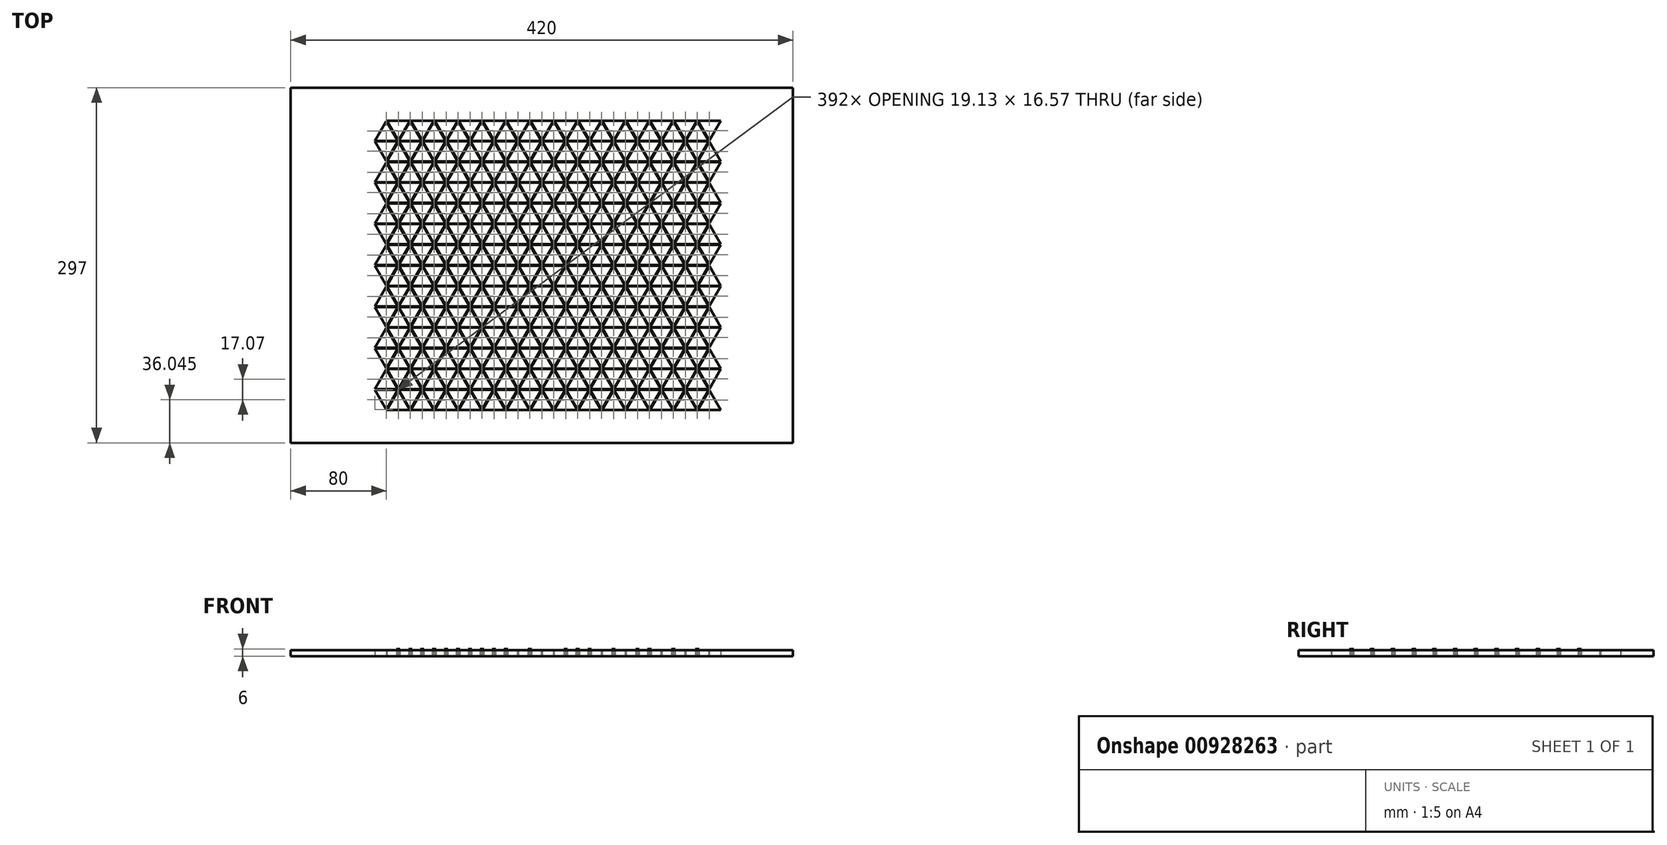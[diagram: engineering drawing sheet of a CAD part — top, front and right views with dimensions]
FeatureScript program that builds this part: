
annotation { "Feature Type Name" : "Feature", "Feature Type Description" : "" }
export const myFeature = defineFeature(function(context is Context, id is Id, definition is map)
    precondition{}
    {
        {
            var Q0;
            Q0=qCreatedBy(makeId("Top.planeOp"),FACE);
            var sketch = newSketch(context, id + "F0", { "sketchPlane" : qUnion([Q0])});
            skLineSegment(sketch, "E0", {"start": v(0, 0) * mm, "end": v(20, 0) * mm, "construction": true});
            skLineSegment(sketch, "E1", {"start": v(20, 0) * mm, "end": v(10, 17.32) * mm, "construction": true});
            skLineSegment(sketch, "E2", {"start": v(10, 17.32) * mm, "end": v(0, 0) * mm, "construction": true});
            skLineSegment(sketch, "E3.MirrorCS", {"start": v(10, -17.32) * mm, "end": v(0, 0) * mm, "construction": true});
            skLineSegment(sketch, "E4.MirrorCS", {"start": v(20, 0) * mm, "end": v(10, -17.32) * mm, "construction": true});
            skLineSegment(sketch, "E5.MirrorCS", {"start": v(30, -17.32) * mm, "end": v(20, 0) * mm, "construction": true});
            skLineSegment(sketch, "E6.MirrorCS", {"start": v(10, -17.32) * mm, "end": v(30, -17.32) * mm, "construction": true});
            skLineSegment(sketch, "E7.MirrorCS", {"start": v(30, 17.32) * mm, "end": v(20, 0) * mm, "construction": true});
            skLineSegment(sketch, "E8.MirrorCS", {"start": v(10, 17.32) * mm, "end": v(30, 17.32) * mm, "construction": true});
            skLineSegment(sketch, "E9.0.1.1", {"start": v(20, 34.64) * mm, "end": v(10, 17.32) * mm, "construction": true});
            skLineSegment(sketch, "E9.0.1.2", {"start": v(30, 17.32) * mm, "end": v(20, 34.64) * mm, "construction": true});
            skLineSegment(sketch, "E9.0.1.3", {"start": v(0, 34.64) * mm, "end": v(20, 34.64) * mm, "construction": true});
            skLineSegment(sketch, "E9.0.1.4", {"start": v(10, 17.32) * mm, "end": v(0, 34.64) * mm, "construction": true});
            skLineSegment(sketch, "E9.0.1.5", {"start": v(10, 51.96) * mm, "end": v(0, 34.64) * mm, "construction": true});
            skLineSegment(sketch, "E9.0.1.6", {"start": v(20, 34.64) * mm, "end": v(10, 51.96) * mm, "construction": true});
            skLineSegment(sketch, "E9.0.1.7", {"start": v(10, 51.96) * mm, "end": v(30, 51.96) * mm, "construction": true});
            skLineSegment(sketch, "E9.0.1.8", {"start": v(30, 51.96) * mm, "end": v(20, 34.64) * mm, "construction": true});
            skLineSegment(sketch, "E9.0.2.0", {"start": v(10, 51.96) * mm, "end": v(30, 51.96) * mm, "construction": true});
            skLineSegment(sketch, "E9.0.2.1", {"start": v(20, 69.28) * mm, "end": v(10, 51.96) * mm, "construction": true});
            skLineSegment(sketch, "E9.0.2.2", {"start": v(30, 51.96) * mm, "end": v(20, 69.28) * mm, "construction": true});
            skLineSegment(sketch, "E9.0.2.3", {"start": v(0, 69.28) * mm, "end": v(20, 69.28) * mm, "construction": true});
            skLineSegment(sketch, "E9.0.2.4", {"start": v(10, 51.96) * mm, "end": v(0, 69.28) * mm, "construction": true});
            skLineSegment(sketch, "E9.0.2.5", {"start": v(10, 86.6) * mm, "end": v(0, 69.28) * mm, "construction": true});
            skLineSegment(sketch, "E9.0.2.6", {"start": v(20, 69.28) * mm, "end": v(10, 86.6) * mm, "construction": true});
            skLineSegment(sketch, "E9.0.2.7", {"start": v(10, 86.6) * mm, "end": v(30, 86.6) * mm, "construction": true});
            skLineSegment(sketch, "E9.0.2.8", {"start": v(30, 86.6) * mm, "end": v(20, 69.28) * mm, "construction": true});
            skLineSegment(sketch, "E9.0.3.0", {"start": v(10, 86.6) * mm, "end": v(30, 86.6) * mm, "construction": true});
            skLineSegment(sketch, "E9.0.3.1", {"start": v(20, 103.92) * mm, "end": v(10, 86.6) * mm, "construction": true});
            skLineSegment(sketch, "E9.0.3.2", {"start": v(30, 86.6) * mm, "end": v(20, 103.92) * mm, "construction": true});
            skLineSegment(sketch, "E9.0.3.3", {"start": v(0, 103.92) * mm, "end": v(20, 103.92) * mm, "construction": true});
            skLineSegment(sketch, "E9.0.3.4", {"start": v(10, 86.6) * mm, "end": v(0, 103.92) * mm, "construction": true});
            skLineSegment(sketch, "E9.0.3.5", {"start": v(10, 121.24) * mm, "end": v(0, 103.92) * mm, "construction": true});
            skLineSegment(sketch, "E9.0.3.6", {"start": v(20, 103.92) * mm, "end": v(10, 121.24) * mm, "construction": true});
            skLineSegment(sketch, "E9.0.3.7", {"start": v(10, 121.24) * mm, "end": v(30, 121.24) * mm, "construction": true});
            skLineSegment(sketch, "E9.0.3.8", {"start": v(30, 121.24) * mm, "end": v(20, 103.92) * mm, "construction": true});
            skLineSegment(sketch, "E9.0.4.0", {"start": v(10, 121.24) * mm, "end": v(30, 121.24) * mm, "construction": true});
            skLineSegment(sketch, "E9.0.4.1", {"start": v(20, 138.56) * mm, "end": v(10, 121.24) * mm, "construction": true});
            skLineSegment(sketch, "E9.0.4.2", {"start": v(30, 121.24) * mm, "end": v(20, 138.56) * mm, "construction": true});
            skLineSegment(sketch, "E9.0.4.3", {"start": v(0, 138.56) * mm, "end": v(20, 138.56) * mm, "construction": true});
            skLineSegment(sketch, "E9.0.4.4", {"start": v(10, 121.24) * mm, "end": v(0, 138.56) * mm, "construction": true});
            skLineSegment(sketch, "E9.0.4.5", {"start": v(10, 155.88) * mm, "end": v(0, 138.56) * mm, "construction": true});
            skLineSegment(sketch, "E9.0.4.6", {"start": v(20, 138.56) * mm, "end": v(10, 155.88) * mm, "construction": true});
            skLineSegment(sketch, "E9.0.4.7", {"start": v(10, 155.88) * mm, "end": v(30, 155.88) * mm, "construction": true});
            skLineSegment(sketch, "E9.0.4.8", {"start": v(30, 155.88) * mm, "end": v(20, 138.56) * mm, "construction": true});
            skLineSegment(sketch, "E9.0.5.0", {"start": v(10, 155.88) * mm, "end": v(30, 155.88) * mm, "construction": true});
            skLineSegment(sketch, "E9.0.5.1", {"start": v(20, 173.2) * mm, "end": v(10, 155.88) * mm, "construction": true});
            skLineSegment(sketch, "E9.0.5.2", {"start": v(30, 155.88) * mm, "end": v(20, 173.2) * mm, "construction": true});
            skLineSegment(sketch, "E9.0.5.3", {"start": v(0, 173.2) * mm, "end": v(20, 173.2) * mm, "construction": true});
            skLineSegment(sketch, "E9.0.5.4", {"start": v(10, 155.88) * mm, "end": v(0, 173.2) * mm, "construction": true});
            skLineSegment(sketch, "E9.0.5.5", {"start": v(10, 190.53) * mm, "end": v(0, 173.2) * mm, "construction": true});
            skLineSegment(sketch, "E9.0.5.6", {"start": v(20, 173.2) * mm, "end": v(10, 190.53) * mm, "construction": true});
            skLineSegment(sketch, "E9.0.5.7", {"start": v(10, 190.53) * mm, "end": v(30, 190.53) * mm, "construction": true});
            skLineSegment(sketch, "E9.0.5.8", {"start": v(30, 190.53) * mm, "end": v(20, 173.2) * mm, "construction": true});
            skLineSegment(sketch, "E9.0.6.0", {"start": v(10, 190.53) * mm, "end": v(30, 190.53) * mm, "construction": true});
            skLineSegment(sketch, "E9.0.6.1", {"start": v(20, 207.85) * mm, "end": v(10, 190.53) * mm, "construction": true});
            skLineSegment(sketch, "E9.0.6.2", {"start": v(30, 190.53) * mm, "end": v(20, 207.85) * mm, "construction": true});
            skLineSegment(sketch, "E9.0.6.3", {"start": v(0, 207.85) * mm, "end": v(20, 207.85) * mm, "construction": true});
            skLineSegment(sketch, "E9.0.6.4", {"start": v(10, 190.53) * mm, "end": v(0, 207.85) * mm, "construction": true});
            skLineSegment(sketch, "E9.0.6.5", {"start": v(10, 225.17) * mm, "end": v(0, 207.85) * mm, "construction": true});
            skLineSegment(sketch, "E9.0.6.6", {"start": v(20, 207.85) * mm, "end": v(10, 225.17) * mm, "construction": true});
            skLineSegment(sketch, "E9.0.6.7", {"start": v(10, 225.17) * mm, "end": v(30, 225.17) * mm, "construction": true});
            skLineSegment(sketch, "E9.0.6.8", {"start": v(30, 225.17) * mm, "end": v(20, 207.85) * mm, "construction": true});
            skLineSegment(sketch, "E9.1.0.0", {"start": v(30, -17.32) * mm, "end": v(50, -17.32) * mm, "construction": true});
            skLineSegment(sketch, "E9.1.0.1", {"start": v(40, 0) * mm, "end": v(30, -17.32) * mm, "construction": true});
            skLineSegment(sketch, "E9.1.0.2", {"start": v(50, -17.32) * mm, "end": v(40, 0) * mm, "construction": true});
            skLineSegment(sketch, "E9.1.0.3", {"start": v(20, 0) * mm, "end": v(40, 0) * mm, "construction": true});
            skLineSegment(sketch, "E9.1.0.6", {"start": v(40, 0) * mm, "end": v(30, 17.32) * mm, "construction": true});
            skLineSegment(sketch, "E9.1.0.7", {"start": v(30, 17.32) * mm, "end": v(50, 17.32) * mm, "construction": true});
            skLineSegment(sketch, "E9.1.0.8", {"start": v(50, 17.32) * mm, "end": v(40, 0) * mm, "construction": true});
            skLineSegment(sketch, "E9.1.1.0", {"start": v(30, 17.32) * mm, "end": v(50, 17.32) * mm, "construction": true});
            skLineSegment(sketch, "E9.1.1.1", {"start": v(40, 34.64) * mm, "end": v(30, 17.32) * mm, "construction": true});
            skLineSegment(sketch, "E9.1.1.2", {"start": v(50, 17.32) * mm, "end": v(40, 34.64) * mm, "construction": true});
            skLineSegment(sketch, "E9.1.1.3", {"start": v(20, 34.64) * mm, "end": v(40, 34.64) * mm, "construction": true});
            skLineSegment(sketch, "E9.1.1.4", {"start": v(30, 17.32) * mm, "end": v(20, 34.64) * mm, "construction": true});
            skLineSegment(sketch, "E9.1.1.5", {"start": v(30, 51.96) * mm, "end": v(20, 34.64) * mm, "construction": true});
            skLineSegment(sketch, "E9.1.1.6", {"start": v(40, 34.64) * mm, "end": v(30, 51.96) * mm, "construction": true});
            skLineSegment(sketch, "E9.1.1.7", {"start": v(30, 51.96) * mm, "end": v(50, 51.96) * mm, "construction": true});
            skLineSegment(sketch, "E9.1.1.8", {"start": v(50, 51.96) * mm, "end": v(40, 34.64) * mm, "construction": true});
            skLineSegment(sketch, "E9.1.2.0", {"start": v(30, 51.96) * mm, "end": v(50, 51.96) * mm, "construction": true});
            skLineSegment(sketch, "E9.1.2.1", {"start": v(40, 69.28) * mm, "end": v(30, 51.96) * mm, "construction": true});
            skLineSegment(sketch, "E9.1.2.2", {"start": v(50, 51.96) * mm, "end": v(40, 69.28) * mm, "construction": true});
            skLineSegment(sketch, "E9.1.2.3", {"start": v(20, 69.28) * mm, "end": v(40, 69.28) * mm, "construction": true});
            skLineSegment(sketch, "E9.1.2.4", {"start": v(30, 51.96) * mm, "end": v(20, 69.28) * mm, "construction": true});
            skLineSegment(sketch, "E9.1.2.5", {"start": v(30, 86.6) * mm, "end": v(20, 69.28) * mm, "construction": true});
            skLineSegment(sketch, "E9.1.2.6", {"start": v(40, 69.28) * mm, "end": v(30, 86.6) * mm, "construction": true});
            skLineSegment(sketch, "E9.1.2.7", {"start": v(30, 86.6) * mm, "end": v(50, 86.6) * mm, "construction": true});
            skLineSegment(sketch, "E9.1.2.8", {"start": v(50, 86.6) * mm, "end": v(40, 69.28) * mm, "construction": true});
            skLineSegment(sketch, "E9.1.3.0", {"start": v(30, 86.6) * mm, "end": v(50, 86.6) * mm, "construction": true});
            skLineSegment(sketch, "E9.1.3.1", {"start": v(40, 103.92) * mm, "end": v(30, 86.6) * mm, "construction": true});
            skLineSegment(sketch, "E9.1.3.2", {"start": v(50, 86.6) * mm, "end": v(40, 103.92) * mm, "construction": true});
            skLineSegment(sketch, "E9.1.3.3", {"start": v(20, 103.92) * mm, "end": v(40, 103.92) * mm, "construction": true});
            skLineSegment(sketch, "E9.1.3.4", {"start": v(30, 86.6) * mm, "end": v(20, 103.92) * mm, "construction": true});
            skLineSegment(sketch, "E9.1.3.5", {"start": v(30, 121.24) * mm, "end": v(20, 103.92) * mm, "construction": true});
            skLineSegment(sketch, "E9.1.3.6", {"start": v(40, 103.92) * mm, "end": v(30, 121.24) * mm, "construction": true});
            skLineSegment(sketch, "E9.1.3.7", {"start": v(30, 121.24) * mm, "end": v(50, 121.24) * mm, "construction": true});
            skLineSegment(sketch, "E9.1.3.8", {"start": v(50, 121.24) * mm, "end": v(40, 103.92) * mm, "construction": true});
            skLineSegment(sketch, "E9.1.4.0", {"start": v(30, 121.24) * mm, "end": v(50, 121.24) * mm, "construction": true});
            skLineSegment(sketch, "E9.1.4.1", {"start": v(40, 138.56) * mm, "end": v(30, 121.24) * mm, "construction": true});
            skLineSegment(sketch, "E9.1.4.2", {"start": v(50, 121.24) * mm, "end": v(40, 138.56) * mm, "construction": true});
            skLineSegment(sketch, "E9.1.4.3", {"start": v(20, 138.56) * mm, "end": v(40, 138.56) * mm, "construction": true});
            skLineSegment(sketch, "E9.1.4.4", {"start": v(30, 121.24) * mm, "end": v(20, 138.56) * mm, "construction": true});
            skLineSegment(sketch, "E9.1.4.5", {"start": v(30, 155.88) * mm, "end": v(20, 138.56) * mm, "construction": true});
            skLineSegment(sketch, "E9.1.4.6", {"start": v(40, 138.56) * mm, "end": v(30, 155.88) * mm, "construction": true});
            skLineSegment(sketch, "E9.1.4.7", {"start": v(30, 155.88) * mm, "end": v(50, 155.88) * mm, "construction": true});
            skLineSegment(sketch, "E9.1.4.8", {"start": v(50, 155.88) * mm, "end": v(40, 138.56) * mm, "construction": true});
            skLineSegment(sketch, "E9.1.5.0", {"start": v(30, 155.88) * mm, "end": v(50, 155.88) * mm, "construction": true});
            skLineSegment(sketch, "E9.1.5.1", {"start": v(40, 173.2) * mm, "end": v(30, 155.88) * mm, "construction": true});
            skLineSegment(sketch, "E9.1.5.2", {"start": v(50, 155.88) * mm, "end": v(40, 173.2) * mm, "construction": true});
            skLineSegment(sketch, "E9.1.5.3", {"start": v(20, 173.2) * mm, "end": v(40, 173.2) * mm, "construction": true});
            skLineSegment(sketch, "E9.1.5.4", {"start": v(30, 155.88) * mm, "end": v(20, 173.2) * mm, "construction": true});
            skLineSegment(sketch, "E9.1.5.5", {"start": v(30, 190.53) * mm, "end": v(20, 173.2) * mm, "construction": true});
            skLineSegment(sketch, "E9.1.5.6", {"start": v(40, 173.2) * mm, "end": v(30, 190.53) * mm, "construction": true});
            skLineSegment(sketch, "E9.1.5.7", {"start": v(30, 190.53) * mm, "end": v(50, 190.53) * mm, "construction": true});
            skLineSegment(sketch, "E9.1.5.8", {"start": v(50, 190.53) * mm, "end": v(40, 173.2) * mm, "construction": true});
            skLineSegment(sketch, "E9.1.6.0", {"start": v(30, 190.53) * mm, "end": v(50, 190.53) * mm, "construction": true});
            skLineSegment(sketch, "E9.1.6.1", {"start": v(40, 207.85) * mm, "end": v(30, 190.53) * mm, "construction": true});
            skLineSegment(sketch, "E9.1.6.2", {"start": v(50, 190.53) * mm, "end": v(40, 207.85) * mm, "construction": true});
            skLineSegment(sketch, "E9.1.6.3", {"start": v(20, 207.85) * mm, "end": v(40, 207.85) * mm, "construction": true});
            skLineSegment(sketch, "E9.1.6.4", {"start": v(30, 190.53) * mm, "end": v(20, 207.85) * mm, "construction": true});
            skLineSegment(sketch, "E9.1.6.5", {"start": v(30, 225.17) * mm, "end": v(20, 207.85) * mm, "construction": true});
            skLineSegment(sketch, "E9.1.6.6", {"start": v(40, 207.85) * mm, "end": v(30, 225.17) * mm, "construction": true});
            skLineSegment(sketch, "E9.1.6.7", {"start": v(30, 225.17) * mm, "end": v(50, 225.17) * mm, "construction": true});
            skLineSegment(sketch, "E9.1.6.8", {"start": v(50, 225.17) * mm, "end": v(40, 207.85) * mm, "construction": true});
            skLineSegment(sketch, "E9.2.0.0", {"start": v(50, -17.32) * mm, "end": v(70, -17.32) * mm, "construction": true});
            skLineSegment(sketch, "E9.2.0.1", {"start": v(60, 0) * mm, "end": v(50, -17.32) * mm, "construction": true});
            skLineSegment(sketch, "E9.2.0.2", {"start": v(70, -17.32) * mm, "end": v(60, 0) * mm, "construction": true});
            skLineSegment(sketch, "E9.2.0.3", {"start": v(40, 0) * mm, "end": v(60, 0) * mm, "construction": true});
            skLineSegment(sketch, "E9.2.0.4", {"start": v(50, -17.32) * mm, "end": v(40, 0) * mm, "construction": true});
            skLineSegment(sketch, "E9.2.0.5", {"start": v(50, 17.32) * mm, "end": v(40, 0) * mm, "construction": true});
            skLineSegment(sketch, "E9.2.0.6", {"start": v(60, 0) * mm, "end": v(50, 17.32) * mm, "construction": true});
            skLineSegment(sketch, "E9.2.0.7", {"start": v(50, 17.32) * mm, "end": v(70, 17.32) * mm, "construction": true});
            skLineSegment(sketch, "E9.2.0.8", {"start": v(70, 17.32) * mm, "end": v(60, 0) * mm, "construction": true});
            skLineSegment(sketch, "E9.2.1.0", {"start": v(50, 17.32) * mm, "end": v(70, 17.32) * mm, "construction": true});
            skLineSegment(sketch, "E9.2.1.1", {"start": v(60, 34.64) * mm, "end": v(50, 17.32) * mm, "construction": true});
            skLineSegment(sketch, "E9.2.1.2", {"start": v(70, 17.32) * mm, "end": v(60, 34.64) * mm, "construction": true});
            skLineSegment(sketch, "E9.2.1.3", {"start": v(40, 34.64) * mm, "end": v(60, 34.64) * mm, "construction": true});
            skLineSegment(sketch, "E9.2.1.4", {"start": v(50, 17.32) * mm, "end": v(40, 34.64) * mm, "construction": true});
            skLineSegment(sketch, "E9.2.1.5", {"start": v(50, 51.96) * mm, "end": v(40, 34.64) * mm, "construction": true});
            skLineSegment(sketch, "E9.2.1.6", {"start": v(60, 34.64) * mm, "end": v(50, 51.96) * mm, "construction": true});
            skLineSegment(sketch, "E9.2.1.7", {"start": v(50, 51.96) * mm, "end": v(70, 51.96) * mm, "construction": true});
            skLineSegment(sketch, "E9.2.1.8", {"start": v(70, 51.96) * mm, "end": v(60, 34.64) * mm, "construction": true});
            skLineSegment(sketch, "E9.2.2.0", {"start": v(50, 51.96) * mm, "end": v(70, 51.96) * mm, "construction": true});
            skLineSegment(sketch, "E9.2.2.1", {"start": v(60, 69.28) * mm, "end": v(50, 51.96) * mm, "construction": true});
            skLineSegment(sketch, "E9.2.2.2", {"start": v(70, 51.96) * mm, "end": v(60, 69.28) * mm, "construction": true});
            skLineSegment(sketch, "E9.2.2.3", {"start": v(40, 69.28) * mm, "end": v(60, 69.28) * mm, "construction": true});
            skLineSegment(sketch, "E9.2.2.4", {"start": v(50, 51.96) * mm, "end": v(40, 69.28) * mm, "construction": true});
            skLineSegment(sketch, "E9.2.2.5", {"start": v(50, 86.6) * mm, "end": v(40, 69.28) * mm, "construction": true});
            skLineSegment(sketch, "E9.2.2.6", {"start": v(60, 69.28) * mm, "end": v(50, 86.6) * mm, "construction": true});
            skLineSegment(sketch, "E9.2.2.7", {"start": v(50, 86.6) * mm, "end": v(70, 86.6) * mm, "construction": true});
            skLineSegment(sketch, "E9.2.2.8", {"start": v(70, 86.6) * mm, "end": v(60, 69.28) * mm, "construction": true});
            skLineSegment(sketch, "E9.2.3.0", {"start": v(50, 86.6) * mm, "end": v(70, 86.6) * mm, "construction": true});
            skLineSegment(sketch, "E9.2.3.1", {"start": v(60, 103.92) * mm, "end": v(50, 86.6) * mm, "construction": true});
            skLineSegment(sketch, "E9.2.3.2", {"start": v(70, 86.6) * mm, "end": v(60, 103.92) * mm, "construction": true});
            skLineSegment(sketch, "E9.2.3.3", {"start": v(40, 103.92) * mm, "end": v(60, 103.92) * mm, "construction": true});
            skLineSegment(sketch, "E9.2.3.4", {"start": v(50, 86.6) * mm, "end": v(40, 103.92) * mm, "construction": true});
            skLineSegment(sketch, "E9.2.3.5", {"start": v(50, 121.24) * mm, "end": v(40, 103.92) * mm, "construction": true});
            skLineSegment(sketch, "E9.2.3.6", {"start": v(60, 103.92) * mm, "end": v(50, 121.24) * mm, "construction": true});
            skLineSegment(sketch, "E9.2.3.7", {"start": v(50, 121.24) * mm, "end": v(70, 121.24) * mm, "construction": true});
            skLineSegment(sketch, "E9.2.3.8", {"start": v(70, 121.24) * mm, "end": v(60, 103.92) * mm, "construction": true});
            skLineSegment(sketch, "E9.2.4.0", {"start": v(50, 121.24) * mm, "end": v(70, 121.24) * mm, "construction": true});
            skLineSegment(sketch, "E9.2.4.1", {"start": v(60, 138.56) * mm, "end": v(50, 121.24) * mm, "construction": true});
            skLineSegment(sketch, "E9.2.4.2", {"start": v(70, 121.24) * mm, "end": v(60, 138.56) * mm, "construction": true});
            skLineSegment(sketch, "E9.2.4.3", {"start": v(40, 138.56) * mm, "end": v(60, 138.56) * mm, "construction": true});
            skLineSegment(sketch, "E9.2.4.4", {"start": v(50, 121.24) * mm, "end": v(40, 138.56) * mm, "construction": true});
            skLineSegment(sketch, "E9.2.4.5", {"start": v(50, 155.88) * mm, "end": v(40, 138.56) * mm, "construction": true});
            skLineSegment(sketch, "E9.2.4.6", {"start": v(60, 138.56) * mm, "end": v(50, 155.88) * mm, "construction": true});
            skLineSegment(sketch, "E9.2.4.7", {"start": v(50, 155.88) * mm, "end": v(70, 155.88) * mm, "construction": true});
            skLineSegment(sketch, "E9.2.4.8", {"start": v(70, 155.88) * mm, "end": v(60, 138.56) * mm, "construction": true});
            skLineSegment(sketch, "E9.2.5.0", {"start": v(50, 155.88) * mm, "end": v(70, 155.88) * mm, "construction": true});
            skLineSegment(sketch, "E9.2.5.1", {"start": v(60, 173.2) * mm, "end": v(50, 155.88) * mm, "construction": true});
            skLineSegment(sketch, "E9.2.5.2", {"start": v(70, 155.88) * mm, "end": v(60, 173.2) * mm, "construction": true});
            skLineSegment(sketch, "E9.2.5.3", {"start": v(40, 173.2) * mm, "end": v(60, 173.2) * mm, "construction": true});
            skLineSegment(sketch, "E9.2.5.4", {"start": v(50, 155.88) * mm, "end": v(40, 173.2) * mm, "construction": true});
            skLineSegment(sketch, "E9.2.5.5", {"start": v(50, 190.53) * mm, "end": v(40, 173.2) * mm, "construction": true});
            skLineSegment(sketch, "E9.2.5.6", {"start": v(60, 173.2) * mm, "end": v(50, 190.53) * mm, "construction": true});
            skLineSegment(sketch, "E9.2.5.7", {"start": v(50, 190.53) * mm, "end": v(70, 190.53) * mm, "construction": true});
            skLineSegment(sketch, "E9.2.5.8", {"start": v(70, 190.53) * mm, "end": v(60, 173.2) * mm, "construction": true});
            skLineSegment(sketch, "E9.2.6.0", {"start": v(50, 190.53) * mm, "end": v(70, 190.53) * mm, "construction": true});
            skLineSegment(sketch, "E9.2.6.1", {"start": v(60, 207.85) * mm, "end": v(50, 190.53) * mm, "construction": true});
            skLineSegment(sketch, "E9.2.6.2", {"start": v(70, 190.53) * mm, "end": v(60, 207.85) * mm, "construction": true});
            skLineSegment(sketch, "E9.2.6.3", {"start": v(40, 207.85) * mm, "end": v(60, 207.85) * mm, "construction": true});
            skLineSegment(sketch, "E9.2.6.4", {"start": v(50, 190.53) * mm, "end": v(40, 207.85) * mm, "construction": true});
            skLineSegment(sketch, "E9.2.6.5", {"start": v(50, 225.17) * mm, "end": v(40, 207.85) * mm, "construction": true});
            skLineSegment(sketch, "E9.2.6.6", {"start": v(60, 207.85) * mm, "end": v(50, 225.17) * mm, "construction": true});
            skLineSegment(sketch, "E9.2.6.7", {"start": v(50, 225.17) * mm, "end": v(70, 225.17) * mm, "construction": true});
            skLineSegment(sketch, "E9.2.6.8", {"start": v(70, 225.17) * mm, "end": v(60, 207.85) * mm, "construction": true});
            skLineSegment(sketch, "E9.3.0.0", {"start": v(70, -17.32) * mm, "end": v(90, -17.32) * mm, "construction": true});
            skLineSegment(sketch, "E9.3.0.1", {"start": v(80, 0) * mm, "end": v(70, -17.32) * mm, "construction": true});
            skLineSegment(sketch, "E9.3.0.2", {"start": v(90, -17.32) * mm, "end": v(80, 0) * mm, "construction": true});
            skLineSegment(sketch, "E9.3.0.3", {"start": v(60, 0) * mm, "end": v(80, 0) * mm, "construction": true});
            skLineSegment(sketch, "E9.3.0.4", {"start": v(70, -17.32) * mm, "end": v(60, 0) * mm, "construction": true});
            skLineSegment(sketch, "E9.3.0.5", {"start": v(70, 17.32) * mm, "end": v(60, 0) * mm, "construction": true});
            skLineSegment(sketch, "E9.3.0.6", {"start": v(80, 0) * mm, "end": v(70, 17.32) * mm, "construction": true});
            skLineSegment(sketch, "E9.3.0.7", {"start": v(70, 17.32) * mm, "end": v(90, 17.32) * mm, "construction": true});
            skLineSegment(sketch, "E9.3.0.8", {"start": v(90, 17.32) * mm, "end": v(80, 0) * mm, "construction": true});
            skLineSegment(sketch, "E9.3.1.0", {"start": v(70, 17.32) * mm, "end": v(90, 17.32) * mm, "construction": true});
            skLineSegment(sketch, "E9.3.1.1", {"start": v(80, 34.64) * mm, "end": v(70, 17.32) * mm, "construction": true});
            skLineSegment(sketch, "E9.3.1.2", {"start": v(90, 17.32) * mm, "end": v(80, 34.64) * mm, "construction": true});
            skLineSegment(sketch, "E9.3.1.3", {"start": v(60, 34.64) * mm, "end": v(80, 34.64) * mm, "construction": true});
            skLineSegment(sketch, "E9.3.1.4", {"start": v(70, 17.32) * mm, "end": v(60, 34.64) * mm, "construction": true});
            skLineSegment(sketch, "E9.3.1.5", {"start": v(70, 51.96) * mm, "end": v(60, 34.64) * mm, "construction": true});
            skLineSegment(sketch, "E9.3.1.6", {"start": v(80, 34.64) * mm, "end": v(70, 51.96) * mm, "construction": true});
            skLineSegment(sketch, "E9.3.1.7", {"start": v(70, 51.96) * mm, "end": v(90, 51.96) * mm, "construction": true});
            skLineSegment(sketch, "E9.3.1.8", {"start": v(90, 51.96) * mm, "end": v(80, 34.64) * mm, "construction": true});
            skLineSegment(sketch, "E9.3.2.0", {"start": v(70, 51.96) * mm, "end": v(90, 51.96) * mm, "construction": true});
            skLineSegment(sketch, "E9.3.2.1", {"start": v(80, 69.28) * mm, "end": v(70, 51.96) * mm, "construction": true});
            skLineSegment(sketch, "E9.3.2.2", {"start": v(90, 51.96) * mm, "end": v(80, 69.28) * mm, "construction": true});
            skLineSegment(sketch, "E9.3.2.3", {"start": v(60, 69.28) * mm, "end": v(80, 69.28) * mm, "construction": true});
            skLineSegment(sketch, "E9.3.2.4", {"start": v(70, 51.96) * mm, "end": v(60, 69.28) * mm, "construction": true});
            skLineSegment(sketch, "E9.3.2.5", {"start": v(70, 86.6) * mm, "end": v(60, 69.28) * mm, "construction": true});
            skLineSegment(sketch, "E9.3.2.6", {"start": v(80, 69.28) * mm, "end": v(70, 86.6) * mm, "construction": true});
            skLineSegment(sketch, "E9.3.2.7", {"start": v(70, 86.6) * mm, "end": v(90, 86.6) * mm, "construction": true});
            skLineSegment(sketch, "E9.3.2.8", {"start": v(90, 86.6) * mm, "end": v(80, 69.28) * mm, "construction": true});
            skLineSegment(sketch, "E9.3.3.0", {"start": v(70, 86.6) * mm, "end": v(90, 86.6) * mm, "construction": true});
            skLineSegment(sketch, "E9.3.3.1", {"start": v(80, 103.92) * mm, "end": v(70, 86.6) * mm, "construction": true});
            skLineSegment(sketch, "E9.3.3.2", {"start": v(90, 86.6) * mm, "end": v(80, 103.92) * mm, "construction": true});
            skLineSegment(sketch, "E9.3.3.3", {"start": v(60, 103.92) * mm, "end": v(80, 103.92) * mm, "construction": true});
            skLineSegment(sketch, "E9.3.3.4", {"start": v(70, 86.6) * mm, "end": v(60, 103.92) * mm, "construction": true});
            skLineSegment(sketch, "E9.3.3.5", {"start": v(70, 121.24) * mm, "end": v(60, 103.92) * mm, "construction": true});
            skLineSegment(sketch, "E9.3.3.6", {"start": v(80, 103.92) * mm, "end": v(70, 121.24) * mm, "construction": true});
            skLineSegment(sketch, "E9.3.3.7", {"start": v(70, 121.24) * mm, "end": v(90, 121.24) * mm, "construction": true});
            skLineSegment(sketch, "E9.3.3.8", {"start": v(90, 121.24) * mm, "end": v(80, 103.92) * mm, "construction": true});
            skLineSegment(sketch, "E9.3.4.0", {"start": v(70, 121.24) * mm, "end": v(90, 121.24) * mm, "construction": true});
            skLineSegment(sketch, "E9.3.4.1", {"start": v(80, 138.56) * mm, "end": v(70, 121.24) * mm, "construction": true});
            skLineSegment(sketch, "E9.3.4.2", {"start": v(90, 121.24) * mm, "end": v(80, 138.56) * mm, "construction": true});
            skLineSegment(sketch, "E9.3.4.3", {"start": v(60, 138.56) * mm, "end": v(80, 138.56) * mm, "construction": true});
            skLineSegment(sketch, "E9.3.4.4", {"start": v(70, 121.24) * mm, "end": v(60, 138.56) * mm, "construction": true});
            skLineSegment(sketch, "E9.3.4.5", {"start": v(70, 155.88) * mm, "end": v(60, 138.56) * mm, "construction": true});
            skLineSegment(sketch, "E9.3.4.6", {"start": v(80, 138.56) * mm, "end": v(70, 155.88) * mm, "construction": true});
            skLineSegment(sketch, "E9.3.4.7", {"start": v(70, 155.88) * mm, "end": v(90, 155.88) * mm, "construction": true});
            skLineSegment(sketch, "E9.3.4.8", {"start": v(90, 155.88) * mm, "end": v(80, 138.56) * mm, "construction": true});
            skLineSegment(sketch, "E9.3.5.0", {"start": v(70, 155.88) * mm, "end": v(90, 155.88) * mm, "construction": true});
            skLineSegment(sketch, "E9.3.5.1", {"start": v(80, 173.2) * mm, "end": v(70, 155.88) * mm, "construction": true});
            skLineSegment(sketch, "E9.3.5.2", {"start": v(90, 155.88) * mm, "end": v(80, 173.2) * mm, "construction": true});
            skLineSegment(sketch, "E9.3.5.3", {"start": v(60, 173.2) * mm, "end": v(80, 173.2) * mm, "construction": true});
            skLineSegment(sketch, "E9.3.5.4", {"start": v(70, 155.88) * mm, "end": v(60, 173.2) * mm, "construction": true});
            skLineSegment(sketch, "E9.3.5.5", {"start": v(70, 190.53) * mm, "end": v(60, 173.2) * mm, "construction": true});
            skLineSegment(sketch, "E9.3.5.6", {"start": v(80, 173.2) * mm, "end": v(70, 190.53) * mm, "construction": true});
            skLineSegment(sketch, "E9.3.5.7", {"start": v(70, 190.53) * mm, "end": v(90, 190.53) * mm, "construction": true});
            skLineSegment(sketch, "E9.3.5.8", {"start": v(90, 190.53) * mm, "end": v(80, 173.2) * mm, "construction": true});
            skLineSegment(sketch, "E9.3.6.0", {"start": v(70, 190.53) * mm, "end": v(90, 190.53) * mm, "construction": true});
            skLineSegment(sketch, "E9.3.6.1", {"start": v(80, 207.85) * mm, "end": v(70, 190.53) * mm, "construction": true});
            skLineSegment(sketch, "E9.3.6.2", {"start": v(90, 190.53) * mm, "end": v(80, 207.85) * mm, "construction": true});
            skLineSegment(sketch, "E9.3.6.3", {"start": v(60, 207.85) * mm, "end": v(80, 207.85) * mm, "construction": true});
            skLineSegment(sketch, "E9.3.6.4", {"start": v(70, 190.53) * mm, "end": v(60, 207.85) * mm, "construction": true});
            skLineSegment(sketch, "E9.3.6.5", {"start": v(70, 225.17) * mm, "end": v(60, 207.85) * mm, "construction": true});
            skLineSegment(sketch, "E9.3.6.6", {"start": v(80, 207.85) * mm, "end": v(70, 225.17) * mm, "construction": true});
            skLineSegment(sketch, "E9.3.6.7", {"start": v(70, 225.17) * mm, "end": v(90, 225.17) * mm, "construction": true});
            skLineSegment(sketch, "E9.3.6.8", {"start": v(90, 225.17) * mm, "end": v(80, 207.85) * mm, "construction": true});
            skLineSegment(sketch, "E9.4.0.0", {"start": v(90, -17.32) * mm, "end": v(110, -17.32) * mm, "construction": true});
            skLineSegment(sketch, "E9.4.0.1", {"start": v(100, 0) * mm, "end": v(90, -17.32) * mm, "construction": true});
            skLineSegment(sketch, "E9.4.0.2", {"start": v(110, -17.32) * mm, "end": v(100, 0) * mm, "construction": true});
            skLineSegment(sketch, "E9.4.0.3", {"start": v(80, 0) * mm, "end": v(100, 0) * mm, "construction": true});
            skLineSegment(sketch, "E9.4.0.4", {"start": v(90, -17.32) * mm, "end": v(80, 0) * mm, "construction": true});
            skLineSegment(sketch, "E9.4.0.5", {"start": v(90, 17.32) * mm, "end": v(80, 0) * mm, "construction": true});
            skLineSegment(sketch, "E9.4.0.6", {"start": v(100, 0) * mm, "end": v(90, 17.32) * mm, "construction": true});
            skLineSegment(sketch, "E9.4.0.7", {"start": v(90, 17.32) * mm, "end": v(110, 17.32) * mm, "construction": true});
            skLineSegment(sketch, "E9.4.0.8", {"start": v(110, 17.32) * mm, "end": v(100, 0) * mm, "construction": true});
            skLineSegment(sketch, "E9.4.1.0", {"start": v(90, 17.32) * mm, "end": v(110, 17.32) * mm, "construction": true});
            skLineSegment(sketch, "E9.4.1.1", {"start": v(100, 34.64) * mm, "end": v(90, 17.32) * mm, "construction": true});
            skLineSegment(sketch, "E9.4.1.2", {"start": v(110, 17.32) * mm, "end": v(100, 34.64) * mm, "construction": true});
            skLineSegment(sketch, "E9.4.1.3", {"start": v(80, 34.64) * mm, "end": v(100, 34.64) * mm, "construction": true});
            skLineSegment(sketch, "E9.4.1.4", {"start": v(90, 17.32) * mm, "end": v(80, 34.64) * mm, "construction": true});
            skLineSegment(sketch, "E9.4.1.5", {"start": v(90, 51.96) * mm, "end": v(80, 34.64) * mm, "construction": true});
            skLineSegment(sketch, "E9.4.1.6", {"start": v(100, 34.64) * mm, "end": v(90, 51.96) * mm, "construction": true});
            skLineSegment(sketch, "E9.4.1.7", {"start": v(90, 51.96) * mm, "end": v(110, 51.96) * mm, "construction": true});
            skLineSegment(sketch, "E9.4.1.8", {"start": v(110, 51.96) * mm, "end": v(100, 34.64) * mm, "construction": true});
            skLineSegment(sketch, "E9.4.2.0", {"start": v(90, 51.96) * mm, "end": v(110, 51.96) * mm, "construction": true});
            skLineSegment(sketch, "E9.4.2.1", {"start": v(100, 69.28) * mm, "end": v(90, 51.96) * mm, "construction": true});
            skLineSegment(sketch, "E9.4.2.2", {"start": v(110, 51.96) * mm, "end": v(100, 69.28) * mm, "construction": true});
            skLineSegment(sketch, "E9.4.2.3", {"start": v(80, 69.28) * mm, "end": v(100, 69.28) * mm, "construction": true});
            skLineSegment(sketch, "E9.4.2.4", {"start": v(90, 51.96) * mm, "end": v(80, 69.28) * mm, "construction": true});
            skLineSegment(sketch, "E9.4.2.5", {"start": v(90, 86.6) * mm, "end": v(80, 69.28) * mm, "construction": true});
            skLineSegment(sketch, "E9.4.2.6", {"start": v(100, 69.28) * mm, "end": v(90, 86.6) * mm, "construction": true});
            skLineSegment(sketch, "E9.4.2.7", {"start": v(90, 86.6) * mm, "end": v(110, 86.6) * mm, "construction": true});
            skLineSegment(sketch, "E9.4.2.8", {"start": v(110, 86.6) * mm, "end": v(100, 69.28) * mm, "construction": true});
            skLineSegment(sketch, "E9.4.3.0", {"start": v(90, 86.6) * mm, "end": v(110, 86.6) * mm, "construction": true});
            skLineSegment(sketch, "E9.4.3.1", {"start": v(100, 103.92) * mm, "end": v(90, 86.6) * mm, "construction": true});
            skLineSegment(sketch, "E9.4.3.2", {"start": v(110, 86.6) * mm, "end": v(100, 103.92) * mm, "construction": true});
            skLineSegment(sketch, "E9.4.3.3", {"start": v(80, 103.92) * mm, "end": v(100, 103.92) * mm, "construction": true});
            skLineSegment(sketch, "E9.4.3.4", {"start": v(90, 86.6) * mm, "end": v(80, 103.92) * mm, "construction": true});
            skLineSegment(sketch, "E9.4.3.5", {"start": v(90, 121.24) * mm, "end": v(80, 103.92) * mm, "construction": true});
            skLineSegment(sketch, "E9.4.3.6", {"start": v(100, 103.92) * mm, "end": v(90, 121.24) * mm, "construction": true});
            skLineSegment(sketch, "E9.4.3.7", {"start": v(90, 121.24) * mm, "end": v(110, 121.24) * mm, "construction": true});
            skLineSegment(sketch, "E9.4.3.8", {"start": v(110, 121.24) * mm, "end": v(100, 103.92) * mm, "construction": true});
            skLineSegment(sketch, "E9.4.4.0", {"start": v(90, 121.24) * mm, "end": v(110, 121.24) * mm, "construction": true});
            skLineSegment(sketch, "E9.4.4.1", {"start": v(100, 138.56) * mm, "end": v(90, 121.24) * mm, "construction": true});
            skLineSegment(sketch, "E9.4.4.2", {"start": v(110, 121.24) * mm, "end": v(100, 138.56) * mm, "construction": true});
            skLineSegment(sketch, "E9.4.4.3", {"start": v(80, 138.56) * mm, "end": v(100, 138.56) * mm, "construction": true});
            skLineSegment(sketch, "E9.4.4.4", {"start": v(90, 121.24) * mm, "end": v(80, 138.56) * mm, "construction": true});
            skLineSegment(sketch, "E9.4.4.5", {"start": v(90, 155.88) * mm, "end": v(80, 138.56) * mm, "construction": true});
            skLineSegment(sketch, "E9.4.4.6", {"start": v(100, 138.56) * mm, "end": v(90, 155.88) * mm, "construction": true});
            skLineSegment(sketch, "E9.4.4.7", {"start": v(90, 155.88) * mm, "end": v(110, 155.88) * mm, "construction": true});
            skLineSegment(sketch, "E9.4.4.8", {"start": v(110, 155.88) * mm, "end": v(100, 138.56) * mm, "construction": true});
            skLineSegment(sketch, "E9.4.5.0", {"start": v(90, 155.88) * mm, "end": v(110, 155.88) * mm, "construction": true});
            skLineSegment(sketch, "E9.4.5.1", {"start": v(100, 173.2) * mm, "end": v(90, 155.88) * mm, "construction": true});
            skLineSegment(sketch, "E9.4.5.2", {"start": v(110, 155.88) * mm, "end": v(100, 173.2) * mm, "construction": true});
            skLineSegment(sketch, "E9.4.5.3", {"start": v(80, 173.2) * mm, "end": v(100, 173.2) * mm, "construction": true});
            skLineSegment(sketch, "E9.4.5.4", {"start": v(90, 155.88) * mm, "end": v(80, 173.2) * mm, "construction": true});
            skLineSegment(sketch, "E9.4.5.5", {"start": v(90, 190.53) * mm, "end": v(80, 173.2) * mm, "construction": true});
            skLineSegment(sketch, "E9.4.5.6", {"start": v(100, 173.2) * mm, "end": v(90, 190.53) * mm, "construction": true});
            skLineSegment(sketch, "E9.4.5.7", {"start": v(90, 190.53) * mm, "end": v(110, 190.53) * mm, "construction": true});
            skLineSegment(sketch, "E9.4.5.8", {"start": v(110, 190.53) * mm, "end": v(100, 173.2) * mm, "construction": true});
            skLineSegment(sketch, "E9.4.6.0", {"start": v(90, 190.53) * mm, "end": v(110, 190.53) * mm, "construction": true});
            skLineSegment(sketch, "E9.4.6.1", {"start": v(100, 207.85) * mm, "end": v(90, 190.53) * mm, "construction": true});
            skLineSegment(sketch, "E9.4.6.2", {"start": v(110, 190.53) * mm, "end": v(100, 207.85) * mm, "construction": true});
            skLineSegment(sketch, "E9.4.6.3", {"start": v(80, 207.85) * mm, "end": v(100, 207.85) * mm, "construction": true});
            skLineSegment(sketch, "E9.4.6.4", {"start": v(90, 190.53) * mm, "end": v(80, 207.85) * mm, "construction": true});
            skLineSegment(sketch, "E9.4.6.5", {"start": v(90, 225.17) * mm, "end": v(80, 207.85) * mm, "construction": true});
            skLineSegment(sketch, "E9.4.6.6", {"start": v(100, 207.85) * mm, "end": v(90, 225.17) * mm, "construction": true});
            skLineSegment(sketch, "E9.4.6.7", {"start": v(90, 225.17) * mm, "end": v(110, 225.17) * mm, "construction": true});
            skLineSegment(sketch, "E9.4.6.8", {"start": v(110, 225.17) * mm, "end": v(100, 207.85) * mm, "construction": true});
            skLineSegment(sketch, "E9.5.0.0", {"start": v(110, -17.32) * mm, "end": v(130, -17.32) * mm, "construction": true});
            skLineSegment(sketch, "E9.5.0.1", {"start": v(120, 0) * mm, "end": v(110, -17.32) * mm, "construction": true});
            skLineSegment(sketch, "E9.5.0.2", {"start": v(130, -17.32) * mm, "end": v(120, 0) * mm, "construction": true});
            skLineSegment(sketch, "E9.5.0.3", {"start": v(100, 0) * mm, "end": v(120, 0) * mm, "construction": true});
            skLineSegment(sketch, "E9.5.0.4", {"start": v(110, -17.32) * mm, "end": v(100, 0) * mm, "construction": true});
            skLineSegment(sketch, "E9.5.0.5", {"start": v(110, 17.32) * mm, "end": v(100, 0) * mm, "construction": true});
            skLineSegment(sketch, "E9.5.0.6", {"start": v(120, 0) * mm, "end": v(110, 17.32) * mm, "construction": true});
            skLineSegment(sketch, "E9.5.0.7", {"start": v(110, 17.32) * mm, "end": v(130, 17.32) * mm, "construction": true});
            skLineSegment(sketch, "E9.5.0.8", {"start": v(130, 17.32) * mm, "end": v(120, 0) * mm, "construction": true});
            skLineSegment(sketch, "E9.5.1.0", {"start": v(110, 17.32) * mm, "end": v(130, 17.32) * mm, "construction": true});
            skLineSegment(sketch, "E9.5.1.1", {"start": v(120, 34.64) * mm, "end": v(110, 17.32) * mm, "construction": true});
            skLineSegment(sketch, "E9.5.1.2", {"start": v(130, 17.32) * mm, "end": v(120, 34.64) * mm, "construction": true});
            skLineSegment(sketch, "E9.5.1.3", {"start": v(100, 34.64) * mm, "end": v(120, 34.64) * mm, "construction": true});
            skLineSegment(sketch, "E9.5.1.4", {"start": v(110, 17.32) * mm, "end": v(100, 34.64) * mm, "construction": true});
            skLineSegment(sketch, "E9.5.1.5", {"start": v(110, 51.96) * mm, "end": v(100, 34.64) * mm, "construction": true});
            skLineSegment(sketch, "E9.5.1.6", {"start": v(120, 34.64) * mm, "end": v(110, 51.96) * mm, "construction": true});
            skLineSegment(sketch, "E9.5.1.7", {"start": v(110, 51.96) * mm, "end": v(130, 51.96) * mm, "construction": true});
            skLineSegment(sketch, "E9.5.1.8", {"start": v(130, 51.96) * mm, "end": v(120, 34.64) * mm, "construction": true});
            skLineSegment(sketch, "E9.5.2.0", {"start": v(110, 51.96) * mm, "end": v(130, 51.96) * mm, "construction": true});
            skLineSegment(sketch, "E9.5.2.1", {"start": v(120, 69.28) * mm, "end": v(110, 51.96) * mm, "construction": true});
            skLineSegment(sketch, "E9.5.2.2", {"start": v(130, 51.96) * mm, "end": v(120, 69.28) * mm, "construction": true});
            skLineSegment(sketch, "E9.5.2.3", {"start": v(100, 69.28) * mm, "end": v(120, 69.28) * mm, "construction": true});
            skLineSegment(sketch, "E9.5.2.4", {"start": v(110, 51.96) * mm, "end": v(100, 69.28) * mm, "construction": true});
            skLineSegment(sketch, "E9.5.2.5", {"start": v(110, 86.6) * mm, "end": v(100, 69.28) * mm, "construction": true});
            skLineSegment(sketch, "E9.5.2.6", {"start": v(120, 69.28) * mm, "end": v(110, 86.6) * mm, "construction": true});
            skLineSegment(sketch, "E9.5.2.7", {"start": v(110, 86.6) * mm, "end": v(130, 86.6) * mm, "construction": true});
            skLineSegment(sketch, "E9.5.2.8", {"start": v(130, 86.6) * mm, "end": v(120, 69.28) * mm, "construction": true});
            skLineSegment(sketch, "E9.5.3.0", {"start": v(110, 86.6) * mm, "end": v(130, 86.6) * mm, "construction": true});
            skLineSegment(sketch, "E9.5.3.1", {"start": v(120, 103.92) * mm, "end": v(110, 86.6) * mm, "construction": true});
            skLineSegment(sketch, "E9.5.3.2", {"start": v(130, 86.6) * mm, "end": v(120, 103.92) * mm, "construction": true});
            skLineSegment(sketch, "E9.5.3.3", {"start": v(100, 103.92) * mm, "end": v(120, 103.92) * mm, "construction": true});
            skLineSegment(sketch, "E9.5.3.4", {"start": v(110, 86.6) * mm, "end": v(100, 103.92) * mm, "construction": true});
            skLineSegment(sketch, "E9.5.3.5", {"start": v(110, 121.24) * mm, "end": v(100, 103.92) * mm, "construction": true});
            skLineSegment(sketch, "E9.5.3.6", {"start": v(120, 103.92) * mm, "end": v(110, 121.24) * mm, "construction": true});
            skLineSegment(sketch, "E9.5.3.7", {"start": v(110, 121.24) * mm, "end": v(130, 121.24) * mm, "construction": true});
            skLineSegment(sketch, "E9.5.3.8", {"start": v(130, 121.24) * mm, "end": v(120, 103.92) * mm, "construction": true});
            skLineSegment(sketch, "E9.5.4.0", {"start": v(110, 121.24) * mm, "end": v(130, 121.24) * mm, "construction": true});
            skLineSegment(sketch, "E9.5.4.1", {"start": v(120, 138.56) * mm, "end": v(110, 121.24) * mm, "construction": true});
            skLineSegment(sketch, "E9.5.4.2", {"start": v(130, 121.24) * mm, "end": v(120, 138.56) * mm, "construction": true});
            skLineSegment(sketch, "E9.5.4.3", {"start": v(100, 138.56) * mm, "end": v(120, 138.56) * mm, "construction": true});
            skLineSegment(sketch, "E9.5.4.4", {"start": v(110, 121.24) * mm, "end": v(100, 138.56) * mm, "construction": true});
            skLineSegment(sketch, "E9.5.4.5", {"start": v(110, 155.88) * mm, "end": v(100, 138.56) * mm, "construction": true});
            skLineSegment(sketch, "E9.5.4.6", {"start": v(120, 138.56) * mm, "end": v(110, 155.88) * mm, "construction": true});
            skLineSegment(sketch, "E9.5.4.7", {"start": v(110, 155.88) * mm, "end": v(130, 155.88) * mm, "construction": true});
            skLineSegment(sketch, "E9.5.4.8", {"start": v(130, 155.88) * mm, "end": v(120, 138.56) * mm, "construction": true});
            skLineSegment(sketch, "E9.5.5.0", {"start": v(110, 155.88) * mm, "end": v(130, 155.88) * mm, "construction": true});
            skLineSegment(sketch, "E9.5.5.1", {"start": v(120, 173.2) * mm, "end": v(110, 155.88) * mm, "construction": true});
            skLineSegment(sketch, "E9.5.5.2", {"start": v(130, 155.88) * mm, "end": v(120, 173.2) * mm, "construction": true});
            skLineSegment(sketch, "E9.5.5.3", {"start": v(100, 173.2) * mm, "end": v(120, 173.2) * mm, "construction": true});
            skLineSegment(sketch, "E9.5.5.4", {"start": v(110, 155.88) * mm, "end": v(100, 173.2) * mm, "construction": true});
            skLineSegment(sketch, "E9.5.5.5", {"start": v(110, 190.53) * mm, "end": v(100, 173.2) * mm, "construction": true});
            skLineSegment(sketch, "E9.5.5.6", {"start": v(120, 173.2) * mm, "end": v(110, 190.53) * mm, "construction": true});
            skLineSegment(sketch, "E9.5.5.7", {"start": v(110, 190.53) * mm, "end": v(130, 190.53) * mm, "construction": true});
            skLineSegment(sketch, "E9.5.5.8", {"start": v(130, 190.53) * mm, "end": v(120, 173.2) * mm, "construction": true});
            skLineSegment(sketch, "E9.5.6.0", {"start": v(110, 190.53) * mm, "end": v(130, 190.53) * mm, "construction": true});
            skLineSegment(sketch, "E9.5.6.1", {"start": v(120, 207.85) * mm, "end": v(110, 190.53) * mm, "construction": true});
            skLineSegment(sketch, "E9.5.6.2", {"start": v(130, 190.53) * mm, "end": v(120, 207.85) * mm, "construction": true});
            skLineSegment(sketch, "E9.5.6.3", {"start": v(100, 207.85) * mm, "end": v(120, 207.85) * mm, "construction": true});
            skLineSegment(sketch, "E9.5.6.4", {"start": v(110, 190.53) * mm, "end": v(100, 207.85) * mm, "construction": true});
            skLineSegment(sketch, "E9.5.6.5", {"start": v(110, 225.17) * mm, "end": v(100, 207.85) * mm, "construction": true});
            skLineSegment(sketch, "E9.5.6.6", {"start": v(120, 207.85) * mm, "end": v(110, 225.17) * mm, "construction": true});
            skLineSegment(sketch, "E9.5.6.7", {"start": v(110, 225.17) * mm, "end": v(130, 225.17) * mm, "construction": true});
            skLineSegment(sketch, "E9.5.6.8", {"start": v(130, 225.17) * mm, "end": v(120, 207.85) * mm, "construction": true});
            skLineSegment(sketch, "E9.6.0.0", {"start": v(130, -17.32) * mm, "end": v(150, -17.32) * mm, "construction": true});
            skLineSegment(sketch, "E9.6.0.1", {"start": v(140, 0) * mm, "end": v(130, -17.32) * mm, "construction": true});
            skLineSegment(sketch, "E9.6.0.2", {"start": v(150, -17.32) * mm, "end": v(140, 0) * mm, "construction": true});
            skLineSegment(sketch, "E9.6.0.3", {"start": v(120, 0) * mm, "end": v(140, 0) * mm, "construction": true});
            skLineSegment(sketch, "E9.6.0.4", {"start": v(130, -17.32) * mm, "end": v(120, 0) * mm, "construction": true});
            skLineSegment(sketch, "E9.6.0.5", {"start": v(130, 17.32) * mm, "end": v(120, 0) * mm, "construction": true});
            skLineSegment(sketch, "E9.6.0.6", {"start": v(140, 0) * mm, "end": v(130, 17.32) * mm, "construction": true});
            skLineSegment(sketch, "E9.6.0.7", {"start": v(130, 17.32) * mm, "end": v(150, 17.32) * mm, "construction": true});
            skLineSegment(sketch, "E9.6.0.8", {"start": v(150, 17.32) * mm, "end": v(140, 0) * mm, "construction": true});
            skLineSegment(sketch, "E9.6.1.0", {"start": v(130, 17.32) * mm, "end": v(150, 17.32) * mm, "construction": true});
            skLineSegment(sketch, "E9.6.1.1", {"start": v(140, 34.64) * mm, "end": v(130, 17.32) * mm, "construction": true});
            skLineSegment(sketch, "E9.6.1.2", {"start": v(150, 17.32) * mm, "end": v(140, 34.64) * mm, "construction": true});
            skLineSegment(sketch, "E9.6.1.3", {"start": v(120, 34.64) * mm, "end": v(140, 34.64) * mm, "construction": true});
            skLineSegment(sketch, "E9.6.1.4", {"start": v(130, 17.32) * mm, "end": v(120, 34.64) * mm, "construction": true});
            skLineSegment(sketch, "E9.6.1.5", {"start": v(130, 51.96) * mm, "end": v(120, 34.64) * mm, "construction": true});
            skLineSegment(sketch, "E9.6.1.6", {"start": v(140, 34.64) * mm, "end": v(130, 51.96) * mm, "construction": true});
            skLineSegment(sketch, "E9.6.1.7", {"start": v(130, 51.96) * mm, "end": v(150, 51.96) * mm, "construction": true});
            skLineSegment(sketch, "E9.6.1.8", {"start": v(150, 51.96) * mm, "end": v(140, 34.64) * mm, "construction": true});
            skLineSegment(sketch, "E9.6.2.0", {"start": v(130, 51.96) * mm, "end": v(150, 51.96) * mm, "construction": true});
            skLineSegment(sketch, "E9.6.2.1", {"start": v(140, 69.28) * mm, "end": v(130, 51.96) * mm, "construction": true});
            skLineSegment(sketch, "E9.6.2.2", {"start": v(150, 51.96) * mm, "end": v(140, 69.28) * mm, "construction": true});
            skLineSegment(sketch, "E9.6.2.3", {"start": v(120, 69.28) * mm, "end": v(140, 69.28) * mm, "construction": true});
            skLineSegment(sketch, "E9.6.2.4", {"start": v(130, 51.96) * mm, "end": v(120, 69.28) * mm, "construction": true});
            skLineSegment(sketch, "E9.6.2.5", {"start": v(130, 86.6) * mm, "end": v(120, 69.28) * mm, "construction": true});
            skLineSegment(sketch, "E9.6.2.6", {"start": v(140, 69.28) * mm, "end": v(130, 86.6) * mm, "construction": true});
            skLineSegment(sketch, "E9.6.2.7", {"start": v(130, 86.6) * mm, "end": v(150, 86.6) * mm, "construction": true});
            skLineSegment(sketch, "E9.6.2.8", {"start": v(150, 86.6) * mm, "end": v(140, 69.28) * mm, "construction": true});
            skLineSegment(sketch, "E9.6.3.0", {"start": v(130, 86.6) * mm, "end": v(150, 86.6) * mm, "construction": true});
            skLineSegment(sketch, "E9.6.3.1", {"start": v(140, 103.92) * mm, "end": v(130, 86.6) * mm, "construction": true});
            skLineSegment(sketch, "E9.6.3.2", {"start": v(150, 86.6) * mm, "end": v(140, 103.92) * mm, "construction": true});
            skLineSegment(sketch, "E9.6.3.3", {"start": v(120, 103.92) * mm, "end": v(140, 103.92) * mm, "construction": true});
            skLineSegment(sketch, "E9.6.3.4", {"start": v(130, 86.6) * mm, "end": v(120, 103.92) * mm, "construction": true});
            skLineSegment(sketch, "E9.6.3.5", {"start": v(130, 121.24) * mm, "end": v(120, 103.92) * mm, "construction": true});
            skLineSegment(sketch, "E9.6.3.6", {"start": v(140, 103.92) * mm, "end": v(130, 121.24) * mm, "construction": true});
            skLineSegment(sketch, "E9.6.3.7", {"start": v(130, 121.24) * mm, "end": v(150, 121.24) * mm, "construction": true});
            skLineSegment(sketch, "E9.6.3.8", {"start": v(150, 121.24) * mm, "end": v(140, 103.92) * mm, "construction": true});
            skLineSegment(sketch, "E9.6.4.0", {"start": v(130, 121.24) * mm, "end": v(150, 121.24) * mm, "construction": true});
            skLineSegment(sketch, "E9.6.4.1", {"start": v(140, 138.56) * mm, "end": v(130, 121.24) * mm, "construction": true});
            skLineSegment(sketch, "E9.6.4.2", {"start": v(150, 121.24) * mm, "end": v(140, 138.56) * mm, "construction": true});
            skLineSegment(sketch, "E9.6.4.3", {"start": v(120, 138.56) * mm, "end": v(140, 138.56) * mm, "construction": true});
            skLineSegment(sketch, "E9.6.4.4", {"start": v(130, 121.24) * mm, "end": v(120, 138.56) * mm, "construction": true});
            skLineSegment(sketch, "E9.6.4.5", {"start": v(130, 155.88) * mm, "end": v(120, 138.56) * mm, "construction": true});
            skLineSegment(sketch, "E9.6.4.6", {"start": v(140, 138.56) * mm, "end": v(130, 155.88) * mm, "construction": true});
            skLineSegment(sketch, "E9.6.4.7", {"start": v(130, 155.88) * mm, "end": v(150, 155.88) * mm, "construction": true});
            skLineSegment(sketch, "E9.6.4.8", {"start": v(150, 155.88) * mm, "end": v(140, 138.56) * mm, "construction": true});
            skLineSegment(sketch, "E9.6.5.0", {"start": v(130, 155.88) * mm, "end": v(150, 155.88) * mm, "construction": true});
            skLineSegment(sketch, "E9.6.5.1", {"start": v(140, 173.2) * mm, "end": v(130, 155.88) * mm, "construction": true});
            skLineSegment(sketch, "E9.6.5.2", {"start": v(150, 155.88) * mm, "end": v(140, 173.2) * mm, "construction": true});
            skLineSegment(sketch, "E9.6.5.3", {"start": v(120, 173.2) * mm, "end": v(140, 173.2) * mm, "construction": true});
            skLineSegment(sketch, "E9.6.5.4", {"start": v(130, 155.88) * mm, "end": v(120, 173.2) * mm, "construction": true});
            skLineSegment(sketch, "E9.6.5.5", {"start": v(130, 190.53) * mm, "end": v(120, 173.2) * mm, "construction": true});
            skLineSegment(sketch, "E9.6.5.6", {"start": v(140, 173.2) * mm, "end": v(130, 190.53) * mm, "construction": true});
            skLineSegment(sketch, "E9.6.5.7", {"start": v(130, 190.53) * mm, "end": v(150, 190.53) * mm, "construction": true});
            skLineSegment(sketch, "E9.6.5.8", {"start": v(150, 190.53) * mm, "end": v(140, 173.2) * mm, "construction": true});
            skLineSegment(sketch, "E9.6.6.0", {"start": v(130, 190.53) * mm, "end": v(150, 190.53) * mm, "construction": true});
            skLineSegment(sketch, "E9.6.6.1", {"start": v(140, 207.85) * mm, "end": v(130, 190.53) * mm, "construction": true});
            skLineSegment(sketch, "E9.6.6.2", {"start": v(150, 190.53) * mm, "end": v(140, 207.85) * mm, "construction": true});
            skLineSegment(sketch, "E9.6.6.3", {"start": v(120, 207.85) * mm, "end": v(140, 207.85) * mm, "construction": true});
            skLineSegment(sketch, "E9.6.6.4", {"start": v(130, 190.53) * mm, "end": v(120, 207.85) * mm, "construction": true});
            skLineSegment(sketch, "E9.6.6.5", {"start": v(130, 225.17) * mm, "end": v(120, 207.85) * mm, "construction": true});
            skLineSegment(sketch, "E9.6.6.6", {"start": v(140, 207.85) * mm, "end": v(130, 225.17) * mm, "construction": true});
            skLineSegment(sketch, "E9.6.6.7", {"start": v(130, 225.17) * mm, "end": v(150, 225.17) * mm, "construction": true});
            skLineSegment(sketch, "E9.6.6.8", {"start": v(150, 225.17) * mm, "end": v(140, 207.85) * mm, "construction": true});
            skLineSegment(sketch, "E9.7.0.0", {"start": v(150, -17.32) * mm, "end": v(170, -17.32) * mm, "construction": true});
            skLineSegment(sketch, "E9.7.0.1", {"start": v(160, 0) * mm, "end": v(150, -17.32) * mm, "construction": true});
            skLineSegment(sketch, "E9.7.0.2", {"start": v(170, -17.32) * mm, "end": v(160, 0) * mm, "construction": true});
            skLineSegment(sketch, "E9.7.0.3", {"start": v(140, 0) * mm, "end": v(160, 0) * mm, "construction": true});
            skLineSegment(sketch, "E9.7.0.4", {"start": v(150, -17.32) * mm, "end": v(140, 0) * mm, "construction": true});
            skLineSegment(sketch, "E9.7.0.5", {"start": v(150, 17.32) * mm, "end": v(140, 0) * mm, "construction": true});
            skLineSegment(sketch, "E9.7.0.6", {"start": v(160, 0) * mm, "end": v(150, 17.32) * mm, "construction": true});
            skLineSegment(sketch, "E9.7.0.7", {"start": v(150, 17.32) * mm, "end": v(170, 17.32) * mm, "construction": true});
            skLineSegment(sketch, "E9.7.0.8", {"start": v(170, 17.32) * mm, "end": v(160, 0) * mm, "construction": true});
            skLineSegment(sketch, "E9.7.1.0", {"start": v(150, 17.32) * mm, "end": v(170, 17.32) * mm, "construction": true});
            skLineSegment(sketch, "E9.7.1.1", {"start": v(160, 34.64) * mm, "end": v(150, 17.32) * mm, "construction": true});
            skLineSegment(sketch, "E9.7.1.2", {"start": v(170, 17.32) * mm, "end": v(160, 34.64) * mm, "construction": true});
            skLineSegment(sketch, "E9.7.1.3", {"start": v(140, 34.64) * mm, "end": v(160, 34.64) * mm, "construction": true});
            skLineSegment(sketch, "E9.7.1.4", {"start": v(150, 17.32) * mm, "end": v(140, 34.64) * mm, "construction": true});
            skLineSegment(sketch, "E9.7.1.5", {"start": v(150, 51.96) * mm, "end": v(140, 34.64) * mm, "construction": true});
            skLineSegment(sketch, "E9.7.1.6", {"start": v(160, 34.64) * mm, "end": v(150, 51.96) * mm, "construction": true});
            skLineSegment(sketch, "E9.7.1.7", {"start": v(150, 51.96) * mm, "end": v(170, 51.96) * mm, "construction": true});
            skLineSegment(sketch, "E9.7.1.8", {"start": v(170, 51.96) * mm, "end": v(160, 34.64) * mm, "construction": true});
            skLineSegment(sketch, "E9.7.2.0", {"start": v(150, 51.96) * mm, "end": v(170, 51.96) * mm, "construction": true});
            skLineSegment(sketch, "E9.7.2.1", {"start": v(160, 69.28) * mm, "end": v(150, 51.96) * mm, "construction": true});
            skLineSegment(sketch, "E9.7.2.2", {"start": v(170, 51.96) * mm, "end": v(160, 69.28) * mm, "construction": true});
            skLineSegment(sketch, "E9.7.2.3", {"start": v(140, 69.28) * mm, "end": v(160, 69.28) * mm, "construction": true});
            skLineSegment(sketch, "E9.7.2.4", {"start": v(150, 51.96) * mm, "end": v(140, 69.28) * mm, "construction": true});
            skLineSegment(sketch, "E9.7.2.5", {"start": v(150, 86.6) * mm, "end": v(140, 69.28) * mm, "construction": true});
            skLineSegment(sketch, "E9.7.2.6", {"start": v(160, 69.28) * mm, "end": v(150, 86.6) * mm, "construction": true});
            skLineSegment(sketch, "E9.7.2.7", {"start": v(150, 86.6) * mm, "end": v(170, 86.6) * mm, "construction": true});
            skLineSegment(sketch, "E9.7.2.8", {"start": v(170, 86.6) * mm, "end": v(160, 69.28) * mm, "construction": true});
            skLineSegment(sketch, "E9.7.3.0", {"start": v(150, 86.6) * mm, "end": v(170, 86.6) * mm, "construction": true});
            skLineSegment(sketch, "E9.7.3.1", {"start": v(160, 103.92) * mm, "end": v(150, 86.6) * mm, "construction": true});
            skLineSegment(sketch, "E9.7.3.2", {"start": v(170, 86.6) * mm, "end": v(160, 103.92) * mm, "construction": true});
            skLineSegment(sketch, "E9.7.3.3", {"start": v(140, 103.92) * mm, "end": v(160, 103.92) * mm, "construction": true});
            skLineSegment(sketch, "E9.7.3.4", {"start": v(150, 86.6) * mm, "end": v(140, 103.92) * mm, "construction": true});
            skLineSegment(sketch, "E9.7.3.5", {"start": v(150, 121.24) * mm, "end": v(140, 103.92) * mm, "construction": true});
            skLineSegment(sketch, "E9.7.3.6", {"start": v(160, 103.92) * mm, "end": v(150, 121.24) * mm, "construction": true});
            skLineSegment(sketch, "E9.7.3.7", {"start": v(150, 121.24) * mm, "end": v(170, 121.24) * mm, "construction": true});
            skLineSegment(sketch, "E9.7.3.8", {"start": v(170, 121.24) * mm, "end": v(160, 103.92) * mm, "construction": true});
            skLineSegment(sketch, "E9.7.4.0", {"start": v(150, 121.24) * mm, "end": v(170, 121.24) * mm, "construction": true});
            skLineSegment(sketch, "E9.7.4.1", {"start": v(160, 138.56) * mm, "end": v(150, 121.24) * mm, "construction": true});
            skLineSegment(sketch, "E9.7.4.2", {"start": v(170, 121.24) * mm, "end": v(160, 138.56) * mm, "construction": true});
            skLineSegment(sketch, "E9.7.4.3", {"start": v(140, 138.56) * mm, "end": v(160, 138.56) * mm, "construction": true});
            skLineSegment(sketch, "E9.7.4.4", {"start": v(150, 121.24) * mm, "end": v(140, 138.56) * mm, "construction": true});
            skLineSegment(sketch, "E9.7.4.5", {"start": v(150, 155.88) * mm, "end": v(140, 138.56) * mm, "construction": true});
            skLineSegment(sketch, "E9.7.4.6", {"start": v(160, 138.56) * mm, "end": v(150, 155.88) * mm, "construction": true});
            skLineSegment(sketch, "E9.7.4.7", {"start": v(150, 155.88) * mm, "end": v(170, 155.88) * mm, "construction": true});
            skLineSegment(sketch, "E9.7.4.8", {"start": v(170, 155.88) * mm, "end": v(160, 138.56) * mm, "construction": true});
            skLineSegment(sketch, "E9.7.5.0", {"start": v(150, 155.88) * mm, "end": v(170, 155.88) * mm, "construction": true});
            skLineSegment(sketch, "E9.7.5.1", {"start": v(160, 173.2) * mm, "end": v(150, 155.88) * mm, "construction": true});
            skLineSegment(sketch, "E9.7.5.2", {"start": v(170, 155.88) * mm, "end": v(160, 173.2) * mm, "construction": true});
            skLineSegment(sketch, "E9.7.5.3", {"start": v(140, 173.2) * mm, "end": v(160, 173.2) * mm, "construction": true});
            skLineSegment(sketch, "E9.7.5.4", {"start": v(150, 155.88) * mm, "end": v(140, 173.2) * mm, "construction": true});
            skLineSegment(sketch, "E9.7.5.5", {"start": v(150, 190.53) * mm, "end": v(140, 173.2) * mm, "construction": true});
            skLineSegment(sketch, "E9.7.5.6", {"start": v(160, 173.2) * mm, "end": v(150, 190.53) * mm, "construction": true});
            skLineSegment(sketch, "E9.7.5.7", {"start": v(150, 190.53) * mm, "end": v(170, 190.53) * mm, "construction": true});
            skLineSegment(sketch, "E9.7.5.8", {"start": v(170, 190.53) * mm, "end": v(160, 173.2) * mm, "construction": true});
            skLineSegment(sketch, "E9.7.6.0", {"start": v(150, 190.53) * mm, "end": v(170, 190.53) * mm, "construction": true});
            skLineSegment(sketch, "E9.7.6.1", {"start": v(160, 207.85) * mm, "end": v(150, 190.53) * mm, "construction": true});
            skLineSegment(sketch, "E9.7.6.2", {"start": v(170, 190.53) * mm, "end": v(160, 207.85) * mm, "construction": true});
            skLineSegment(sketch, "E9.7.6.3", {"start": v(140, 207.85) * mm, "end": v(160, 207.85) * mm, "construction": true});
            skLineSegment(sketch, "E9.7.6.4", {"start": v(150, 190.53) * mm, "end": v(140, 207.85) * mm, "construction": true});
            skLineSegment(sketch, "E9.7.6.5", {"start": v(150, 225.17) * mm, "end": v(140, 207.85) * mm, "construction": true});
            skLineSegment(sketch, "E9.7.6.6", {"start": v(160, 207.85) * mm, "end": v(150, 225.17) * mm, "construction": true});
            skLineSegment(sketch, "E9.7.6.7", {"start": v(150, 225.17) * mm, "end": v(170, 225.17) * mm, "construction": true});
            skLineSegment(sketch, "E9.7.6.8", {"start": v(170, 225.17) * mm, "end": v(160, 207.85) * mm, "construction": true});
            skLineSegment(sketch, "E9.8.0.0", {"start": v(170, -17.32) * mm, "end": v(190, -17.32) * mm, "construction": true});
            skLineSegment(sketch, "E9.8.0.1", {"start": v(180, 0) * mm, "end": v(170, -17.32) * mm, "construction": true});
            skLineSegment(sketch, "E9.8.0.2", {"start": v(190, -17.32) * mm, "end": v(180, 0) * mm, "construction": true});
            skLineSegment(sketch, "E9.8.0.3", {"start": v(160, 0) * mm, "end": v(180, 0) * mm, "construction": true});
            skLineSegment(sketch, "E9.8.0.4", {"start": v(170, -17.32) * mm, "end": v(160, 0) * mm, "construction": true});
            skLineSegment(sketch, "E9.8.0.5", {"start": v(170, 17.32) * mm, "end": v(160, 0) * mm, "construction": true});
            skLineSegment(sketch, "E9.8.0.6", {"start": v(180, 0) * mm, "end": v(170, 17.32) * mm, "construction": true});
            skLineSegment(sketch, "E9.8.0.7", {"start": v(170, 17.32) * mm, "end": v(190, 17.32) * mm, "construction": true});
            skLineSegment(sketch, "E9.8.0.8", {"start": v(190, 17.32) * mm, "end": v(180, 0) * mm, "construction": true});
            skLineSegment(sketch, "E9.8.1.0", {"start": v(170, 17.32) * mm, "end": v(190, 17.32) * mm, "construction": true});
            skLineSegment(sketch, "E9.8.1.1", {"start": v(180, 34.64) * mm, "end": v(170, 17.32) * mm, "construction": true});
            skLineSegment(sketch, "E9.8.1.2", {"start": v(190, 17.32) * mm, "end": v(180, 34.64) * mm, "construction": true});
            skLineSegment(sketch, "E9.8.1.3", {"start": v(160, 34.64) * mm, "end": v(180, 34.64) * mm, "construction": true});
            skLineSegment(sketch, "E9.8.1.4", {"start": v(170, 17.32) * mm, "end": v(160, 34.64) * mm, "construction": true});
            skLineSegment(sketch, "E9.8.1.5", {"start": v(170, 51.96) * mm, "end": v(160, 34.64) * mm, "construction": true});
            skLineSegment(sketch, "E9.8.1.6", {"start": v(180, 34.64) * mm, "end": v(170, 51.96) * mm, "construction": true});
            skLineSegment(sketch, "E9.8.1.7", {"start": v(170, 51.96) * mm, "end": v(190, 51.96) * mm, "construction": true});
            skLineSegment(sketch, "E9.8.1.8", {"start": v(190, 51.96) * mm, "end": v(180, 34.64) * mm, "construction": true});
            skLineSegment(sketch, "E9.8.2.0", {"start": v(170, 51.96) * mm, "end": v(190, 51.96) * mm, "construction": true});
            skLineSegment(sketch, "E9.8.2.1", {"start": v(180, 69.28) * mm, "end": v(170, 51.96) * mm, "construction": true});
            skLineSegment(sketch, "E9.8.2.2", {"start": v(190, 51.96) * mm, "end": v(180, 69.28) * mm, "construction": true});
            skLineSegment(sketch, "E9.8.2.3", {"start": v(160, 69.28) * mm, "end": v(180, 69.28) * mm, "construction": true});
            skLineSegment(sketch, "E9.8.2.4", {"start": v(170, 51.96) * mm, "end": v(160, 69.28) * mm, "construction": true});
            skLineSegment(sketch, "E9.8.2.5", {"start": v(170, 86.6) * mm, "end": v(160, 69.28) * mm, "construction": true});
            skLineSegment(sketch, "E9.8.2.6", {"start": v(180, 69.28) * mm, "end": v(170, 86.6) * mm, "construction": true});
            skLineSegment(sketch, "E9.8.2.7", {"start": v(170, 86.6) * mm, "end": v(190, 86.6) * mm, "construction": true});
            skLineSegment(sketch, "E9.8.2.8", {"start": v(190, 86.6) * mm, "end": v(180, 69.28) * mm, "construction": true});
            skLineSegment(sketch, "E9.8.3.0", {"start": v(170, 86.6) * mm, "end": v(190, 86.6) * mm, "construction": true});
            skLineSegment(sketch, "E9.8.3.1", {"start": v(180, 103.92) * mm, "end": v(170, 86.6) * mm, "construction": true});
            skLineSegment(sketch, "E9.8.3.2", {"start": v(190, 86.6) * mm, "end": v(180, 103.92) * mm, "construction": true});
            skLineSegment(sketch, "E9.8.3.3", {"start": v(160, 103.92) * mm, "end": v(180, 103.92) * mm, "construction": true});
            skLineSegment(sketch, "E9.8.3.4", {"start": v(170, 86.6) * mm, "end": v(160, 103.92) * mm, "construction": true});
            skLineSegment(sketch, "E9.8.3.5", {"start": v(170, 121.24) * mm, "end": v(160, 103.92) * mm, "construction": true});
            skLineSegment(sketch, "E9.8.3.6", {"start": v(180, 103.92) * mm, "end": v(170, 121.24) * mm, "construction": true});
            skLineSegment(sketch, "E9.8.3.7", {"start": v(170, 121.24) * mm, "end": v(190, 121.24) * mm, "construction": true});
            skLineSegment(sketch, "E9.8.3.8", {"start": v(190, 121.24) * mm, "end": v(180, 103.92) * mm, "construction": true});
            skLineSegment(sketch, "E9.8.4.0", {"start": v(170, 121.24) * mm, "end": v(190, 121.24) * mm, "construction": true});
            skLineSegment(sketch, "E9.8.4.1", {"start": v(180, 138.56) * mm, "end": v(170, 121.24) * mm, "construction": true});
            skLineSegment(sketch, "E9.8.4.2", {"start": v(190, 121.24) * mm, "end": v(180, 138.56) * mm, "construction": true});
            skLineSegment(sketch, "E9.8.4.3", {"start": v(160, 138.56) * mm, "end": v(180, 138.56) * mm, "construction": true});
            skLineSegment(sketch, "E9.8.4.4", {"start": v(170, 121.24) * mm, "end": v(160, 138.56) * mm, "construction": true});
            skLineSegment(sketch, "E9.8.4.5", {"start": v(170, 155.88) * mm, "end": v(160, 138.56) * mm, "construction": true});
            skLineSegment(sketch, "E9.8.4.6", {"start": v(180, 138.56) * mm, "end": v(170, 155.88) * mm, "construction": true});
            skLineSegment(sketch, "E9.8.4.7", {"start": v(170, 155.88) * mm, "end": v(190, 155.88) * mm, "construction": true});
            skLineSegment(sketch, "E9.8.4.8", {"start": v(190, 155.88) * mm, "end": v(180, 138.56) * mm, "construction": true});
            skLineSegment(sketch, "E9.8.5.0", {"start": v(170, 155.88) * mm, "end": v(190, 155.88) * mm, "construction": true});
            skLineSegment(sketch, "E9.8.5.1", {"start": v(180, 173.2) * mm, "end": v(170, 155.88) * mm, "construction": true});
            skLineSegment(sketch, "E9.8.5.2", {"start": v(190, 155.88) * mm, "end": v(180, 173.2) * mm, "construction": true});
            skLineSegment(sketch, "E9.8.5.3", {"start": v(160, 173.2) * mm, "end": v(180, 173.2) * mm, "construction": true});
            skLineSegment(sketch, "E9.8.5.4", {"start": v(170, 155.88) * mm, "end": v(160, 173.2) * mm, "construction": true});
            skLineSegment(sketch, "E9.8.5.5", {"start": v(170, 190.53) * mm, "end": v(160, 173.2) * mm, "construction": true});
            skLineSegment(sketch, "E9.8.5.6", {"start": v(180, 173.2) * mm, "end": v(170, 190.53) * mm, "construction": true});
            skLineSegment(sketch, "E9.8.5.7", {"start": v(170, 190.53) * mm, "end": v(190, 190.53) * mm, "construction": true});
            skLineSegment(sketch, "E9.8.5.8", {"start": v(190, 190.53) * mm, "end": v(180, 173.2) * mm, "construction": true});
            skLineSegment(sketch, "E9.8.6.0", {"start": v(170, 190.53) * mm, "end": v(190, 190.53) * mm, "construction": true});
            skLineSegment(sketch, "E9.8.6.1", {"start": v(180, 207.85) * mm, "end": v(170, 190.53) * mm, "construction": true});
            skLineSegment(sketch, "E9.8.6.2", {"start": v(190, 190.53) * mm, "end": v(180, 207.85) * mm, "construction": true});
            skLineSegment(sketch, "E9.8.6.3", {"start": v(160, 207.85) * mm, "end": v(180, 207.85) * mm, "construction": true});
            skLineSegment(sketch, "E9.8.6.4", {"start": v(170, 190.53) * mm, "end": v(160, 207.85) * mm, "construction": true});
            skLineSegment(sketch, "E9.8.6.5", {"start": v(170, 225.17) * mm, "end": v(160, 207.85) * mm, "construction": true});
            skLineSegment(sketch, "E9.8.6.6", {"start": v(180, 207.85) * mm, "end": v(170, 225.17) * mm, "construction": true});
            skLineSegment(sketch, "E9.8.6.7", {"start": v(170, 225.17) * mm, "end": v(190, 225.17) * mm, "construction": true});
            skLineSegment(sketch, "E9.8.6.8", {"start": v(190, 225.17) * mm, "end": v(180, 207.85) * mm, "construction": true});
            skLineSegment(sketch, "E9.9.0.0", {"start": v(190, -17.32) * mm, "end": v(210, -17.32) * mm, "construction": true});
            skLineSegment(sketch, "E9.9.0.1", {"start": v(200, 0) * mm, "end": v(190, -17.32) * mm, "construction": true});
            skLineSegment(sketch, "E9.9.0.2", {"start": v(210, -17.32) * mm, "end": v(200, 0) * mm, "construction": true});
            skLineSegment(sketch, "E9.9.0.3", {"start": v(180, 0) * mm, "end": v(200, 0) * mm, "construction": true});
            skLineSegment(sketch, "E9.9.0.4", {"start": v(190, -17.32) * mm, "end": v(180, 0) * mm, "construction": true});
            skLineSegment(sketch, "E9.9.0.5", {"start": v(190, 17.32) * mm, "end": v(180, 0) * mm, "construction": true});
            skLineSegment(sketch, "E9.9.0.6", {"start": v(200, 0) * mm, "end": v(190, 17.32) * mm, "construction": true});
            skLineSegment(sketch, "E9.9.0.7", {"start": v(190, 17.32) * mm, "end": v(210, 17.32) * mm, "construction": true});
            skLineSegment(sketch, "E9.9.0.8", {"start": v(210, 17.32) * mm, "end": v(200, 0) * mm, "construction": true});
            skLineSegment(sketch, "E9.9.1.0", {"start": v(190, 17.32) * mm, "end": v(210, 17.32) * mm, "construction": true});
            skLineSegment(sketch, "E9.9.1.1", {"start": v(200, 34.64) * mm, "end": v(190, 17.32) * mm, "construction": true});
            skLineSegment(sketch, "E9.9.1.2", {"start": v(210, 17.32) * mm, "end": v(200, 34.64) * mm, "construction": true});
            skLineSegment(sketch, "E9.9.1.3", {"start": v(180, 34.64) * mm, "end": v(200, 34.64) * mm, "construction": true});
            skLineSegment(sketch, "E9.9.1.4", {"start": v(190, 17.32) * mm, "end": v(180, 34.64) * mm, "construction": true});
            skLineSegment(sketch, "E9.9.1.5", {"start": v(190, 51.96) * mm, "end": v(180, 34.64) * mm, "construction": true});
            skLineSegment(sketch, "E9.9.1.6", {"start": v(200, 34.64) * mm, "end": v(190, 51.96) * mm, "construction": true});
            skLineSegment(sketch, "E9.9.1.7", {"start": v(190, 51.96) * mm, "end": v(210, 51.96) * mm, "construction": true});
            skLineSegment(sketch, "E9.9.1.8", {"start": v(210, 51.96) * mm, "end": v(200, 34.64) * mm, "construction": true});
            skLineSegment(sketch, "E9.9.2.0", {"start": v(190, 51.96) * mm, "end": v(210, 51.96) * mm, "construction": true});
            skLineSegment(sketch, "E9.9.2.1", {"start": v(200, 69.28) * mm, "end": v(190, 51.96) * mm, "construction": true});
            skLineSegment(sketch, "E9.9.2.2", {"start": v(210, 51.96) * mm, "end": v(200, 69.28) * mm, "construction": true});
            skLineSegment(sketch, "E9.9.2.3", {"start": v(180, 69.28) * mm, "end": v(200, 69.28) * mm, "construction": true});
            skLineSegment(sketch, "E9.9.2.4", {"start": v(190, 51.96) * mm, "end": v(180, 69.28) * mm, "construction": true});
            skLineSegment(sketch, "E9.9.2.5", {"start": v(190, 86.6) * mm, "end": v(180, 69.28) * mm, "construction": true});
            skLineSegment(sketch, "E9.9.2.6", {"start": v(200, 69.28) * mm, "end": v(190, 86.6) * mm, "construction": true});
            skLineSegment(sketch, "E9.9.2.7", {"start": v(190, 86.6) * mm, "end": v(210, 86.6) * mm, "construction": true});
            skLineSegment(sketch, "E9.9.2.8", {"start": v(210, 86.6) * mm, "end": v(200, 69.28) * mm, "construction": true});
            skLineSegment(sketch, "E9.9.3.0", {"start": v(190, 86.6) * mm, "end": v(210, 86.6) * mm, "construction": true});
            skLineSegment(sketch, "E9.9.3.1", {"start": v(200, 103.92) * mm, "end": v(190, 86.6) * mm, "construction": true});
            skLineSegment(sketch, "E9.9.3.2", {"start": v(210, 86.6) * mm, "end": v(200, 103.92) * mm, "construction": true});
            skLineSegment(sketch, "E9.9.3.3", {"start": v(180, 103.92) * mm, "end": v(200, 103.92) * mm, "construction": true});
            skLineSegment(sketch, "E9.9.3.4", {"start": v(190, 86.6) * mm, "end": v(180, 103.92) * mm, "construction": true});
            skLineSegment(sketch, "E9.9.3.5", {"start": v(190, 121.24) * mm, "end": v(180, 103.92) * mm, "construction": true});
            skLineSegment(sketch, "E9.9.3.6", {"start": v(200, 103.92) * mm, "end": v(190, 121.24) * mm, "construction": true});
            skLineSegment(sketch, "E9.9.3.7", {"start": v(190, 121.24) * mm, "end": v(210, 121.24) * mm, "construction": true});
            skLineSegment(sketch, "E9.9.3.8", {"start": v(210, 121.24) * mm, "end": v(200, 103.92) * mm, "construction": true});
            skLineSegment(sketch, "E9.9.4.0", {"start": v(190, 121.24) * mm, "end": v(210, 121.24) * mm, "construction": true});
            skLineSegment(sketch, "E9.9.4.1", {"start": v(200, 138.56) * mm, "end": v(190, 121.24) * mm, "construction": true});
            skLineSegment(sketch, "E9.9.4.2", {"start": v(210, 121.24) * mm, "end": v(200, 138.56) * mm, "construction": true});
            skLineSegment(sketch, "E9.9.4.3", {"start": v(180, 138.56) * mm, "end": v(200, 138.56) * mm, "construction": true});
            skLineSegment(sketch, "E9.9.4.4", {"start": v(190, 121.24) * mm, "end": v(180, 138.56) * mm, "construction": true});
            skLineSegment(sketch, "E9.9.4.5", {"start": v(190, 155.88) * mm, "end": v(180, 138.56) * mm, "construction": true});
            skLineSegment(sketch, "E9.9.4.6", {"start": v(200, 138.56) * mm, "end": v(190, 155.88) * mm, "construction": true});
            skLineSegment(sketch, "E9.9.4.7", {"start": v(190, 155.88) * mm, "end": v(210, 155.88) * mm, "construction": true});
            skLineSegment(sketch, "E9.9.4.8", {"start": v(210, 155.88) * mm, "end": v(200, 138.56) * mm, "construction": true});
            skLineSegment(sketch, "E9.9.5.0", {"start": v(190, 155.88) * mm, "end": v(210, 155.88) * mm, "construction": true});
            skLineSegment(sketch, "E9.9.5.1", {"start": v(200, 173.2) * mm, "end": v(190, 155.88) * mm, "construction": true});
            skLineSegment(sketch, "E9.9.5.2", {"start": v(210, 155.88) * mm, "end": v(200, 173.2) * mm, "construction": true});
            skLineSegment(sketch, "E9.9.5.3", {"start": v(180, 173.2) * mm, "end": v(200, 173.2) * mm, "construction": true});
            skLineSegment(sketch, "E9.9.5.4", {"start": v(190, 155.88) * mm, "end": v(180, 173.2) * mm, "construction": true});
            skLineSegment(sketch, "E9.9.5.5", {"start": v(190, 190.53) * mm, "end": v(180, 173.2) * mm, "construction": true});
            skLineSegment(sketch, "E9.9.5.6", {"start": v(200, 173.2) * mm, "end": v(190, 190.53) * mm, "construction": true});
            skLineSegment(sketch, "E9.9.5.7", {"start": v(190, 190.53) * mm, "end": v(210, 190.53) * mm, "construction": true});
            skLineSegment(sketch, "E9.9.5.8", {"start": v(210, 190.53) * mm, "end": v(200, 173.2) * mm, "construction": true});
            skLineSegment(sketch, "E9.9.6.0", {"start": v(190, 190.53) * mm, "end": v(210, 190.53) * mm, "construction": true});
            skLineSegment(sketch, "E9.9.6.1", {"start": v(200, 207.85) * mm, "end": v(190, 190.53) * mm, "construction": true});
            skLineSegment(sketch, "E9.9.6.2", {"start": v(210, 190.53) * mm, "end": v(200, 207.85) * mm, "construction": true});
            skLineSegment(sketch, "E9.9.6.3", {"start": v(180, 207.85) * mm, "end": v(200, 207.85) * mm, "construction": true});
            skLineSegment(sketch, "E9.9.6.4", {"start": v(190, 190.53) * mm, "end": v(180, 207.85) * mm, "construction": true});
            skLineSegment(sketch, "E9.9.6.5", {"start": v(190, 225.17) * mm, "end": v(180, 207.85) * mm, "construction": true});
            skLineSegment(sketch, "E9.9.6.6", {"start": v(200, 207.85) * mm, "end": v(190, 225.17) * mm, "construction": true});
            skLineSegment(sketch, "E9.9.6.7", {"start": v(190, 225.17) * mm, "end": v(210, 225.17) * mm, "construction": true});
            skLineSegment(sketch, "E9.9.6.8", {"start": v(210, 225.17) * mm, "end": v(200, 207.85) * mm, "construction": true});
            skLineSegment(sketch, "E9.10.0.0", {"start": v(210, -17.32) * mm, "end": v(230, -17.32) * mm, "construction": true});
            skLineSegment(sketch, "E9.10.0.1", {"start": v(220, 0) * mm, "end": v(210, -17.32) * mm, "construction": true});
            skLineSegment(sketch, "E9.10.0.2", {"start": v(230, -17.32) * mm, "end": v(220, 0) * mm, "construction": true});
            skLineSegment(sketch, "E9.10.0.3", {"start": v(200, 0) * mm, "end": v(220, 0) * mm, "construction": true});
            skLineSegment(sketch, "E9.10.0.4", {"start": v(210, -17.32) * mm, "end": v(200, 0) * mm, "construction": true});
            skLineSegment(sketch, "E9.10.0.5", {"start": v(210, 17.32) * mm, "end": v(200, 0) * mm, "construction": true});
            skLineSegment(sketch, "E9.10.0.6", {"start": v(220, 0) * mm, "end": v(210, 17.32) * mm, "construction": true});
            skLineSegment(sketch, "E9.10.0.7", {"start": v(210, 17.32) * mm, "end": v(230, 17.32) * mm, "construction": true});
            skLineSegment(sketch, "E9.10.0.8", {"start": v(230, 17.32) * mm, "end": v(220, 0) * mm, "construction": true});
            skLineSegment(sketch, "E9.10.1.0", {"start": v(210, 17.32) * mm, "end": v(230, 17.32) * mm, "construction": true});
            skLineSegment(sketch, "E9.10.1.1", {"start": v(220, 34.64) * mm, "end": v(210, 17.32) * mm, "construction": true});
            skLineSegment(sketch, "E9.10.1.2", {"start": v(230, 17.32) * mm, "end": v(220, 34.64) * mm, "construction": true});
            skLineSegment(sketch, "E9.10.1.3", {"start": v(200, 34.64) * mm, "end": v(220, 34.64) * mm, "construction": true});
            skLineSegment(sketch, "E9.10.1.4", {"start": v(210, 17.32) * mm, "end": v(200, 34.64) * mm, "construction": true});
            skLineSegment(sketch, "E9.10.1.5", {"start": v(210, 51.96) * mm, "end": v(200, 34.64) * mm, "construction": true});
            skLineSegment(sketch, "E9.10.1.6", {"start": v(220, 34.64) * mm, "end": v(210, 51.96) * mm, "construction": true});
            skLineSegment(sketch, "E9.10.1.7", {"start": v(210, 51.96) * mm, "end": v(230, 51.96) * mm, "construction": true});
            skLineSegment(sketch, "E9.10.1.8", {"start": v(230, 51.96) * mm, "end": v(220, 34.64) * mm, "construction": true});
            skLineSegment(sketch, "E9.10.2.0", {"start": v(210, 51.96) * mm, "end": v(230, 51.96) * mm, "construction": true});
            skLineSegment(sketch, "E9.10.2.1", {"start": v(220, 69.28) * mm, "end": v(210, 51.96) * mm, "construction": true});
            skLineSegment(sketch, "E9.10.2.2", {"start": v(230, 51.96) * mm, "end": v(220, 69.28) * mm, "construction": true});
            skLineSegment(sketch, "E9.10.2.3", {"start": v(200, 69.28) * mm, "end": v(220, 69.28) * mm, "construction": true});
            skLineSegment(sketch, "E9.10.2.4", {"start": v(210, 51.96) * mm, "end": v(200, 69.28) * mm, "construction": true});
            skLineSegment(sketch, "E9.10.2.5", {"start": v(210, 86.6) * mm, "end": v(200, 69.28) * mm, "construction": true});
            skLineSegment(sketch, "E9.10.2.6", {"start": v(220, 69.28) * mm, "end": v(210, 86.6) * mm, "construction": true});
            skLineSegment(sketch, "E9.10.2.7", {"start": v(210, 86.6) * mm, "end": v(230, 86.6) * mm, "construction": true});
            skLineSegment(sketch, "E9.10.2.8", {"start": v(230, 86.6) * mm, "end": v(220, 69.28) * mm, "construction": true});
            skLineSegment(sketch, "E9.10.3.0", {"start": v(210, 86.6) * mm, "end": v(230, 86.6) * mm, "construction": true});
            skLineSegment(sketch, "E9.10.3.1", {"start": v(220, 103.92) * mm, "end": v(210, 86.6) * mm, "construction": true});
            skLineSegment(sketch, "E9.10.3.2", {"start": v(230, 86.6) * mm, "end": v(220, 103.92) * mm, "construction": true});
            skLineSegment(sketch, "E9.10.3.3", {"start": v(200, 103.92) * mm, "end": v(220, 103.92) * mm, "construction": true});
            skLineSegment(sketch, "E9.10.3.4", {"start": v(210, 86.6) * mm, "end": v(200, 103.92) * mm, "construction": true});
            skLineSegment(sketch, "E9.10.3.5", {"start": v(210, 121.24) * mm, "end": v(200, 103.92) * mm, "construction": true});
            skLineSegment(sketch, "E9.10.3.6", {"start": v(220, 103.92) * mm, "end": v(210, 121.24) * mm, "construction": true});
            skLineSegment(sketch, "E9.10.3.7", {"start": v(210, 121.24) * mm, "end": v(230, 121.24) * mm, "construction": true});
            skLineSegment(sketch, "E9.10.3.8", {"start": v(230, 121.24) * mm, "end": v(220, 103.92) * mm, "construction": true});
            skLineSegment(sketch, "E9.10.4.0", {"start": v(210, 121.24) * mm, "end": v(230, 121.24) * mm, "construction": true});
            skLineSegment(sketch, "E9.10.4.1", {"start": v(220, 138.56) * mm, "end": v(210, 121.24) * mm, "construction": true});
            skLineSegment(sketch, "E9.10.4.2", {"start": v(230, 121.24) * mm, "end": v(220, 138.56) * mm, "construction": true});
            skLineSegment(sketch, "E9.10.4.3", {"start": v(200, 138.56) * mm, "end": v(220, 138.56) * mm, "construction": true});
            skLineSegment(sketch, "E9.10.4.4", {"start": v(210, 121.24) * mm, "end": v(200, 138.56) * mm, "construction": true});
            skLineSegment(sketch, "E9.10.4.5", {"start": v(210, 155.88) * mm, "end": v(200, 138.56) * mm, "construction": true});
            skLineSegment(sketch, "E9.10.4.6", {"start": v(220, 138.56) * mm, "end": v(210, 155.88) * mm, "construction": true});
            skLineSegment(sketch, "E9.10.4.7", {"start": v(210, 155.88) * mm, "end": v(230, 155.88) * mm, "construction": true});
            skLineSegment(sketch, "E9.10.4.8", {"start": v(230, 155.88) * mm, "end": v(220, 138.56) * mm, "construction": true});
            skLineSegment(sketch, "E9.10.5.0", {"start": v(210, 155.88) * mm, "end": v(230, 155.88) * mm, "construction": true});
            skLineSegment(sketch, "E9.10.5.1", {"start": v(220, 173.2) * mm, "end": v(210, 155.88) * mm, "construction": true});
            skLineSegment(sketch, "E9.10.5.2", {"start": v(230, 155.88) * mm, "end": v(220, 173.2) * mm, "construction": true});
            skLineSegment(sketch, "E9.10.5.3", {"start": v(200, 173.2) * mm, "end": v(220, 173.2) * mm, "construction": true});
            skLineSegment(sketch, "E9.10.5.4", {"start": v(210, 155.88) * mm, "end": v(200, 173.2) * mm, "construction": true});
            skLineSegment(sketch, "E9.10.5.5", {"start": v(210, 190.53) * mm, "end": v(200, 173.2) * mm, "construction": true});
            skLineSegment(sketch, "E9.10.5.6", {"start": v(220, 173.2) * mm, "end": v(210, 190.53) * mm, "construction": true});
            skLineSegment(sketch, "E9.10.5.7", {"start": v(210, 190.53) * mm, "end": v(230, 190.53) * mm, "construction": true});
            skLineSegment(sketch, "E9.10.5.8", {"start": v(230, 190.53) * mm, "end": v(220, 173.2) * mm, "construction": true});
            skLineSegment(sketch, "E9.10.6.0", {"start": v(210, 190.53) * mm, "end": v(230, 190.53) * mm, "construction": true});
            skLineSegment(sketch, "E9.10.6.1", {"start": v(220, 207.85) * mm, "end": v(210, 190.53) * mm, "construction": true});
            skLineSegment(sketch, "E9.10.6.2", {"start": v(230, 190.53) * mm, "end": v(220, 207.85) * mm, "construction": true});
            skLineSegment(sketch, "E9.10.6.3", {"start": v(200, 207.85) * mm, "end": v(220, 207.85) * mm, "construction": true});
            skLineSegment(sketch, "E9.10.6.4", {"start": v(210, 190.53) * mm, "end": v(200, 207.85) * mm, "construction": true});
            skLineSegment(sketch, "E9.10.6.5", {"start": v(210, 225.17) * mm, "end": v(200, 207.85) * mm, "construction": true});
            skLineSegment(sketch, "E9.10.6.6", {"start": v(220, 207.85) * mm, "end": v(210, 225.17) * mm, "construction": true});
            skLineSegment(sketch, "E9.10.6.7", {"start": v(210, 225.17) * mm, "end": v(230, 225.17) * mm, "construction": true});
            skLineSegment(sketch, "E9.10.6.8", {"start": v(230, 225.17) * mm, "end": v(220, 207.85) * mm, "construction": true});
            skLineSegment(sketch, "E9.11.0.0", {"start": v(230, -17.32) * mm, "end": v(250, -17.32) * mm, "construction": true});
            skLineSegment(sketch, "E9.11.0.1", {"start": v(240, 0) * mm, "end": v(230, -17.32) * mm, "construction": true});
            skLineSegment(sketch, "E9.11.0.2", {"start": v(250, -17.32) * mm, "end": v(240, 0) * mm, "construction": true});
            skLineSegment(sketch, "E9.11.0.3", {"start": v(220, 0) * mm, "end": v(240, 0) * mm, "construction": true});
            skLineSegment(sketch, "E9.11.0.4", {"start": v(230, -17.32) * mm, "end": v(220, 0) * mm, "construction": true});
            skLineSegment(sketch, "E9.11.0.5", {"start": v(230, 17.32) * mm, "end": v(220, 0) * mm, "construction": true});
            skLineSegment(sketch, "E9.11.0.6", {"start": v(240, 0) * mm, "end": v(230, 17.32) * mm, "construction": true});
            skLineSegment(sketch, "E9.11.0.7", {"start": v(230, 17.32) * mm, "end": v(250, 17.32) * mm, "construction": true});
            skLineSegment(sketch, "E9.11.0.8", {"start": v(250, 17.32) * mm, "end": v(240, 0) * mm, "construction": true});
            skLineSegment(sketch, "E9.11.1.0", {"start": v(230, 17.32) * mm, "end": v(250, 17.32) * mm, "construction": true});
            skLineSegment(sketch, "E9.11.1.1", {"start": v(240, 34.64) * mm, "end": v(230, 17.32) * mm, "construction": true});
            skLineSegment(sketch, "E9.11.1.2", {"start": v(250, 17.32) * mm, "end": v(240, 34.64) * mm, "construction": true});
            skLineSegment(sketch, "E9.11.1.3", {"start": v(220, 34.64) * mm, "end": v(240, 34.64) * mm, "construction": true});
            skLineSegment(sketch, "E9.11.1.4", {"start": v(230, 17.32) * mm, "end": v(220, 34.64) * mm, "construction": true});
            skLineSegment(sketch, "E9.11.1.5", {"start": v(230, 51.96) * mm, "end": v(220, 34.64) * mm, "construction": true});
            skLineSegment(sketch, "E9.11.1.6", {"start": v(240, 34.64) * mm, "end": v(230, 51.96) * mm, "construction": true});
            skLineSegment(sketch, "E9.11.1.7", {"start": v(230, 51.96) * mm, "end": v(250, 51.96) * mm, "construction": true});
            skLineSegment(sketch, "E9.11.1.8", {"start": v(250, 51.96) * mm, "end": v(240, 34.64) * mm, "construction": true});
            skLineSegment(sketch, "E9.11.2.0", {"start": v(230, 51.96) * mm, "end": v(250, 51.96) * mm, "construction": true});
            skLineSegment(sketch, "E9.11.2.1", {"start": v(240, 69.28) * mm, "end": v(230, 51.96) * mm, "construction": true});
            skLineSegment(sketch, "E9.11.2.2", {"start": v(250, 51.96) * mm, "end": v(240, 69.28) * mm, "construction": true});
            skLineSegment(sketch, "E9.11.2.3", {"start": v(220, 69.28) * mm, "end": v(240, 69.28) * mm, "construction": true});
            skLineSegment(sketch, "E9.11.2.4", {"start": v(230, 51.96) * mm, "end": v(220, 69.28) * mm, "construction": true});
            skLineSegment(sketch, "E9.11.2.5", {"start": v(230, 86.6) * mm, "end": v(220, 69.28) * mm, "construction": true});
            skLineSegment(sketch, "E9.11.2.6", {"start": v(240, 69.28) * mm, "end": v(230, 86.6) * mm, "construction": true});
            skLineSegment(sketch, "E9.11.2.7", {"start": v(230, 86.6) * mm, "end": v(250, 86.6) * mm, "construction": true});
            skLineSegment(sketch, "E9.11.2.8", {"start": v(250, 86.6) * mm, "end": v(240, 69.28) * mm, "construction": true});
            skLineSegment(sketch, "E9.11.3.0", {"start": v(230, 86.6) * mm, "end": v(250, 86.6) * mm, "construction": true});
            skLineSegment(sketch, "E9.11.3.1", {"start": v(240, 103.92) * mm, "end": v(230, 86.6) * mm, "construction": true});
            skLineSegment(sketch, "E9.11.3.2", {"start": v(250, 86.6) * mm, "end": v(240, 103.92) * mm, "construction": true});
            skLineSegment(sketch, "E9.11.3.3", {"start": v(220, 103.92) * mm, "end": v(240, 103.92) * mm, "construction": true});
            skLineSegment(sketch, "E9.11.3.4", {"start": v(230, 86.6) * mm, "end": v(220, 103.92) * mm, "construction": true});
            skLineSegment(sketch, "E9.11.3.5", {"start": v(230, 121.24) * mm, "end": v(220, 103.92) * mm, "construction": true});
            skLineSegment(sketch, "E9.11.3.6", {"start": v(240, 103.92) * mm, "end": v(230, 121.24) * mm, "construction": true});
            skLineSegment(sketch, "E9.11.3.7", {"start": v(230, 121.24) * mm, "end": v(250, 121.24) * mm, "construction": true});
            skLineSegment(sketch, "E9.11.3.8", {"start": v(250, 121.24) * mm, "end": v(240, 103.92) * mm, "construction": true});
            skLineSegment(sketch, "E9.11.4.0", {"start": v(230, 121.24) * mm, "end": v(250, 121.24) * mm, "construction": true});
            skLineSegment(sketch, "E9.11.4.1", {"start": v(240, 138.56) * mm, "end": v(230, 121.24) * mm, "construction": true});
            skLineSegment(sketch, "E9.11.4.2", {"start": v(250, 121.24) * mm, "end": v(240, 138.56) * mm, "construction": true});
            skLineSegment(sketch, "E9.11.4.3", {"start": v(220, 138.56) * mm, "end": v(240, 138.56) * mm, "construction": true});
            skLineSegment(sketch, "E9.11.4.4", {"start": v(230, 121.24) * mm, "end": v(220, 138.56) * mm, "construction": true});
            skLineSegment(sketch, "E9.11.4.5", {"start": v(230, 155.88) * mm, "end": v(220, 138.56) * mm, "construction": true});
            skLineSegment(sketch, "E9.11.4.6", {"start": v(240, 138.56) * mm, "end": v(230, 155.88) * mm, "construction": true});
            skLineSegment(sketch, "E9.11.4.7", {"start": v(230, 155.88) * mm, "end": v(250, 155.88) * mm, "construction": true});
            skLineSegment(sketch, "E9.11.4.8", {"start": v(250, 155.88) * mm, "end": v(240, 138.56) * mm, "construction": true});
            skLineSegment(sketch, "E9.11.5.0", {"start": v(230, 155.88) * mm, "end": v(250, 155.88) * mm, "construction": true});
            skLineSegment(sketch, "E9.11.5.1", {"start": v(240, 173.2) * mm, "end": v(230, 155.88) * mm, "construction": true});
            skLineSegment(sketch, "E9.11.5.2", {"start": v(250, 155.88) * mm, "end": v(240, 173.2) * mm, "construction": true});
            skLineSegment(sketch, "E9.11.5.3", {"start": v(220, 173.2) * mm, "end": v(240, 173.2) * mm, "construction": true});
            skLineSegment(sketch, "E9.11.5.4", {"start": v(230, 155.88) * mm, "end": v(220, 173.2) * mm, "construction": true});
            skLineSegment(sketch, "E9.11.5.5", {"start": v(230, 190.53) * mm, "end": v(220, 173.2) * mm, "construction": true});
            skLineSegment(sketch, "E9.11.5.6", {"start": v(240, 173.2) * mm, "end": v(230, 190.53) * mm, "construction": true});
            skLineSegment(sketch, "E9.11.5.7", {"start": v(230, 190.53) * mm, "end": v(250, 190.53) * mm, "construction": true});
            skLineSegment(sketch, "E9.11.5.8", {"start": v(250, 190.53) * mm, "end": v(240, 173.2) * mm, "construction": true});
            skLineSegment(sketch, "E9.11.6.0", {"start": v(230, 190.53) * mm, "end": v(250, 190.53) * mm, "construction": true});
            skLineSegment(sketch, "E9.11.6.1", {"start": v(240, 207.85) * mm, "end": v(230, 190.53) * mm, "construction": true});
            skLineSegment(sketch, "E9.11.6.2", {"start": v(250, 190.53) * mm, "end": v(240, 207.85) * mm, "construction": true});
            skLineSegment(sketch, "E9.11.6.3", {"start": v(220, 207.85) * mm, "end": v(240, 207.85) * mm, "construction": true});
            skLineSegment(sketch, "E9.11.6.4", {"start": v(230, 190.53) * mm, "end": v(220, 207.85) * mm, "construction": true});
            skLineSegment(sketch, "E9.11.6.5", {"start": v(230, 225.17) * mm, "end": v(220, 207.85) * mm, "construction": true});
            skLineSegment(sketch, "E9.11.6.6", {"start": v(240, 207.85) * mm, "end": v(230, 225.17) * mm, "construction": true});
            skLineSegment(sketch, "E9.11.6.7", {"start": v(230, 225.17) * mm, "end": v(250, 225.17) * mm, "construction": true});
            skLineSegment(sketch, "E9.11.6.8", {"start": v(250, 225.17) * mm, "end": v(240, 207.85) * mm, "construction": true});
            skLineSegment(sketch, "E9.12.0.0", {"start": v(250, -17.32) * mm, "end": v(270, -17.32) * mm, "construction": true});
            skLineSegment(sketch, "E9.12.0.1", {"start": v(260, 0) * mm, "end": v(250, -17.32) * mm, "construction": true});
            skLineSegment(sketch, "E9.12.0.2", {"start": v(270, -17.32) * mm, "end": v(260, 0) * mm, "construction": true});
            skLineSegment(sketch, "E9.12.0.3", {"start": v(240, 0) * mm, "end": v(260, 0) * mm, "construction": true});
            skLineSegment(sketch, "E9.12.0.4", {"start": v(250, -17.32) * mm, "end": v(240, 0) * mm, "construction": true});
            skLineSegment(sketch, "E9.12.0.5", {"start": v(250, 17.32) * mm, "end": v(240, 0) * mm, "construction": true});
            skLineSegment(sketch, "E9.12.0.6", {"start": v(260, 0) * mm, "end": v(250, 17.32) * mm, "construction": true});
            skLineSegment(sketch, "E9.12.0.7", {"start": v(250, 17.32) * mm, "end": v(270, 17.32) * mm, "construction": true});
            skLineSegment(sketch, "E9.12.0.8", {"start": v(270, 17.32) * mm, "end": v(260, 0) * mm, "construction": true});
            skLineSegment(sketch, "E9.12.1.0", {"start": v(250, 17.32) * mm, "end": v(270, 17.32) * mm, "construction": true});
            skLineSegment(sketch, "E9.12.1.1", {"start": v(260, 34.64) * mm, "end": v(250, 17.32) * mm, "construction": true});
            skLineSegment(sketch, "E9.12.1.2", {"start": v(270, 17.32) * mm, "end": v(260, 34.64) * mm, "construction": true});
            skLineSegment(sketch, "E9.12.1.3", {"start": v(240, 34.64) * mm, "end": v(260, 34.64) * mm, "construction": true});
            skLineSegment(sketch, "E9.12.1.4", {"start": v(250, 17.32) * mm, "end": v(240, 34.64) * mm, "construction": true});
            skLineSegment(sketch, "E9.12.1.5", {"start": v(250, 51.96) * mm, "end": v(240, 34.64) * mm, "construction": true});
            skLineSegment(sketch, "E9.12.1.6", {"start": v(260, 34.64) * mm, "end": v(250, 51.96) * mm, "construction": true});
            skLineSegment(sketch, "E9.12.1.7", {"start": v(250, 51.96) * mm, "end": v(270, 51.96) * mm, "construction": true});
            skLineSegment(sketch, "E9.12.1.8", {"start": v(270, 51.96) * mm, "end": v(260, 34.64) * mm, "construction": true});
            skLineSegment(sketch, "E9.12.2.0", {"start": v(250, 51.96) * mm, "end": v(270, 51.96) * mm, "construction": true});
            skLineSegment(sketch, "E9.12.2.1", {"start": v(260, 69.28) * mm, "end": v(250, 51.96) * mm, "construction": true});
            skLineSegment(sketch, "E9.12.2.2", {"start": v(270, 51.96) * mm, "end": v(260, 69.28) * mm, "construction": true});
            skLineSegment(sketch, "E9.12.2.3", {"start": v(240, 69.28) * mm, "end": v(260, 69.28) * mm, "construction": true});
            skLineSegment(sketch, "E9.12.2.4", {"start": v(250, 51.96) * mm, "end": v(240, 69.28) * mm, "construction": true});
            skLineSegment(sketch, "E9.12.2.5", {"start": v(250, 86.6) * mm, "end": v(240, 69.28) * mm, "construction": true});
            skLineSegment(sketch, "E9.12.2.6", {"start": v(260, 69.28) * mm, "end": v(250, 86.6) * mm, "construction": true});
            skLineSegment(sketch, "E9.12.2.7", {"start": v(250, 86.6) * mm, "end": v(270, 86.6) * mm, "construction": true});
            skLineSegment(sketch, "E9.12.2.8", {"start": v(270, 86.6) * mm, "end": v(260, 69.28) * mm, "construction": true});
            skLineSegment(sketch, "E9.12.3.0", {"start": v(250, 86.6) * mm, "end": v(270, 86.6) * mm, "construction": true});
            skLineSegment(sketch, "E9.12.3.1", {"start": v(260, 103.92) * mm, "end": v(250, 86.6) * mm, "construction": true});
            skLineSegment(sketch, "E9.12.3.2", {"start": v(270, 86.6) * mm, "end": v(260, 103.92) * mm, "construction": true});
            skLineSegment(sketch, "E9.12.3.3", {"start": v(240, 103.92) * mm, "end": v(260, 103.92) * mm, "construction": true});
            skLineSegment(sketch, "E9.12.3.4", {"start": v(250, 86.6) * mm, "end": v(240, 103.92) * mm, "construction": true});
            skLineSegment(sketch, "E9.12.3.5", {"start": v(250, 121.24) * mm, "end": v(240, 103.92) * mm, "construction": true});
            skLineSegment(sketch, "E9.12.3.6", {"start": v(260, 103.92) * mm, "end": v(250, 121.24) * mm, "construction": true});
            skLineSegment(sketch, "E9.12.3.7", {"start": v(250, 121.24) * mm, "end": v(270, 121.24) * mm, "construction": true});
            skLineSegment(sketch, "E9.12.3.8", {"start": v(270, 121.24) * mm, "end": v(260, 103.92) * mm, "construction": true});
            skLineSegment(sketch, "E9.12.4.0", {"start": v(250, 121.24) * mm, "end": v(270, 121.24) * mm, "construction": true});
            skLineSegment(sketch, "E9.12.4.1", {"start": v(260, 138.56) * mm, "end": v(250, 121.24) * mm, "construction": true});
            skLineSegment(sketch, "E9.12.4.2", {"start": v(270, 121.24) * mm, "end": v(260, 138.56) * mm, "construction": true});
            skLineSegment(sketch, "E9.12.4.3", {"start": v(240, 138.56) * mm, "end": v(260, 138.56) * mm, "construction": true});
            skLineSegment(sketch, "E9.12.4.4", {"start": v(250, 121.24) * mm, "end": v(240, 138.56) * mm, "construction": true});
            skLineSegment(sketch, "E9.12.4.5", {"start": v(250, 155.88) * mm, "end": v(240, 138.56) * mm, "construction": true});
            skLineSegment(sketch, "E9.12.4.6", {"start": v(260, 138.56) * mm, "end": v(250, 155.88) * mm, "construction": true});
            skLineSegment(sketch, "E9.12.4.7", {"start": v(250, 155.88) * mm, "end": v(270, 155.88) * mm, "construction": true});
            skLineSegment(sketch, "E9.12.4.8", {"start": v(270, 155.88) * mm, "end": v(260, 138.56) * mm, "construction": true});
            skLineSegment(sketch, "E9.12.5.0", {"start": v(250, 155.88) * mm, "end": v(270, 155.88) * mm, "construction": true});
            skLineSegment(sketch, "E9.12.5.1", {"start": v(260, 173.2) * mm, "end": v(250, 155.88) * mm, "construction": true});
            skLineSegment(sketch, "E9.12.5.2", {"start": v(270, 155.88) * mm, "end": v(260, 173.2) * mm, "construction": true});
            skLineSegment(sketch, "E9.12.5.3", {"start": v(240, 173.2) * mm, "end": v(260, 173.2) * mm, "construction": true});
            skLineSegment(sketch, "E9.12.5.4", {"start": v(250, 155.88) * mm, "end": v(240, 173.2) * mm, "construction": true});
            skLineSegment(sketch, "E9.12.5.5", {"start": v(250, 190.53) * mm, "end": v(240, 173.2) * mm, "construction": true});
            skLineSegment(sketch, "E9.12.5.6", {"start": v(260, 173.2) * mm, "end": v(250, 190.53) * mm, "construction": true});
            skLineSegment(sketch, "E9.12.5.7", {"start": v(250, 190.53) * mm, "end": v(270, 190.53) * mm, "construction": true});
            skLineSegment(sketch, "E9.12.5.8", {"start": v(270, 190.53) * mm, "end": v(260, 173.2) * mm, "construction": true});
            skLineSegment(sketch, "E9.12.6.0", {"start": v(250, 190.53) * mm, "end": v(270, 190.53) * mm, "construction": true});
            skLineSegment(sketch, "E9.12.6.1", {"start": v(260, 207.85) * mm, "end": v(250, 190.53) * mm, "construction": true});
            skLineSegment(sketch, "E9.12.6.2", {"start": v(270, 190.53) * mm, "end": v(260, 207.85) * mm, "construction": true});
            skLineSegment(sketch, "E9.12.6.3", {"start": v(240, 207.85) * mm, "end": v(260, 207.85) * mm, "construction": true});
            skLineSegment(sketch, "E9.12.6.4", {"start": v(250, 190.53) * mm, "end": v(240, 207.85) * mm, "construction": true});
            skLineSegment(sketch, "E9.12.6.5", {"start": v(250, 225.17) * mm, "end": v(240, 207.85) * mm, "construction": true});
            skLineSegment(sketch, "E9.12.6.6", {"start": v(260, 207.85) * mm, "end": v(250, 225.17) * mm, "construction": true});
            skLineSegment(sketch, "E9.12.6.7", {"start": v(250, 225.17) * mm, "end": v(270, 225.17) * mm, "construction": true});
            skLineSegment(sketch, "E9.12.6.8", {"start": v(270, 225.17) * mm, "end": v(260, 207.85) * mm, "construction": true});
            skLineSegment(sketch, "E9.13.0.0", {"start": v(270, -17.32) * mm, "end": v(290, -17.32) * mm, "construction": true});
            skLineSegment(sketch, "E9.13.0.1", {"start": v(280, 0) * mm, "end": v(270, -17.32) * mm, "construction": true});
            skLineSegment(sketch, "E9.13.0.2", {"start": v(290, -17.32) * mm, "end": v(280, 0) * mm, "construction": true});
            skLineSegment(sketch, "E9.13.0.3", {"start": v(260, 0) * mm, "end": v(280, 0) * mm, "construction": true});
            skLineSegment(sketch, "E9.13.0.4", {"start": v(270, -17.32) * mm, "end": v(260, 0) * mm, "construction": true});
            skLineSegment(sketch, "E9.13.0.5", {"start": v(270, 17.32) * mm, "end": v(260, 0) * mm, "construction": true});
            skLineSegment(sketch, "E9.13.0.6", {"start": v(280, 0) * mm, "end": v(270, 17.32) * mm, "construction": true});
            skLineSegment(sketch, "E9.13.0.7", {"start": v(270, 17.32) * mm, "end": v(290, 17.32) * mm, "construction": true});
            skLineSegment(sketch, "E9.13.0.8", {"start": v(290, 17.32) * mm, "end": v(280, 0) * mm, "construction": true});
            skLineSegment(sketch, "E9.13.1.0", {"start": v(270, 17.32) * mm, "end": v(290, 17.32) * mm, "construction": true});
            skLineSegment(sketch, "E9.13.1.1", {"start": v(280, 34.64) * mm, "end": v(270, 17.32) * mm, "construction": true});
            skLineSegment(sketch, "E9.13.1.2", {"start": v(290, 17.32) * mm, "end": v(280, 34.64) * mm, "construction": true});
            skLineSegment(sketch, "E9.13.1.3", {"start": v(260, 34.64) * mm, "end": v(280, 34.64) * mm, "construction": true});
            skLineSegment(sketch, "E9.13.1.4", {"start": v(270, 17.32) * mm, "end": v(260, 34.64) * mm, "construction": true});
            skLineSegment(sketch, "E9.13.1.5", {"start": v(270, 51.96) * mm, "end": v(260, 34.64) * mm, "construction": true});
            skLineSegment(sketch, "E9.13.1.6", {"start": v(280, 34.64) * mm, "end": v(270, 51.96) * mm, "construction": true});
            skLineSegment(sketch, "E9.13.1.7", {"start": v(270, 51.96) * mm, "end": v(290, 51.96) * mm, "construction": true});
            skLineSegment(sketch, "E9.13.1.8", {"start": v(290, 51.96) * mm, "end": v(280, 34.64) * mm, "construction": true});
            skLineSegment(sketch, "E9.13.2.0", {"start": v(270, 51.96) * mm, "end": v(290, 51.96) * mm, "construction": true});
            skLineSegment(sketch, "E9.13.2.1", {"start": v(280, 69.28) * mm, "end": v(270, 51.96) * mm, "construction": true});
            skLineSegment(sketch, "E9.13.2.2", {"start": v(290, 51.96) * mm, "end": v(280, 69.28) * mm, "construction": true});
            skLineSegment(sketch, "E9.13.2.3", {"start": v(260, 69.28) * mm, "end": v(280, 69.28) * mm, "construction": true});
            skLineSegment(sketch, "E9.13.2.4", {"start": v(270, 51.96) * mm, "end": v(260, 69.28) * mm, "construction": true});
            skLineSegment(sketch, "E9.13.2.5", {"start": v(270, 86.6) * mm, "end": v(260, 69.28) * mm, "construction": true});
            skLineSegment(sketch, "E9.13.2.6", {"start": v(280, 69.28) * mm, "end": v(270, 86.6) * mm, "construction": true});
            skLineSegment(sketch, "E9.13.2.7", {"start": v(270, 86.6) * mm, "end": v(290, 86.6) * mm, "construction": true});
            skLineSegment(sketch, "E9.13.2.8", {"start": v(290, 86.6) * mm, "end": v(280, 69.28) * mm, "construction": true});
            skLineSegment(sketch, "E9.13.3.0", {"start": v(270, 86.6) * mm, "end": v(290, 86.6) * mm, "construction": true});
            skLineSegment(sketch, "E9.13.3.1", {"start": v(280, 103.92) * mm, "end": v(270, 86.6) * mm, "construction": true});
            skLineSegment(sketch, "E9.13.3.2", {"start": v(290, 86.6) * mm, "end": v(280, 103.92) * mm, "construction": true});
            skLineSegment(sketch, "E9.13.3.3", {"start": v(260, 103.92) * mm, "end": v(280, 103.92) * mm, "construction": true});
            skLineSegment(sketch, "E9.13.3.4", {"start": v(270, 86.6) * mm, "end": v(260, 103.92) * mm, "construction": true});
            skLineSegment(sketch, "E9.13.3.5", {"start": v(270, 121.24) * mm, "end": v(260, 103.92) * mm, "construction": true});
            skLineSegment(sketch, "E9.13.3.6", {"start": v(280, 103.92) * mm, "end": v(270, 121.24) * mm, "construction": true});
            skLineSegment(sketch, "E9.13.3.7", {"start": v(270, 121.24) * mm, "end": v(290, 121.24) * mm, "construction": true});
            skLineSegment(sketch, "E9.13.3.8", {"start": v(290, 121.24) * mm, "end": v(280, 103.92) * mm, "construction": true});
            skLineSegment(sketch, "E9.13.4.0", {"start": v(270, 121.24) * mm, "end": v(290, 121.24) * mm, "construction": true});
            skLineSegment(sketch, "E9.13.4.1", {"start": v(280, 138.56) * mm, "end": v(270, 121.24) * mm, "construction": true});
            skLineSegment(sketch, "E9.13.4.2", {"start": v(290, 121.24) * mm, "end": v(280, 138.56) * mm, "construction": true});
            skLineSegment(sketch, "E9.13.4.3", {"start": v(260, 138.56) * mm, "end": v(280, 138.56) * mm, "construction": true});
            skLineSegment(sketch, "E9.13.4.4", {"start": v(270, 121.24) * mm, "end": v(260, 138.56) * mm, "construction": true});
            skLineSegment(sketch, "E9.13.4.5", {"start": v(270, 155.88) * mm, "end": v(260, 138.56) * mm, "construction": true});
            skLineSegment(sketch, "E9.13.4.6", {"start": v(280, 138.56) * mm, "end": v(270, 155.88) * mm, "construction": true});
            skLineSegment(sketch, "E9.13.4.7", {"start": v(270, 155.88) * mm, "end": v(290, 155.88) * mm, "construction": true});
            skLineSegment(sketch, "E9.13.4.8", {"start": v(290, 155.88) * mm, "end": v(280, 138.56) * mm, "construction": true});
            skLineSegment(sketch, "E9.13.5.0", {"start": v(270, 155.88) * mm, "end": v(290, 155.88) * mm, "construction": true});
            skLineSegment(sketch, "E9.13.5.1", {"start": v(280, 173.2) * mm, "end": v(270, 155.88) * mm, "construction": true});
            skLineSegment(sketch, "E9.13.5.2", {"start": v(290, 155.88) * mm, "end": v(280, 173.2) * mm, "construction": true});
            skLineSegment(sketch, "E9.13.5.3", {"start": v(260, 173.2) * mm, "end": v(280, 173.2) * mm, "construction": true});
            skLineSegment(sketch, "E9.13.5.4", {"start": v(270, 155.88) * mm, "end": v(260, 173.2) * mm, "construction": true});
            skLineSegment(sketch, "E9.13.5.5", {"start": v(270, 190.53) * mm, "end": v(260, 173.2) * mm, "construction": true});
            skLineSegment(sketch, "E9.13.5.6", {"start": v(280, 173.2) * mm, "end": v(270, 190.53) * mm, "construction": true});
            skLineSegment(sketch, "E9.13.5.7", {"start": v(270, 190.53) * mm, "end": v(290, 190.53) * mm, "construction": true});
            skLineSegment(sketch, "E9.13.5.8", {"start": v(290, 190.53) * mm, "end": v(280, 173.2) * mm, "construction": true});
            skLineSegment(sketch, "E9.13.6.0", {"start": v(270, 190.53) * mm, "end": v(290, 190.53) * mm, "construction": true});
            skLineSegment(sketch, "E9.13.6.1", {"start": v(280, 207.85) * mm, "end": v(270, 190.53) * mm, "construction": true});
            skLineSegment(sketch, "E9.13.6.2", {"start": v(290, 190.53) * mm, "end": v(280, 207.85) * mm, "construction": true});
            skLineSegment(sketch, "E9.13.6.3", {"start": v(260, 207.85) * mm, "end": v(280, 207.85) * mm, "construction": true});
            skLineSegment(sketch, "E9.13.6.4", {"start": v(270, 190.53) * mm, "end": v(260, 207.85) * mm, "construction": true});
            skLineSegment(sketch, "E9.13.6.5", {"start": v(270, 225.17) * mm, "end": v(260, 207.85) * mm, "construction": true});
            skLineSegment(sketch, "E9.13.6.6", {"start": v(280, 207.85) * mm, "end": v(270, 225.17) * mm, "construction": true});
            skLineSegment(sketch, "E9.13.6.7", {"start": v(270, 225.17) * mm, "end": v(290, 225.17) * mm, "construction": true});
            skLineSegment(sketch, "E9.13.6.8", {"start": v(290, 225.17) * mm, "end": v(280, 207.85) * mm, "construction": true});
            skLineSegment(sketch, "E9.direction2", {"start": v(10, -17.32) * mm, "end": v(10, 17.32) * mm, "construction": true});
            skLineSegment(sketch, "E10.bottom", {"start": v(-70, -44.58) * mm, "end": v(350, -44.58) * mm});
            skLineSegment(sketch, "E10.top", {"start": v(-70, 252.42) * mm, "end": v(350, 252.42) * mm});
            skLineSegment(sketch, "E10.left", {"start": v(-70, -44.58) * mm, "end": v(-70, 252.42) * mm});
            skLineSegment(sketch, "E10.right", {"start": v(350, -44.58) * mm, "end": v(350, 252.42) * mm});
            skPoint(sketch, "E10.middle", {"position": v(140, 103.92) * mm});
            skLineSegment(sketch, "E11", {"start": v(0.43, -0.25) * mm, "end": v(19.57, -0.25) * mm});
            skLineSegment(sketch, "E12", {"start": v(19.57, -0.25) * mm, "end": v(10, -16.82) * mm});
            skLineSegment(sketch, "E13", {"start": v(10, -16.82) * mm, "end": v(0.43, -0.25) * mm});
            skLineSegment(sketch, "E14.MirrorCS", {"start": v(0.43, 0.25) * mm, "end": v(19.57, 0.25) * mm});
            skLineSegment(sketch, "E15.MirrorCS", {"start": v(10, 16.82) * mm, "end": v(0.43, 0.25) * mm});
            skLineSegment(sketch, "E16.MirrorCS", {"start": v(19.57, 0.25) * mm, "end": v(10, 16.82) * mm});
            skLineSegment(sketch, "E17.MirrorCS", {"start": v(20, -0.5) * mm, "end": v(10.43, -17.07) * mm});
            skLineSegment(sketch, "E18.MirrorCS", {"start": v(29.57, -17.07) * mm, "end": v(20, -0.5) * mm});
            skLineSegment(sketch, "E19.MirrorCS", {"start": v(10.43, -17.07) * mm, "end": v(29.57, -17.07) * mm});
            skLineSegment(sketch, "E20.MirrorCS", {"start": v(20, 0.5) * mm, "end": v(10.43, 17.07) * mm});
            skLineSegment(sketch, "E21.MirrorCS", {"start": v(10.43, 17.07) * mm, "end": v(29.57, 17.07) * mm});
            skLineSegment(sketch, "E22.MirrorCS", {"start": v(29.57, 17.07) * mm, "end": v(20, 0.5) * mm});
            skLineSegment(sketch, "E23.0.1.0", {"start": v(10.43, 17.57) * mm, "end": v(29.57, 17.57) * mm});
            skLineSegment(sketch, "E23.0.1.1", {"start": v(20, 34.14) * mm, "end": v(10.43, 17.57) * mm});
            skLineSegment(sketch, "E23.0.1.2", {"start": v(29.57, 17.57) * mm, "end": v(20, 34.14) * mm});
            skLineSegment(sketch, "E23.0.1.3", {"start": v(0.43, 34.4) * mm, "end": v(19.57, 34.4) * mm});
            skLineSegment(sketch, "E23.0.1.4", {"start": v(19.57, 34.4) * mm, "end": v(10, 17.82) * mm});
            skLineSegment(sketch, "E23.0.1.5", {"start": v(10, 17.82) * mm, "end": v(0.43, 34.4) * mm});
            skLineSegment(sketch, "E23.0.1.6", {"start": v(10, 51.46) * mm, "end": v(0.43, 34.9) * mm});
            skLineSegment(sketch, "E23.0.1.7", {"start": v(0.43, 34.9) * mm, "end": v(19.57, 34.9) * mm});
            skLineSegment(sketch, "E23.0.1.8", {"start": v(19.57, 34.9) * mm, "end": v(10, 51.46) * mm});
            skLineSegment(sketch, "E23.0.1.9", {"start": v(20, 35.14) * mm, "end": v(10.43, 51.71) * mm});
            skLineSegment(sketch, "E23.0.1.10", {"start": v(29.57, 51.71) * mm, "end": v(20, 35.14) * mm});
            skLineSegment(sketch, "E23.0.1.11", {"start": v(10.43, 51.71) * mm, "end": v(29.57, 51.71) * mm});
            skLineSegment(sketch, "E23.0.2.0", {"start": v(10.43, 52.21) * mm, "end": v(29.57, 52.21) * mm});
            skLineSegment(sketch, "E23.0.2.1", {"start": v(20, 68.78) * mm, "end": v(10.43, 52.21) * mm});
            skLineSegment(sketch, "E23.0.2.2", {"start": v(29.57, 52.21) * mm, "end": v(20, 68.78) * mm});
            skLineSegment(sketch, "E23.0.2.3", {"start": v(0.43, 69.03) * mm, "end": v(19.57, 69.03) * mm});
            skLineSegment(sketch, "E23.0.2.4", {"start": v(19.57, 69.03) * mm, "end": v(10, 52.46) * mm});
            skLineSegment(sketch, "E23.0.2.5", {"start": v(10, 52.46) * mm, "end": v(0.43, 69.03) * mm});
            skLineSegment(sketch, "E23.0.2.6", {"start": v(10, 86.1) * mm, "end": v(0.43, 69.53) * mm});
            skLineSegment(sketch, "E23.0.2.7", {"start": v(0.43, 69.53) * mm, "end": v(19.57, 69.53) * mm});
            skLineSegment(sketch, "E23.0.2.8", {"start": v(19.57, 69.53) * mm, "end": v(10, 86.1) * mm});
            skLineSegment(sketch, "E23.0.2.9", {"start": v(20, 69.78) * mm, "end": v(10.43, 86.35) * mm});
            skLineSegment(sketch, "E23.0.2.10", {"start": v(29.57, 86.35) * mm, "end": v(20, 69.78) * mm});
            skLineSegment(sketch, "E23.0.2.11", {"start": v(10.43, 86.35) * mm, "end": v(29.57, 86.35) * mm});
            skLineSegment(sketch, "E23.0.3.0", {"start": v(10.43, 86.85) * mm, "end": v(29.57, 86.85) * mm});
            skLineSegment(sketch, "E23.0.3.1", {"start": v(20, 103.42) * mm, "end": v(10.43, 86.85) * mm});
            skLineSegment(sketch, "E23.0.3.2", {"start": v(29.57, 86.85) * mm, "end": v(20, 103.42) * mm});
            skLineSegment(sketch, "E23.0.3.3", {"start": v(0.43, 103.67) * mm, "end": v(19.57, 103.67) * mm});
            skLineSegment(sketch, "E23.0.3.4", {"start": v(19.57, 103.67) * mm, "end": v(10, 87.1) * mm});
            skLineSegment(sketch, "E23.0.3.5", {"start": v(10, 87.1) * mm, "end": v(0.43, 103.67) * mm});
            skLineSegment(sketch, "E23.0.3.6", {"start": v(10, 120.74) * mm, "end": v(0.43, 104.17) * mm});
            skLineSegment(sketch, "E23.0.3.7", {"start": v(0.43, 104.17) * mm, "end": v(19.57, 104.17) * mm});
            skLineSegment(sketch, "E23.0.3.8", {"start": v(19.57, 104.17) * mm, "end": v(10, 120.74) * mm});
            skLineSegment(sketch, "E23.0.3.9", {"start": v(20, 104.42) * mm, "end": v(10.43, 121) * mm});
            skLineSegment(sketch, "E23.0.3.10", {"start": v(29.57, 121) * mm, "end": v(20, 104.42) * mm});
            skLineSegment(sketch, "E23.0.3.11", {"start": v(10.43, 121) * mm, "end": v(29.57, 121) * mm});
            skLineSegment(sketch, "E23.0.4.0", {"start": v(10.43, 121.5) * mm, "end": v(29.57, 121.5) * mm});
            skLineSegment(sketch, "E23.0.4.1", {"start": v(20, 138.06) * mm, "end": v(10.43, 121.5) * mm});
            skLineSegment(sketch, "E23.0.4.2", {"start": v(29.57, 121.5) * mm, "end": v(20, 138.06) * mm});
            skLineSegment(sketch, "E23.0.4.3", {"start": v(0.43, 138.31) * mm, "end": v(19.57, 138.31) * mm});
            skLineSegment(sketch, "E23.0.4.4", {"start": v(19.57, 138.31) * mm, "end": v(10, 121.74) * mm});
            skLineSegment(sketch, "E23.0.4.5", {"start": v(10, 121.74) * mm, "end": v(0.43, 138.31) * mm});
            skLineSegment(sketch, "E23.0.4.6", {"start": v(10, 155.38) * mm, "end": v(0.43, 138.81) * mm});
            skLineSegment(sketch, "E23.0.4.7", {"start": v(0.43, 138.81) * mm, "end": v(19.57, 138.81) * mm});
            skLineSegment(sketch, "E23.0.4.8", {"start": v(19.57, 138.81) * mm, "end": v(10, 155.38) * mm});
            skLineSegment(sketch, "E23.0.4.9", {"start": v(20, 139.06) * mm, "end": v(10.43, 155.63) * mm});
            skLineSegment(sketch, "E23.0.4.10", {"start": v(29.57, 155.63) * mm, "end": v(20, 139.06) * mm});
            skLineSegment(sketch, "E23.0.4.11", {"start": v(10.43, 155.63) * mm, "end": v(29.57, 155.63) * mm});
            skLineSegment(sketch, "E23.0.5.0", {"start": v(10.43, 156.13) * mm, "end": v(29.57, 156.13) * mm});
            skLineSegment(sketch, "E23.0.5.1", {"start": v(20, 172.7) * mm, "end": v(10.43, 156.13) * mm});
            skLineSegment(sketch, "E23.0.5.2", {"start": v(29.57, 156.13) * mm, "end": v(20, 172.7) * mm});
            skLineSegment(sketch, "E23.0.5.3", {"start": v(0.43, 172.96) * mm, "end": v(19.57, 172.96) * mm});
            skLineSegment(sketch, "E23.0.5.4", {"start": v(19.57, 172.96) * mm, "end": v(10, 156.38) * mm});
            skLineSegment(sketch, "E23.0.5.5", {"start": v(10, 156.38) * mm, "end": v(0.43, 172.96) * mm});
            skLineSegment(sketch, "E23.0.5.6", {"start": v(10, 190.03) * mm, "end": v(0.43, 173.46) * mm});
            skLineSegment(sketch, "E23.0.5.7", {"start": v(0.43, 173.46) * mm, "end": v(19.57, 173.46) * mm});
            skLineSegment(sketch, "E23.0.5.8", {"start": v(19.57, 173.46) * mm, "end": v(10, 190.03) * mm});
            skLineSegment(sketch, "E23.0.5.9", {"start": v(20, 173.7) * mm, "end": v(10.43, 190.28) * mm});
            skLineSegment(sketch, "E23.0.5.10", {"start": v(29.57, 190.28) * mm, "end": v(20, 173.7) * mm});
            skLineSegment(sketch, "E23.0.5.11", {"start": v(10.43, 190.28) * mm, "end": v(29.57, 190.28) * mm});
            skLineSegment(sketch, "E23.0.6.0", {"start": v(10.43, 190.78) * mm, "end": v(29.57, 190.78) * mm});
            skLineSegment(sketch, "E23.0.6.1", {"start": v(20, 207.35) * mm, "end": v(10.43, 190.78) * mm});
            skLineSegment(sketch, "E23.0.6.2", {"start": v(29.57, 190.78) * mm, "end": v(20, 207.35) * mm});
            skLineSegment(sketch, "E23.0.6.3", {"start": v(0.43, 207.6) * mm, "end": v(19.57, 207.6) * mm});
            skLineSegment(sketch, "E23.0.6.4", {"start": v(19.57, 207.6) * mm, "end": v(10, 191.03) * mm});
            skLineSegment(sketch, "E23.0.6.5", {"start": v(10, 191.03) * mm, "end": v(0.43, 207.6) * mm});
            skLineSegment(sketch, "E23.0.6.6", {"start": v(10, 224.67) * mm, "end": v(0.43, 208.1) * mm});
            skLineSegment(sketch, "E23.0.6.7", {"start": v(0.43, 208.1) * mm, "end": v(19.57, 208.1) * mm});
            skLineSegment(sketch, "E23.0.6.8", {"start": v(19.57, 208.1) * mm, "end": v(10, 224.67) * mm});
            skLineSegment(sketch, "E23.0.6.9", {"start": v(20, 208.35) * mm, "end": v(10.43, 224.92) * mm});
            skLineSegment(sketch, "E23.0.6.10", {"start": v(29.57, 224.92) * mm, "end": v(20, 208.35) * mm});
            skLineSegment(sketch, "E23.0.6.11", {"start": v(10.43, 224.92) * mm, "end": v(29.57, 224.92) * mm});
            skLineSegment(sketch, "E23.1.0.0", {"start": v(30.43, -17.07) * mm, "end": v(49.57, -17.07) * mm});
            skLineSegment(sketch, "E23.1.0.1", {"start": v(40, -0.5) * mm, "end": v(30.43, -17.07) * mm});
            skLineSegment(sketch, "E23.1.0.2", {"start": v(49.57, -17.07) * mm, "end": v(40, -0.5) * mm});
            skLineSegment(sketch, "E23.1.0.3", {"start": v(20.43, -0.25) * mm, "end": v(39.57, -0.25) * mm});
            skLineSegment(sketch, "E23.1.0.4", {"start": v(39.57, -0.25) * mm, "end": v(30, -16.82) * mm});
            skLineSegment(sketch, "E23.1.0.5", {"start": v(30, -16.82) * mm, "end": v(20.43, -0.25) * mm});
            skLineSegment(sketch, "E23.1.0.6", {"start": v(30, 16.82) * mm, "end": v(20.43, 0.25) * mm});
            skLineSegment(sketch, "E23.1.0.7", {"start": v(20.43, 0.25) * mm, "end": v(39.57, 0.25) * mm});
            skLineSegment(sketch, "E23.1.0.8", {"start": v(39.57, 0.25) * mm, "end": v(30, 16.82) * mm});
            skLineSegment(sketch, "E23.1.0.9", {"start": v(40, 0.5) * mm, "end": v(30.43, 17.07) * mm});
            skLineSegment(sketch, "E23.1.0.10", {"start": v(49.57, 17.07) * mm, "end": v(40, 0.5) * mm});
            skLineSegment(sketch, "E23.1.0.11", {"start": v(30.43, 17.07) * mm, "end": v(49.57, 17.07) * mm});
            skLineSegment(sketch, "E23.1.1.0", {"start": v(30.43, 17.57) * mm, "end": v(49.57, 17.57) * mm});
            skLineSegment(sketch, "E23.1.1.1", {"start": v(40, 34.14) * mm, "end": v(30.43, 17.57) * mm});
            skLineSegment(sketch, "E23.1.1.2", {"start": v(49.57, 17.57) * mm, "end": v(40, 34.14) * mm});
            skLineSegment(sketch, "E23.1.1.3", {"start": v(20.43, 34.4) * mm, "end": v(39.57, 34.4) * mm});
            skLineSegment(sketch, "E23.1.1.4", {"start": v(39.57, 34.4) * mm, "end": v(30, 17.82) * mm});
            skLineSegment(sketch, "E23.1.1.5", {"start": v(30, 17.82) * mm, "end": v(20.43, 34.4) * mm});
            skLineSegment(sketch, "E23.1.1.6", {"start": v(30, 51.46) * mm, "end": v(20.43, 34.9) * mm});
            skLineSegment(sketch, "E23.1.1.7", {"start": v(20.43, 34.9) * mm, "end": v(39.57, 34.9) * mm});
            skLineSegment(sketch, "E23.1.1.8", {"start": v(39.57, 34.9) * mm, "end": v(30, 51.46) * mm});
            skLineSegment(sketch, "E23.1.1.9", {"start": v(40, 35.14) * mm, "end": v(30.43, 51.71) * mm});
            skLineSegment(sketch, "E23.1.1.10", {"start": v(49.57, 51.71) * mm, "end": v(40, 35.14) * mm});
            skLineSegment(sketch, "E23.1.1.11", {"start": v(30.43, 51.71) * mm, "end": v(49.57, 51.71) * mm});
            skLineSegment(sketch, "E23.1.2.0", {"start": v(30.43, 52.21) * mm, "end": v(49.57, 52.21) * mm});
            skLineSegment(sketch, "E23.1.2.1", {"start": v(40, 68.78) * mm, "end": v(30.43, 52.21) * mm});
            skLineSegment(sketch, "E23.1.2.2", {"start": v(49.57, 52.21) * mm, "end": v(40, 68.78) * mm});
            skLineSegment(sketch, "E23.1.2.3", {"start": v(20.43, 69.03) * mm, "end": v(39.57, 69.03) * mm});
            skLineSegment(sketch, "E23.1.2.4", {"start": v(39.57, 69.03) * mm, "end": v(30, 52.46) * mm});
            skLineSegment(sketch, "E23.1.2.5", {"start": v(30, 52.46) * mm, "end": v(20.43, 69.03) * mm});
            skLineSegment(sketch, "E23.1.2.6", {"start": v(30, 86.1) * mm, "end": v(20.43, 69.53) * mm});
            skLineSegment(sketch, "E23.1.2.7", {"start": v(20.43, 69.53) * mm, "end": v(39.57, 69.53) * mm});
            skLineSegment(sketch, "E23.1.2.8", {"start": v(39.57, 69.53) * mm, "end": v(30, 86.1) * mm});
            skLineSegment(sketch, "E23.1.2.9", {"start": v(40, 69.78) * mm, "end": v(30.43, 86.35) * mm});
            skLineSegment(sketch, "E23.1.2.10", {"start": v(49.57, 86.35) * mm, "end": v(40, 69.78) * mm});
            skLineSegment(sketch, "E23.1.2.11", {"start": v(30.43, 86.35) * mm, "end": v(49.57, 86.35) * mm});
            skLineSegment(sketch, "E23.1.3.0", {"start": v(30.43, 86.85) * mm, "end": v(49.57, 86.85) * mm});
            skLineSegment(sketch, "E23.1.3.1", {"start": v(40, 103.42) * mm, "end": v(30.43, 86.85) * mm});
            skLineSegment(sketch, "E23.1.3.2", {"start": v(49.57, 86.85) * mm, "end": v(40, 103.42) * mm});
            skLineSegment(sketch, "E23.1.3.3", {"start": v(20.43, 103.67) * mm, "end": v(39.57, 103.67) * mm});
            skLineSegment(sketch, "E23.1.3.4", {"start": v(39.57, 103.67) * mm, "end": v(30, 87.1) * mm});
            skLineSegment(sketch, "E23.1.3.5", {"start": v(30, 87.1) * mm, "end": v(20.43, 103.67) * mm});
            skLineSegment(sketch, "E23.1.3.6", {"start": v(30, 120.74) * mm, "end": v(20.43, 104.17) * mm});
            skLineSegment(sketch, "E23.1.3.7", {"start": v(20.43, 104.17) * mm, "end": v(39.57, 104.17) * mm});
            skLineSegment(sketch, "E23.1.3.8", {"start": v(39.57, 104.17) * mm, "end": v(30, 120.74) * mm});
            skLineSegment(sketch, "E23.1.3.9", {"start": v(40, 104.42) * mm, "end": v(30.43, 121) * mm});
            skLineSegment(sketch, "E23.1.3.10", {"start": v(49.57, 121) * mm, "end": v(40, 104.42) * mm});
            skLineSegment(sketch, "E23.1.3.11", {"start": v(30.43, 121) * mm, "end": v(49.57, 121) * mm});
            skLineSegment(sketch, "E23.1.4.0", {"start": v(30.43, 121.5) * mm, "end": v(49.57, 121.5) * mm});
            skLineSegment(sketch, "E23.1.4.1", {"start": v(40, 138.06) * mm, "end": v(30.43, 121.5) * mm});
            skLineSegment(sketch, "E23.1.4.2", {"start": v(49.57, 121.5) * mm, "end": v(40, 138.06) * mm});
            skLineSegment(sketch, "E23.1.4.3", {"start": v(20.43, 138.31) * mm, "end": v(39.57, 138.31) * mm});
            skLineSegment(sketch, "E23.1.4.4", {"start": v(39.57, 138.31) * mm, "end": v(30, 121.74) * mm});
            skLineSegment(sketch, "E23.1.4.5", {"start": v(30, 121.74) * mm, "end": v(20.43, 138.31) * mm});
            skLineSegment(sketch, "E23.1.4.6", {"start": v(30, 155.38) * mm, "end": v(20.43, 138.81) * mm});
            skLineSegment(sketch, "E23.1.4.7", {"start": v(20.43, 138.81) * mm, "end": v(39.57, 138.81) * mm});
            skLineSegment(sketch, "E23.1.4.8", {"start": v(39.57, 138.81) * mm, "end": v(30, 155.38) * mm});
            skLineSegment(sketch, "E23.1.4.9", {"start": v(40, 139.06) * mm, "end": v(30.43, 155.63) * mm});
            skLineSegment(sketch, "E23.1.4.10", {"start": v(49.57, 155.63) * mm, "end": v(40, 139.06) * mm});
            skLineSegment(sketch, "E23.1.4.11", {"start": v(30.43, 155.63) * mm, "end": v(49.57, 155.63) * mm});
            skLineSegment(sketch, "E23.1.5.0", {"start": v(30.43, 156.13) * mm, "end": v(49.57, 156.13) * mm});
            skLineSegment(sketch, "E23.1.5.1", {"start": v(40, 172.7) * mm, "end": v(30.43, 156.13) * mm});
            skLineSegment(sketch, "E23.1.5.2", {"start": v(49.57, 156.13) * mm, "end": v(40, 172.7) * mm});
            skLineSegment(sketch, "E23.1.5.3", {"start": v(20.43, 172.96) * mm, "end": v(39.57, 172.96) * mm});
            skLineSegment(sketch, "E23.1.5.4", {"start": v(39.57, 172.96) * mm, "end": v(30, 156.38) * mm});
            skLineSegment(sketch, "E23.1.5.5", {"start": v(30, 156.38) * mm, "end": v(20.43, 172.96) * mm});
            skLineSegment(sketch, "E23.1.5.6", {"start": v(30, 190.03) * mm, "end": v(20.43, 173.46) * mm});
            skLineSegment(sketch, "E23.1.5.7", {"start": v(20.43, 173.46) * mm, "end": v(39.57, 173.46) * mm});
            skLineSegment(sketch, "E23.1.5.8", {"start": v(39.57, 173.46) * mm, "end": v(30, 190.03) * mm});
            skLineSegment(sketch, "E23.1.5.9", {"start": v(40, 173.7) * mm, "end": v(30.43, 190.28) * mm});
            skLineSegment(sketch, "E23.1.5.10", {"start": v(49.57, 190.28) * mm, "end": v(40, 173.7) * mm});
            skLineSegment(sketch, "E23.1.5.11", {"start": v(30.43, 190.28) * mm, "end": v(49.57, 190.28) * mm});
            skLineSegment(sketch, "E23.1.6.0", {"start": v(30.43, 190.78) * mm, "end": v(49.57, 190.78) * mm});
            skLineSegment(sketch, "E23.1.6.1", {"start": v(40, 207.35) * mm, "end": v(30.43, 190.78) * mm});
            skLineSegment(sketch, "E23.1.6.2", {"start": v(49.57, 190.78) * mm, "end": v(40, 207.35) * mm});
            skLineSegment(sketch, "E23.1.6.3", {"start": v(20.43, 207.6) * mm, "end": v(39.57, 207.6) * mm});
            skLineSegment(sketch, "E23.1.6.4", {"start": v(39.57, 207.6) * mm, "end": v(30, 191.03) * mm});
            skLineSegment(sketch, "E23.1.6.5", {"start": v(30, 191.03) * mm, "end": v(20.43, 207.6) * mm});
            skLineSegment(sketch, "E23.1.6.6", {"start": v(30, 224.67) * mm, "end": v(20.43, 208.1) * mm});
            skLineSegment(sketch, "E23.1.6.7", {"start": v(20.43, 208.1) * mm, "end": v(39.57, 208.1) * mm});
            skLineSegment(sketch, "E23.1.6.8", {"start": v(39.57, 208.1) * mm, "end": v(30, 224.67) * mm});
            skLineSegment(sketch, "E23.1.6.9", {"start": v(40, 208.35) * mm, "end": v(30.43, 224.92) * mm});
            skLineSegment(sketch, "E23.1.6.10", {"start": v(49.57, 224.92) * mm, "end": v(40, 208.35) * mm});
            skLineSegment(sketch, "E23.1.6.11", {"start": v(30.43, 224.92) * mm, "end": v(49.57, 224.92) * mm});
            skLineSegment(sketch, "E23.2.0.0", {"start": v(50.43, -17.07) * mm, "end": v(69.57, -17.07) * mm});
            skLineSegment(sketch, "E23.2.0.1", {"start": v(60, -0.5) * mm, "end": v(50.43, -17.07) * mm});
            skLineSegment(sketch, "E23.2.0.2", {"start": v(69.57, -17.07) * mm, "end": v(60, -0.5) * mm});
            skLineSegment(sketch, "E23.2.0.3", {"start": v(40.43, -0.25) * mm, "end": v(59.57, -0.25) * mm});
            skLineSegment(sketch, "E23.2.0.4", {"start": v(59.57, -0.25) * mm, "end": v(50, -16.82) * mm});
            skLineSegment(sketch, "E23.2.0.5", {"start": v(50, -16.82) * mm, "end": v(40.43, -0.25) * mm});
            skLineSegment(sketch, "E23.2.0.6", {"start": v(50, 16.82) * mm, "end": v(40.43, 0.25) * mm});
            skLineSegment(sketch, "E23.2.0.7", {"start": v(40.43, 0.25) * mm, "end": v(59.57, 0.25) * mm});
            skLineSegment(sketch, "E23.2.0.8", {"start": v(59.57, 0.25) * mm, "end": v(50, 16.82) * mm});
            skLineSegment(sketch, "E23.2.0.9", {"start": v(60, 0.5) * mm, "end": v(50.43, 17.07) * mm});
            skLineSegment(sketch, "E23.2.0.10", {"start": v(69.57, 17.07) * mm, "end": v(60, 0.5) * mm});
            skLineSegment(sketch, "E23.2.0.11", {"start": v(50.43, 17.07) * mm, "end": v(69.57, 17.07) * mm});
            skLineSegment(sketch, "E23.2.1.0", {"start": v(50.43, 17.57) * mm, "end": v(69.57, 17.57) * mm});
            skLineSegment(sketch, "E23.2.1.1", {"start": v(60, 34.14) * mm, "end": v(50.43, 17.57) * mm});
            skLineSegment(sketch, "E23.2.1.2", {"start": v(69.57, 17.57) * mm, "end": v(60, 34.14) * mm});
            skLineSegment(sketch, "E23.2.1.3", {"start": v(40.43, 34.4) * mm, "end": v(59.57, 34.4) * mm});
            skLineSegment(sketch, "E23.2.1.4", {"start": v(59.57, 34.4) * mm, "end": v(50, 17.82) * mm});
            skLineSegment(sketch, "E23.2.1.5", {"start": v(50, 17.82) * mm, "end": v(40.43, 34.4) * mm});
            skLineSegment(sketch, "E23.2.1.6", {"start": v(50, 51.46) * mm, "end": v(40.43, 34.9) * mm});
            skLineSegment(sketch, "E23.2.1.7", {"start": v(40.43, 34.9) * mm, "end": v(59.57, 34.9) * mm});
            skLineSegment(sketch, "E23.2.1.8", {"start": v(59.57, 34.9) * mm, "end": v(50, 51.46) * mm});
            skLineSegment(sketch, "E23.2.1.9", {"start": v(60, 35.14) * mm, "end": v(50.43, 51.71) * mm});
            skLineSegment(sketch, "E23.2.1.10", {"start": v(69.57, 51.71) * mm, "end": v(60, 35.14) * mm});
            skLineSegment(sketch, "E23.2.1.11", {"start": v(50.43, 51.71) * mm, "end": v(69.57, 51.71) * mm});
            skLineSegment(sketch, "E23.2.2.0", {"start": v(50.43, 52.21) * mm, "end": v(69.57, 52.21) * mm});
            skLineSegment(sketch, "E23.2.2.1", {"start": v(60, 68.78) * mm, "end": v(50.43, 52.21) * mm});
            skLineSegment(sketch, "E23.2.2.2", {"start": v(69.57, 52.21) * mm, "end": v(60, 68.78) * mm});
            skLineSegment(sketch, "E23.2.2.3", {"start": v(40.43, 69.03) * mm, "end": v(59.57, 69.03) * mm});
            skLineSegment(sketch, "E23.2.2.4", {"start": v(59.57, 69.03) * mm, "end": v(50, 52.46) * mm});
            skLineSegment(sketch, "E23.2.2.5", {"start": v(50, 52.46) * mm, "end": v(40.43, 69.03) * mm});
            skLineSegment(sketch, "E23.2.2.6", {"start": v(50, 86.1) * mm, "end": v(40.43, 69.53) * mm});
            skLineSegment(sketch, "E23.2.2.7", {"start": v(40.43, 69.53) * mm, "end": v(59.57, 69.53) * mm});
            skLineSegment(sketch, "E23.2.2.8", {"start": v(59.57, 69.53) * mm, "end": v(50, 86.1) * mm});
            skLineSegment(sketch, "E23.2.2.9", {"start": v(60, 69.78) * mm, "end": v(50.43, 86.35) * mm});
            skLineSegment(sketch, "E23.2.2.10", {"start": v(69.57, 86.35) * mm, "end": v(60, 69.78) * mm});
            skLineSegment(sketch, "E23.2.2.11", {"start": v(50.43, 86.35) * mm, "end": v(69.57, 86.35) * mm});
            skLineSegment(sketch, "E23.2.3.0", {"start": v(50.43, 86.85) * mm, "end": v(69.57, 86.85) * mm});
            skLineSegment(sketch, "E23.2.3.1", {"start": v(60, 103.42) * mm, "end": v(50.43, 86.85) * mm});
            skLineSegment(sketch, "E23.2.3.2", {"start": v(69.57, 86.85) * mm, "end": v(60, 103.42) * mm});
            skLineSegment(sketch, "E23.2.3.3", {"start": v(40.43, 103.67) * mm, "end": v(59.57, 103.67) * mm});
            skLineSegment(sketch, "E23.2.3.4", {"start": v(59.57, 103.67) * mm, "end": v(50, 87.1) * mm});
            skLineSegment(sketch, "E23.2.3.5", {"start": v(50, 87.1) * mm, "end": v(40.43, 103.67) * mm});
            skLineSegment(sketch, "E23.2.3.6", {"start": v(50, 120.74) * mm, "end": v(40.43, 104.17) * mm});
            skLineSegment(sketch, "E23.2.3.7", {"start": v(40.43, 104.17) * mm, "end": v(59.57, 104.17) * mm});
            skLineSegment(sketch, "E23.2.3.8", {"start": v(59.57, 104.17) * mm, "end": v(50, 120.74) * mm});
            skLineSegment(sketch, "E23.2.3.9", {"start": v(60, 104.42) * mm, "end": v(50.43, 121) * mm});
            skLineSegment(sketch, "E23.2.3.10", {"start": v(69.57, 121) * mm, "end": v(60, 104.42) * mm});
            skLineSegment(sketch, "E23.2.3.11", {"start": v(50.43, 121) * mm, "end": v(69.57, 121) * mm});
            skLineSegment(sketch, "E23.2.4.0", {"start": v(50.43, 121.5) * mm, "end": v(69.57, 121.5) * mm});
            skLineSegment(sketch, "E23.2.4.1", {"start": v(60, 138.06) * mm, "end": v(50.43, 121.5) * mm});
            skLineSegment(sketch, "E23.2.4.2", {"start": v(69.57, 121.5) * mm, "end": v(60, 138.06) * mm});
            skLineSegment(sketch, "E23.2.4.3", {"start": v(40.43, 138.31) * mm, "end": v(59.57, 138.31) * mm});
            skLineSegment(sketch, "E23.2.4.4", {"start": v(59.57, 138.31) * mm, "end": v(50, 121.74) * mm});
            skLineSegment(sketch, "E23.2.4.5", {"start": v(50, 121.74) * mm, "end": v(40.43, 138.31) * mm});
            skLineSegment(sketch, "E23.2.4.6", {"start": v(50, 155.38) * mm, "end": v(40.43, 138.81) * mm});
            skLineSegment(sketch, "E23.2.4.7", {"start": v(40.43, 138.81) * mm, "end": v(59.57, 138.81) * mm});
            skLineSegment(sketch, "E23.2.4.8", {"start": v(59.57, 138.81) * mm, "end": v(50, 155.38) * mm});
            skLineSegment(sketch, "E23.2.4.9", {"start": v(60, 139.06) * mm, "end": v(50.43, 155.63) * mm});
            skLineSegment(sketch, "E23.2.4.10", {"start": v(69.57, 155.63) * mm, "end": v(60, 139.06) * mm});
            skLineSegment(sketch, "E23.2.4.11", {"start": v(50.43, 155.63) * mm, "end": v(69.57, 155.63) * mm});
            skLineSegment(sketch, "E23.2.5.0", {"start": v(50.43, 156.13) * mm, "end": v(69.57, 156.13) * mm});
            skLineSegment(sketch, "E23.2.5.1", {"start": v(60, 172.7) * mm, "end": v(50.43, 156.13) * mm});
            skLineSegment(sketch, "E23.2.5.2", {"start": v(69.57, 156.13) * mm, "end": v(60, 172.7) * mm});
            skLineSegment(sketch, "E23.2.5.3", {"start": v(40.43, 172.96) * mm, "end": v(59.57, 172.96) * mm});
            skLineSegment(sketch, "E23.2.5.4", {"start": v(59.57, 172.96) * mm, "end": v(50, 156.38) * mm});
            skLineSegment(sketch, "E23.2.5.5", {"start": v(50, 156.38) * mm, "end": v(40.43, 172.96) * mm});
            skLineSegment(sketch, "E23.2.5.6", {"start": v(50, 190.03) * mm, "end": v(40.43, 173.46) * mm});
            skLineSegment(sketch, "E23.2.5.7", {"start": v(40.43, 173.46) * mm, "end": v(59.57, 173.46) * mm});
            skLineSegment(sketch, "E23.2.5.8", {"start": v(59.57, 173.46) * mm, "end": v(50, 190.03) * mm});
            skLineSegment(sketch, "E23.2.5.9", {"start": v(60, 173.7) * mm, "end": v(50.43, 190.28) * mm});
            skLineSegment(sketch, "E23.2.5.10", {"start": v(69.57, 190.28) * mm, "end": v(60, 173.7) * mm});
            skLineSegment(sketch, "E23.2.5.11", {"start": v(50.43, 190.28) * mm, "end": v(69.57, 190.28) * mm});
            skLineSegment(sketch, "E23.2.6.0", {"start": v(50.43, 190.78) * mm, "end": v(69.57, 190.78) * mm});
            skLineSegment(sketch, "E23.2.6.1", {"start": v(60, 207.35) * mm, "end": v(50.43, 190.78) * mm});
            skLineSegment(sketch, "E23.2.6.2", {"start": v(69.57, 190.78) * mm, "end": v(60, 207.35) * mm});
            skLineSegment(sketch, "E23.2.6.3", {"start": v(40.43, 207.6) * mm, "end": v(59.57, 207.6) * mm});
            skLineSegment(sketch, "E23.2.6.4", {"start": v(59.57, 207.6) * mm, "end": v(50, 191.03) * mm});
            skLineSegment(sketch, "E23.2.6.5", {"start": v(50, 191.03) * mm, "end": v(40.43, 207.6) * mm});
            skLineSegment(sketch, "E23.2.6.6", {"start": v(50, 224.67) * mm, "end": v(40.43, 208.1) * mm});
            skLineSegment(sketch, "E23.2.6.7", {"start": v(40.43, 208.1) * mm, "end": v(59.57, 208.1) * mm});
            skLineSegment(sketch, "E23.2.6.8", {"start": v(59.57, 208.1) * mm, "end": v(50, 224.67) * mm});
            skLineSegment(sketch, "E23.2.6.9", {"start": v(60, 208.35) * mm, "end": v(50.43, 224.92) * mm});
            skLineSegment(sketch, "E23.2.6.10", {"start": v(69.57, 224.92) * mm, "end": v(60, 208.35) * mm});
            skLineSegment(sketch, "E23.2.6.11", {"start": v(50.43, 224.92) * mm, "end": v(69.57, 224.92) * mm});
            skLineSegment(sketch, "E23.3.0.0", {"start": v(70.43, -17.07) * mm, "end": v(89.57, -17.07) * mm});
            skLineSegment(sketch, "E23.3.0.1", {"start": v(80, -0.5) * mm, "end": v(70.43, -17.07) * mm});
            skLineSegment(sketch, "E23.3.0.2", {"start": v(89.57, -17.07) * mm, "end": v(80, -0.5) * mm});
            skLineSegment(sketch, "E23.3.0.3", {"start": v(60.43, -0.25) * mm, "end": v(79.57, -0.25) * mm});
            skLineSegment(sketch, "E23.3.0.4", {"start": v(79.57, -0.25) * mm, "end": v(70, -16.82) * mm});
            skLineSegment(sketch, "E23.3.0.5", {"start": v(70, -16.82) * mm, "end": v(60.43, -0.25) * mm});
            skLineSegment(sketch, "E23.3.0.6", {"start": v(70, 16.82) * mm, "end": v(60.43, 0.25) * mm});
            skLineSegment(sketch, "E23.3.0.7", {"start": v(60.43, 0.25) * mm, "end": v(79.57, 0.25) * mm});
            skLineSegment(sketch, "E23.3.0.8", {"start": v(79.57, 0.25) * mm, "end": v(70, 16.82) * mm});
            skLineSegment(sketch, "E23.3.0.9", {"start": v(80, 0.5) * mm, "end": v(70.43, 17.07) * mm});
            skLineSegment(sketch, "E23.3.0.10", {"start": v(89.57, 17.07) * mm, "end": v(80, 0.5) * mm});
            skLineSegment(sketch, "E23.3.0.11", {"start": v(70.43, 17.07) * mm, "end": v(89.57, 17.07) * mm});
            skLineSegment(sketch, "E23.3.1.0", {"start": v(70.43, 17.57) * mm, "end": v(89.57, 17.57) * mm});
            skLineSegment(sketch, "E23.3.1.1", {"start": v(80, 34.14) * mm, "end": v(70.43, 17.57) * mm});
            skLineSegment(sketch, "E23.3.1.2", {"start": v(89.57, 17.57) * mm, "end": v(80, 34.14) * mm});
            skLineSegment(sketch, "E23.3.1.3", {"start": v(60.43, 34.4) * mm, "end": v(79.57, 34.4) * mm});
            skLineSegment(sketch, "E23.3.1.4", {"start": v(79.57, 34.4) * mm, "end": v(70, 17.82) * mm});
            skLineSegment(sketch, "E23.3.1.5", {"start": v(70, 17.82) * mm, "end": v(60.43, 34.4) * mm});
            skLineSegment(sketch, "E23.3.1.6", {"start": v(70, 51.46) * mm, "end": v(60.43, 34.9) * mm});
            skLineSegment(sketch, "E23.3.1.7", {"start": v(60.43, 34.9) * mm, "end": v(79.57, 34.9) * mm});
            skLineSegment(sketch, "E23.3.1.8", {"start": v(79.57, 34.9) * mm, "end": v(70, 51.46) * mm});
            skLineSegment(sketch, "E23.3.1.9", {"start": v(80, 35.14) * mm, "end": v(70.43, 51.71) * mm});
            skLineSegment(sketch, "E23.3.1.10", {"start": v(89.57, 51.71) * mm, "end": v(80, 35.14) * mm});
            skLineSegment(sketch, "E23.3.1.11", {"start": v(70.43, 51.71) * mm, "end": v(89.57, 51.71) * mm});
            skLineSegment(sketch, "E23.3.2.0", {"start": v(70.43, 52.21) * mm, "end": v(89.57, 52.21) * mm});
            skLineSegment(sketch, "E23.3.2.1", {"start": v(80, 68.78) * mm, "end": v(70.43, 52.21) * mm});
            skLineSegment(sketch, "E23.3.2.2", {"start": v(89.57, 52.21) * mm, "end": v(80, 68.78) * mm});
            skLineSegment(sketch, "E23.3.2.3", {"start": v(60.43, 69.03) * mm, "end": v(79.57, 69.03) * mm});
            skLineSegment(sketch, "E23.3.2.4", {"start": v(79.57, 69.03) * mm, "end": v(70, 52.46) * mm});
            skLineSegment(sketch, "E23.3.2.5", {"start": v(70, 52.46) * mm, "end": v(60.43, 69.03) * mm});
            skLineSegment(sketch, "E23.3.2.6", {"start": v(70, 86.1) * mm, "end": v(60.43, 69.53) * mm});
            skLineSegment(sketch, "E23.3.2.7", {"start": v(60.43, 69.53) * mm, "end": v(79.57, 69.53) * mm});
            skLineSegment(sketch, "E23.3.2.8", {"start": v(79.57, 69.53) * mm, "end": v(70, 86.1) * mm});
            skLineSegment(sketch, "E23.3.2.9", {"start": v(80, 69.78) * mm, "end": v(70.43, 86.35) * mm});
            skLineSegment(sketch, "E23.3.2.10", {"start": v(89.57, 86.35) * mm, "end": v(80, 69.78) * mm});
            skLineSegment(sketch, "E23.3.2.11", {"start": v(70.43, 86.35) * mm, "end": v(89.57, 86.35) * mm});
            skLineSegment(sketch, "E23.3.3.0", {"start": v(70.43, 86.85) * mm, "end": v(89.57, 86.85) * mm});
            skLineSegment(sketch, "E23.3.3.1", {"start": v(80, 103.42) * mm, "end": v(70.43, 86.85) * mm});
            skLineSegment(sketch, "E23.3.3.2", {"start": v(89.57, 86.85) * mm, "end": v(80, 103.42) * mm});
            skLineSegment(sketch, "E23.3.3.3", {"start": v(60.43, 103.67) * mm, "end": v(79.57, 103.67) * mm});
            skLineSegment(sketch, "E23.3.3.4", {"start": v(79.57, 103.67) * mm, "end": v(70, 87.1) * mm});
            skLineSegment(sketch, "E23.3.3.5", {"start": v(70, 87.1) * mm, "end": v(60.43, 103.67) * mm});
            skLineSegment(sketch, "E23.3.3.6", {"start": v(70, 120.74) * mm, "end": v(60.43, 104.17) * mm});
            skLineSegment(sketch, "E23.3.3.7", {"start": v(60.43, 104.17) * mm, "end": v(79.57, 104.17) * mm});
            skLineSegment(sketch, "E23.3.3.8", {"start": v(79.57, 104.17) * mm, "end": v(70, 120.74) * mm});
            skLineSegment(sketch, "E23.3.3.9", {"start": v(80, 104.42) * mm, "end": v(70.43, 121) * mm});
            skLineSegment(sketch, "E23.3.3.10", {"start": v(89.57, 121) * mm, "end": v(80, 104.42) * mm});
            skLineSegment(sketch, "E23.3.3.11", {"start": v(70.43, 121) * mm, "end": v(89.57, 121) * mm});
            skLineSegment(sketch, "E23.3.4.0", {"start": v(70.43, 121.5) * mm, "end": v(89.57, 121.5) * mm});
            skLineSegment(sketch, "E23.3.4.1", {"start": v(80, 138.06) * mm, "end": v(70.43, 121.5) * mm});
            skLineSegment(sketch, "E23.3.4.2", {"start": v(89.57, 121.5) * mm, "end": v(80, 138.06) * mm});
            skLineSegment(sketch, "E23.3.4.3", {"start": v(60.43, 138.31) * mm, "end": v(79.57, 138.31) * mm});
            skLineSegment(sketch, "E23.3.4.4", {"start": v(79.57, 138.31) * mm, "end": v(70, 121.74) * mm});
            skLineSegment(sketch, "E23.3.4.5", {"start": v(70, 121.74) * mm, "end": v(60.43, 138.31) * mm});
            skLineSegment(sketch, "E23.3.4.6", {"start": v(70, 155.38) * mm, "end": v(60.43, 138.81) * mm});
            skLineSegment(sketch, "E23.3.4.7", {"start": v(60.43, 138.81) * mm, "end": v(79.57, 138.81) * mm});
            skLineSegment(sketch, "E23.3.4.8", {"start": v(79.57, 138.81) * mm, "end": v(70, 155.38) * mm});
            skLineSegment(sketch, "E23.3.4.9", {"start": v(80, 139.06) * mm, "end": v(70.43, 155.63) * mm});
            skLineSegment(sketch, "E23.3.4.10", {"start": v(89.57, 155.63) * mm, "end": v(80, 139.06) * mm});
            skLineSegment(sketch, "E23.3.4.11", {"start": v(70.43, 155.63) * mm, "end": v(89.57, 155.63) * mm});
            skLineSegment(sketch, "E23.3.5.0", {"start": v(70.43, 156.13) * mm, "end": v(89.57, 156.13) * mm});
            skLineSegment(sketch, "E23.3.5.1", {"start": v(80, 172.7) * mm, "end": v(70.43, 156.13) * mm});
            skLineSegment(sketch, "E23.3.5.2", {"start": v(89.57, 156.13) * mm, "end": v(80, 172.7) * mm});
            skLineSegment(sketch, "E23.3.5.3", {"start": v(60.43, 172.96) * mm, "end": v(79.57, 172.96) * mm});
            skLineSegment(sketch, "E23.3.5.4", {"start": v(79.57, 172.96) * mm, "end": v(70, 156.38) * mm});
            skLineSegment(sketch, "E23.3.5.5", {"start": v(70, 156.38) * mm, "end": v(60.43, 172.96) * mm});
            skLineSegment(sketch, "E23.3.5.6", {"start": v(70, 190.03) * mm, "end": v(60.43, 173.46) * mm});
            skLineSegment(sketch, "E23.3.5.7", {"start": v(60.43, 173.46) * mm, "end": v(79.57, 173.46) * mm});
            skLineSegment(sketch, "E23.3.5.8", {"start": v(79.57, 173.46) * mm, "end": v(70, 190.03) * mm});
            skLineSegment(sketch, "E23.3.5.9", {"start": v(80, 173.7) * mm, "end": v(70.43, 190.28) * mm});
            skLineSegment(sketch, "E23.3.5.10", {"start": v(89.57, 190.28) * mm, "end": v(80, 173.7) * mm});
            skLineSegment(sketch, "E23.3.5.11", {"start": v(70.43, 190.28) * mm, "end": v(89.57, 190.28) * mm});
            skLineSegment(sketch, "E23.3.6.0", {"start": v(70.43, 190.78) * mm, "end": v(89.57, 190.78) * mm});
            skLineSegment(sketch, "E23.3.6.1", {"start": v(80, 207.35) * mm, "end": v(70.43, 190.78) * mm});
            skLineSegment(sketch, "E23.3.6.2", {"start": v(89.57, 190.78) * mm, "end": v(80, 207.35) * mm});
            skLineSegment(sketch, "E23.3.6.3", {"start": v(60.43, 207.6) * mm, "end": v(79.57, 207.6) * mm});
            skLineSegment(sketch, "E23.3.6.4", {"start": v(79.57, 207.6) * mm, "end": v(70, 191.03) * mm});
            skLineSegment(sketch, "E23.3.6.5", {"start": v(70, 191.03) * mm, "end": v(60.43, 207.6) * mm});
            skLineSegment(sketch, "E23.3.6.6", {"start": v(70, 224.67) * mm, "end": v(60.43, 208.1) * mm});
            skLineSegment(sketch, "E23.3.6.7", {"start": v(60.43, 208.1) * mm, "end": v(79.57, 208.1) * mm});
            skLineSegment(sketch, "E23.3.6.8", {"start": v(79.57, 208.1) * mm, "end": v(70, 224.67) * mm});
            skLineSegment(sketch, "E23.3.6.9", {"start": v(80, 208.35) * mm, "end": v(70.43, 224.92) * mm});
            skLineSegment(sketch, "E23.3.6.10", {"start": v(89.57, 224.92) * mm, "end": v(80, 208.35) * mm});
            skLineSegment(sketch, "E23.3.6.11", {"start": v(70.43, 224.92) * mm, "end": v(89.57, 224.92) * mm});
            skLineSegment(sketch, "E23.4.0.0", {"start": v(90.43, -17.07) * mm, "end": v(109.57, -17.07) * mm});
            skLineSegment(sketch, "E23.4.0.1", {"start": v(100, -0.5) * mm, "end": v(90.43, -17.07) * mm});
            skLineSegment(sketch, "E23.4.0.2", {"start": v(109.57, -17.07) * mm, "end": v(100, -0.5) * mm});
            skLineSegment(sketch, "E23.4.0.3", {"start": v(80.43, -0.25) * mm, "end": v(99.57, -0.25) * mm});
            skLineSegment(sketch, "E23.4.0.4", {"start": v(99.57, -0.25) * mm, "end": v(90, -16.82) * mm});
            skLineSegment(sketch, "E23.4.0.5", {"start": v(90, -16.82) * mm, "end": v(80.43, -0.25) * mm});
            skLineSegment(sketch, "E23.4.0.6", {"start": v(90, 16.82) * mm, "end": v(80.43, 0.25) * mm});
            skLineSegment(sketch, "E23.4.0.7", {"start": v(80.43, 0.25) * mm, "end": v(99.57, 0.25) * mm});
            skLineSegment(sketch, "E23.4.0.8", {"start": v(99.57, 0.25) * mm, "end": v(90, 16.82) * mm});
            skLineSegment(sketch, "E23.4.0.9", {"start": v(100, 0.5) * mm, "end": v(90.43, 17.07) * mm});
            skLineSegment(sketch, "E23.4.0.10", {"start": v(109.57, 17.07) * mm, "end": v(100, 0.5) * mm});
            skLineSegment(sketch, "E23.4.0.11", {"start": v(90.43, 17.07) * mm, "end": v(109.57, 17.07) * mm});
            skLineSegment(sketch, "E23.4.1.0", {"start": v(90.43, 17.57) * mm, "end": v(109.57, 17.57) * mm});
            skLineSegment(sketch, "E23.4.1.1", {"start": v(100, 34.14) * mm, "end": v(90.43, 17.57) * mm});
            skLineSegment(sketch, "E23.4.1.2", {"start": v(109.57, 17.57) * mm, "end": v(100, 34.14) * mm});
            skLineSegment(sketch, "E23.4.1.3", {"start": v(80.43, 34.4) * mm, "end": v(99.57, 34.4) * mm});
            skLineSegment(sketch, "E23.4.1.4", {"start": v(99.57, 34.4) * mm, "end": v(90, 17.82) * mm});
            skLineSegment(sketch, "E23.4.1.5", {"start": v(90, 17.82) * mm, "end": v(80.43, 34.4) * mm});
            skLineSegment(sketch, "E23.4.1.6", {"start": v(90, 51.46) * mm, "end": v(80.43, 34.9) * mm});
            skLineSegment(sketch, "E23.4.1.7", {"start": v(80.43, 34.9) * mm, "end": v(99.57, 34.9) * mm});
            skLineSegment(sketch, "E23.4.1.8", {"start": v(99.57, 34.9) * mm, "end": v(90, 51.46) * mm});
            skLineSegment(sketch, "E23.4.1.9", {"start": v(100, 35.14) * mm, "end": v(90.43, 51.71) * mm});
            skLineSegment(sketch, "E23.4.1.10", {"start": v(109.57, 51.71) * mm, "end": v(100, 35.14) * mm});
            skLineSegment(sketch, "E23.4.1.11", {"start": v(90.43, 51.71) * mm, "end": v(109.57, 51.71) * mm});
            skLineSegment(sketch, "E23.4.2.0", {"start": v(90.43, 52.21) * mm, "end": v(109.57, 52.21) * mm});
            skLineSegment(sketch, "E23.4.2.1", {"start": v(100, 68.78) * mm, "end": v(90.43, 52.21) * mm});
            skLineSegment(sketch, "E23.4.2.2", {"start": v(109.57, 52.21) * mm, "end": v(100, 68.78) * mm});
            skLineSegment(sketch, "E23.4.2.3", {"start": v(80.43, 69.03) * mm, "end": v(99.57, 69.03) * mm});
            skLineSegment(sketch, "E23.4.2.4", {"start": v(99.57, 69.03) * mm, "end": v(90, 52.46) * mm});
            skLineSegment(sketch, "E23.4.2.5", {"start": v(90, 52.46) * mm, "end": v(80.43, 69.03) * mm});
            skLineSegment(sketch, "E23.4.2.6", {"start": v(90, 86.1) * mm, "end": v(80.43, 69.53) * mm});
            skLineSegment(sketch, "E23.4.2.7", {"start": v(80.43, 69.53) * mm, "end": v(99.57, 69.53) * mm});
            skLineSegment(sketch, "E23.4.2.8", {"start": v(99.57, 69.53) * mm, "end": v(90, 86.1) * mm});
            skLineSegment(sketch, "E23.4.2.9", {"start": v(100, 69.78) * mm, "end": v(90.43, 86.35) * mm});
            skLineSegment(sketch, "E23.4.2.10", {"start": v(109.57, 86.35) * mm, "end": v(100, 69.78) * mm});
            skLineSegment(sketch, "E23.4.2.11", {"start": v(90.43, 86.35) * mm, "end": v(109.57, 86.35) * mm});
            skLineSegment(sketch, "E23.4.3.0", {"start": v(90.43, 86.85) * mm, "end": v(109.57, 86.85) * mm});
            skLineSegment(sketch, "E23.4.3.1", {"start": v(100, 103.42) * mm, "end": v(90.43, 86.85) * mm});
            skLineSegment(sketch, "E23.4.3.2", {"start": v(109.57, 86.85) * mm, "end": v(100, 103.42) * mm});
            skLineSegment(sketch, "E23.4.3.3", {"start": v(80.43, 103.67) * mm, "end": v(99.57, 103.67) * mm});
            skLineSegment(sketch, "E23.4.3.4", {"start": v(99.57, 103.67) * mm, "end": v(90, 87.1) * mm});
            skLineSegment(sketch, "E23.4.3.5", {"start": v(90, 87.1) * mm, "end": v(80.43, 103.67) * mm});
            skLineSegment(sketch, "E23.4.3.6", {"start": v(90, 120.74) * mm, "end": v(80.43, 104.17) * mm});
            skLineSegment(sketch, "E23.4.3.7", {"start": v(80.43, 104.17) * mm, "end": v(99.57, 104.17) * mm});
            skLineSegment(sketch, "E23.4.3.8", {"start": v(99.57, 104.17) * mm, "end": v(90, 120.74) * mm});
            skLineSegment(sketch, "E23.4.3.9", {"start": v(100, 104.42) * mm, "end": v(90.43, 121) * mm});
            skLineSegment(sketch, "E23.4.3.10", {"start": v(109.57, 121) * mm, "end": v(100, 104.42) * mm});
            skLineSegment(sketch, "E23.4.3.11", {"start": v(90.43, 121) * mm, "end": v(109.57, 121) * mm});
            skLineSegment(sketch, "E23.4.4.0", {"start": v(90.43, 121.5) * mm, "end": v(109.57, 121.5) * mm});
            skLineSegment(sketch, "E23.4.4.1", {"start": v(100, 138.06) * mm, "end": v(90.43, 121.5) * mm});
            skLineSegment(sketch, "E23.4.4.2", {"start": v(109.57, 121.5) * mm, "end": v(100, 138.06) * mm});
            skLineSegment(sketch, "E23.4.4.3", {"start": v(80.43, 138.31) * mm, "end": v(99.57, 138.31) * mm});
            skLineSegment(sketch, "E23.4.4.4", {"start": v(99.57, 138.31) * mm, "end": v(90, 121.74) * mm});
            skLineSegment(sketch, "E23.4.4.5", {"start": v(90, 121.74) * mm, "end": v(80.43, 138.31) * mm});
            skLineSegment(sketch, "E23.4.4.6", {"start": v(90, 155.38) * mm, "end": v(80.43, 138.81) * mm});
            skLineSegment(sketch, "E23.4.4.7", {"start": v(80.43, 138.81) * mm, "end": v(99.57, 138.81) * mm});
            skLineSegment(sketch, "E23.4.4.8", {"start": v(99.57, 138.81) * mm, "end": v(90, 155.38) * mm});
            skLineSegment(sketch, "E23.4.4.9", {"start": v(100, 139.06) * mm, "end": v(90.43, 155.63) * mm});
            skLineSegment(sketch, "E23.4.4.10", {"start": v(109.57, 155.63) * mm, "end": v(100, 139.06) * mm});
            skLineSegment(sketch, "E23.4.4.11", {"start": v(90.43, 155.63) * mm, "end": v(109.57, 155.63) * mm});
            skLineSegment(sketch, "E23.4.5.0", {"start": v(90.43, 156.13) * mm, "end": v(109.57, 156.13) * mm});
            skLineSegment(sketch, "E23.4.5.1", {"start": v(100, 172.7) * mm, "end": v(90.43, 156.13) * mm});
            skLineSegment(sketch, "E23.4.5.2", {"start": v(109.57, 156.13) * mm, "end": v(100, 172.7) * mm});
            skLineSegment(sketch, "E23.4.5.3", {"start": v(80.43, 172.96) * mm, "end": v(99.57, 172.96) * mm});
            skLineSegment(sketch, "E23.4.5.4", {"start": v(99.57, 172.96) * mm, "end": v(90, 156.38) * mm});
            skLineSegment(sketch, "E23.4.5.5", {"start": v(90, 156.38) * mm, "end": v(80.43, 172.96) * mm});
            skLineSegment(sketch, "E23.4.5.6", {"start": v(90, 190.03) * mm, "end": v(80.43, 173.46) * mm});
            skLineSegment(sketch, "E23.4.5.7", {"start": v(80.43, 173.46) * mm, "end": v(99.57, 173.46) * mm});
            skLineSegment(sketch, "E23.4.5.8", {"start": v(99.57, 173.46) * mm, "end": v(90, 190.03) * mm});
            skLineSegment(sketch, "E23.4.5.9", {"start": v(100, 173.7) * mm, "end": v(90.43, 190.28) * mm});
            skLineSegment(sketch, "E23.4.5.10", {"start": v(109.57, 190.28) * mm, "end": v(100, 173.7) * mm});
            skLineSegment(sketch, "E23.4.5.11", {"start": v(90.43, 190.28) * mm, "end": v(109.57, 190.28) * mm});
            skLineSegment(sketch, "E23.4.6.0", {"start": v(90.43, 190.78) * mm, "end": v(109.57, 190.78) * mm});
            skLineSegment(sketch, "E23.4.6.1", {"start": v(100, 207.35) * mm, "end": v(90.43, 190.78) * mm});
            skLineSegment(sketch, "E23.4.6.2", {"start": v(109.57, 190.78) * mm, "end": v(100, 207.35) * mm});
            skLineSegment(sketch, "E23.4.6.3", {"start": v(80.43, 207.6) * mm, "end": v(99.57, 207.6) * mm});
            skLineSegment(sketch, "E23.4.6.4", {"start": v(99.57, 207.6) * mm, "end": v(90, 191.03) * mm});
            skLineSegment(sketch, "E23.4.6.5", {"start": v(90, 191.03) * mm, "end": v(80.43, 207.6) * mm});
            skLineSegment(sketch, "E23.4.6.6", {"start": v(90, 224.67) * mm, "end": v(80.43, 208.1) * mm});
            skLineSegment(sketch, "E23.4.6.7", {"start": v(80.43, 208.1) * mm, "end": v(99.57, 208.1) * mm});
            skLineSegment(sketch, "E23.4.6.8", {"start": v(99.57, 208.1) * mm, "end": v(90, 224.67) * mm});
            skLineSegment(sketch, "E23.4.6.9", {"start": v(100, 208.35) * mm, "end": v(90.43, 224.92) * mm});
            skLineSegment(sketch, "E23.4.6.10", {"start": v(109.57, 224.92) * mm, "end": v(100, 208.35) * mm});
            skLineSegment(sketch, "E23.4.6.11", {"start": v(90.43, 224.92) * mm, "end": v(109.57, 224.92) * mm});
            skLineSegment(sketch, "E23.5.0.0", {"start": v(110.43, -17.07) * mm, "end": v(129.57, -17.07) * mm});
            skLineSegment(sketch, "E23.5.0.1", {"start": v(120, -0.5) * mm, "end": v(110.43, -17.07) * mm});
            skLineSegment(sketch, "E23.5.0.2", {"start": v(129.57, -17.07) * mm, "end": v(120, -0.5) * mm});
            skLineSegment(sketch, "E23.5.0.3", {"start": v(100.43, -0.25) * mm, "end": v(119.57, -0.25) * mm});
            skLineSegment(sketch, "E23.5.0.4", {"start": v(119.57, -0.25) * mm, "end": v(110, -16.82) * mm});
            skLineSegment(sketch, "E23.5.0.5", {"start": v(110, -16.82) * mm, "end": v(100.43, -0.25) * mm});
            skLineSegment(sketch, "E23.5.0.6", {"start": v(110, 16.82) * mm, "end": v(100.43, 0.25) * mm});
            skLineSegment(sketch, "E23.5.0.7", {"start": v(100.43, 0.25) * mm, "end": v(119.57, 0.25) * mm});
            skLineSegment(sketch, "E23.5.0.8", {"start": v(119.57, 0.25) * mm, "end": v(110, 16.82) * mm});
            skLineSegment(sketch, "E23.5.0.9", {"start": v(120, 0.5) * mm, "end": v(110.43, 17.07) * mm});
            skLineSegment(sketch, "E23.5.0.10", {"start": v(129.57, 17.07) * mm, "end": v(120, 0.5) * mm});
            skLineSegment(sketch, "E23.5.0.11", {"start": v(110.43, 17.07) * mm, "end": v(129.57, 17.07) * mm});
            skLineSegment(sketch, "E23.5.1.0", {"start": v(110.43, 17.57) * mm, "end": v(129.57, 17.57) * mm});
            skLineSegment(sketch, "E23.5.1.1", {"start": v(120, 34.14) * mm, "end": v(110.43, 17.57) * mm});
            skLineSegment(sketch, "E23.5.1.2", {"start": v(129.57, 17.57) * mm, "end": v(120, 34.14) * mm});
            skLineSegment(sketch, "E23.5.1.3", {"start": v(100.43, 34.4) * mm, "end": v(119.57, 34.4) * mm});
            skLineSegment(sketch, "E23.5.1.4", {"start": v(119.57, 34.4) * mm, "end": v(110, 17.82) * mm});
            skLineSegment(sketch, "E23.5.1.5", {"start": v(110, 17.82) * mm, "end": v(100.43, 34.4) * mm});
            skLineSegment(sketch, "E23.5.1.6", {"start": v(110, 51.46) * mm, "end": v(100.43, 34.9) * mm});
            skLineSegment(sketch, "E23.5.1.7", {"start": v(100.43, 34.9) * mm, "end": v(119.57, 34.9) * mm});
            skLineSegment(sketch, "E23.5.1.8", {"start": v(119.57, 34.9) * mm, "end": v(110, 51.46) * mm});
            skLineSegment(sketch, "E23.5.1.9", {"start": v(120, 35.14) * mm, "end": v(110.43, 51.71) * mm});
            skLineSegment(sketch, "E23.5.1.10", {"start": v(129.57, 51.71) * mm, "end": v(120, 35.14) * mm});
            skLineSegment(sketch, "E23.5.1.11", {"start": v(110.43, 51.71) * mm, "end": v(129.57, 51.71) * mm});
            skLineSegment(sketch, "E23.5.2.0", {"start": v(110.43, 52.21) * mm, "end": v(129.57, 52.21) * mm});
            skLineSegment(sketch, "E23.5.2.1", {"start": v(120, 68.78) * mm, "end": v(110.43, 52.21) * mm});
            skLineSegment(sketch, "E23.5.2.2", {"start": v(129.57, 52.21) * mm, "end": v(120, 68.78) * mm});
            skLineSegment(sketch, "E23.5.2.3", {"start": v(100.43, 69.03) * mm, "end": v(119.57, 69.03) * mm});
            skLineSegment(sketch, "E23.5.2.4", {"start": v(119.57, 69.03) * mm, "end": v(110, 52.46) * mm});
            skLineSegment(sketch, "E23.5.2.5", {"start": v(110, 52.46) * mm, "end": v(100.43, 69.03) * mm});
            skLineSegment(sketch, "E23.5.2.6", {"start": v(110, 86.1) * mm, "end": v(100.43, 69.53) * mm});
            skLineSegment(sketch, "E23.5.2.7", {"start": v(100.43, 69.53) * mm, "end": v(119.57, 69.53) * mm});
            skLineSegment(sketch, "E23.5.2.8", {"start": v(119.57, 69.53) * mm, "end": v(110, 86.1) * mm});
            skLineSegment(sketch, "E23.5.2.9", {"start": v(120, 69.78) * mm, "end": v(110.43, 86.35) * mm});
            skLineSegment(sketch, "E23.5.2.10", {"start": v(129.57, 86.35) * mm, "end": v(120, 69.78) * mm});
            skLineSegment(sketch, "E23.5.2.11", {"start": v(110.43, 86.35) * mm, "end": v(129.57, 86.35) * mm});
            skLineSegment(sketch, "E23.5.3.0", {"start": v(110.43, 86.85) * mm, "end": v(129.57, 86.85) * mm});
            skLineSegment(sketch, "E23.5.3.1", {"start": v(120, 103.42) * mm, "end": v(110.43, 86.85) * mm});
            skLineSegment(sketch, "E23.5.3.2", {"start": v(129.57, 86.85) * mm, "end": v(120, 103.42) * mm});
            skLineSegment(sketch, "E23.5.3.3", {"start": v(100.43, 103.67) * mm, "end": v(119.57, 103.67) * mm});
            skLineSegment(sketch, "E23.5.3.4", {"start": v(119.57, 103.67) * mm, "end": v(110, 87.1) * mm});
            skLineSegment(sketch, "E23.5.3.5", {"start": v(110, 87.1) * mm, "end": v(100.43, 103.67) * mm});
            skLineSegment(sketch, "E23.5.3.6", {"start": v(110, 120.74) * mm, "end": v(100.43, 104.17) * mm});
            skLineSegment(sketch, "E23.5.3.7", {"start": v(100.43, 104.17) * mm, "end": v(119.57, 104.17) * mm});
            skLineSegment(sketch, "E23.5.3.8", {"start": v(119.57, 104.17) * mm, "end": v(110, 120.74) * mm});
            skLineSegment(sketch, "E23.5.3.9", {"start": v(120, 104.42) * mm, "end": v(110.43, 121) * mm});
            skLineSegment(sketch, "E23.5.3.10", {"start": v(129.57, 121) * mm, "end": v(120, 104.42) * mm});
            skLineSegment(sketch, "E23.5.3.11", {"start": v(110.43, 121) * mm, "end": v(129.57, 121) * mm});
            skLineSegment(sketch, "E23.5.4.0", {"start": v(110.43, 121.5) * mm, "end": v(129.57, 121.5) * mm});
            skLineSegment(sketch, "E23.5.4.1", {"start": v(120, 138.06) * mm, "end": v(110.43, 121.5) * mm});
            skLineSegment(sketch, "E23.5.4.2", {"start": v(129.57, 121.5) * mm, "end": v(120, 138.06) * mm});
            skLineSegment(sketch, "E23.5.4.3", {"start": v(100.43, 138.31) * mm, "end": v(119.57, 138.31) * mm});
            skLineSegment(sketch, "E23.5.4.4", {"start": v(119.57, 138.31) * mm, "end": v(110, 121.74) * mm});
            skLineSegment(sketch, "E23.5.4.5", {"start": v(110, 121.74) * mm, "end": v(100.43, 138.31) * mm});
            skLineSegment(sketch, "E23.5.4.6", {"start": v(110, 155.38) * mm, "end": v(100.43, 138.81) * mm});
            skLineSegment(sketch, "E23.5.4.7", {"start": v(100.43, 138.81) * mm, "end": v(119.57, 138.81) * mm});
            skLineSegment(sketch, "E23.5.4.8", {"start": v(119.57, 138.81) * mm, "end": v(110, 155.38) * mm});
            skLineSegment(sketch, "E23.5.4.9", {"start": v(120, 139.06) * mm, "end": v(110.43, 155.63) * mm});
            skLineSegment(sketch, "E23.5.4.10", {"start": v(129.57, 155.63) * mm, "end": v(120, 139.06) * mm});
            skLineSegment(sketch, "E23.5.4.11", {"start": v(110.43, 155.63) * mm, "end": v(129.57, 155.63) * mm});
            skLineSegment(sketch, "E23.5.5.0", {"start": v(110.43, 156.13) * mm, "end": v(129.57, 156.13) * mm});
            skLineSegment(sketch, "E23.5.5.1", {"start": v(120, 172.7) * mm, "end": v(110.43, 156.13) * mm});
            skLineSegment(sketch, "E23.5.5.2", {"start": v(129.57, 156.13) * mm, "end": v(120, 172.7) * mm});
            skLineSegment(sketch, "E23.5.5.3", {"start": v(100.43, 172.96) * mm, "end": v(119.57, 172.96) * mm});
            skLineSegment(sketch, "E23.5.5.4", {"start": v(119.57, 172.96) * mm, "end": v(110, 156.38) * mm});
            skLineSegment(sketch, "E23.5.5.5", {"start": v(110, 156.38) * mm, "end": v(100.43, 172.96) * mm});
            skLineSegment(sketch, "E23.5.5.6", {"start": v(110, 190.03) * mm, "end": v(100.43, 173.46) * mm});
            skLineSegment(sketch, "E23.5.5.7", {"start": v(100.43, 173.46) * mm, "end": v(119.57, 173.46) * mm});
            skLineSegment(sketch, "E23.5.5.8", {"start": v(119.57, 173.46) * mm, "end": v(110, 190.03) * mm});
            skLineSegment(sketch, "E23.5.5.9", {"start": v(120, 173.7) * mm, "end": v(110.43, 190.28) * mm});
            skLineSegment(sketch, "E23.5.5.10", {"start": v(129.57, 190.28) * mm, "end": v(120, 173.7) * mm});
            skLineSegment(sketch, "E23.5.5.11", {"start": v(110.43, 190.28) * mm, "end": v(129.57, 190.28) * mm});
            skLineSegment(sketch, "E23.5.6.0", {"start": v(110.43, 190.78) * mm, "end": v(129.57, 190.78) * mm});
            skLineSegment(sketch, "E23.5.6.1", {"start": v(120, 207.35) * mm, "end": v(110.43, 190.78) * mm});
            skLineSegment(sketch, "E23.5.6.2", {"start": v(129.57, 190.78) * mm, "end": v(120, 207.35) * mm});
            skLineSegment(sketch, "E23.5.6.3", {"start": v(100.43, 207.6) * mm, "end": v(119.57, 207.6) * mm});
            skLineSegment(sketch, "E23.5.6.4", {"start": v(119.57, 207.6) * mm, "end": v(110, 191.03) * mm});
            skLineSegment(sketch, "E23.5.6.5", {"start": v(110, 191.03) * mm, "end": v(100.43, 207.6) * mm});
            skLineSegment(sketch, "E23.5.6.6", {"start": v(110, 224.67) * mm, "end": v(100.43, 208.1) * mm});
            skLineSegment(sketch, "E23.5.6.7", {"start": v(100.43, 208.1) * mm, "end": v(119.57, 208.1) * mm});
            skLineSegment(sketch, "E23.5.6.8", {"start": v(119.57, 208.1) * mm, "end": v(110, 224.67) * mm});
            skLineSegment(sketch, "E23.5.6.9", {"start": v(120, 208.35) * mm, "end": v(110.43, 224.92) * mm});
            skLineSegment(sketch, "E23.5.6.10", {"start": v(129.57, 224.92) * mm, "end": v(120, 208.35) * mm});
            skLineSegment(sketch, "E23.5.6.11", {"start": v(110.43, 224.92) * mm, "end": v(129.57, 224.92) * mm});
            skLineSegment(sketch, "E23.6.0.0", {"start": v(130.43, -17.07) * mm, "end": v(149.57, -17.07) * mm});
            skLineSegment(sketch, "E23.6.0.1", {"start": v(140, -0.5) * mm, "end": v(130.43, -17.07) * mm});
            skLineSegment(sketch, "E23.6.0.2", {"start": v(149.57, -17.07) * mm, "end": v(140, -0.5) * mm});
            skLineSegment(sketch, "E23.6.0.3", {"start": v(120.43, -0.25) * mm, "end": v(139.57, -0.25) * mm});
            skLineSegment(sketch, "E23.6.0.4", {"start": v(139.57, -0.25) * mm, "end": v(130, -16.82) * mm});
            skLineSegment(sketch, "E23.6.0.5", {"start": v(130, -16.82) * mm, "end": v(120.43, -0.25) * mm});
            skLineSegment(sketch, "E23.6.0.6", {"start": v(130, 16.82) * mm, "end": v(120.43, 0.25) * mm});
            skLineSegment(sketch, "E23.6.0.7", {"start": v(120.43, 0.25) * mm, "end": v(139.57, 0.25) * mm});
            skLineSegment(sketch, "E23.6.0.8", {"start": v(139.57, 0.25) * mm, "end": v(130, 16.82) * mm});
            skLineSegment(sketch, "E23.6.0.9", {"start": v(140, 0.5) * mm, "end": v(130.43, 17.07) * mm});
            skLineSegment(sketch, "E23.6.0.10", {"start": v(149.57, 17.07) * mm, "end": v(140, 0.5) * mm});
            skLineSegment(sketch, "E23.6.0.11", {"start": v(130.43, 17.07) * mm, "end": v(149.57, 17.07) * mm});
            skLineSegment(sketch, "E23.6.1.0", {"start": v(130.43, 17.57) * mm, "end": v(149.57, 17.57) * mm});
            skLineSegment(sketch, "E23.6.1.1", {"start": v(140, 34.14) * mm, "end": v(130.43, 17.57) * mm});
            skLineSegment(sketch, "E23.6.1.2", {"start": v(149.57, 17.57) * mm, "end": v(140, 34.14) * mm});
            skLineSegment(sketch, "E23.6.1.3", {"start": v(120.43, 34.4) * mm, "end": v(139.57, 34.4) * mm});
            skLineSegment(sketch, "E23.6.1.4", {"start": v(139.57, 34.4) * mm, "end": v(130, 17.82) * mm});
            skLineSegment(sketch, "E23.6.1.5", {"start": v(130, 17.82) * mm, "end": v(120.43, 34.4) * mm});
            skLineSegment(sketch, "E23.6.1.6", {"start": v(130, 51.46) * mm, "end": v(120.43, 34.9) * mm});
            skLineSegment(sketch, "E23.6.1.7", {"start": v(120.43, 34.9) * mm, "end": v(139.57, 34.9) * mm});
            skLineSegment(sketch, "E23.6.1.8", {"start": v(139.57, 34.9) * mm, "end": v(130, 51.46) * mm});
            skLineSegment(sketch, "E23.6.1.9", {"start": v(140, 35.14) * mm, "end": v(130.43, 51.71) * mm});
            skLineSegment(sketch, "E23.6.1.10", {"start": v(149.57, 51.71) * mm, "end": v(140, 35.14) * mm});
            skLineSegment(sketch, "E23.6.1.11", {"start": v(130.43, 51.71) * mm, "end": v(149.57, 51.71) * mm});
            skLineSegment(sketch, "E23.6.2.0", {"start": v(130.43, 52.21) * mm, "end": v(149.57, 52.21) * mm});
            skLineSegment(sketch, "E23.6.2.1", {"start": v(140, 68.78) * mm, "end": v(130.43, 52.21) * mm});
            skLineSegment(sketch, "E23.6.2.2", {"start": v(149.57, 52.21) * mm, "end": v(140, 68.78) * mm});
            skLineSegment(sketch, "E23.6.2.3", {"start": v(120.43, 69.03) * mm, "end": v(139.57, 69.03) * mm});
            skLineSegment(sketch, "E23.6.2.4", {"start": v(139.57, 69.03) * mm, "end": v(130, 52.46) * mm});
            skLineSegment(sketch, "E23.6.2.5", {"start": v(130, 52.46) * mm, "end": v(120.43, 69.03) * mm});
            skLineSegment(sketch, "E23.6.2.6", {"start": v(130, 86.1) * mm, "end": v(120.43, 69.53) * mm});
            skLineSegment(sketch, "E23.6.2.7", {"start": v(120.43, 69.53) * mm, "end": v(139.57, 69.53) * mm});
            skLineSegment(sketch, "E23.6.2.8", {"start": v(139.57, 69.53) * mm, "end": v(130, 86.1) * mm});
            skLineSegment(sketch, "E23.6.2.9", {"start": v(140, 69.78) * mm, "end": v(130.43, 86.35) * mm});
            skLineSegment(sketch, "E23.6.2.10", {"start": v(149.57, 86.35) * mm, "end": v(140, 69.78) * mm});
            skLineSegment(sketch, "E23.6.2.11", {"start": v(130.43, 86.35) * mm, "end": v(149.57, 86.35) * mm});
            skLineSegment(sketch, "E23.6.3.0", {"start": v(130.43, 86.85) * mm, "end": v(149.57, 86.85) * mm});
            skLineSegment(sketch, "E23.6.3.1", {"start": v(140, 103.42) * mm, "end": v(130.43, 86.85) * mm});
            skLineSegment(sketch, "E23.6.3.2", {"start": v(149.57, 86.85) * mm, "end": v(140, 103.42) * mm});
            skLineSegment(sketch, "E23.6.3.3", {"start": v(120.43, 103.67) * mm, "end": v(139.57, 103.67) * mm});
            skLineSegment(sketch, "E23.6.3.4", {"start": v(139.57, 103.67) * mm, "end": v(130, 87.1) * mm});
            skLineSegment(sketch, "E23.6.3.5", {"start": v(130, 87.1) * mm, "end": v(120.43, 103.67) * mm});
            skLineSegment(sketch, "E23.6.3.6", {"start": v(130, 120.74) * mm, "end": v(120.43, 104.17) * mm});
            skLineSegment(sketch, "E23.6.3.7", {"start": v(120.43, 104.17) * mm, "end": v(139.57, 104.17) * mm});
            skLineSegment(sketch, "E23.6.3.8", {"start": v(139.57, 104.17) * mm, "end": v(130, 120.74) * mm});
            skLineSegment(sketch, "E23.6.3.9", {"start": v(140, 104.42) * mm, "end": v(130.43, 121) * mm});
            skLineSegment(sketch, "E23.6.3.10", {"start": v(149.57, 121) * mm, "end": v(140, 104.42) * mm});
            skLineSegment(sketch, "E23.6.3.11", {"start": v(130.43, 121) * mm, "end": v(149.57, 121) * mm});
            skLineSegment(sketch, "E23.6.4.0", {"start": v(130.43, 121.5) * mm, "end": v(149.57, 121.5) * mm});
            skLineSegment(sketch, "E23.6.4.1", {"start": v(140, 138.06) * mm, "end": v(130.43, 121.5) * mm});
            skLineSegment(sketch, "E23.6.4.2", {"start": v(149.57, 121.5) * mm, "end": v(140, 138.06) * mm});
            skLineSegment(sketch, "E23.6.4.3", {"start": v(120.43, 138.31) * mm, "end": v(139.57, 138.31) * mm});
            skLineSegment(sketch, "E23.6.4.4", {"start": v(139.57, 138.31) * mm, "end": v(130, 121.74) * mm});
            skLineSegment(sketch, "E23.6.4.5", {"start": v(130, 121.74) * mm, "end": v(120.43, 138.31) * mm});
            skLineSegment(sketch, "E23.6.4.6", {"start": v(130, 155.38) * mm, "end": v(120.43, 138.81) * mm});
            skLineSegment(sketch, "E23.6.4.7", {"start": v(120.43, 138.81) * mm, "end": v(139.57, 138.81) * mm});
            skLineSegment(sketch, "E23.6.4.8", {"start": v(139.57, 138.81) * mm, "end": v(130, 155.38) * mm});
            skLineSegment(sketch, "E23.6.4.9", {"start": v(140, 139.06) * mm, "end": v(130.43, 155.63) * mm});
            skLineSegment(sketch, "E23.6.4.10", {"start": v(149.57, 155.63) * mm, "end": v(140, 139.06) * mm});
            skLineSegment(sketch, "E23.6.4.11", {"start": v(130.43, 155.63) * mm, "end": v(149.57, 155.63) * mm});
            skLineSegment(sketch, "E23.6.5.0", {"start": v(130.43, 156.13) * mm, "end": v(149.57, 156.13) * mm});
            skLineSegment(sketch, "E23.6.5.1", {"start": v(140, 172.7) * mm, "end": v(130.43, 156.13) * mm});
            skLineSegment(sketch, "E23.6.5.2", {"start": v(149.57, 156.13) * mm, "end": v(140, 172.7) * mm});
            skLineSegment(sketch, "E23.6.5.3", {"start": v(120.43, 172.96) * mm, "end": v(139.57, 172.96) * mm});
            skLineSegment(sketch, "E23.6.5.4", {"start": v(139.57, 172.96) * mm, "end": v(130, 156.38) * mm});
            skLineSegment(sketch, "E23.6.5.5", {"start": v(130, 156.38) * mm, "end": v(120.43, 172.96) * mm});
            skLineSegment(sketch, "E23.6.5.6", {"start": v(130, 190.03) * mm, "end": v(120.43, 173.46) * mm});
            skLineSegment(sketch, "E23.6.5.7", {"start": v(120.43, 173.46) * mm, "end": v(139.57, 173.46) * mm});
            skLineSegment(sketch, "E23.6.5.8", {"start": v(139.57, 173.46) * mm, "end": v(130, 190.03) * mm});
            skLineSegment(sketch, "E23.6.5.9", {"start": v(140, 173.7) * mm, "end": v(130.43, 190.28) * mm});
            skLineSegment(sketch, "E23.6.5.10", {"start": v(149.57, 190.28) * mm, "end": v(140, 173.7) * mm});
            skLineSegment(sketch, "E23.6.5.11", {"start": v(130.43, 190.28) * mm, "end": v(149.57, 190.28) * mm});
            skLineSegment(sketch, "E23.6.6.0", {"start": v(130.43, 190.78) * mm, "end": v(149.57, 190.78) * mm});
            skLineSegment(sketch, "E23.6.6.1", {"start": v(140, 207.35) * mm, "end": v(130.43, 190.78) * mm});
            skLineSegment(sketch, "E23.6.6.2", {"start": v(149.57, 190.78) * mm, "end": v(140, 207.35) * mm});
            skLineSegment(sketch, "E23.6.6.3", {"start": v(120.43, 207.6) * mm, "end": v(139.57, 207.6) * mm});
            skLineSegment(sketch, "E23.6.6.4", {"start": v(139.57, 207.6) * mm, "end": v(130, 191.03) * mm});
            skLineSegment(sketch, "E23.6.6.5", {"start": v(130, 191.03) * mm, "end": v(120.43, 207.6) * mm});
            skLineSegment(sketch, "E23.6.6.6", {"start": v(130, 224.67) * mm, "end": v(120.43, 208.1) * mm});
            skLineSegment(sketch, "E23.6.6.7", {"start": v(120.43, 208.1) * mm, "end": v(139.57, 208.1) * mm});
            skLineSegment(sketch, "E23.6.6.8", {"start": v(139.57, 208.1) * mm, "end": v(130, 224.67) * mm});
            skLineSegment(sketch, "E23.6.6.9", {"start": v(140, 208.35) * mm, "end": v(130.43, 224.92) * mm});
            skLineSegment(sketch, "E23.6.6.10", {"start": v(149.57, 224.92) * mm, "end": v(140, 208.35) * mm});
            skLineSegment(sketch, "E23.6.6.11", {"start": v(130.43, 224.92) * mm, "end": v(149.57, 224.92) * mm});
            skLineSegment(sketch, "E23.7.0.0", {"start": v(150.43, -17.07) * mm, "end": v(169.57, -17.07) * mm});
            skLineSegment(sketch, "E23.7.0.1", {"start": v(160, -0.5) * mm, "end": v(150.43, -17.07) * mm});
            skLineSegment(sketch, "E23.7.0.2", {"start": v(169.57, -17.07) * mm, "end": v(160, -0.5) * mm});
            skLineSegment(sketch, "E23.7.0.3", {"start": v(140.43, -0.25) * mm, "end": v(159.57, -0.25) * mm});
            skLineSegment(sketch, "E23.7.0.4", {"start": v(159.57, -0.25) * mm, "end": v(150, -16.82) * mm});
            skLineSegment(sketch, "E23.7.0.5", {"start": v(150, -16.82) * mm, "end": v(140.43, -0.25) * mm});
            skLineSegment(sketch, "E23.7.0.6", {"start": v(150, 16.82) * mm, "end": v(140.43, 0.25) * mm});
            skLineSegment(sketch, "E23.7.0.7", {"start": v(140.43, 0.25) * mm, "end": v(159.57, 0.25) * mm});
            skLineSegment(sketch, "E23.7.0.8", {"start": v(159.57, 0.25) * mm, "end": v(150, 16.82) * mm});
            skLineSegment(sketch, "E23.7.0.9", {"start": v(160, 0.5) * mm, "end": v(150.43, 17.07) * mm});
            skLineSegment(sketch, "E23.7.0.10", {"start": v(169.57, 17.07) * mm, "end": v(160, 0.5) * mm});
            skLineSegment(sketch, "E23.7.0.11", {"start": v(150.43, 17.07) * mm, "end": v(169.57, 17.07) * mm});
            skLineSegment(sketch, "E23.7.1.0", {"start": v(150.43, 17.57) * mm, "end": v(169.57, 17.57) * mm});
            skLineSegment(sketch, "E23.7.1.1", {"start": v(160, 34.14) * mm, "end": v(150.43, 17.57) * mm});
            skLineSegment(sketch, "E23.7.1.2", {"start": v(169.57, 17.57) * mm, "end": v(160, 34.14) * mm});
            skLineSegment(sketch, "E23.7.1.3", {"start": v(140.43, 34.4) * mm, "end": v(159.57, 34.4) * mm});
            skLineSegment(sketch, "E23.7.1.4", {"start": v(159.57, 34.4) * mm, "end": v(150, 17.82) * mm});
            skLineSegment(sketch, "E23.7.1.5", {"start": v(150, 17.82) * mm, "end": v(140.43, 34.4) * mm});
            skLineSegment(sketch, "E23.7.1.6", {"start": v(150, 51.46) * mm, "end": v(140.43, 34.9) * mm});
            skLineSegment(sketch, "E23.7.1.7", {"start": v(140.43, 34.9) * mm, "end": v(159.57, 34.9) * mm});
            skLineSegment(sketch, "E23.7.1.8", {"start": v(159.57, 34.9) * mm, "end": v(150, 51.46) * mm});
            skLineSegment(sketch, "E23.7.1.9", {"start": v(160, 35.14) * mm, "end": v(150.43, 51.71) * mm});
            skLineSegment(sketch, "E23.7.1.10", {"start": v(169.57, 51.71) * mm, "end": v(160, 35.14) * mm});
            skLineSegment(sketch, "E23.7.1.11", {"start": v(150.43, 51.71) * mm, "end": v(169.57, 51.71) * mm});
            skLineSegment(sketch, "E23.7.2.0", {"start": v(150.43, 52.21) * mm, "end": v(169.57, 52.21) * mm});
            skLineSegment(sketch, "E23.7.2.1", {"start": v(160, 68.78) * mm, "end": v(150.43, 52.21) * mm});
            skLineSegment(sketch, "E23.7.2.2", {"start": v(169.57, 52.21) * mm, "end": v(160, 68.78) * mm});
            skLineSegment(sketch, "E23.7.2.3", {"start": v(140.43, 69.03) * mm, "end": v(159.57, 69.03) * mm});
            skLineSegment(sketch, "E23.7.2.4", {"start": v(159.57, 69.03) * mm, "end": v(150, 52.46) * mm});
            skLineSegment(sketch, "E23.7.2.5", {"start": v(150, 52.46) * mm, "end": v(140.43, 69.03) * mm});
            skLineSegment(sketch, "E23.7.2.6", {"start": v(150, 86.1) * mm, "end": v(140.43, 69.53) * mm});
            skLineSegment(sketch, "E23.7.2.7", {"start": v(140.43, 69.53) * mm, "end": v(159.57, 69.53) * mm});
            skLineSegment(sketch, "E23.7.2.8", {"start": v(159.57, 69.53) * mm, "end": v(150, 86.1) * mm});
            skLineSegment(sketch, "E23.7.2.9", {"start": v(160, 69.78) * mm, "end": v(150.43, 86.35) * mm});
            skLineSegment(sketch, "E23.7.2.10", {"start": v(169.57, 86.35) * mm, "end": v(160, 69.78) * mm});
            skLineSegment(sketch, "E23.7.2.11", {"start": v(150.43, 86.35) * mm, "end": v(169.57, 86.35) * mm});
            skLineSegment(sketch, "E23.7.3.0", {"start": v(150.43, 86.85) * mm, "end": v(169.57, 86.85) * mm});
            skLineSegment(sketch, "E23.7.3.1", {"start": v(160, 103.42) * mm, "end": v(150.43, 86.85) * mm});
            skLineSegment(sketch, "E23.7.3.2", {"start": v(169.57, 86.85) * mm, "end": v(160, 103.42) * mm});
            skLineSegment(sketch, "E23.7.3.3", {"start": v(140.43, 103.67) * mm, "end": v(159.57, 103.67) * mm});
            skLineSegment(sketch, "E23.7.3.4", {"start": v(159.57, 103.67) * mm, "end": v(150, 87.1) * mm});
            skLineSegment(sketch, "E23.7.3.5", {"start": v(150, 87.1) * mm, "end": v(140.43, 103.67) * mm});
            skLineSegment(sketch, "E23.7.3.6", {"start": v(150, 120.74) * mm, "end": v(140.43, 104.17) * mm});
            skLineSegment(sketch, "E23.7.3.7", {"start": v(140.43, 104.17) * mm, "end": v(159.57, 104.17) * mm});
            skLineSegment(sketch, "E23.7.3.8", {"start": v(159.57, 104.17) * mm, "end": v(150, 120.74) * mm});
            skLineSegment(sketch, "E23.7.3.9", {"start": v(160, 104.42) * mm, "end": v(150.43, 121) * mm});
            skLineSegment(sketch, "E23.7.3.10", {"start": v(169.57, 121) * mm, "end": v(160, 104.42) * mm});
            skLineSegment(sketch, "E23.7.3.11", {"start": v(150.43, 121) * mm, "end": v(169.57, 121) * mm});
            skLineSegment(sketch, "E23.7.4.0", {"start": v(150.43, 121.5) * mm, "end": v(169.57, 121.5) * mm});
            skLineSegment(sketch, "E23.7.4.1", {"start": v(160, 138.06) * mm, "end": v(150.43, 121.5) * mm});
            skLineSegment(sketch, "E23.7.4.2", {"start": v(169.57, 121.5) * mm, "end": v(160, 138.06) * mm});
            skLineSegment(sketch, "E23.7.4.3", {"start": v(140.43, 138.31) * mm, "end": v(159.57, 138.31) * mm});
            skLineSegment(sketch, "E23.7.4.4", {"start": v(159.57, 138.31) * mm, "end": v(150, 121.74) * mm});
            skLineSegment(sketch, "E23.7.4.5", {"start": v(150, 121.74) * mm, "end": v(140.43, 138.31) * mm});
            skLineSegment(sketch, "E23.7.4.6", {"start": v(150, 155.38) * mm, "end": v(140.43, 138.81) * mm});
            skLineSegment(sketch, "E23.7.4.7", {"start": v(140.43, 138.81) * mm, "end": v(159.57, 138.81) * mm});
            skLineSegment(sketch, "E23.7.4.8", {"start": v(159.57, 138.81) * mm, "end": v(150, 155.38) * mm});
            skLineSegment(sketch, "E23.7.4.9", {"start": v(160, 139.06) * mm, "end": v(150.43, 155.63) * mm});
            skLineSegment(sketch, "E23.7.4.10", {"start": v(169.57, 155.63) * mm, "end": v(160, 139.06) * mm});
            skLineSegment(sketch, "E23.7.4.11", {"start": v(150.43, 155.63) * mm, "end": v(169.57, 155.63) * mm});
            skLineSegment(sketch, "E23.7.5.0", {"start": v(150.43, 156.13) * mm, "end": v(169.57, 156.13) * mm});
            skLineSegment(sketch, "E23.7.5.1", {"start": v(160, 172.7) * mm, "end": v(150.43, 156.13) * mm});
            skLineSegment(sketch, "E23.7.5.2", {"start": v(169.57, 156.13) * mm, "end": v(160, 172.7) * mm});
            skLineSegment(sketch, "E23.7.5.3", {"start": v(140.43, 172.96) * mm, "end": v(159.57, 172.96) * mm});
            skLineSegment(sketch, "E23.7.5.4", {"start": v(159.57, 172.96) * mm, "end": v(150, 156.38) * mm});
            skLineSegment(sketch, "E23.7.5.5", {"start": v(150, 156.38) * mm, "end": v(140.43, 172.96) * mm});
            skLineSegment(sketch, "E23.7.5.6", {"start": v(150, 190.03) * mm, "end": v(140.43, 173.46) * mm});
            skLineSegment(sketch, "E23.7.5.7", {"start": v(140.43, 173.46) * mm, "end": v(159.57, 173.46) * mm});
            skLineSegment(sketch, "E23.7.5.8", {"start": v(159.57, 173.46) * mm, "end": v(150, 190.03) * mm});
            skLineSegment(sketch, "E23.7.5.9", {"start": v(160, 173.7) * mm, "end": v(150.43, 190.28) * mm});
            skLineSegment(sketch, "E23.7.5.10", {"start": v(169.57, 190.28) * mm, "end": v(160, 173.7) * mm});
            skLineSegment(sketch, "E23.7.5.11", {"start": v(150.43, 190.28) * mm, "end": v(169.57, 190.28) * mm});
            skLineSegment(sketch, "E23.7.6.0", {"start": v(150.43, 190.78) * mm, "end": v(169.57, 190.78) * mm});
            skLineSegment(sketch, "E23.7.6.1", {"start": v(160, 207.35) * mm, "end": v(150.43, 190.78) * mm});
            skLineSegment(sketch, "E23.7.6.2", {"start": v(169.57, 190.78) * mm, "end": v(160, 207.35) * mm});
            skLineSegment(sketch, "E23.7.6.3", {"start": v(140.43, 207.6) * mm, "end": v(159.57, 207.6) * mm});
            skLineSegment(sketch, "E23.7.6.4", {"start": v(159.57, 207.6) * mm, "end": v(150, 191.03) * mm});
            skLineSegment(sketch, "E23.7.6.5", {"start": v(150, 191.03) * mm, "end": v(140.43, 207.6) * mm});
            skLineSegment(sketch, "E23.7.6.6", {"start": v(150, 224.67) * mm, "end": v(140.43, 208.1) * mm});
            skLineSegment(sketch, "E23.7.6.7", {"start": v(140.43, 208.1) * mm, "end": v(159.57, 208.1) * mm});
            skLineSegment(sketch, "E23.7.6.8", {"start": v(159.57, 208.1) * mm, "end": v(150, 224.67) * mm});
            skLineSegment(sketch, "E23.7.6.9", {"start": v(160, 208.35) * mm, "end": v(150.43, 224.92) * mm});
            skLineSegment(sketch, "E23.7.6.10", {"start": v(169.57, 224.92) * mm, "end": v(160, 208.35) * mm});
            skLineSegment(sketch, "E23.7.6.11", {"start": v(150.43, 224.92) * mm, "end": v(169.57, 224.92) * mm});
            skLineSegment(sketch, "E23.8.0.0", {"start": v(170.43, -17.07) * mm, "end": v(189.57, -17.07) * mm});
            skLineSegment(sketch, "E23.8.0.1", {"start": v(180, -0.5) * mm, "end": v(170.43, -17.07) * mm});
            skLineSegment(sketch, "E23.8.0.2", {"start": v(189.57, -17.07) * mm, "end": v(180, -0.5) * mm});
            skLineSegment(sketch, "E23.8.0.3", {"start": v(160.43, -0.25) * mm, "end": v(179.57, -0.25) * mm});
            skLineSegment(sketch, "E23.8.0.4", {"start": v(179.57, -0.25) * mm, "end": v(170, -16.82) * mm});
            skLineSegment(sketch, "E23.8.0.5", {"start": v(170, -16.82) * mm, "end": v(160.43, -0.25) * mm});
            skLineSegment(sketch, "E23.8.0.6", {"start": v(170, 16.82) * mm, "end": v(160.43, 0.25) * mm});
            skLineSegment(sketch, "E23.8.0.7", {"start": v(160.43, 0.25) * mm, "end": v(179.57, 0.25) * mm});
            skLineSegment(sketch, "E23.8.0.8", {"start": v(179.57, 0.25) * mm, "end": v(170, 16.82) * mm});
            skLineSegment(sketch, "E23.8.0.9", {"start": v(180, 0.5) * mm, "end": v(170.43, 17.07) * mm});
            skLineSegment(sketch, "E23.8.0.10", {"start": v(189.57, 17.07) * mm, "end": v(180, 0.5) * mm});
            skLineSegment(sketch, "E23.8.0.11", {"start": v(170.43, 17.07) * mm, "end": v(189.57, 17.07) * mm});
            skLineSegment(sketch, "E23.8.1.0", {"start": v(170.43, 17.57) * mm, "end": v(189.57, 17.57) * mm});
            skLineSegment(sketch, "E23.8.1.1", {"start": v(180, 34.14) * mm, "end": v(170.43, 17.57) * mm});
            skLineSegment(sketch, "E23.8.1.2", {"start": v(189.57, 17.57) * mm, "end": v(180, 34.14) * mm});
            skLineSegment(sketch, "E23.8.1.3", {"start": v(160.43, 34.4) * mm, "end": v(179.57, 34.4) * mm});
            skLineSegment(sketch, "E23.8.1.4", {"start": v(179.57, 34.4) * mm, "end": v(170, 17.82) * mm});
            skLineSegment(sketch, "E23.8.1.5", {"start": v(170, 17.82) * mm, "end": v(160.43, 34.4) * mm});
            skLineSegment(sketch, "E23.8.1.6", {"start": v(170, 51.46) * mm, "end": v(160.43, 34.9) * mm});
            skLineSegment(sketch, "E23.8.1.7", {"start": v(160.43, 34.9) * mm, "end": v(179.57, 34.9) * mm});
            skLineSegment(sketch, "E23.8.1.8", {"start": v(179.57, 34.9) * mm, "end": v(170, 51.46) * mm});
            skLineSegment(sketch, "E23.8.1.9", {"start": v(180, 35.14) * mm, "end": v(170.43, 51.71) * mm});
            skLineSegment(sketch, "E23.8.1.10", {"start": v(189.57, 51.71) * mm, "end": v(180, 35.14) * mm});
            skLineSegment(sketch, "E23.8.1.11", {"start": v(170.43, 51.71) * mm, "end": v(189.57, 51.71) * mm});
            skLineSegment(sketch, "E23.8.2.0", {"start": v(170.43, 52.21) * mm, "end": v(189.57, 52.21) * mm});
            skLineSegment(sketch, "E23.8.2.1", {"start": v(180, 68.78) * mm, "end": v(170.43, 52.21) * mm});
            skLineSegment(sketch, "E23.8.2.2", {"start": v(189.57, 52.21) * mm, "end": v(180, 68.78) * mm});
            skLineSegment(sketch, "E23.8.2.3", {"start": v(160.43, 69.03) * mm, "end": v(179.57, 69.03) * mm});
            skLineSegment(sketch, "E23.8.2.4", {"start": v(179.57, 69.03) * mm, "end": v(170, 52.46) * mm});
            skLineSegment(sketch, "E23.8.2.5", {"start": v(170, 52.46) * mm, "end": v(160.43, 69.03) * mm});
            skLineSegment(sketch, "E23.8.2.6", {"start": v(170, 86.1) * mm, "end": v(160.43, 69.53) * mm});
            skLineSegment(sketch, "E23.8.2.7", {"start": v(160.43, 69.53) * mm, "end": v(179.57, 69.53) * mm});
            skLineSegment(sketch, "E23.8.2.8", {"start": v(179.57, 69.53) * mm, "end": v(170, 86.1) * mm});
            skLineSegment(sketch, "E23.8.2.9", {"start": v(180, 69.78) * mm, "end": v(170.43, 86.35) * mm});
            skLineSegment(sketch, "E23.8.2.10", {"start": v(189.57, 86.35) * mm, "end": v(180, 69.78) * mm});
            skLineSegment(sketch, "E23.8.2.11", {"start": v(170.43, 86.35) * mm, "end": v(189.57, 86.35) * mm});
            skLineSegment(sketch, "E23.8.3.0", {"start": v(170.43, 86.85) * mm, "end": v(189.57, 86.85) * mm});
            skLineSegment(sketch, "E23.8.3.1", {"start": v(180, 103.42) * mm, "end": v(170.43, 86.85) * mm});
            skLineSegment(sketch, "E23.8.3.2", {"start": v(189.57, 86.85) * mm, "end": v(180, 103.42) * mm});
            skLineSegment(sketch, "E23.8.3.3", {"start": v(160.43, 103.67) * mm, "end": v(179.57, 103.67) * mm});
            skLineSegment(sketch, "E23.8.3.4", {"start": v(179.57, 103.67) * mm, "end": v(170, 87.1) * mm});
            skLineSegment(sketch, "E23.8.3.5", {"start": v(170, 87.1) * mm, "end": v(160.43, 103.67) * mm});
            skLineSegment(sketch, "E23.8.3.6", {"start": v(170, 120.74) * mm, "end": v(160.43, 104.17) * mm});
            skLineSegment(sketch, "E23.8.3.7", {"start": v(160.43, 104.17) * mm, "end": v(179.57, 104.17) * mm});
            skLineSegment(sketch, "E23.8.3.8", {"start": v(179.57, 104.17) * mm, "end": v(170, 120.74) * mm});
            skLineSegment(sketch, "E23.8.3.9", {"start": v(180, 104.42) * mm, "end": v(170.43, 121) * mm});
            skLineSegment(sketch, "E23.8.3.10", {"start": v(189.57, 121) * mm, "end": v(180, 104.42) * mm});
            skLineSegment(sketch, "E23.8.3.11", {"start": v(170.43, 121) * mm, "end": v(189.57, 121) * mm});
            skLineSegment(sketch, "E23.8.4.0", {"start": v(170.43, 121.5) * mm, "end": v(189.57, 121.5) * mm});
            skLineSegment(sketch, "E23.8.4.1", {"start": v(180, 138.06) * mm, "end": v(170.43, 121.5) * mm});
            skLineSegment(sketch, "E23.8.4.2", {"start": v(189.57, 121.5) * mm, "end": v(180, 138.06) * mm});
            skLineSegment(sketch, "E23.8.4.3", {"start": v(160.43, 138.31) * mm, "end": v(179.57, 138.31) * mm});
            skLineSegment(sketch, "E23.8.4.4", {"start": v(179.57, 138.31) * mm, "end": v(170, 121.74) * mm});
            skLineSegment(sketch, "E23.8.4.5", {"start": v(170, 121.74) * mm, "end": v(160.43, 138.31) * mm});
            skLineSegment(sketch, "E23.8.4.6", {"start": v(170, 155.38) * mm, "end": v(160.43, 138.81) * mm});
            skLineSegment(sketch, "E23.8.4.7", {"start": v(160.43, 138.81) * mm, "end": v(179.57, 138.81) * mm});
            skLineSegment(sketch, "E23.8.4.8", {"start": v(179.57, 138.81) * mm, "end": v(170, 155.38) * mm});
            skLineSegment(sketch, "E23.8.4.9", {"start": v(180, 139.06) * mm, "end": v(170.43, 155.63) * mm});
            skLineSegment(sketch, "E23.8.4.10", {"start": v(189.57, 155.63) * mm, "end": v(180, 139.06) * mm});
            skLineSegment(sketch, "E23.8.4.11", {"start": v(170.43, 155.63) * mm, "end": v(189.57, 155.63) * mm});
            skLineSegment(sketch, "E23.8.5.0", {"start": v(170.43, 156.13) * mm, "end": v(189.57, 156.13) * mm});
            skLineSegment(sketch, "E23.8.5.1", {"start": v(180, 172.7) * mm, "end": v(170.43, 156.13) * mm});
            skLineSegment(sketch, "E23.8.5.2", {"start": v(189.57, 156.13) * mm, "end": v(180, 172.7) * mm});
            skLineSegment(sketch, "E23.8.5.3", {"start": v(160.43, 172.96) * mm, "end": v(179.57, 172.96) * mm});
            skLineSegment(sketch, "E23.8.5.4", {"start": v(179.57, 172.96) * mm, "end": v(170, 156.38) * mm});
            skLineSegment(sketch, "E23.8.5.5", {"start": v(170, 156.38) * mm, "end": v(160.43, 172.96) * mm});
            skLineSegment(sketch, "E23.8.5.6", {"start": v(170, 190.03) * mm, "end": v(160.43, 173.46) * mm});
            skLineSegment(sketch, "E23.8.5.7", {"start": v(160.43, 173.46) * mm, "end": v(179.57, 173.46) * mm});
            skLineSegment(sketch, "E23.8.5.8", {"start": v(179.57, 173.46) * mm, "end": v(170, 190.03) * mm});
            skLineSegment(sketch, "E23.8.5.9", {"start": v(180, 173.7) * mm, "end": v(170.43, 190.28) * mm});
            skLineSegment(sketch, "E23.8.5.10", {"start": v(189.57, 190.28) * mm, "end": v(180, 173.7) * mm});
            skLineSegment(sketch, "E23.8.5.11", {"start": v(170.43, 190.28) * mm, "end": v(189.57, 190.28) * mm});
            skLineSegment(sketch, "E23.8.6.0", {"start": v(170.43, 190.78) * mm, "end": v(189.57, 190.78) * mm});
            skLineSegment(sketch, "E23.8.6.1", {"start": v(180, 207.35) * mm, "end": v(170.43, 190.78) * mm});
            skLineSegment(sketch, "E23.8.6.2", {"start": v(189.57, 190.78) * mm, "end": v(180, 207.35) * mm});
            skLineSegment(sketch, "E23.8.6.3", {"start": v(160.43, 207.6) * mm, "end": v(179.57, 207.6) * mm});
            skLineSegment(sketch, "E23.8.6.4", {"start": v(179.57, 207.6) * mm, "end": v(170, 191.03) * mm});
            skLineSegment(sketch, "E23.8.6.5", {"start": v(170, 191.03) * mm, "end": v(160.43, 207.6) * mm});
            skLineSegment(sketch, "E23.8.6.6", {"start": v(170, 224.67) * mm, "end": v(160.43, 208.1) * mm});
            skLineSegment(sketch, "E23.8.6.7", {"start": v(160.43, 208.1) * mm, "end": v(179.57, 208.1) * mm});
            skLineSegment(sketch, "E23.8.6.8", {"start": v(179.57, 208.1) * mm, "end": v(170, 224.67) * mm});
            skLineSegment(sketch, "E23.8.6.9", {"start": v(180, 208.35) * mm, "end": v(170.43, 224.92) * mm});
            skLineSegment(sketch, "E23.8.6.10", {"start": v(189.57, 224.92) * mm, "end": v(180, 208.35) * mm});
            skLineSegment(sketch, "E23.8.6.11", {"start": v(170.43, 224.92) * mm, "end": v(189.57, 224.92) * mm});
            skLineSegment(sketch, "E23.9.0.0", {"start": v(190.43, -17.07) * mm, "end": v(209.57, -17.07) * mm});
            skLineSegment(sketch, "E23.9.0.1", {"start": v(200, -0.5) * mm, "end": v(190.43, -17.07) * mm});
            skLineSegment(sketch, "E23.9.0.2", {"start": v(209.57, -17.07) * mm, "end": v(200, -0.5) * mm});
            skLineSegment(sketch, "E23.9.0.3", {"start": v(180.43, -0.25) * mm, "end": v(199.57, -0.25) * mm});
            skLineSegment(sketch, "E23.9.0.4", {"start": v(199.57, -0.25) * mm, "end": v(190, -16.82) * mm});
            skLineSegment(sketch, "E23.9.0.5", {"start": v(190, -16.82) * mm, "end": v(180.43, -0.25) * mm});
            skLineSegment(sketch, "E23.9.0.6", {"start": v(190, 16.82) * mm, "end": v(180.43, 0.25) * mm});
            skLineSegment(sketch, "E23.9.0.7", {"start": v(180.43, 0.25) * mm, "end": v(199.57, 0.25) * mm});
            skLineSegment(sketch, "E23.9.0.8", {"start": v(199.57, 0.25) * mm, "end": v(190, 16.82) * mm});
            skLineSegment(sketch, "E23.9.0.9", {"start": v(200, 0.5) * mm, "end": v(190.43, 17.07) * mm});
            skLineSegment(sketch, "E23.9.0.10", {"start": v(209.57, 17.07) * mm, "end": v(200, 0.5) * mm});
            skLineSegment(sketch, "E23.9.0.11", {"start": v(190.43, 17.07) * mm, "end": v(209.57, 17.07) * mm});
            skLineSegment(sketch, "E23.9.1.0", {"start": v(190.43, 17.57) * mm, "end": v(209.57, 17.57) * mm});
            skLineSegment(sketch, "E23.9.1.1", {"start": v(200, 34.14) * mm, "end": v(190.43, 17.57) * mm});
            skLineSegment(sketch, "E23.9.1.2", {"start": v(209.57, 17.57) * mm, "end": v(200, 34.14) * mm});
            skLineSegment(sketch, "E23.9.1.3", {"start": v(180.43, 34.4) * mm, "end": v(199.57, 34.4) * mm});
            skLineSegment(sketch, "E23.9.1.4", {"start": v(199.57, 34.4) * mm, "end": v(190, 17.82) * mm});
            skLineSegment(sketch, "E23.9.1.5", {"start": v(190, 17.82) * mm, "end": v(180.43, 34.4) * mm});
            skLineSegment(sketch, "E23.9.1.6", {"start": v(190, 51.46) * mm, "end": v(180.43, 34.9) * mm});
            skLineSegment(sketch, "E23.9.1.7", {"start": v(180.43, 34.9) * mm, "end": v(199.57, 34.9) * mm});
            skLineSegment(sketch, "E23.9.1.8", {"start": v(199.57, 34.9) * mm, "end": v(190, 51.46) * mm});
            skLineSegment(sketch, "E23.9.1.9", {"start": v(200, 35.14) * mm, "end": v(190.43, 51.71) * mm});
            skLineSegment(sketch, "E23.9.1.10", {"start": v(209.57, 51.71) * mm, "end": v(200, 35.14) * mm});
            skLineSegment(sketch, "E23.9.1.11", {"start": v(190.43, 51.71) * mm, "end": v(209.57, 51.71) * mm});
            skLineSegment(sketch, "E23.9.2.0", {"start": v(190.43, 52.21) * mm, "end": v(209.57, 52.21) * mm});
            skLineSegment(sketch, "E23.9.2.1", {"start": v(200, 68.78) * mm, "end": v(190.43, 52.21) * mm});
            skLineSegment(sketch, "E23.9.2.2", {"start": v(209.57, 52.21) * mm, "end": v(200, 68.78) * mm});
            skLineSegment(sketch, "E23.9.2.3", {"start": v(180.43, 69.03) * mm, "end": v(199.57, 69.03) * mm});
            skLineSegment(sketch, "E23.9.2.4", {"start": v(199.57, 69.03) * mm, "end": v(190, 52.46) * mm});
            skLineSegment(sketch, "E23.9.2.5", {"start": v(190, 52.46) * mm, "end": v(180.43, 69.03) * mm});
            skLineSegment(sketch, "E23.9.2.6", {"start": v(190, 86.1) * mm, "end": v(180.43, 69.53) * mm});
            skLineSegment(sketch, "E23.9.2.7", {"start": v(180.43, 69.53) * mm, "end": v(199.57, 69.53) * mm});
            skLineSegment(sketch, "E23.9.2.8", {"start": v(199.57, 69.53) * mm, "end": v(190, 86.1) * mm});
            skLineSegment(sketch, "E23.9.2.9", {"start": v(200, 69.78) * mm, "end": v(190.43, 86.35) * mm});
            skLineSegment(sketch, "E23.9.2.10", {"start": v(209.57, 86.35) * mm, "end": v(200, 69.78) * mm});
            skLineSegment(sketch, "E23.9.2.11", {"start": v(190.43, 86.35) * mm, "end": v(209.57, 86.35) * mm});
            skLineSegment(sketch, "E23.9.3.0", {"start": v(190.43, 86.85) * mm, "end": v(209.57, 86.85) * mm});
            skLineSegment(sketch, "E23.9.3.1", {"start": v(200, 103.42) * mm, "end": v(190.43, 86.85) * mm});
            skLineSegment(sketch, "E23.9.3.2", {"start": v(209.57, 86.85) * mm, "end": v(200, 103.42) * mm});
            skLineSegment(sketch, "E23.9.3.3", {"start": v(180.43, 103.67) * mm, "end": v(199.57, 103.67) * mm});
            skLineSegment(sketch, "E23.9.3.4", {"start": v(199.57, 103.67) * mm, "end": v(190, 87.1) * mm});
            skLineSegment(sketch, "E23.9.3.5", {"start": v(190, 87.1) * mm, "end": v(180.43, 103.67) * mm});
            skLineSegment(sketch, "E23.9.3.6", {"start": v(190, 120.74) * mm, "end": v(180.43, 104.17) * mm});
            skLineSegment(sketch, "E23.9.3.7", {"start": v(180.43, 104.17) * mm, "end": v(199.57, 104.17) * mm});
            skLineSegment(sketch, "E23.9.3.8", {"start": v(199.57, 104.17) * mm, "end": v(190, 120.74) * mm});
            skLineSegment(sketch, "E23.9.3.9", {"start": v(200, 104.42) * mm, "end": v(190.43, 121) * mm});
            skLineSegment(sketch, "E23.9.3.10", {"start": v(209.57, 121) * mm, "end": v(200, 104.42) * mm});
            skLineSegment(sketch, "E23.9.3.11", {"start": v(190.43, 121) * mm, "end": v(209.57, 121) * mm});
            skLineSegment(sketch, "E23.9.4.0", {"start": v(190.43, 121.5) * mm, "end": v(209.57, 121.5) * mm});
            skLineSegment(sketch, "E23.9.4.1", {"start": v(200, 138.06) * mm, "end": v(190.43, 121.5) * mm});
            skLineSegment(sketch, "E23.9.4.2", {"start": v(209.57, 121.5) * mm, "end": v(200, 138.06) * mm});
            skLineSegment(sketch, "E23.9.4.3", {"start": v(180.43, 138.31) * mm, "end": v(199.57, 138.31) * mm});
            skLineSegment(sketch, "E23.9.4.4", {"start": v(199.57, 138.31) * mm, "end": v(190, 121.74) * mm});
            skLineSegment(sketch, "E23.9.4.5", {"start": v(190, 121.74) * mm, "end": v(180.43, 138.31) * mm});
            skLineSegment(sketch, "E23.9.4.6", {"start": v(190, 155.38) * mm, "end": v(180.43, 138.81) * mm});
            skLineSegment(sketch, "E23.9.4.7", {"start": v(180.43, 138.81) * mm, "end": v(199.57, 138.81) * mm});
            skLineSegment(sketch, "E23.9.4.8", {"start": v(199.57, 138.81) * mm, "end": v(190, 155.38) * mm});
            skLineSegment(sketch, "E23.9.4.9", {"start": v(200, 139.06) * mm, "end": v(190.43, 155.63) * mm});
            skLineSegment(sketch, "E23.9.4.10", {"start": v(209.57, 155.63) * mm, "end": v(200, 139.06) * mm});
            skLineSegment(sketch, "E23.9.4.11", {"start": v(190.43, 155.63) * mm, "end": v(209.57, 155.63) * mm});
            skLineSegment(sketch, "E23.9.5.0", {"start": v(190.43, 156.13) * mm, "end": v(209.57, 156.13) * mm});
            skLineSegment(sketch, "E23.9.5.1", {"start": v(200, 172.7) * mm, "end": v(190.43, 156.13) * mm});
            skLineSegment(sketch, "E23.9.5.2", {"start": v(209.57, 156.13) * mm, "end": v(200, 172.7) * mm});
            skLineSegment(sketch, "E23.9.5.3", {"start": v(180.43, 172.96) * mm, "end": v(199.57, 172.96) * mm});
            skLineSegment(sketch, "E23.9.5.4", {"start": v(199.57, 172.96) * mm, "end": v(190, 156.38) * mm});
            skLineSegment(sketch, "E23.9.5.5", {"start": v(190, 156.38) * mm, "end": v(180.43, 172.96) * mm});
            skLineSegment(sketch, "E23.9.5.6", {"start": v(190, 190.03) * mm, "end": v(180.43, 173.46) * mm});
            skLineSegment(sketch, "E23.9.5.7", {"start": v(180.43, 173.46) * mm, "end": v(199.57, 173.46) * mm});
            skLineSegment(sketch, "E23.9.5.8", {"start": v(199.57, 173.46) * mm, "end": v(190, 190.03) * mm});
            skLineSegment(sketch, "E23.9.5.9", {"start": v(200, 173.7) * mm, "end": v(190.43, 190.28) * mm});
            skLineSegment(sketch, "E23.9.5.10", {"start": v(209.57, 190.28) * mm, "end": v(200, 173.7) * mm});
            skLineSegment(sketch, "E23.9.5.11", {"start": v(190.43, 190.28) * mm, "end": v(209.57, 190.28) * mm});
            skLineSegment(sketch, "E23.9.6.0", {"start": v(190.43, 190.78) * mm, "end": v(209.57, 190.78) * mm});
            skLineSegment(sketch, "E23.9.6.1", {"start": v(200, 207.35) * mm, "end": v(190.43, 190.78) * mm});
            skLineSegment(sketch, "E23.9.6.2", {"start": v(209.57, 190.78) * mm, "end": v(200, 207.35) * mm});
            skLineSegment(sketch, "E23.9.6.3", {"start": v(180.43, 207.6) * mm, "end": v(199.57, 207.6) * mm});
            skLineSegment(sketch, "E23.9.6.4", {"start": v(199.57, 207.6) * mm, "end": v(190, 191.03) * mm});
            skLineSegment(sketch, "E23.9.6.5", {"start": v(190, 191.03) * mm, "end": v(180.43, 207.6) * mm});
            skLineSegment(sketch, "E23.9.6.6", {"start": v(190, 224.67) * mm, "end": v(180.43, 208.1) * mm});
            skLineSegment(sketch, "E23.9.6.7", {"start": v(180.43, 208.1) * mm, "end": v(199.57, 208.1) * mm});
            skLineSegment(sketch, "E23.9.6.8", {"start": v(199.57, 208.1) * mm, "end": v(190, 224.67) * mm});
            skLineSegment(sketch, "E23.9.6.9", {"start": v(200, 208.35) * mm, "end": v(190.43, 224.92) * mm});
            skLineSegment(sketch, "E23.9.6.10", {"start": v(209.57, 224.92) * mm, "end": v(200, 208.35) * mm});
            skLineSegment(sketch, "E23.9.6.11", {"start": v(190.43, 224.92) * mm, "end": v(209.57, 224.92) * mm});
            skLineSegment(sketch, "E23.10.0.0", {"start": v(210.43, -17.07) * mm, "end": v(229.57, -17.07) * mm});
            skLineSegment(sketch, "E23.10.0.1", {"start": v(220, -0.5) * mm, "end": v(210.43, -17.07) * mm});
            skLineSegment(sketch, "E23.10.0.2", {"start": v(229.57, -17.07) * mm, "end": v(220, -0.5) * mm});
            skLineSegment(sketch, "E23.10.0.3", {"start": v(200.43, -0.25) * mm, "end": v(219.57, -0.25) * mm});
            skLineSegment(sketch, "E23.10.0.4", {"start": v(219.57, -0.25) * mm, "end": v(210, -16.82) * mm});
            skLineSegment(sketch, "E23.10.0.5", {"start": v(210, -16.82) * mm, "end": v(200.43, -0.25) * mm});
            skLineSegment(sketch, "E23.10.0.6", {"start": v(210, 16.82) * mm, "end": v(200.43, 0.25) * mm});
            skLineSegment(sketch, "E23.10.0.7", {"start": v(200.43, 0.25) * mm, "end": v(219.57, 0.25) * mm});
            skLineSegment(sketch, "E23.10.0.8", {"start": v(219.57, 0.25) * mm, "end": v(210, 16.82) * mm});
            skLineSegment(sketch, "E23.10.0.9", {"start": v(220, 0.5) * mm, "end": v(210.43, 17.07) * mm});
            skLineSegment(sketch, "E23.10.0.10", {"start": v(229.57, 17.07) * mm, "end": v(220, 0.5) * mm});
            skLineSegment(sketch, "E23.10.0.11", {"start": v(210.43, 17.07) * mm, "end": v(229.57, 17.07) * mm});
            skLineSegment(sketch, "E23.10.1.0", {"start": v(210.43, 17.57) * mm, "end": v(229.57, 17.57) * mm});
            skLineSegment(sketch, "E23.10.1.1", {"start": v(220, 34.14) * mm, "end": v(210.43, 17.57) * mm});
            skLineSegment(sketch, "E23.10.1.2", {"start": v(229.57, 17.57) * mm, "end": v(220, 34.14) * mm});
            skLineSegment(sketch, "E23.10.1.3", {"start": v(200.43, 34.4) * mm, "end": v(219.57, 34.4) * mm});
            skLineSegment(sketch, "E23.10.1.4", {"start": v(219.57, 34.4) * mm, "end": v(210, 17.82) * mm});
            skLineSegment(sketch, "E23.10.1.5", {"start": v(210, 17.82) * mm, "end": v(200.43, 34.4) * mm});
            skLineSegment(sketch, "E23.10.1.6", {"start": v(210, 51.46) * mm, "end": v(200.43, 34.9) * mm});
            skLineSegment(sketch, "E23.10.1.7", {"start": v(200.43, 34.9) * mm, "end": v(219.57, 34.9) * mm});
            skLineSegment(sketch, "E23.10.1.8", {"start": v(219.57, 34.9) * mm, "end": v(210, 51.46) * mm});
            skLineSegment(sketch, "E23.10.1.9", {"start": v(220, 35.14) * mm, "end": v(210.43, 51.71) * mm});
            skLineSegment(sketch, "E23.10.1.10", {"start": v(229.57, 51.71) * mm, "end": v(220, 35.14) * mm});
            skLineSegment(sketch, "E23.10.1.11", {"start": v(210.43, 51.71) * mm, "end": v(229.57, 51.71) * mm});
            skLineSegment(sketch, "E23.10.2.0", {"start": v(210.43, 52.21) * mm, "end": v(229.57, 52.21) * mm});
            skLineSegment(sketch, "E23.10.2.1", {"start": v(220, 68.78) * mm, "end": v(210.43, 52.21) * mm});
            skLineSegment(sketch, "E23.10.2.2", {"start": v(229.57, 52.21) * mm, "end": v(220, 68.78) * mm});
            skLineSegment(sketch, "E23.10.2.3", {"start": v(200.43, 69.03) * mm, "end": v(219.57, 69.03) * mm});
            skLineSegment(sketch, "E23.10.2.4", {"start": v(219.57, 69.03) * mm, "end": v(210, 52.46) * mm});
            skLineSegment(sketch, "E23.10.2.5", {"start": v(210, 52.46) * mm, "end": v(200.43, 69.03) * mm});
            skLineSegment(sketch, "E23.10.2.6", {"start": v(210, 86.1) * mm, "end": v(200.43, 69.53) * mm});
            skLineSegment(sketch, "E23.10.2.7", {"start": v(200.43, 69.53) * mm, "end": v(219.57, 69.53) * mm});
            skLineSegment(sketch, "E23.10.2.8", {"start": v(219.57, 69.53) * mm, "end": v(210, 86.1) * mm});
            skLineSegment(sketch, "E23.10.2.9", {"start": v(220, 69.78) * mm, "end": v(210.43, 86.35) * mm});
            skLineSegment(sketch, "E23.10.2.10", {"start": v(229.57, 86.35) * mm, "end": v(220, 69.78) * mm});
            skLineSegment(sketch, "E23.10.2.11", {"start": v(210.43, 86.35) * mm, "end": v(229.57, 86.35) * mm});
            skLineSegment(sketch, "E23.10.3.0", {"start": v(210.43, 86.85) * mm, "end": v(229.57, 86.85) * mm});
            skLineSegment(sketch, "E23.10.3.1", {"start": v(220, 103.42) * mm, "end": v(210.43, 86.85) * mm});
            skLineSegment(sketch, "E23.10.3.2", {"start": v(229.57, 86.85) * mm, "end": v(220, 103.42) * mm});
            skLineSegment(sketch, "E23.10.3.3", {"start": v(200.43, 103.67) * mm, "end": v(219.57, 103.67) * mm});
            skLineSegment(sketch, "E23.10.3.4", {"start": v(219.57, 103.67) * mm, "end": v(210, 87.1) * mm});
            skLineSegment(sketch, "E23.10.3.5", {"start": v(210, 87.1) * mm, "end": v(200.43, 103.67) * mm});
            skLineSegment(sketch, "E23.10.3.6", {"start": v(210, 120.74) * mm, "end": v(200.43, 104.17) * mm});
            skLineSegment(sketch, "E23.10.3.7", {"start": v(200.43, 104.17) * mm, "end": v(219.57, 104.17) * mm});
            skLineSegment(sketch, "E23.10.3.8", {"start": v(219.57, 104.17) * mm, "end": v(210, 120.74) * mm});
            skLineSegment(sketch, "E23.10.3.9", {"start": v(220, 104.42) * mm, "end": v(210.43, 121) * mm});
            skLineSegment(sketch, "E23.10.3.10", {"start": v(229.57, 121) * mm, "end": v(220, 104.42) * mm});
            skLineSegment(sketch, "E23.10.3.11", {"start": v(210.43, 121) * mm, "end": v(229.57, 121) * mm});
            skLineSegment(sketch, "E23.10.4.0", {"start": v(210.43, 121.5) * mm, "end": v(229.57, 121.5) * mm});
            skLineSegment(sketch, "E23.10.4.1", {"start": v(220, 138.06) * mm, "end": v(210.43, 121.5) * mm});
            skLineSegment(sketch, "E23.10.4.2", {"start": v(229.57, 121.5) * mm, "end": v(220, 138.06) * mm});
            skLineSegment(sketch, "E23.10.4.3", {"start": v(200.43, 138.31) * mm, "end": v(219.57, 138.31) * mm});
            skLineSegment(sketch, "E23.10.4.4", {"start": v(219.57, 138.31) * mm, "end": v(210, 121.74) * mm});
            skLineSegment(sketch, "E23.10.4.5", {"start": v(210, 121.74) * mm, "end": v(200.43, 138.31) * mm});
            skLineSegment(sketch, "E23.10.4.6", {"start": v(210, 155.38) * mm, "end": v(200.43, 138.81) * mm});
            skLineSegment(sketch, "E23.10.4.7", {"start": v(200.43, 138.81) * mm, "end": v(219.57, 138.81) * mm});
            skLineSegment(sketch, "E23.10.4.8", {"start": v(219.57, 138.81) * mm, "end": v(210, 155.38) * mm});
            skLineSegment(sketch, "E23.10.4.9", {"start": v(220, 139.06) * mm, "end": v(210.43, 155.63) * mm});
            skLineSegment(sketch, "E23.10.4.10", {"start": v(229.57, 155.63) * mm, "end": v(220, 139.06) * mm});
            skLineSegment(sketch, "E23.10.4.11", {"start": v(210.43, 155.63) * mm, "end": v(229.57, 155.63) * mm});
            skLineSegment(sketch, "E23.10.5.0", {"start": v(210.43, 156.13) * mm, "end": v(229.57, 156.13) * mm});
            skLineSegment(sketch, "E23.10.5.1", {"start": v(220, 172.7) * mm, "end": v(210.43, 156.13) * mm});
            skLineSegment(sketch, "E23.10.5.2", {"start": v(229.57, 156.13) * mm, "end": v(220, 172.7) * mm});
            skLineSegment(sketch, "E23.10.5.3", {"start": v(200.43, 172.96) * mm, "end": v(219.57, 172.96) * mm});
            skLineSegment(sketch, "E23.10.5.4", {"start": v(219.57, 172.96) * mm, "end": v(210, 156.38) * mm});
            skLineSegment(sketch, "E23.10.5.5", {"start": v(210, 156.38) * mm, "end": v(200.43, 172.96) * mm});
            skLineSegment(sketch, "E23.10.5.6", {"start": v(210, 190.03) * mm, "end": v(200.43, 173.46) * mm});
            skLineSegment(sketch, "E23.10.5.7", {"start": v(200.43, 173.46) * mm, "end": v(219.57, 173.46) * mm});
            skLineSegment(sketch, "E23.10.5.8", {"start": v(219.57, 173.46) * mm, "end": v(210, 190.03) * mm});
            skLineSegment(sketch, "E23.10.5.9", {"start": v(220, 173.7) * mm, "end": v(210.43, 190.28) * mm});
            skLineSegment(sketch, "E23.10.5.10", {"start": v(229.57, 190.28) * mm, "end": v(220, 173.7) * mm});
            skLineSegment(sketch, "E23.10.5.11", {"start": v(210.43, 190.28) * mm, "end": v(229.57, 190.28) * mm});
            skLineSegment(sketch, "E23.10.6.0", {"start": v(210.43, 190.78) * mm, "end": v(229.57, 190.78) * mm});
            skLineSegment(sketch, "E23.10.6.1", {"start": v(220, 207.35) * mm, "end": v(210.43, 190.78) * mm});
            skLineSegment(sketch, "E23.10.6.2", {"start": v(229.57, 190.78) * mm, "end": v(220, 207.35) * mm});
            skLineSegment(sketch, "E23.10.6.3", {"start": v(200.43, 207.6) * mm, "end": v(219.57, 207.6) * mm});
            skLineSegment(sketch, "E23.10.6.4", {"start": v(219.57, 207.6) * mm, "end": v(210, 191.03) * mm});
            skLineSegment(sketch, "E23.10.6.5", {"start": v(210, 191.03) * mm, "end": v(200.43, 207.6) * mm});
            skLineSegment(sketch, "E23.10.6.6", {"start": v(210, 224.67) * mm, "end": v(200.43, 208.1) * mm});
            skLineSegment(sketch, "E23.10.6.7", {"start": v(200.43, 208.1) * mm, "end": v(219.57, 208.1) * mm});
            skLineSegment(sketch, "E23.10.6.8", {"start": v(219.57, 208.1) * mm, "end": v(210, 224.67) * mm});
            skLineSegment(sketch, "E23.10.6.9", {"start": v(220, 208.35) * mm, "end": v(210.43, 224.92) * mm});
            skLineSegment(sketch, "E23.10.6.10", {"start": v(229.57, 224.92) * mm, "end": v(220, 208.35) * mm});
            skLineSegment(sketch, "E23.10.6.11", {"start": v(210.43, 224.92) * mm, "end": v(229.57, 224.92) * mm});
            skLineSegment(sketch, "E23.11.0.0", {"start": v(230.43, -17.07) * mm, "end": v(249.57, -17.07) * mm});
            skLineSegment(sketch, "E23.11.0.1", {"start": v(240, -0.5) * mm, "end": v(230.43, -17.07) * mm});
            skLineSegment(sketch, "E23.11.0.2", {"start": v(249.57, -17.07) * mm, "end": v(240, -0.5) * mm});
            skLineSegment(sketch, "E23.11.0.3", {"start": v(220.43, -0.25) * mm, "end": v(239.57, -0.25) * mm});
            skLineSegment(sketch, "E23.11.0.4", {"start": v(239.57, -0.25) * mm, "end": v(230, -16.82) * mm});
            skLineSegment(sketch, "E23.11.0.5", {"start": v(230, -16.82) * mm, "end": v(220.43, -0.25) * mm});
            skLineSegment(sketch, "E23.11.0.6", {"start": v(230, 16.82) * mm, "end": v(220.43, 0.25) * mm});
            skLineSegment(sketch, "E23.11.0.7", {"start": v(220.43, 0.25) * mm, "end": v(239.57, 0.25) * mm});
            skLineSegment(sketch, "E23.11.0.8", {"start": v(239.57, 0.25) * mm, "end": v(230, 16.82) * mm});
            skLineSegment(sketch, "E23.11.0.9", {"start": v(240, 0.5) * mm, "end": v(230.43, 17.07) * mm});
            skLineSegment(sketch, "E23.11.0.10", {"start": v(249.57, 17.07) * mm, "end": v(240, 0.5) * mm});
            skLineSegment(sketch, "E23.11.0.11", {"start": v(230.43, 17.07) * mm, "end": v(249.57, 17.07) * mm});
            skLineSegment(sketch, "E23.11.1.0", {"start": v(230.43, 17.57) * mm, "end": v(249.57, 17.57) * mm});
            skLineSegment(sketch, "E23.11.1.1", {"start": v(240, 34.14) * mm, "end": v(230.43, 17.57) * mm});
            skLineSegment(sketch, "E23.11.1.2", {"start": v(249.57, 17.57) * mm, "end": v(240, 34.14) * mm});
            skLineSegment(sketch, "E23.11.1.3", {"start": v(220.43, 34.4) * mm, "end": v(239.57, 34.4) * mm});
            skLineSegment(sketch, "E23.11.1.4", {"start": v(239.57, 34.4) * mm, "end": v(230, 17.82) * mm});
            skLineSegment(sketch, "E23.11.1.5", {"start": v(230, 17.82) * mm, "end": v(220.43, 34.4) * mm});
            skLineSegment(sketch, "E23.11.1.6", {"start": v(230, 51.46) * mm, "end": v(220.43, 34.9) * mm});
            skLineSegment(sketch, "E23.11.1.7", {"start": v(220.43, 34.9) * mm, "end": v(239.57, 34.9) * mm});
            skLineSegment(sketch, "E23.11.1.8", {"start": v(239.57, 34.9) * mm, "end": v(230, 51.46) * mm});
            skLineSegment(sketch, "E23.11.1.9", {"start": v(240, 35.14) * mm, "end": v(230.43, 51.71) * mm});
            skLineSegment(sketch, "E23.11.1.10", {"start": v(249.57, 51.71) * mm, "end": v(240, 35.14) * mm});
            skLineSegment(sketch, "E23.11.1.11", {"start": v(230.43, 51.71) * mm, "end": v(249.57, 51.71) * mm});
            skLineSegment(sketch, "E23.11.2.0", {"start": v(230.43, 52.21) * mm, "end": v(249.57, 52.21) * mm});
            skLineSegment(sketch, "E23.11.2.1", {"start": v(240, 68.78) * mm, "end": v(230.43, 52.21) * mm});
            skLineSegment(sketch, "E23.11.2.2", {"start": v(249.57, 52.21) * mm, "end": v(240, 68.78) * mm});
            skLineSegment(sketch, "E23.11.2.3", {"start": v(220.43, 69.03) * mm, "end": v(239.57, 69.03) * mm});
            skLineSegment(sketch, "E23.11.2.4", {"start": v(239.57, 69.03) * mm, "end": v(230, 52.46) * mm});
            skLineSegment(sketch, "E23.11.2.5", {"start": v(230, 52.46) * mm, "end": v(220.43, 69.03) * mm});
            skLineSegment(sketch, "E23.11.2.6", {"start": v(230, 86.1) * mm, "end": v(220.43, 69.53) * mm});
            skLineSegment(sketch, "E23.11.2.7", {"start": v(220.43, 69.53) * mm, "end": v(239.57, 69.53) * mm});
            skLineSegment(sketch, "E23.11.2.8", {"start": v(239.57, 69.53) * mm, "end": v(230, 86.1) * mm});
            skLineSegment(sketch, "E23.11.2.9", {"start": v(240, 69.78) * mm, "end": v(230.43, 86.35) * mm});
            skLineSegment(sketch, "E23.11.2.10", {"start": v(249.57, 86.35) * mm, "end": v(240, 69.78) * mm});
            skLineSegment(sketch, "E23.11.2.11", {"start": v(230.43, 86.35) * mm, "end": v(249.57, 86.35) * mm});
            skLineSegment(sketch, "E23.11.3.0", {"start": v(230.43, 86.85) * mm, "end": v(249.57, 86.85) * mm});
            skLineSegment(sketch, "E23.11.3.1", {"start": v(240, 103.42) * mm, "end": v(230.43, 86.85) * mm});
            skLineSegment(sketch, "E23.11.3.2", {"start": v(249.57, 86.85) * mm, "end": v(240, 103.42) * mm});
            skLineSegment(sketch, "E23.11.3.3", {"start": v(220.43, 103.67) * mm, "end": v(239.57, 103.67) * mm});
            skLineSegment(sketch, "E23.11.3.4", {"start": v(239.57, 103.67) * mm, "end": v(230, 87.1) * mm});
            skLineSegment(sketch, "E23.11.3.5", {"start": v(230, 87.1) * mm, "end": v(220.43, 103.67) * mm});
            skLineSegment(sketch, "E23.11.3.6", {"start": v(230, 120.74) * mm, "end": v(220.43, 104.17) * mm});
            skLineSegment(sketch, "E23.11.3.7", {"start": v(220.43, 104.17) * mm, "end": v(239.57, 104.17) * mm});
            skLineSegment(sketch, "E23.11.3.8", {"start": v(239.57, 104.17) * mm, "end": v(230, 120.74) * mm});
            skLineSegment(sketch, "E23.11.3.9", {"start": v(240, 104.42) * mm, "end": v(230.43, 121) * mm});
            skLineSegment(sketch, "E23.11.3.10", {"start": v(249.57, 121) * mm, "end": v(240, 104.42) * mm});
            skLineSegment(sketch, "E23.11.3.11", {"start": v(230.43, 121) * mm, "end": v(249.57, 121) * mm});
            skLineSegment(sketch, "E23.11.4.0", {"start": v(230.43, 121.5) * mm, "end": v(249.57, 121.5) * mm});
            skLineSegment(sketch, "E23.11.4.1", {"start": v(240, 138.06) * mm, "end": v(230.43, 121.5) * mm});
            skLineSegment(sketch, "E23.11.4.2", {"start": v(249.57, 121.5) * mm, "end": v(240, 138.06) * mm});
            skLineSegment(sketch, "E23.11.4.3", {"start": v(220.43, 138.31) * mm, "end": v(239.57, 138.31) * mm});
            skLineSegment(sketch, "E23.11.4.4", {"start": v(239.57, 138.31) * mm, "end": v(230, 121.74) * mm});
            skLineSegment(sketch, "E23.11.4.5", {"start": v(230, 121.74) * mm, "end": v(220.43, 138.31) * mm});
            skLineSegment(sketch, "E23.11.4.6", {"start": v(230, 155.38) * mm, "end": v(220.43, 138.81) * mm});
            skLineSegment(sketch, "E23.11.4.7", {"start": v(220.43, 138.81) * mm, "end": v(239.57, 138.81) * mm});
            skLineSegment(sketch, "E23.11.4.8", {"start": v(239.57, 138.81) * mm, "end": v(230, 155.38) * mm});
            skLineSegment(sketch, "E23.11.4.9", {"start": v(240, 139.06) * mm, "end": v(230.43, 155.63) * mm});
            skLineSegment(sketch, "E23.11.4.10", {"start": v(249.57, 155.63) * mm, "end": v(240, 139.06) * mm});
            skLineSegment(sketch, "E23.11.4.11", {"start": v(230.43, 155.63) * mm, "end": v(249.57, 155.63) * mm});
            skLineSegment(sketch, "E23.11.5.0", {"start": v(230.43, 156.13) * mm, "end": v(249.57, 156.13) * mm});
            skLineSegment(sketch, "E23.11.5.1", {"start": v(240, 172.7) * mm, "end": v(230.43, 156.13) * mm});
            skLineSegment(sketch, "E23.11.5.2", {"start": v(249.57, 156.13) * mm, "end": v(240, 172.7) * mm});
            skLineSegment(sketch, "E23.11.5.3", {"start": v(220.43, 172.96) * mm, "end": v(239.57, 172.96) * mm});
            skLineSegment(sketch, "E23.11.5.4", {"start": v(239.57, 172.96) * mm, "end": v(230, 156.38) * mm});
            skLineSegment(sketch, "E23.11.5.5", {"start": v(230, 156.38) * mm, "end": v(220.43, 172.96) * mm});
            skLineSegment(sketch, "E23.11.5.6", {"start": v(230, 190.03) * mm, "end": v(220.43, 173.46) * mm});
            skLineSegment(sketch, "E23.11.5.7", {"start": v(220.43, 173.46) * mm, "end": v(239.57, 173.46) * mm});
            skLineSegment(sketch, "E23.11.5.8", {"start": v(239.57, 173.46) * mm, "end": v(230, 190.03) * mm});
            skLineSegment(sketch, "E23.11.5.9", {"start": v(240, 173.7) * mm, "end": v(230.43, 190.28) * mm});
            skLineSegment(sketch, "E23.11.5.10", {"start": v(249.57, 190.28) * mm, "end": v(240, 173.7) * mm});
            skLineSegment(sketch, "E23.11.5.11", {"start": v(230.43, 190.28) * mm, "end": v(249.57, 190.28) * mm});
            skLineSegment(sketch, "E23.11.6.0", {"start": v(230.43, 190.78) * mm, "end": v(249.57, 190.78) * mm});
            skLineSegment(sketch, "E23.11.6.1", {"start": v(240, 207.35) * mm, "end": v(230.43, 190.78) * mm});
            skLineSegment(sketch, "E23.11.6.2", {"start": v(249.57, 190.78) * mm, "end": v(240, 207.35) * mm});
            skLineSegment(sketch, "E23.11.6.3", {"start": v(220.43, 207.6) * mm, "end": v(239.57, 207.6) * mm});
            skLineSegment(sketch, "E23.11.6.4", {"start": v(239.57, 207.6) * mm, "end": v(230, 191.03) * mm});
            skLineSegment(sketch, "E23.11.6.5", {"start": v(230, 191.03) * mm, "end": v(220.43, 207.6) * mm});
            skLineSegment(sketch, "E23.11.6.6", {"start": v(230, 224.67) * mm, "end": v(220.43, 208.1) * mm});
            skLineSegment(sketch, "E23.11.6.7", {"start": v(220.43, 208.1) * mm, "end": v(239.57, 208.1) * mm});
            skLineSegment(sketch, "E23.11.6.8", {"start": v(239.57, 208.1) * mm, "end": v(230, 224.67) * mm});
            skLineSegment(sketch, "E23.11.6.9", {"start": v(240, 208.35) * mm, "end": v(230.43, 224.92) * mm});
            skLineSegment(sketch, "E23.11.6.10", {"start": v(249.57, 224.92) * mm, "end": v(240, 208.35) * mm});
            skLineSegment(sketch, "E23.11.6.11", {"start": v(230.43, 224.92) * mm, "end": v(249.57, 224.92) * mm});
            skLineSegment(sketch, "E23.12.0.0", {"start": v(250.43, -17.07) * mm, "end": v(269.57, -17.07) * mm});
            skLineSegment(sketch, "E23.12.0.1", {"start": v(260, -0.5) * mm, "end": v(250.43, -17.07) * mm});
            skLineSegment(sketch, "E23.12.0.2", {"start": v(269.57, -17.07) * mm, "end": v(260, -0.5) * mm});
            skLineSegment(sketch, "E23.12.0.3", {"start": v(240.43, -0.25) * mm, "end": v(259.57, -0.25) * mm});
            skLineSegment(sketch, "E23.12.0.4", {"start": v(259.57, -0.25) * mm, "end": v(250, -16.82) * mm});
            skLineSegment(sketch, "E23.12.0.5", {"start": v(250, -16.82) * mm, "end": v(240.43, -0.25) * mm});
            skLineSegment(sketch, "E23.12.0.6", {"start": v(250, 16.82) * mm, "end": v(240.43, 0.25) * mm});
            skLineSegment(sketch, "E23.12.0.7", {"start": v(240.43, 0.25) * mm, "end": v(259.57, 0.25) * mm});
            skLineSegment(sketch, "E23.12.0.8", {"start": v(259.57, 0.25) * mm, "end": v(250, 16.82) * mm});
            skLineSegment(sketch, "E23.12.0.9", {"start": v(260, 0.5) * mm, "end": v(250.43, 17.07) * mm});
            skLineSegment(sketch, "E23.12.0.10", {"start": v(269.57, 17.07) * mm, "end": v(260, 0.5) * mm});
            skLineSegment(sketch, "E23.12.0.11", {"start": v(250.43, 17.07) * mm, "end": v(269.57, 17.07) * mm});
            skLineSegment(sketch, "E23.12.1.0", {"start": v(250.43, 17.57) * mm, "end": v(269.57, 17.57) * mm});
            skLineSegment(sketch, "E23.12.1.1", {"start": v(260, 34.14) * mm, "end": v(250.43, 17.57) * mm});
            skLineSegment(sketch, "E23.12.1.2", {"start": v(269.57, 17.57) * mm, "end": v(260, 34.14) * mm});
            skLineSegment(sketch, "E23.12.1.3", {"start": v(240.43, 34.4) * mm, "end": v(259.57, 34.4) * mm});
            skLineSegment(sketch, "E23.12.1.4", {"start": v(259.57, 34.4) * mm, "end": v(250, 17.82) * mm});
            skLineSegment(sketch, "E23.12.1.5", {"start": v(250, 17.82) * mm, "end": v(240.43, 34.4) * mm});
            skLineSegment(sketch, "E23.12.1.6", {"start": v(250, 51.46) * mm, "end": v(240.43, 34.9) * mm});
            skLineSegment(sketch, "E23.12.1.7", {"start": v(240.43, 34.9) * mm, "end": v(259.57, 34.9) * mm});
            skLineSegment(sketch, "E23.12.1.8", {"start": v(259.57, 34.9) * mm, "end": v(250, 51.46) * mm});
            skLineSegment(sketch, "E23.12.1.9", {"start": v(260, 35.14) * mm, "end": v(250.43, 51.71) * mm});
            skLineSegment(sketch, "E23.12.1.10", {"start": v(269.57, 51.71) * mm, "end": v(260, 35.14) * mm});
            skLineSegment(sketch, "E23.12.1.11", {"start": v(250.43, 51.71) * mm, "end": v(269.57, 51.71) * mm});
            skLineSegment(sketch, "E23.12.2.0", {"start": v(250.43, 52.21) * mm, "end": v(269.57, 52.21) * mm});
            skLineSegment(sketch, "E23.12.2.1", {"start": v(260, 68.78) * mm, "end": v(250.43, 52.21) * mm});
            skLineSegment(sketch, "E23.12.2.2", {"start": v(269.57, 52.21) * mm, "end": v(260, 68.78) * mm});
            skLineSegment(sketch, "E23.12.2.3", {"start": v(240.43, 69.03) * mm, "end": v(259.57, 69.03) * mm});
            skLineSegment(sketch, "E23.12.2.4", {"start": v(259.57, 69.03) * mm, "end": v(250, 52.46) * mm});
            skLineSegment(sketch, "E23.12.2.5", {"start": v(250, 52.46) * mm, "end": v(240.43, 69.03) * mm});
            skLineSegment(sketch, "E23.12.2.6", {"start": v(250, 86.1) * mm, "end": v(240.43, 69.53) * mm});
            skLineSegment(sketch, "E23.12.2.7", {"start": v(240.43, 69.53) * mm, "end": v(259.57, 69.53) * mm});
            skLineSegment(sketch, "E23.12.2.8", {"start": v(259.57, 69.53) * mm, "end": v(250, 86.1) * mm});
            skLineSegment(sketch, "E23.12.2.9", {"start": v(260, 69.78) * mm, "end": v(250.43, 86.35) * mm});
            skLineSegment(sketch, "E23.12.2.10", {"start": v(269.57, 86.35) * mm, "end": v(260, 69.78) * mm});
            skLineSegment(sketch, "E23.12.2.11", {"start": v(250.43, 86.35) * mm, "end": v(269.57, 86.35) * mm});
            skLineSegment(sketch, "E23.12.3.0", {"start": v(250.43, 86.85) * mm, "end": v(269.57, 86.85) * mm});
            skLineSegment(sketch, "E23.12.3.1", {"start": v(260, 103.42) * mm, "end": v(250.43, 86.85) * mm});
            skLineSegment(sketch, "E23.12.3.2", {"start": v(269.57, 86.85) * mm, "end": v(260, 103.42) * mm});
            skLineSegment(sketch, "E23.12.3.3", {"start": v(240.43, 103.67) * mm, "end": v(259.57, 103.67) * mm});
            skLineSegment(sketch, "E23.12.3.4", {"start": v(259.57, 103.67) * mm, "end": v(250, 87.1) * mm});
            skLineSegment(sketch, "E23.12.3.5", {"start": v(250, 87.1) * mm, "end": v(240.43, 103.67) * mm});
            skLineSegment(sketch, "E23.12.3.6", {"start": v(250, 120.74) * mm, "end": v(240.43, 104.17) * mm});
            skLineSegment(sketch, "E23.12.3.7", {"start": v(240.43, 104.17) * mm, "end": v(259.57, 104.17) * mm});
            skLineSegment(sketch, "E23.12.3.8", {"start": v(259.57, 104.17) * mm, "end": v(250, 120.74) * mm});
            skLineSegment(sketch, "E23.12.3.9", {"start": v(260, 104.42) * mm, "end": v(250.43, 121) * mm});
            skLineSegment(sketch, "E23.12.3.10", {"start": v(269.57, 121) * mm, "end": v(260, 104.42) * mm});
            skLineSegment(sketch, "E23.12.3.11", {"start": v(250.43, 121) * mm, "end": v(269.57, 121) * mm});
            skLineSegment(sketch, "E23.12.4.0", {"start": v(250.43, 121.5) * mm, "end": v(269.57, 121.5) * mm});
            skLineSegment(sketch, "E23.12.4.1", {"start": v(260, 138.06) * mm, "end": v(250.43, 121.5) * mm});
            skLineSegment(sketch, "E23.12.4.2", {"start": v(269.57, 121.5) * mm, "end": v(260, 138.06) * mm});
            skLineSegment(sketch, "E23.12.4.3", {"start": v(240.43, 138.31) * mm, "end": v(259.57, 138.31) * mm});
            skLineSegment(sketch, "E23.12.4.4", {"start": v(259.57, 138.31) * mm, "end": v(250, 121.74) * mm});
            skLineSegment(sketch, "E23.12.4.5", {"start": v(250, 121.74) * mm, "end": v(240.43, 138.31) * mm});
            skLineSegment(sketch, "E23.12.4.6", {"start": v(250, 155.38) * mm, "end": v(240.43, 138.81) * mm});
            skLineSegment(sketch, "E23.12.4.7", {"start": v(240.43, 138.81) * mm, "end": v(259.57, 138.81) * mm});
            skLineSegment(sketch, "E23.12.4.8", {"start": v(259.57, 138.81) * mm, "end": v(250, 155.38) * mm});
            skLineSegment(sketch, "E23.12.4.9", {"start": v(260, 139.06) * mm, "end": v(250.43, 155.63) * mm});
            skLineSegment(sketch, "E23.12.4.10", {"start": v(269.57, 155.63) * mm, "end": v(260, 139.06) * mm});
            skLineSegment(sketch, "E23.12.4.11", {"start": v(250.43, 155.63) * mm, "end": v(269.57, 155.63) * mm});
            skLineSegment(sketch, "E23.12.5.0", {"start": v(250.43, 156.13) * mm, "end": v(269.57, 156.13) * mm});
            skLineSegment(sketch, "E23.12.5.1", {"start": v(260, 172.7) * mm, "end": v(250.43, 156.13) * mm});
            skLineSegment(sketch, "E23.12.5.2", {"start": v(269.57, 156.13) * mm, "end": v(260, 172.7) * mm});
            skLineSegment(sketch, "E23.12.5.3", {"start": v(240.43, 172.96) * mm, "end": v(259.57, 172.96) * mm});
            skLineSegment(sketch, "E23.12.5.4", {"start": v(259.57, 172.96) * mm, "end": v(250, 156.38) * mm});
            skLineSegment(sketch, "E23.12.5.5", {"start": v(250, 156.38) * mm, "end": v(240.43, 172.96) * mm});
            skLineSegment(sketch, "E23.12.5.6", {"start": v(250, 190.03) * mm, "end": v(240.43, 173.46) * mm});
            skLineSegment(sketch, "E23.12.5.7", {"start": v(240.43, 173.46) * mm, "end": v(259.57, 173.46) * mm});
            skLineSegment(sketch, "E23.12.5.8", {"start": v(259.57, 173.46) * mm, "end": v(250, 190.03) * mm});
            skLineSegment(sketch, "E23.12.5.9", {"start": v(260, 173.7) * mm, "end": v(250.43, 190.28) * mm});
            skLineSegment(sketch, "E23.12.5.10", {"start": v(269.57, 190.28) * mm, "end": v(260, 173.7) * mm});
            skLineSegment(sketch, "E23.12.5.11", {"start": v(250.43, 190.28) * mm, "end": v(269.57, 190.28) * mm});
            skLineSegment(sketch, "E23.12.6.0", {"start": v(250.43, 190.78) * mm, "end": v(269.57, 190.78) * mm});
            skLineSegment(sketch, "E23.12.6.1", {"start": v(260, 207.35) * mm, "end": v(250.43, 190.78) * mm});
            skLineSegment(sketch, "E23.12.6.2", {"start": v(269.57, 190.78) * mm, "end": v(260, 207.35) * mm});
            skLineSegment(sketch, "E23.12.6.3", {"start": v(240.43, 207.6) * mm, "end": v(259.57, 207.6) * mm});
            skLineSegment(sketch, "E23.12.6.4", {"start": v(259.57, 207.6) * mm, "end": v(250, 191.03) * mm});
            skLineSegment(sketch, "E23.12.6.5", {"start": v(250, 191.03) * mm, "end": v(240.43, 207.6) * mm});
            skLineSegment(sketch, "E23.12.6.6", {"start": v(250, 224.67) * mm, "end": v(240.43, 208.1) * mm});
            skLineSegment(sketch, "E23.12.6.7", {"start": v(240.43, 208.1) * mm, "end": v(259.57, 208.1) * mm});
            skLineSegment(sketch, "E23.12.6.8", {"start": v(259.57, 208.1) * mm, "end": v(250, 224.67) * mm});
            skLineSegment(sketch, "E23.12.6.9", {"start": v(260, 208.35) * mm, "end": v(250.43, 224.92) * mm});
            skLineSegment(sketch, "E23.12.6.10", {"start": v(269.57, 224.92) * mm, "end": v(260, 208.35) * mm});
            skLineSegment(sketch, "E23.12.6.11", {"start": v(250.43, 224.92) * mm, "end": v(269.57, 224.92) * mm});
            skLineSegment(sketch, "E23.13.0.0", {"start": v(270.43, -17.07) * mm, "end": v(289.57, -17.07) * mm});
            skLineSegment(sketch, "E23.13.0.1", {"start": v(280, -0.5) * mm, "end": v(270.43, -17.07) * mm});
            skLineSegment(sketch, "E23.13.0.2", {"start": v(289.57, -17.07) * mm, "end": v(280, -0.5) * mm});
            skLineSegment(sketch, "E23.13.0.3", {"start": v(260.43, -0.25) * mm, "end": v(279.57, -0.25) * mm});
            skLineSegment(sketch, "E23.13.0.4", {"start": v(279.57, -0.25) * mm, "end": v(270, -16.82) * mm});
            skLineSegment(sketch, "E23.13.0.5", {"start": v(270, -16.82) * mm, "end": v(260.43, -0.25) * mm});
            skLineSegment(sketch, "E23.13.0.6", {"start": v(270, 16.82) * mm, "end": v(260.43, 0.25) * mm});
            skLineSegment(sketch, "E23.13.0.7", {"start": v(260.43, 0.25) * mm, "end": v(279.57, 0.25) * mm});
            skLineSegment(sketch, "E23.13.0.8", {"start": v(279.57, 0.25) * mm, "end": v(270, 16.82) * mm});
            skLineSegment(sketch, "E23.13.0.9", {"start": v(280, 0.5) * mm, "end": v(270.43, 17.07) * mm});
            skLineSegment(sketch, "E23.13.0.10", {"start": v(289.57, 17.07) * mm, "end": v(280, 0.5) * mm});
            skLineSegment(sketch, "E23.13.0.11", {"start": v(270.43, 17.07) * mm, "end": v(289.57, 17.07) * mm});
            skLineSegment(sketch, "E23.13.1.0", {"start": v(270.43, 17.57) * mm, "end": v(289.57, 17.57) * mm});
            skLineSegment(sketch, "E23.13.1.1", {"start": v(280, 34.14) * mm, "end": v(270.43, 17.57) * mm});
            skLineSegment(sketch, "E23.13.1.2", {"start": v(289.57, 17.57) * mm, "end": v(280, 34.14) * mm});
            skLineSegment(sketch, "E23.13.1.3", {"start": v(260.43, 34.4) * mm, "end": v(279.57, 34.4) * mm});
            skLineSegment(sketch, "E23.13.1.4", {"start": v(279.57, 34.4) * mm, "end": v(270, 17.82) * mm});
            skLineSegment(sketch, "E23.13.1.5", {"start": v(270, 17.82) * mm, "end": v(260.43, 34.4) * mm});
            skLineSegment(sketch, "E23.13.1.6", {"start": v(270, 51.46) * mm, "end": v(260.43, 34.9) * mm});
            skLineSegment(sketch, "E23.13.1.7", {"start": v(260.43, 34.9) * mm, "end": v(279.57, 34.9) * mm});
            skLineSegment(sketch, "E23.13.1.8", {"start": v(279.57, 34.9) * mm, "end": v(270, 51.46) * mm});
            skLineSegment(sketch, "E23.13.1.9", {"start": v(280, 35.14) * mm, "end": v(270.43, 51.71) * mm});
            skLineSegment(sketch, "E23.13.1.10", {"start": v(289.57, 51.71) * mm, "end": v(280, 35.14) * mm});
            skLineSegment(sketch, "E23.13.1.11", {"start": v(270.43, 51.71) * mm, "end": v(289.57, 51.71) * mm});
            skLineSegment(sketch, "E23.13.2.0", {"start": v(270.43, 52.21) * mm, "end": v(289.57, 52.21) * mm});
            skLineSegment(sketch, "E23.13.2.1", {"start": v(280, 68.78) * mm, "end": v(270.43, 52.21) * mm});
            skLineSegment(sketch, "E23.13.2.2", {"start": v(289.57, 52.21) * mm, "end": v(280, 68.78) * mm});
            skLineSegment(sketch, "E23.13.2.3", {"start": v(260.43, 69.03) * mm, "end": v(279.57, 69.03) * mm});
            skLineSegment(sketch, "E23.13.2.4", {"start": v(279.57, 69.03) * mm, "end": v(270, 52.46) * mm});
            skLineSegment(sketch, "E23.13.2.5", {"start": v(270, 52.46) * mm, "end": v(260.43, 69.03) * mm});
            skLineSegment(sketch, "E23.13.2.6", {"start": v(270, 86.1) * mm, "end": v(260.43, 69.53) * mm});
            skLineSegment(sketch, "E23.13.2.7", {"start": v(260.43, 69.53) * mm, "end": v(279.57, 69.53) * mm});
            skLineSegment(sketch, "E23.13.2.8", {"start": v(279.57, 69.53) * mm, "end": v(270, 86.1) * mm});
            skLineSegment(sketch, "E23.13.2.9", {"start": v(280, 69.78) * mm, "end": v(270.43, 86.35) * mm});
            skLineSegment(sketch, "E23.13.2.10", {"start": v(289.57, 86.35) * mm, "end": v(280, 69.78) * mm});
            skLineSegment(sketch, "E23.13.2.11", {"start": v(270.43, 86.35) * mm, "end": v(289.57, 86.35) * mm});
            skLineSegment(sketch, "E23.13.3.0", {"start": v(270.43, 86.85) * mm, "end": v(289.57, 86.85) * mm});
            skLineSegment(sketch, "E23.13.3.1", {"start": v(280, 103.42) * mm, "end": v(270.43, 86.85) * mm});
            skLineSegment(sketch, "E23.13.3.2", {"start": v(289.57, 86.85) * mm, "end": v(280, 103.42) * mm});
            skLineSegment(sketch, "E23.13.3.3", {"start": v(260.43, 103.67) * mm, "end": v(279.57, 103.67) * mm});
            skLineSegment(sketch, "E23.13.3.4", {"start": v(279.57, 103.67) * mm, "end": v(270, 87.1) * mm});
            skLineSegment(sketch, "E23.13.3.5", {"start": v(270, 87.1) * mm, "end": v(260.43, 103.67) * mm});
            skLineSegment(sketch, "E23.13.3.6", {"start": v(270, 120.74) * mm, "end": v(260.43, 104.17) * mm});
            skLineSegment(sketch, "E23.13.3.7", {"start": v(260.43, 104.17) * mm, "end": v(279.57, 104.17) * mm});
            skLineSegment(sketch, "E23.13.3.8", {"start": v(279.57, 104.17) * mm, "end": v(270, 120.74) * mm});
            skLineSegment(sketch, "E23.13.3.9", {"start": v(280, 104.42) * mm, "end": v(270.43, 121) * mm});
            skLineSegment(sketch, "E23.13.3.10", {"start": v(289.57, 121) * mm, "end": v(280, 104.42) * mm});
            skLineSegment(sketch, "E23.13.3.11", {"start": v(270.43, 121) * mm, "end": v(289.57, 121) * mm});
            skLineSegment(sketch, "E23.13.4.0", {"start": v(270.43, 121.5) * mm, "end": v(289.57, 121.5) * mm});
            skLineSegment(sketch, "E23.13.4.1", {"start": v(280, 138.06) * mm, "end": v(270.43, 121.5) * mm});
            skLineSegment(sketch, "E23.13.4.2", {"start": v(289.57, 121.5) * mm, "end": v(280, 138.06) * mm});
            skLineSegment(sketch, "E23.13.4.3", {"start": v(260.43, 138.31) * mm, "end": v(279.57, 138.31) * mm});
            skLineSegment(sketch, "E23.13.4.4", {"start": v(279.57, 138.31) * mm, "end": v(270, 121.74) * mm});
            skLineSegment(sketch, "E23.13.4.5", {"start": v(270, 121.74) * mm, "end": v(260.43, 138.31) * mm});
            skLineSegment(sketch, "E23.13.4.6", {"start": v(270, 155.38) * mm, "end": v(260.43, 138.81) * mm});
            skLineSegment(sketch, "E23.13.4.7", {"start": v(260.43, 138.81) * mm, "end": v(279.57, 138.81) * mm});
            skLineSegment(sketch, "E23.13.4.8", {"start": v(279.57, 138.81) * mm, "end": v(270, 155.38) * mm});
            skLineSegment(sketch, "E23.13.4.9", {"start": v(280, 139.06) * mm, "end": v(270.43, 155.63) * mm});
            skLineSegment(sketch, "E23.13.4.10", {"start": v(289.57, 155.63) * mm, "end": v(280, 139.06) * mm});
            skLineSegment(sketch, "E23.13.4.11", {"start": v(270.43, 155.63) * mm, "end": v(289.57, 155.63) * mm});
            skLineSegment(sketch, "E23.13.5.0", {"start": v(270.43, 156.13) * mm, "end": v(289.57, 156.13) * mm});
            skLineSegment(sketch, "E23.13.5.1", {"start": v(280, 172.7) * mm, "end": v(270.43, 156.13) * mm});
            skLineSegment(sketch, "E23.13.5.2", {"start": v(289.57, 156.13) * mm, "end": v(280, 172.7) * mm});
            skLineSegment(sketch, "E23.13.5.3", {"start": v(260.43, 172.96) * mm, "end": v(279.57, 172.96) * mm});
            skLineSegment(sketch, "E23.13.5.4", {"start": v(279.57, 172.96) * mm, "end": v(270, 156.38) * mm});
            skLineSegment(sketch, "E23.13.5.5", {"start": v(270, 156.38) * mm, "end": v(260.43, 172.96) * mm});
            skLineSegment(sketch, "E23.13.5.6", {"start": v(270, 190.03) * mm, "end": v(260.43, 173.46) * mm});
            skLineSegment(sketch, "E23.13.5.7", {"start": v(260.43, 173.46) * mm, "end": v(279.57, 173.46) * mm});
            skLineSegment(sketch, "E23.13.5.8", {"start": v(279.57, 173.46) * mm, "end": v(270, 190.03) * mm});
            skLineSegment(sketch, "E23.13.5.9", {"start": v(280, 173.7) * mm, "end": v(270.43, 190.28) * mm});
            skLineSegment(sketch, "E23.13.5.10", {"start": v(289.57, 190.28) * mm, "end": v(280, 173.7) * mm});
            skLineSegment(sketch, "E23.13.5.11", {"start": v(270.43, 190.28) * mm, "end": v(289.57, 190.28) * mm});
            skLineSegment(sketch, "E23.13.6.0", {"start": v(270.43, 190.78) * mm, "end": v(289.57, 190.78) * mm});
            skLineSegment(sketch, "E23.13.6.1", {"start": v(280, 207.35) * mm, "end": v(270.43, 190.78) * mm});
            skLineSegment(sketch, "E23.13.6.2", {"start": v(289.57, 190.78) * mm, "end": v(280, 207.35) * mm});
            skLineSegment(sketch, "E23.13.6.3", {"start": v(260.43, 207.6) * mm, "end": v(279.57, 207.6) * mm});
            skLineSegment(sketch, "E23.13.6.4", {"start": v(279.57, 207.6) * mm, "end": v(270, 191.03) * mm});
            skLineSegment(sketch, "E23.13.6.5", {"start": v(270, 191.03) * mm, "end": v(260.43, 207.6) * mm});
            skLineSegment(sketch, "E23.13.6.6", {"start": v(270, 224.67) * mm, "end": v(260.43, 208.1) * mm});
            skLineSegment(sketch, "E23.13.6.7", {"start": v(260.43, 208.1) * mm, "end": v(279.57, 208.1) * mm});
            skLineSegment(sketch, "E23.13.6.8", {"start": v(279.57, 208.1) * mm, "end": v(270, 224.67) * mm});
            skLineSegment(sketch, "E23.13.6.9", {"start": v(280, 208.35) * mm, "end": v(270.43, 224.92) * mm});
            skLineSegment(sketch, "E23.13.6.10", {"start": v(289.57, 224.92) * mm, "end": v(280, 208.35) * mm});
            skLineSegment(sketch, "E23.13.6.11", {"start": v(270.43, 224.92) * mm, "end": v(289.57, 224.92) * mm});
            skLineSegment(sketch, "E23.direction1", {"start": v(10.43, -17.07) * mm, "end": v(30.43, -17.07) * mm, "construction": true});
            skLineSegment(sketch, "E23.direction2", {"start": v(10.43, -17.07) * mm, "end": v(10.43, 17.57) * mm, "construction": true});
            skPoint(sketch, "E24.middle", {"position": v(-4.97, 0.22) * mm});
            skSolve(sketch);
        }
        {
            var Q0;
            Q0=makeQuery(id+"F0.imprint","IMPRINT",FACE,{"disambiguationData":[TD([[makeQuery(id+"F0.imprint","IMPRINT",EDGE,{"derivedFrom":sQuery(id+"F0.wireOp",EDGE,"E10.bottom")}),1.0]])]});
            extrude(context, id + "F1", {"entities" : qUnion([Q0]), "depth" : 5 * mm, "offsetDistance" : 25 * mm});
        }
        {
            var Q0;
            Q0=qCreatedBy(makeId("Top.planeOp"),FACE);
            var sketch = newSketch(context, id + "F2", { "sketchPlane" : qUnion([Q0])});
            skLineSegment(sketch, "E25", {"start": v(0, 0) * mm, "end": v(20, 0) * mm, "construction": true});
            skLineSegment(sketch, "E26", {"start": v(20, 0) * mm, "end": v(10, 17.32) * mm, "construction": true});
            skLineSegment(sketch, "E27", {"start": v(10, 17.32) * mm, "end": v(0, 0) * mm, "construction": true});
            skLineSegment(sketch, "E28.MirrorCS", {"start": v(10, -17.32) * mm, "end": v(0, 0) * mm, "construction": true});
            skLineSegment(sketch, "E29.MirrorCS", {"start": v(20, 0) * mm, "end": v(10, -17.32) * mm, "construction": true});
            skLineSegment(sketch, "E30.MirrorCS", {"start": v(30, -17.32) * mm, "end": v(20, 0) * mm, "construction": true});
            skLineSegment(sketch, "E31.MirrorCS", {"start": v(10, -17.32) * mm, "end": v(30, -17.32) * mm, "construction": true});
            skLineSegment(sketch, "E32.MirrorCS", {"start": v(30, 17.32) * mm, "end": v(20, 0) * mm, "construction": true});
            skLineSegment(sketch, "E33.MirrorCS", {"start": v(10, 17.32) * mm, "end": v(30, 17.32) * mm, "construction": true});
            skLineSegment(sketch, "E34.0.1.1", {"start": v(20, 34.64) * mm, "end": v(10, 17.32) * mm, "construction": true});
            skLineSegment(sketch, "E34.0.1.2", {"start": v(30, 17.32) * mm, "end": v(20, 34.64) * mm, "construction": true});
            skLineSegment(sketch, "E34.0.1.3", {"start": v(0, 34.64) * mm, "end": v(20, 34.64) * mm, "construction": true});
            skLineSegment(sketch, "E34.0.1.4", {"start": v(10, 17.32) * mm, "end": v(0, 34.64) * mm, "construction": true});
            skLineSegment(sketch, "E34.0.1.5", {"start": v(10, 51.96) * mm, "end": v(0, 34.64) * mm, "construction": true});
            skLineSegment(sketch, "E34.0.1.6", {"start": v(20, 34.64) * mm, "end": v(10, 51.96) * mm, "construction": true});
            skLineSegment(sketch, "E34.0.1.7", {"start": v(10, 51.96) * mm, "end": v(30, 51.96) * mm, "construction": true});
            skLineSegment(sketch, "E34.0.1.8", {"start": v(30, 51.96) * mm, "end": v(20, 34.64) * mm, "construction": true});
            skLineSegment(sketch, "E34.0.2.0", {"start": v(10, 51.96) * mm, "end": v(30, 51.96) * mm, "construction": true});
            skLineSegment(sketch, "E34.0.2.1", {"start": v(20, 69.28) * mm, "end": v(10, 51.96) * mm, "construction": true});
            skLineSegment(sketch, "E34.0.2.2", {"start": v(30, 51.96) * mm, "end": v(20, 69.28) * mm, "construction": true});
            skLineSegment(sketch, "E34.0.2.3", {"start": v(0, 69.28) * mm, "end": v(20, 69.28) * mm, "construction": true});
            skLineSegment(sketch, "E34.0.2.4", {"start": v(10, 51.96) * mm, "end": v(0, 69.28) * mm, "construction": true});
            skLineSegment(sketch, "E34.0.2.5", {"start": v(10, 86.6) * mm, "end": v(0, 69.28) * mm, "construction": true});
            skLineSegment(sketch, "E34.0.2.6", {"start": v(20, 69.28) * mm, "end": v(10, 86.6) * mm, "construction": true});
            skLineSegment(sketch, "E34.0.2.7", {"start": v(10, 86.6) * mm, "end": v(30, 86.6) * mm, "construction": true});
            skLineSegment(sketch, "E34.0.2.8", {"start": v(30, 86.6) * mm, "end": v(20, 69.28) * mm, "construction": true});
            skLineSegment(sketch, "E34.0.3.0", {"start": v(10, 86.6) * mm, "end": v(30, 86.6) * mm, "construction": true});
            skLineSegment(sketch, "E34.0.3.1", {"start": v(20, 103.92) * mm, "end": v(10, 86.6) * mm, "construction": true});
            skLineSegment(sketch, "E34.0.3.2", {"start": v(30, 86.6) * mm, "end": v(20, 103.92) * mm, "construction": true});
            skLineSegment(sketch, "E34.0.3.3", {"start": v(0, 103.92) * mm, "end": v(20, 103.92) * mm, "construction": true});
            skLineSegment(sketch, "E34.0.3.4", {"start": v(10, 86.6) * mm, "end": v(0, 103.92) * mm, "construction": true});
            skLineSegment(sketch, "E34.0.3.5", {"start": v(10, 121.24) * mm, "end": v(0, 103.92) * mm, "construction": true});
            skLineSegment(sketch, "E34.0.3.6", {"start": v(20, 103.92) * mm, "end": v(10, 121.24) * mm, "construction": true});
            skLineSegment(sketch, "E34.0.3.7", {"start": v(10, 121.24) * mm, "end": v(30, 121.24) * mm, "construction": true});
            skLineSegment(sketch, "E34.0.3.8", {"start": v(30, 121.24) * mm, "end": v(20, 103.92) * mm, "construction": true});
            skLineSegment(sketch, "E34.0.4.0", {"start": v(10, 121.24) * mm, "end": v(30, 121.24) * mm, "construction": true});
            skLineSegment(sketch, "E34.0.4.1", {"start": v(20, 138.56) * mm, "end": v(10, 121.24) * mm, "construction": true});
            skLineSegment(sketch, "E34.0.4.2", {"start": v(30, 121.24) * mm, "end": v(20, 138.56) * mm, "construction": true});
            skLineSegment(sketch, "E34.0.4.3", {"start": v(0, 138.56) * mm, "end": v(20, 138.56) * mm, "construction": true});
            skLineSegment(sketch, "E34.0.4.4", {"start": v(10, 121.24) * mm, "end": v(0, 138.56) * mm, "construction": true});
            skLineSegment(sketch, "E34.0.4.5", {"start": v(10, 155.88) * mm, "end": v(0, 138.56) * mm, "construction": true});
            skLineSegment(sketch, "E34.0.4.6", {"start": v(20, 138.56) * mm, "end": v(10, 155.88) * mm, "construction": true});
            skLineSegment(sketch, "E34.0.4.7", {"start": v(10, 155.88) * mm, "end": v(30, 155.88) * mm, "construction": true});
            skLineSegment(sketch, "E34.0.4.8", {"start": v(30, 155.88) * mm, "end": v(20, 138.56) * mm, "construction": true});
            skLineSegment(sketch, "E34.0.5.0", {"start": v(10, 155.88) * mm, "end": v(30, 155.88) * mm, "construction": true});
            skLineSegment(sketch, "E34.0.5.1", {"start": v(20, 173.2) * mm, "end": v(10, 155.88) * mm, "construction": true});
            skLineSegment(sketch, "E34.0.5.2", {"start": v(30, 155.88) * mm, "end": v(20, 173.2) * mm, "construction": true});
            skLineSegment(sketch, "E34.0.5.3", {"start": v(0, 173.2) * mm, "end": v(20, 173.2) * mm, "construction": true});
            skLineSegment(sketch, "E34.0.5.4", {"start": v(10, 155.88) * mm, "end": v(0, 173.2) * mm, "construction": true});
            skLineSegment(sketch, "E34.0.5.5", {"start": v(10, 190.53) * mm, "end": v(0, 173.2) * mm, "construction": true});
            skLineSegment(sketch, "E34.0.5.6", {"start": v(20, 173.2) * mm, "end": v(10, 190.53) * mm, "construction": true});
            skLineSegment(sketch, "E34.0.5.7", {"start": v(10, 190.53) * mm, "end": v(30, 190.53) * mm, "construction": true});
            skLineSegment(sketch, "E34.0.5.8", {"start": v(30, 190.53) * mm, "end": v(20, 173.2) * mm, "construction": true});
            skLineSegment(sketch, "E34.0.6.0", {"start": v(10, 190.53) * mm, "end": v(30, 190.53) * mm, "construction": true});
            skLineSegment(sketch, "E34.0.6.1", {"start": v(20, 207.85) * mm, "end": v(10, 190.53) * mm, "construction": true});
            skLineSegment(sketch, "E34.0.6.2", {"start": v(30, 190.53) * mm, "end": v(20, 207.85) * mm, "construction": true});
            skLineSegment(sketch, "E34.0.6.3", {"start": v(0, 207.85) * mm, "end": v(20, 207.85) * mm, "construction": true});
            skLineSegment(sketch, "E34.0.6.4", {"start": v(10, 190.53) * mm, "end": v(0, 207.85) * mm, "construction": true});
            skLineSegment(sketch, "E34.0.6.5", {"start": v(10, 225.17) * mm, "end": v(0, 207.85) * mm, "construction": true});
            skLineSegment(sketch, "E34.0.6.6", {"start": v(20, 207.85) * mm, "end": v(10, 225.17) * mm, "construction": true});
            skLineSegment(sketch, "E34.0.6.7", {"start": v(10, 225.17) * mm, "end": v(30, 225.17) * mm, "construction": true});
            skLineSegment(sketch, "E34.0.6.8", {"start": v(30, 225.17) * mm, "end": v(20, 207.85) * mm, "construction": true});
            skLineSegment(sketch, "E34.1.0.0", {"start": v(30, -17.32) * mm, "end": v(50, -17.32) * mm, "construction": true});
            skLineSegment(sketch, "E34.1.0.1", {"start": v(40, 0) * mm, "end": v(30, -17.32) * mm, "construction": true});
            skLineSegment(sketch, "E34.1.0.2", {"start": v(50, -17.32) * mm, "end": v(40, 0) * mm, "construction": true});
            skLineSegment(sketch, "E34.1.0.3", {"start": v(20, 0) * mm, "end": v(40, 0) * mm, "construction": true});
            skLineSegment(sketch, "E34.1.0.6", {"start": v(40, 0) * mm, "end": v(30, 17.32) * mm, "construction": true});
            skLineSegment(sketch, "E34.1.0.7", {"start": v(30, 17.32) * mm, "end": v(50, 17.32) * mm, "construction": true});
            skLineSegment(sketch, "E34.1.0.8", {"start": v(50, 17.32) * mm, "end": v(40, 0) * mm, "construction": true});
            skLineSegment(sketch, "E34.1.1.0", {"start": v(30, 17.32) * mm, "end": v(50, 17.32) * mm, "construction": true});
            skLineSegment(sketch, "E34.1.1.1", {"start": v(40, 34.64) * mm, "end": v(30, 17.32) * mm, "construction": true});
            skLineSegment(sketch, "E34.1.1.2", {"start": v(50, 17.32) * mm, "end": v(40, 34.64) * mm, "construction": true});
            skLineSegment(sketch, "E34.1.1.3", {"start": v(20, 34.64) * mm, "end": v(40, 34.64) * mm, "construction": true});
            skLineSegment(sketch, "E34.1.1.4", {"start": v(30, 17.32) * mm, "end": v(20, 34.64) * mm, "construction": true});
            skLineSegment(sketch, "E34.1.1.5", {"start": v(30, 51.96) * mm, "end": v(20, 34.64) * mm, "construction": true});
            skLineSegment(sketch, "E34.1.1.6", {"start": v(40, 34.64) * mm, "end": v(30, 51.96) * mm, "construction": true});
            skLineSegment(sketch, "E34.1.1.7", {"start": v(30, 51.96) * mm, "end": v(50, 51.96) * mm, "construction": true});
            skLineSegment(sketch, "E34.1.1.8", {"start": v(50, 51.96) * mm, "end": v(40, 34.64) * mm, "construction": true});
            skLineSegment(sketch, "E34.1.2.0", {"start": v(30, 51.96) * mm, "end": v(50, 51.96) * mm, "construction": true});
            skLineSegment(sketch, "E34.1.2.1", {"start": v(40, 69.28) * mm, "end": v(30, 51.96) * mm, "construction": true});
            skLineSegment(sketch, "E34.1.2.2", {"start": v(50, 51.96) * mm, "end": v(40, 69.28) * mm, "construction": true});
            skLineSegment(sketch, "E34.1.2.3", {"start": v(20, 69.28) * mm, "end": v(40, 69.28) * mm, "construction": true});
            skLineSegment(sketch, "E34.1.2.4", {"start": v(30, 51.96) * mm, "end": v(20, 69.28) * mm, "construction": true});
            skLineSegment(sketch, "E34.1.2.5", {"start": v(30, 86.6) * mm, "end": v(20, 69.28) * mm, "construction": true});
            skLineSegment(sketch, "E34.1.2.6", {"start": v(40, 69.28) * mm, "end": v(30, 86.6) * mm, "construction": true});
            skLineSegment(sketch, "E34.1.2.7", {"start": v(30, 86.6) * mm, "end": v(50, 86.6) * mm, "construction": true});
            skLineSegment(sketch, "E34.1.2.8", {"start": v(50, 86.6) * mm, "end": v(40, 69.28) * mm, "construction": true});
            skLineSegment(sketch, "E34.1.3.0", {"start": v(30, 86.6) * mm, "end": v(50, 86.6) * mm, "construction": true});
            skLineSegment(sketch, "E34.1.3.1", {"start": v(40, 103.92) * mm, "end": v(30, 86.6) * mm, "construction": true});
            skLineSegment(sketch, "E34.1.3.2", {"start": v(50, 86.6) * mm, "end": v(40, 103.92) * mm, "construction": true});
            skLineSegment(sketch, "E34.1.3.3", {"start": v(20, 103.92) * mm, "end": v(40, 103.92) * mm, "construction": true});
            skLineSegment(sketch, "E34.1.3.4", {"start": v(30, 86.6) * mm, "end": v(20, 103.92) * mm, "construction": true});
            skLineSegment(sketch, "E34.1.3.5", {"start": v(30, 121.24) * mm, "end": v(20, 103.92) * mm, "construction": true});
            skLineSegment(sketch, "E34.1.3.6", {"start": v(40, 103.92) * mm, "end": v(30, 121.24) * mm, "construction": true});
            skLineSegment(sketch, "E34.1.3.7", {"start": v(30, 121.24) * mm, "end": v(50, 121.24) * mm, "construction": true});
            skLineSegment(sketch, "E34.1.3.8", {"start": v(50, 121.24) * mm, "end": v(40, 103.92) * mm, "construction": true});
            skLineSegment(sketch, "E34.1.4.0", {"start": v(30, 121.24) * mm, "end": v(50, 121.24) * mm, "construction": true});
            skLineSegment(sketch, "E34.1.4.1", {"start": v(40, 138.56) * mm, "end": v(30, 121.24) * mm, "construction": true});
            skLineSegment(sketch, "E34.1.4.2", {"start": v(50, 121.24) * mm, "end": v(40, 138.56) * mm, "construction": true});
            skLineSegment(sketch, "E34.1.4.3", {"start": v(20, 138.56) * mm, "end": v(40, 138.56) * mm, "construction": true});
            skLineSegment(sketch, "E34.1.4.4", {"start": v(30, 121.24) * mm, "end": v(20, 138.56) * mm, "construction": true});
            skLineSegment(sketch, "E34.1.4.5", {"start": v(30, 155.88) * mm, "end": v(20, 138.56) * mm, "construction": true});
            skLineSegment(sketch, "E34.1.4.6", {"start": v(40, 138.56) * mm, "end": v(30, 155.88) * mm, "construction": true});
            skLineSegment(sketch, "E34.1.4.7", {"start": v(30, 155.88) * mm, "end": v(50, 155.88) * mm, "construction": true});
            skLineSegment(sketch, "E34.1.4.8", {"start": v(50, 155.88) * mm, "end": v(40, 138.56) * mm, "construction": true});
            skLineSegment(sketch, "E34.1.5.0", {"start": v(30, 155.88) * mm, "end": v(50, 155.88) * mm, "construction": true});
            skLineSegment(sketch, "E34.1.5.1", {"start": v(40, 173.2) * mm, "end": v(30, 155.88) * mm, "construction": true});
            skLineSegment(sketch, "E34.1.5.2", {"start": v(50, 155.88) * mm, "end": v(40, 173.2) * mm, "construction": true});
            skLineSegment(sketch, "E34.1.5.3", {"start": v(20, 173.2) * mm, "end": v(40, 173.2) * mm, "construction": true});
            skLineSegment(sketch, "E34.1.5.4", {"start": v(30, 155.88) * mm, "end": v(20, 173.2) * mm, "construction": true});
            skLineSegment(sketch, "E34.1.5.5", {"start": v(30, 190.53) * mm, "end": v(20, 173.2) * mm, "construction": true});
            skLineSegment(sketch, "E34.1.5.6", {"start": v(40, 173.2) * mm, "end": v(30, 190.53) * mm, "construction": true});
            skLineSegment(sketch, "E34.1.5.7", {"start": v(30, 190.53) * mm, "end": v(50, 190.53) * mm, "construction": true});
            skLineSegment(sketch, "E34.1.5.8", {"start": v(50, 190.53) * mm, "end": v(40, 173.2) * mm, "construction": true});
            skLineSegment(sketch, "E34.1.6.0", {"start": v(30, 190.53) * mm, "end": v(50, 190.53) * mm, "construction": true});
            skLineSegment(sketch, "E34.1.6.1", {"start": v(40, 207.85) * mm, "end": v(30, 190.53) * mm, "construction": true});
            skLineSegment(sketch, "E34.1.6.2", {"start": v(50, 190.53) * mm, "end": v(40, 207.85) * mm, "construction": true});
            skLineSegment(sketch, "E34.1.6.3", {"start": v(20, 207.85) * mm, "end": v(40, 207.85) * mm, "construction": true});
            skLineSegment(sketch, "E34.1.6.4", {"start": v(30, 190.53) * mm, "end": v(20, 207.85) * mm, "construction": true});
            skLineSegment(sketch, "E34.1.6.5", {"start": v(30, 225.17) * mm, "end": v(20, 207.85) * mm, "construction": true});
            skLineSegment(sketch, "E34.1.6.6", {"start": v(40, 207.85) * mm, "end": v(30, 225.17) * mm, "construction": true});
            skLineSegment(sketch, "E34.1.6.7", {"start": v(30, 225.17) * mm, "end": v(50, 225.17) * mm, "construction": true});
            skLineSegment(sketch, "E34.1.6.8", {"start": v(50, 225.17) * mm, "end": v(40, 207.85) * mm, "construction": true});
            skLineSegment(sketch, "E34.2.0.0", {"start": v(50, -17.32) * mm, "end": v(70, -17.32) * mm, "construction": true});
            skLineSegment(sketch, "E34.2.0.1", {"start": v(60, 0) * mm, "end": v(50, -17.32) * mm, "construction": true});
            skLineSegment(sketch, "E34.2.0.2", {"start": v(70, -17.32) * mm, "end": v(60, 0) * mm, "construction": true});
            skLineSegment(sketch, "E34.2.0.3", {"start": v(40, 0) * mm, "end": v(60, 0) * mm, "construction": true});
            skLineSegment(sketch, "E34.2.0.4", {"start": v(50, -17.32) * mm, "end": v(40, 0) * mm, "construction": true});
            skLineSegment(sketch, "E34.2.0.5", {"start": v(50, 17.32) * mm, "end": v(40, 0) * mm, "construction": true});
            skLineSegment(sketch, "E34.2.0.6", {"start": v(60, 0) * mm, "end": v(50, 17.32) * mm, "construction": true});
            skLineSegment(sketch, "E34.2.0.7", {"start": v(50, 17.32) * mm, "end": v(70, 17.32) * mm, "construction": true});
            skLineSegment(sketch, "E34.2.0.8", {"start": v(70, 17.32) * mm, "end": v(60, 0) * mm, "construction": true});
            skLineSegment(sketch, "E34.2.1.0", {"start": v(50, 17.32) * mm, "end": v(70, 17.32) * mm, "construction": true});
            skLineSegment(sketch, "E34.2.1.1", {"start": v(60, 34.64) * mm, "end": v(50, 17.32) * mm, "construction": true});
            skLineSegment(sketch, "E34.2.1.2", {"start": v(70, 17.32) * mm, "end": v(60, 34.64) * mm, "construction": true});
            skLineSegment(sketch, "E34.2.1.3", {"start": v(40, 34.64) * mm, "end": v(60, 34.64) * mm, "construction": true});
            skLineSegment(sketch, "E34.2.1.4", {"start": v(50, 17.32) * mm, "end": v(40, 34.64) * mm, "construction": true});
            skLineSegment(sketch, "E34.2.1.5", {"start": v(50, 51.96) * mm, "end": v(40, 34.64) * mm, "construction": true});
            skLineSegment(sketch, "E34.2.1.6", {"start": v(60, 34.64) * mm, "end": v(50, 51.96) * mm, "construction": true});
            skLineSegment(sketch, "E34.2.1.7", {"start": v(50, 51.96) * mm, "end": v(70, 51.96) * mm, "construction": true});
            skLineSegment(sketch, "E34.2.1.8", {"start": v(70, 51.96) * mm, "end": v(60, 34.64) * mm, "construction": true});
            skLineSegment(sketch, "E34.2.2.0", {"start": v(50, 51.96) * mm, "end": v(70, 51.96) * mm, "construction": true});
            skLineSegment(sketch, "E34.2.2.1", {"start": v(60, 69.28) * mm, "end": v(50, 51.96) * mm, "construction": true});
            skLineSegment(sketch, "E34.2.2.2", {"start": v(70, 51.96) * mm, "end": v(60, 69.28) * mm, "construction": true});
            skLineSegment(sketch, "E34.2.2.3", {"start": v(40, 69.28) * mm, "end": v(60, 69.28) * mm, "construction": true});
            skLineSegment(sketch, "E34.2.2.4", {"start": v(50, 51.96) * mm, "end": v(40, 69.28) * mm, "construction": true});
            skLineSegment(sketch, "E34.2.2.5", {"start": v(50, 86.6) * mm, "end": v(40, 69.28) * mm, "construction": true});
            skLineSegment(sketch, "E34.2.2.6", {"start": v(60, 69.28) * mm, "end": v(50, 86.6) * mm, "construction": true});
            skLineSegment(sketch, "E34.2.2.7", {"start": v(50, 86.6) * mm, "end": v(70, 86.6) * mm, "construction": true});
            skLineSegment(sketch, "E34.2.2.8", {"start": v(70, 86.6) * mm, "end": v(60, 69.28) * mm, "construction": true});
            skLineSegment(sketch, "E34.2.3.0", {"start": v(50, 86.6) * mm, "end": v(70, 86.6) * mm, "construction": true});
            skLineSegment(sketch, "E34.2.3.1", {"start": v(60, 103.92) * mm, "end": v(50, 86.6) * mm, "construction": true});
            skLineSegment(sketch, "E34.2.3.2", {"start": v(70, 86.6) * mm, "end": v(60, 103.92) * mm, "construction": true});
            skLineSegment(sketch, "E34.2.3.3", {"start": v(40, 103.92) * mm, "end": v(60, 103.92) * mm, "construction": true});
            skLineSegment(sketch, "E34.2.3.4", {"start": v(50, 86.6) * mm, "end": v(40, 103.92) * mm, "construction": true});
            skLineSegment(sketch, "E34.2.3.5", {"start": v(50, 121.24) * mm, "end": v(40, 103.92) * mm, "construction": true});
            skLineSegment(sketch, "E34.2.3.6", {"start": v(60, 103.92) * mm, "end": v(50, 121.24) * mm, "construction": true});
            skLineSegment(sketch, "E34.2.3.7", {"start": v(50, 121.24) * mm, "end": v(70, 121.24) * mm, "construction": true});
            skLineSegment(sketch, "E34.2.3.8", {"start": v(70, 121.24) * mm, "end": v(60, 103.92) * mm, "construction": true});
            skLineSegment(sketch, "E34.2.4.0", {"start": v(50, 121.24) * mm, "end": v(70, 121.24) * mm, "construction": true});
            skLineSegment(sketch, "E34.2.4.1", {"start": v(60, 138.56) * mm, "end": v(50, 121.24) * mm, "construction": true});
            skLineSegment(sketch, "E34.2.4.2", {"start": v(70, 121.24) * mm, "end": v(60, 138.56) * mm, "construction": true});
            skLineSegment(sketch, "E34.2.4.3", {"start": v(40, 138.56) * mm, "end": v(60, 138.56) * mm, "construction": true});
            skLineSegment(sketch, "E34.2.4.4", {"start": v(50, 121.24) * mm, "end": v(40, 138.56) * mm, "construction": true});
            skLineSegment(sketch, "E34.2.4.5", {"start": v(50, 155.88) * mm, "end": v(40, 138.56) * mm, "construction": true});
            skLineSegment(sketch, "E34.2.4.6", {"start": v(60, 138.56) * mm, "end": v(50, 155.88) * mm, "construction": true});
            skLineSegment(sketch, "E34.2.4.7", {"start": v(50, 155.88) * mm, "end": v(70, 155.88) * mm, "construction": true});
            skLineSegment(sketch, "E34.2.4.8", {"start": v(70, 155.88) * mm, "end": v(60, 138.56) * mm, "construction": true});
            skLineSegment(sketch, "E34.2.5.0", {"start": v(50, 155.88) * mm, "end": v(70, 155.88) * mm, "construction": true});
            skLineSegment(sketch, "E34.2.5.1", {"start": v(60, 173.2) * mm, "end": v(50, 155.88) * mm, "construction": true});
            skLineSegment(sketch, "E34.2.5.2", {"start": v(70, 155.88) * mm, "end": v(60, 173.2) * mm, "construction": true});
            skLineSegment(sketch, "E34.2.5.3", {"start": v(40, 173.2) * mm, "end": v(60, 173.2) * mm, "construction": true});
            skLineSegment(sketch, "E34.2.5.4", {"start": v(50, 155.88) * mm, "end": v(40, 173.2) * mm, "construction": true});
            skLineSegment(sketch, "E34.2.5.5", {"start": v(50, 190.53) * mm, "end": v(40, 173.2) * mm, "construction": true});
            skLineSegment(sketch, "E34.2.5.6", {"start": v(60, 173.2) * mm, "end": v(50, 190.53) * mm, "construction": true});
            skLineSegment(sketch, "E34.2.5.7", {"start": v(50, 190.53) * mm, "end": v(70, 190.53) * mm, "construction": true});
            skLineSegment(sketch, "E34.2.5.8", {"start": v(70, 190.53) * mm, "end": v(60, 173.2) * mm, "construction": true});
            skLineSegment(sketch, "E34.2.6.0", {"start": v(50, 190.53) * mm, "end": v(70, 190.53) * mm, "construction": true});
            skLineSegment(sketch, "E34.2.6.1", {"start": v(60, 207.85) * mm, "end": v(50, 190.53) * mm, "construction": true});
            skLineSegment(sketch, "E34.2.6.2", {"start": v(70, 190.53) * mm, "end": v(60, 207.85) * mm, "construction": true});
            skLineSegment(sketch, "E34.2.6.3", {"start": v(40, 207.85) * mm, "end": v(60, 207.85) * mm, "construction": true});
            skLineSegment(sketch, "E34.2.6.4", {"start": v(50, 190.53) * mm, "end": v(40, 207.85) * mm, "construction": true});
            skLineSegment(sketch, "E34.2.6.5", {"start": v(50, 225.17) * mm, "end": v(40, 207.85) * mm, "construction": true});
            skLineSegment(sketch, "E34.2.6.6", {"start": v(60, 207.85) * mm, "end": v(50, 225.17) * mm, "construction": true});
            skLineSegment(sketch, "E34.2.6.7", {"start": v(50, 225.17) * mm, "end": v(70, 225.17) * mm, "construction": true});
            skLineSegment(sketch, "E34.2.6.8", {"start": v(70, 225.17) * mm, "end": v(60, 207.85) * mm, "construction": true});
            skLineSegment(sketch, "E34.3.0.0", {"start": v(70, -17.32) * mm, "end": v(90, -17.32) * mm, "construction": true});
            skLineSegment(sketch, "E34.3.0.1", {"start": v(80, 0) * mm, "end": v(70, -17.32) * mm, "construction": true});
            skLineSegment(sketch, "E34.3.0.2", {"start": v(90, -17.32) * mm, "end": v(80, 0) * mm, "construction": true});
            skLineSegment(sketch, "E34.3.0.3", {"start": v(60, 0) * mm, "end": v(80, 0) * mm, "construction": true});
            skLineSegment(sketch, "E34.3.0.4", {"start": v(70, -17.32) * mm, "end": v(60, 0) * mm, "construction": true});
            skLineSegment(sketch, "E34.3.0.5", {"start": v(70, 17.32) * mm, "end": v(60, 0) * mm, "construction": true});
            skLineSegment(sketch, "E34.3.0.6", {"start": v(80, 0) * mm, "end": v(70, 17.32) * mm, "construction": true});
            skLineSegment(sketch, "E34.3.0.7", {"start": v(70, 17.32) * mm, "end": v(90, 17.32) * mm, "construction": true});
            skLineSegment(sketch, "E34.3.0.8", {"start": v(90, 17.32) * mm, "end": v(80, 0) * mm, "construction": true});
            skLineSegment(sketch, "E34.3.1.0", {"start": v(70, 17.32) * mm, "end": v(90, 17.32) * mm, "construction": true});
            skLineSegment(sketch, "E34.3.1.1", {"start": v(80, 34.64) * mm, "end": v(70, 17.32) * mm, "construction": true});
            skLineSegment(sketch, "E34.3.1.2", {"start": v(90, 17.32) * mm, "end": v(80, 34.64) * mm, "construction": true});
            skLineSegment(sketch, "E34.3.1.3", {"start": v(60, 34.64) * mm, "end": v(80, 34.64) * mm, "construction": true});
            skLineSegment(sketch, "E34.3.1.4", {"start": v(70, 17.32) * mm, "end": v(60, 34.64) * mm, "construction": true});
            skLineSegment(sketch, "E34.3.1.5", {"start": v(70, 51.96) * mm, "end": v(60, 34.64) * mm, "construction": true});
            skLineSegment(sketch, "E34.3.1.6", {"start": v(80, 34.64) * mm, "end": v(70, 51.96) * mm, "construction": true});
            skLineSegment(sketch, "E34.3.1.7", {"start": v(70, 51.96) * mm, "end": v(90, 51.96) * mm, "construction": true});
            skLineSegment(sketch, "E34.3.1.8", {"start": v(90, 51.96) * mm, "end": v(80, 34.64) * mm, "construction": true});
            skLineSegment(sketch, "E34.3.2.0", {"start": v(70, 51.96) * mm, "end": v(90, 51.96) * mm, "construction": true});
            skLineSegment(sketch, "E34.3.2.1", {"start": v(80, 69.28) * mm, "end": v(70, 51.96) * mm, "construction": true});
            skLineSegment(sketch, "E34.3.2.2", {"start": v(90, 51.96) * mm, "end": v(80, 69.28) * mm, "construction": true});
            skLineSegment(sketch, "E34.3.2.3", {"start": v(60, 69.28) * mm, "end": v(80, 69.28) * mm, "construction": true});
            skLineSegment(sketch, "E34.3.2.4", {"start": v(70, 51.96) * mm, "end": v(60, 69.28) * mm, "construction": true});
            skLineSegment(sketch, "E34.3.2.5", {"start": v(70, 86.6) * mm, "end": v(60, 69.28) * mm, "construction": true});
            skLineSegment(sketch, "E34.3.2.6", {"start": v(80, 69.28) * mm, "end": v(70, 86.6) * mm, "construction": true});
            skLineSegment(sketch, "E34.3.2.7", {"start": v(70, 86.6) * mm, "end": v(90, 86.6) * mm, "construction": true});
            skLineSegment(sketch, "E34.3.2.8", {"start": v(90, 86.6) * mm, "end": v(80, 69.28) * mm, "construction": true});
            skLineSegment(sketch, "E34.3.3.0", {"start": v(70, 86.6) * mm, "end": v(90, 86.6) * mm, "construction": true});
            skLineSegment(sketch, "E34.3.3.1", {"start": v(80, 103.92) * mm, "end": v(70, 86.6) * mm, "construction": true});
            skLineSegment(sketch, "E34.3.3.2", {"start": v(90, 86.6) * mm, "end": v(80, 103.92) * mm, "construction": true});
            skLineSegment(sketch, "E34.3.3.3", {"start": v(60, 103.92) * mm, "end": v(80, 103.92) * mm, "construction": true});
            skLineSegment(sketch, "E34.3.3.4", {"start": v(70, 86.6) * mm, "end": v(60, 103.92) * mm, "construction": true});
            skLineSegment(sketch, "E34.3.3.5", {"start": v(70, 121.24) * mm, "end": v(60, 103.92) * mm, "construction": true});
            skLineSegment(sketch, "E34.3.3.6", {"start": v(80, 103.92) * mm, "end": v(70, 121.24) * mm, "construction": true});
            skLineSegment(sketch, "E34.3.3.7", {"start": v(70, 121.24) * mm, "end": v(90, 121.24) * mm, "construction": true});
            skLineSegment(sketch, "E34.3.3.8", {"start": v(90, 121.24) * mm, "end": v(80, 103.92) * mm, "construction": true});
            skLineSegment(sketch, "E34.3.4.0", {"start": v(70, 121.24) * mm, "end": v(90, 121.24) * mm, "construction": true});
            skLineSegment(sketch, "E34.3.4.1", {"start": v(80, 138.56) * mm, "end": v(70, 121.24) * mm, "construction": true});
            skLineSegment(sketch, "E34.3.4.2", {"start": v(90, 121.24) * mm, "end": v(80, 138.56) * mm, "construction": true});
            skLineSegment(sketch, "E34.3.4.3", {"start": v(60, 138.56) * mm, "end": v(80, 138.56) * mm, "construction": true});
            skLineSegment(sketch, "E34.3.4.4", {"start": v(70, 121.24) * mm, "end": v(60, 138.56) * mm, "construction": true});
            skLineSegment(sketch, "E34.3.4.5", {"start": v(70, 155.88) * mm, "end": v(60, 138.56) * mm, "construction": true});
            skLineSegment(sketch, "E34.3.4.6", {"start": v(80, 138.56) * mm, "end": v(70, 155.88) * mm, "construction": true});
            skLineSegment(sketch, "E34.3.4.7", {"start": v(70, 155.88) * mm, "end": v(90, 155.88) * mm, "construction": true});
            skLineSegment(sketch, "E34.3.4.8", {"start": v(90, 155.88) * mm, "end": v(80, 138.56) * mm, "construction": true});
            skLineSegment(sketch, "E34.3.5.0", {"start": v(70, 155.88) * mm, "end": v(90, 155.88) * mm, "construction": true});
            skLineSegment(sketch, "E34.3.5.1", {"start": v(80, 173.2) * mm, "end": v(70, 155.88) * mm, "construction": true});
            skLineSegment(sketch, "E34.3.5.2", {"start": v(90, 155.88) * mm, "end": v(80, 173.2) * mm, "construction": true});
            skLineSegment(sketch, "E34.3.5.3", {"start": v(60, 173.2) * mm, "end": v(80, 173.2) * mm, "construction": true});
            skLineSegment(sketch, "E34.3.5.4", {"start": v(70, 155.88) * mm, "end": v(60, 173.2) * mm, "construction": true});
            skLineSegment(sketch, "E34.3.5.5", {"start": v(70, 190.53) * mm, "end": v(60, 173.2) * mm, "construction": true});
            skLineSegment(sketch, "E34.3.5.6", {"start": v(80, 173.2) * mm, "end": v(70, 190.53) * mm, "construction": true});
            skLineSegment(sketch, "E34.3.5.7", {"start": v(70, 190.53) * mm, "end": v(90, 190.53) * mm, "construction": true});
            skLineSegment(sketch, "E34.3.5.8", {"start": v(90, 190.53) * mm, "end": v(80, 173.2) * mm, "construction": true});
            skLineSegment(sketch, "E34.3.6.0", {"start": v(70, 190.53) * mm, "end": v(90, 190.53) * mm, "construction": true});
            skLineSegment(sketch, "E34.3.6.1", {"start": v(80, 207.85) * mm, "end": v(70, 190.53) * mm, "construction": true});
            skLineSegment(sketch, "E34.3.6.2", {"start": v(90, 190.53) * mm, "end": v(80, 207.85) * mm, "construction": true});
            skLineSegment(sketch, "E34.3.6.3", {"start": v(60, 207.85) * mm, "end": v(80, 207.85) * mm, "construction": true});
            skLineSegment(sketch, "E34.3.6.4", {"start": v(70, 190.53) * mm, "end": v(60, 207.85) * mm, "construction": true});
            skLineSegment(sketch, "E34.3.6.5", {"start": v(70, 225.17) * mm, "end": v(60, 207.85) * mm, "construction": true});
            skLineSegment(sketch, "E34.3.6.6", {"start": v(80, 207.85) * mm, "end": v(70, 225.17) * mm, "construction": true});
            skLineSegment(sketch, "E34.3.6.7", {"start": v(70, 225.17) * mm, "end": v(90, 225.17) * mm, "construction": true});
            skLineSegment(sketch, "E34.3.6.8", {"start": v(90, 225.17) * mm, "end": v(80, 207.85) * mm, "construction": true});
            skLineSegment(sketch, "E34.4.0.0", {"start": v(90, -17.32) * mm, "end": v(110, -17.32) * mm, "construction": true});
            skLineSegment(sketch, "E34.4.0.1", {"start": v(100, 0) * mm, "end": v(90, -17.32) * mm, "construction": true});
            skLineSegment(sketch, "E34.4.0.2", {"start": v(110, -17.32) * mm, "end": v(100, 0) * mm, "construction": true});
            skLineSegment(sketch, "E34.4.0.3", {"start": v(80, 0) * mm, "end": v(100, 0) * mm, "construction": true});
            skLineSegment(sketch, "E34.4.0.4", {"start": v(90, -17.32) * mm, "end": v(80, 0) * mm, "construction": true});
            skLineSegment(sketch, "E34.4.0.5", {"start": v(90, 17.32) * mm, "end": v(80, 0) * mm, "construction": true});
            skLineSegment(sketch, "E34.4.0.6", {"start": v(100, 0) * mm, "end": v(90, 17.32) * mm, "construction": true});
            skLineSegment(sketch, "E34.4.0.7", {"start": v(90, 17.32) * mm, "end": v(110, 17.32) * mm, "construction": true});
            skLineSegment(sketch, "E34.4.0.8", {"start": v(110, 17.32) * mm, "end": v(100, 0) * mm, "construction": true});
            skLineSegment(sketch, "E34.4.1.0", {"start": v(90, 17.32) * mm, "end": v(110, 17.32) * mm, "construction": true});
            skLineSegment(sketch, "E34.4.1.1", {"start": v(100, 34.64) * mm, "end": v(90, 17.32) * mm, "construction": true});
            skLineSegment(sketch, "E34.4.1.2", {"start": v(110, 17.32) * mm, "end": v(100, 34.64) * mm, "construction": true});
            skLineSegment(sketch, "E34.4.1.3", {"start": v(80, 34.64) * mm, "end": v(100, 34.64) * mm, "construction": true});
            skLineSegment(sketch, "E34.4.1.4", {"start": v(90, 17.32) * mm, "end": v(80, 34.64) * mm, "construction": true});
            skLineSegment(sketch, "E34.4.1.5", {"start": v(90, 51.96) * mm, "end": v(80, 34.64) * mm, "construction": true});
            skLineSegment(sketch, "E34.4.1.6", {"start": v(100, 34.64) * mm, "end": v(90, 51.96) * mm, "construction": true});
            skLineSegment(sketch, "E34.4.1.7", {"start": v(90, 51.96) * mm, "end": v(110, 51.96) * mm, "construction": true});
            skLineSegment(sketch, "E34.4.1.8", {"start": v(110, 51.96) * mm, "end": v(100, 34.64) * mm, "construction": true});
            skLineSegment(sketch, "E34.4.2.0", {"start": v(90, 51.96) * mm, "end": v(110, 51.96) * mm, "construction": true});
            skLineSegment(sketch, "E34.4.2.1", {"start": v(100, 69.28) * mm, "end": v(90, 51.96) * mm, "construction": true});
            skLineSegment(sketch, "E34.4.2.2", {"start": v(110, 51.96) * mm, "end": v(100, 69.28) * mm, "construction": true});
            skLineSegment(sketch, "E34.4.2.3", {"start": v(80, 69.28) * mm, "end": v(100, 69.28) * mm, "construction": true});
            skLineSegment(sketch, "E34.4.2.4", {"start": v(90, 51.96) * mm, "end": v(80, 69.28) * mm, "construction": true});
            skLineSegment(sketch, "E34.4.2.5", {"start": v(90, 86.6) * mm, "end": v(80, 69.28) * mm, "construction": true});
            skLineSegment(sketch, "E34.4.2.6", {"start": v(100, 69.28) * mm, "end": v(90, 86.6) * mm, "construction": true});
            skLineSegment(sketch, "E34.4.2.7", {"start": v(90, 86.6) * mm, "end": v(110, 86.6) * mm, "construction": true});
            skLineSegment(sketch, "E34.4.2.8", {"start": v(110, 86.6) * mm, "end": v(100, 69.28) * mm, "construction": true});
            skLineSegment(sketch, "E34.4.3.0", {"start": v(90, 86.6) * mm, "end": v(110, 86.6) * mm, "construction": true});
            skLineSegment(sketch, "E34.4.3.1", {"start": v(100, 103.92) * mm, "end": v(90, 86.6) * mm, "construction": true});
            skLineSegment(sketch, "E34.4.3.2", {"start": v(110, 86.6) * mm, "end": v(100, 103.92) * mm, "construction": true});
            skLineSegment(sketch, "E34.4.3.3", {"start": v(80, 103.92) * mm, "end": v(100, 103.92) * mm, "construction": true});
            skLineSegment(sketch, "E34.4.3.4", {"start": v(90, 86.6) * mm, "end": v(80, 103.92) * mm, "construction": true});
            skLineSegment(sketch, "E34.4.3.5", {"start": v(90, 121.24) * mm, "end": v(80, 103.92) * mm, "construction": true});
            skLineSegment(sketch, "E34.4.3.6", {"start": v(100, 103.92) * mm, "end": v(90, 121.24) * mm, "construction": true});
            skLineSegment(sketch, "E34.4.3.7", {"start": v(90, 121.24) * mm, "end": v(110, 121.24) * mm, "construction": true});
            skLineSegment(sketch, "E34.4.3.8", {"start": v(110, 121.24) * mm, "end": v(100, 103.92) * mm, "construction": true});
            skLineSegment(sketch, "E34.4.4.0", {"start": v(90, 121.24) * mm, "end": v(110, 121.24) * mm, "construction": true});
            skLineSegment(sketch, "E34.4.4.1", {"start": v(100, 138.56) * mm, "end": v(90, 121.24) * mm, "construction": true});
            skLineSegment(sketch, "E34.4.4.2", {"start": v(110, 121.24) * mm, "end": v(100, 138.56) * mm, "construction": true});
            skLineSegment(sketch, "E34.4.4.3", {"start": v(80, 138.56) * mm, "end": v(100, 138.56) * mm, "construction": true});
            skLineSegment(sketch, "E34.4.4.4", {"start": v(90, 121.24) * mm, "end": v(80, 138.56) * mm, "construction": true});
            skLineSegment(sketch, "E34.4.4.5", {"start": v(90, 155.88) * mm, "end": v(80, 138.56) * mm, "construction": true});
            skLineSegment(sketch, "E34.4.4.6", {"start": v(100, 138.56) * mm, "end": v(90, 155.88) * mm, "construction": true});
            skLineSegment(sketch, "E34.4.4.7", {"start": v(90, 155.88) * mm, "end": v(110, 155.88) * mm, "construction": true});
            skLineSegment(sketch, "E34.4.4.8", {"start": v(110, 155.88) * mm, "end": v(100, 138.56) * mm, "construction": true});
            skLineSegment(sketch, "E34.4.5.0", {"start": v(90, 155.88) * mm, "end": v(110, 155.88) * mm, "construction": true});
            skLineSegment(sketch, "E34.4.5.1", {"start": v(100, 173.2) * mm, "end": v(90, 155.88) * mm, "construction": true});
            skLineSegment(sketch, "E34.4.5.2", {"start": v(110, 155.88) * mm, "end": v(100, 173.2) * mm, "construction": true});
            skLineSegment(sketch, "E34.4.5.3", {"start": v(80, 173.2) * mm, "end": v(100, 173.2) * mm, "construction": true});
            skLineSegment(sketch, "E34.4.5.4", {"start": v(90, 155.88) * mm, "end": v(80, 173.2) * mm, "construction": true});
            skLineSegment(sketch, "E34.4.5.5", {"start": v(90, 190.53) * mm, "end": v(80, 173.2) * mm, "construction": true});
            skLineSegment(sketch, "E34.4.5.6", {"start": v(100, 173.2) * mm, "end": v(90, 190.53) * mm, "construction": true});
            skLineSegment(sketch, "E34.4.5.7", {"start": v(90, 190.53) * mm, "end": v(110, 190.53) * mm, "construction": true});
            skLineSegment(sketch, "E34.4.5.8", {"start": v(110, 190.53) * mm, "end": v(100, 173.2) * mm, "construction": true});
            skLineSegment(sketch, "E34.4.6.0", {"start": v(90, 190.53) * mm, "end": v(110, 190.53) * mm, "construction": true});
            skLineSegment(sketch, "E34.4.6.1", {"start": v(100, 207.85) * mm, "end": v(90, 190.53) * mm, "construction": true});
            skLineSegment(sketch, "E34.4.6.2", {"start": v(110, 190.53) * mm, "end": v(100, 207.85) * mm, "construction": true});
            skLineSegment(sketch, "E34.4.6.3", {"start": v(80, 207.85) * mm, "end": v(100, 207.85) * mm, "construction": true});
            skLineSegment(sketch, "E34.4.6.4", {"start": v(90, 190.53) * mm, "end": v(80, 207.85) * mm, "construction": true});
            skLineSegment(sketch, "E34.4.6.5", {"start": v(90, 225.17) * mm, "end": v(80, 207.85) * mm, "construction": true});
            skLineSegment(sketch, "E34.4.6.6", {"start": v(100, 207.85) * mm, "end": v(90, 225.17) * mm, "construction": true});
            skLineSegment(sketch, "E34.4.6.7", {"start": v(90, 225.17) * mm, "end": v(110, 225.17) * mm, "construction": true});
            skLineSegment(sketch, "E34.4.6.8", {"start": v(110, 225.17) * mm, "end": v(100, 207.85) * mm, "construction": true});
            skLineSegment(sketch, "E34.5.0.0", {"start": v(110, -17.32) * mm, "end": v(130, -17.32) * mm, "construction": true});
            skLineSegment(sketch, "E34.5.0.1", {"start": v(120, 0) * mm, "end": v(110, -17.32) * mm, "construction": true});
            skLineSegment(sketch, "E34.5.0.2", {"start": v(130, -17.32) * mm, "end": v(120, 0) * mm, "construction": true});
            skLineSegment(sketch, "E34.5.0.3", {"start": v(100, 0) * mm, "end": v(120, 0) * mm, "construction": true});
            skLineSegment(sketch, "E34.5.0.4", {"start": v(110, -17.32) * mm, "end": v(100, 0) * mm, "construction": true});
            skLineSegment(sketch, "E34.5.0.5", {"start": v(110, 17.32) * mm, "end": v(100, 0) * mm, "construction": true});
            skLineSegment(sketch, "E34.5.0.6", {"start": v(120, 0) * mm, "end": v(110, 17.32) * mm, "construction": true});
            skLineSegment(sketch, "E34.5.0.7", {"start": v(110, 17.32) * mm, "end": v(130, 17.32) * mm, "construction": true});
            skLineSegment(sketch, "E34.5.0.8", {"start": v(130, 17.32) * mm, "end": v(120, 0) * mm, "construction": true});
            skLineSegment(sketch, "E34.5.1.0", {"start": v(110, 17.32) * mm, "end": v(130, 17.32) * mm, "construction": true});
            skLineSegment(sketch, "E34.5.1.1", {"start": v(120, 34.64) * mm, "end": v(110, 17.32) * mm, "construction": true});
            skLineSegment(sketch, "E34.5.1.2", {"start": v(130, 17.32) * mm, "end": v(120, 34.64) * mm, "construction": true});
            skLineSegment(sketch, "E34.5.1.3", {"start": v(100, 34.64) * mm, "end": v(120, 34.64) * mm, "construction": true});
            skLineSegment(sketch, "E34.5.1.4", {"start": v(110, 17.32) * mm, "end": v(100, 34.64) * mm, "construction": true});
            skLineSegment(sketch, "E34.5.1.5", {"start": v(110, 51.96) * mm, "end": v(100, 34.64) * mm, "construction": true});
            skLineSegment(sketch, "E34.5.1.6", {"start": v(120, 34.64) * mm, "end": v(110, 51.96) * mm, "construction": true});
            skLineSegment(sketch, "E34.5.1.7", {"start": v(110, 51.96) * mm, "end": v(130, 51.96) * mm, "construction": true});
            skLineSegment(sketch, "E34.5.1.8", {"start": v(130, 51.96) * mm, "end": v(120, 34.64) * mm, "construction": true});
            skLineSegment(sketch, "E34.5.2.0", {"start": v(110, 51.96) * mm, "end": v(130, 51.96) * mm, "construction": true});
            skLineSegment(sketch, "E34.5.2.1", {"start": v(120, 69.28) * mm, "end": v(110, 51.96) * mm, "construction": true});
            skLineSegment(sketch, "E34.5.2.2", {"start": v(130, 51.96) * mm, "end": v(120, 69.28) * mm, "construction": true});
            skLineSegment(sketch, "E34.5.2.3", {"start": v(100, 69.28) * mm, "end": v(120, 69.28) * mm, "construction": true});
            skLineSegment(sketch, "E34.5.2.4", {"start": v(110, 51.96) * mm, "end": v(100, 69.28) * mm, "construction": true});
            skLineSegment(sketch, "E34.5.2.5", {"start": v(110, 86.6) * mm, "end": v(100, 69.28) * mm, "construction": true});
            skLineSegment(sketch, "E34.5.2.6", {"start": v(120, 69.28) * mm, "end": v(110, 86.6) * mm, "construction": true});
            skLineSegment(sketch, "E34.5.2.7", {"start": v(110, 86.6) * mm, "end": v(130, 86.6) * mm, "construction": true});
            skLineSegment(sketch, "E34.5.2.8", {"start": v(130, 86.6) * mm, "end": v(120, 69.28) * mm, "construction": true});
            skLineSegment(sketch, "E34.5.3.0", {"start": v(110, 86.6) * mm, "end": v(130, 86.6) * mm, "construction": true});
            skLineSegment(sketch, "E34.5.3.1", {"start": v(120, 103.92) * mm, "end": v(110, 86.6) * mm, "construction": true});
            skLineSegment(sketch, "E34.5.3.2", {"start": v(130, 86.6) * mm, "end": v(120, 103.92) * mm, "construction": true});
            skLineSegment(sketch, "E34.5.3.3", {"start": v(100, 103.92) * mm, "end": v(120, 103.92) * mm, "construction": true});
            skLineSegment(sketch, "E34.5.3.4", {"start": v(110, 86.6) * mm, "end": v(100, 103.92) * mm, "construction": true});
            skLineSegment(sketch, "E34.5.3.5", {"start": v(110, 121.24) * mm, "end": v(100, 103.92) * mm, "construction": true});
            skLineSegment(sketch, "E34.5.3.6", {"start": v(120, 103.92) * mm, "end": v(110, 121.24) * mm, "construction": true});
            skLineSegment(sketch, "E34.5.3.7", {"start": v(110, 121.24) * mm, "end": v(130, 121.24) * mm, "construction": true});
            skLineSegment(sketch, "E34.5.3.8", {"start": v(130, 121.24) * mm, "end": v(120, 103.92) * mm, "construction": true});
            skLineSegment(sketch, "E34.5.4.0", {"start": v(110, 121.24) * mm, "end": v(130, 121.24) * mm, "construction": true});
            skLineSegment(sketch, "E34.5.4.1", {"start": v(120, 138.56) * mm, "end": v(110, 121.24) * mm, "construction": true});
            skLineSegment(sketch, "E34.5.4.2", {"start": v(130, 121.24) * mm, "end": v(120, 138.56) * mm, "construction": true});
            skLineSegment(sketch, "E34.5.4.3", {"start": v(100, 138.56) * mm, "end": v(120, 138.56) * mm, "construction": true});
            skLineSegment(sketch, "E34.5.4.4", {"start": v(110, 121.24) * mm, "end": v(100, 138.56) * mm, "construction": true});
            skLineSegment(sketch, "E34.5.4.5", {"start": v(110, 155.88) * mm, "end": v(100, 138.56) * mm, "construction": true});
            skLineSegment(sketch, "E34.5.4.6", {"start": v(120, 138.56) * mm, "end": v(110, 155.88) * mm, "construction": true});
            skLineSegment(sketch, "E34.5.4.7", {"start": v(110, 155.88) * mm, "end": v(130, 155.88) * mm, "construction": true});
            skLineSegment(sketch, "E34.5.4.8", {"start": v(130, 155.88) * mm, "end": v(120, 138.56) * mm, "construction": true});
            skLineSegment(sketch, "E34.5.5.0", {"start": v(110, 155.88) * mm, "end": v(130, 155.88) * mm, "construction": true});
            skLineSegment(sketch, "E34.5.5.1", {"start": v(120, 173.2) * mm, "end": v(110, 155.88) * mm, "construction": true});
            skLineSegment(sketch, "E34.5.5.2", {"start": v(130, 155.88) * mm, "end": v(120, 173.2) * mm, "construction": true});
            skLineSegment(sketch, "E34.5.5.3", {"start": v(100, 173.2) * mm, "end": v(120, 173.2) * mm, "construction": true});
            skLineSegment(sketch, "E34.5.5.4", {"start": v(110, 155.88) * mm, "end": v(100, 173.2) * mm, "construction": true});
            skLineSegment(sketch, "E34.5.5.5", {"start": v(110, 190.53) * mm, "end": v(100, 173.2) * mm, "construction": true});
            skLineSegment(sketch, "E34.5.5.6", {"start": v(120, 173.2) * mm, "end": v(110, 190.53) * mm, "construction": true});
            skLineSegment(sketch, "E34.5.5.7", {"start": v(110, 190.53) * mm, "end": v(130, 190.53) * mm, "construction": true});
            skLineSegment(sketch, "E34.5.5.8", {"start": v(130, 190.53) * mm, "end": v(120, 173.2) * mm, "construction": true});
            skLineSegment(sketch, "E34.5.6.0", {"start": v(110, 190.53) * mm, "end": v(130, 190.53) * mm, "construction": true});
            skLineSegment(sketch, "E34.5.6.1", {"start": v(120, 207.85) * mm, "end": v(110, 190.53) * mm, "construction": true});
            skLineSegment(sketch, "E34.5.6.2", {"start": v(130, 190.53) * mm, "end": v(120, 207.85) * mm, "construction": true});
            skLineSegment(sketch, "E34.5.6.3", {"start": v(100, 207.85) * mm, "end": v(120, 207.85) * mm, "construction": true});
            skLineSegment(sketch, "E34.5.6.4", {"start": v(110, 190.53) * mm, "end": v(100, 207.85) * mm, "construction": true});
            skLineSegment(sketch, "E34.5.6.5", {"start": v(110, 225.17) * mm, "end": v(100, 207.85) * mm, "construction": true});
            skLineSegment(sketch, "E34.5.6.6", {"start": v(120, 207.85) * mm, "end": v(110, 225.17) * mm, "construction": true});
            skLineSegment(sketch, "E34.5.6.7", {"start": v(110, 225.17) * mm, "end": v(130, 225.17) * mm, "construction": true});
            skLineSegment(sketch, "E34.5.6.8", {"start": v(130, 225.17) * mm, "end": v(120, 207.85) * mm, "construction": true});
            skLineSegment(sketch, "E34.6.0.0", {"start": v(130, -17.32) * mm, "end": v(150, -17.32) * mm, "construction": true});
            skLineSegment(sketch, "E34.6.0.1", {"start": v(140, 0) * mm, "end": v(130, -17.32) * mm, "construction": true});
            skLineSegment(sketch, "E34.6.0.2", {"start": v(150, -17.32) * mm, "end": v(140, 0) * mm, "construction": true});
            skLineSegment(sketch, "E34.6.0.3", {"start": v(120, 0) * mm, "end": v(140, 0) * mm, "construction": true});
            skLineSegment(sketch, "E34.6.0.4", {"start": v(130, -17.32) * mm, "end": v(120, 0) * mm, "construction": true});
            skLineSegment(sketch, "E34.6.0.5", {"start": v(130, 17.32) * mm, "end": v(120, 0) * mm, "construction": true});
            skLineSegment(sketch, "E34.6.0.6", {"start": v(140, 0) * mm, "end": v(130, 17.32) * mm, "construction": true});
            skLineSegment(sketch, "E34.6.0.7", {"start": v(130, 17.32) * mm, "end": v(150, 17.32) * mm, "construction": true});
            skLineSegment(sketch, "E34.6.0.8", {"start": v(150, 17.32) * mm, "end": v(140, 0) * mm, "construction": true});
            skLineSegment(sketch, "E34.6.1.0", {"start": v(130, 17.32) * mm, "end": v(150, 17.32) * mm, "construction": true});
            skLineSegment(sketch, "E34.6.1.1", {"start": v(140, 34.64) * mm, "end": v(130, 17.32) * mm, "construction": true});
            skLineSegment(sketch, "E34.6.1.2", {"start": v(150, 17.32) * mm, "end": v(140, 34.64) * mm, "construction": true});
            skLineSegment(sketch, "E34.6.1.3", {"start": v(120, 34.64) * mm, "end": v(140, 34.64) * mm, "construction": true});
            skLineSegment(sketch, "E34.6.1.4", {"start": v(130, 17.32) * mm, "end": v(120, 34.64) * mm, "construction": true});
            skLineSegment(sketch, "E34.6.1.5", {"start": v(130, 51.96) * mm, "end": v(120, 34.64) * mm, "construction": true});
            skLineSegment(sketch, "E34.6.1.6", {"start": v(140, 34.64) * mm, "end": v(130, 51.96) * mm, "construction": true});
            skLineSegment(sketch, "E34.6.1.7", {"start": v(130, 51.96) * mm, "end": v(150, 51.96) * mm, "construction": true});
            skLineSegment(sketch, "E34.6.1.8", {"start": v(150, 51.96) * mm, "end": v(140, 34.64) * mm, "construction": true});
            skLineSegment(sketch, "E34.6.2.0", {"start": v(130, 51.96) * mm, "end": v(150, 51.96) * mm, "construction": true});
            skLineSegment(sketch, "E34.6.2.1", {"start": v(140, 69.28) * mm, "end": v(130, 51.96) * mm, "construction": true});
            skLineSegment(sketch, "E34.6.2.2", {"start": v(150, 51.96) * mm, "end": v(140, 69.28) * mm, "construction": true});
            skLineSegment(sketch, "E34.6.2.3", {"start": v(120, 69.28) * mm, "end": v(140, 69.28) * mm, "construction": true});
            skLineSegment(sketch, "E34.6.2.4", {"start": v(130, 51.96) * mm, "end": v(120, 69.28) * mm, "construction": true});
            skLineSegment(sketch, "E34.6.2.5", {"start": v(130, 86.6) * mm, "end": v(120, 69.28) * mm, "construction": true});
            skLineSegment(sketch, "E34.6.2.6", {"start": v(140, 69.28) * mm, "end": v(130, 86.6) * mm, "construction": true});
            skLineSegment(sketch, "E34.6.2.7", {"start": v(130, 86.6) * mm, "end": v(150, 86.6) * mm, "construction": true});
            skLineSegment(sketch, "E34.6.2.8", {"start": v(150, 86.6) * mm, "end": v(140, 69.28) * mm, "construction": true});
            skLineSegment(sketch, "E34.6.3.0", {"start": v(130, 86.6) * mm, "end": v(150, 86.6) * mm, "construction": true});
            skLineSegment(sketch, "E34.6.3.1", {"start": v(140, 103.92) * mm, "end": v(130, 86.6) * mm, "construction": true});
            skLineSegment(sketch, "E34.6.3.2", {"start": v(150, 86.6) * mm, "end": v(140, 103.92) * mm, "construction": true});
            skLineSegment(sketch, "E34.6.3.3", {"start": v(120, 103.92) * mm, "end": v(140, 103.92) * mm, "construction": true});
            skLineSegment(sketch, "E34.6.3.4", {"start": v(130, 86.6) * mm, "end": v(120, 103.92) * mm, "construction": true});
            skLineSegment(sketch, "E34.6.3.5", {"start": v(130, 121.24) * mm, "end": v(120, 103.92) * mm, "construction": true});
            skLineSegment(sketch, "E34.6.3.6", {"start": v(140, 103.92) * mm, "end": v(130, 121.24) * mm, "construction": true});
            skLineSegment(sketch, "E34.6.3.7", {"start": v(130, 121.24) * mm, "end": v(150, 121.24) * mm, "construction": true});
            skLineSegment(sketch, "E34.6.3.8", {"start": v(150, 121.24) * mm, "end": v(140, 103.92) * mm, "construction": true});
            skLineSegment(sketch, "E34.6.4.0", {"start": v(130, 121.24) * mm, "end": v(150, 121.24) * mm, "construction": true});
            skLineSegment(sketch, "E34.6.4.1", {"start": v(140, 138.56) * mm, "end": v(130, 121.24) * mm, "construction": true});
            skLineSegment(sketch, "E34.6.4.2", {"start": v(150, 121.24) * mm, "end": v(140, 138.56) * mm, "construction": true});
            skLineSegment(sketch, "E34.6.4.3", {"start": v(120, 138.56) * mm, "end": v(140, 138.56) * mm, "construction": true});
            skLineSegment(sketch, "E34.6.4.4", {"start": v(130, 121.24) * mm, "end": v(120, 138.56) * mm, "construction": true});
            skLineSegment(sketch, "E34.6.4.5", {"start": v(130, 155.88) * mm, "end": v(120, 138.56) * mm, "construction": true});
            skLineSegment(sketch, "E34.6.4.6", {"start": v(140, 138.56) * mm, "end": v(130, 155.88) * mm, "construction": true});
            skLineSegment(sketch, "E34.6.4.7", {"start": v(130, 155.88) * mm, "end": v(150, 155.88) * mm, "construction": true});
            skLineSegment(sketch, "E34.6.4.8", {"start": v(150, 155.88) * mm, "end": v(140, 138.56) * mm, "construction": true});
            skLineSegment(sketch, "E34.6.5.0", {"start": v(130, 155.88) * mm, "end": v(150, 155.88) * mm, "construction": true});
            skLineSegment(sketch, "E34.6.5.1", {"start": v(140, 173.2) * mm, "end": v(130, 155.88) * mm, "construction": true});
            skLineSegment(sketch, "E34.6.5.2", {"start": v(150, 155.88) * mm, "end": v(140, 173.2) * mm, "construction": true});
            skLineSegment(sketch, "E34.6.5.3", {"start": v(120, 173.2) * mm, "end": v(140, 173.2) * mm, "construction": true});
            skLineSegment(sketch, "E34.6.5.4", {"start": v(130, 155.88) * mm, "end": v(120, 173.2) * mm, "construction": true});
            skLineSegment(sketch, "E34.6.5.5", {"start": v(130, 190.53) * mm, "end": v(120, 173.2) * mm, "construction": true});
            skLineSegment(sketch, "E34.6.5.6", {"start": v(140, 173.2) * mm, "end": v(130, 190.53) * mm, "construction": true});
            skLineSegment(sketch, "E34.6.5.7", {"start": v(130, 190.53) * mm, "end": v(150, 190.53) * mm, "construction": true});
            skLineSegment(sketch, "E34.6.5.8", {"start": v(150, 190.53) * mm, "end": v(140, 173.2) * mm, "construction": true});
            skLineSegment(sketch, "E34.6.6.0", {"start": v(130, 190.53) * mm, "end": v(150, 190.53) * mm, "construction": true});
            skLineSegment(sketch, "E34.6.6.1", {"start": v(140, 207.85) * mm, "end": v(130, 190.53) * mm, "construction": true});
            skLineSegment(sketch, "E34.6.6.2", {"start": v(150, 190.53) * mm, "end": v(140, 207.85) * mm, "construction": true});
            skLineSegment(sketch, "E34.6.6.3", {"start": v(120, 207.85) * mm, "end": v(140, 207.85) * mm, "construction": true});
            skLineSegment(sketch, "E34.6.6.4", {"start": v(130, 190.53) * mm, "end": v(120, 207.85) * mm, "construction": true});
            skLineSegment(sketch, "E34.6.6.5", {"start": v(130, 225.17) * mm, "end": v(120, 207.85) * mm, "construction": true});
            skLineSegment(sketch, "E34.6.6.6", {"start": v(140, 207.85) * mm, "end": v(130, 225.17) * mm, "construction": true});
            skLineSegment(sketch, "E34.6.6.7", {"start": v(130, 225.17) * mm, "end": v(150, 225.17) * mm, "construction": true});
            skLineSegment(sketch, "E34.6.6.8", {"start": v(150, 225.17) * mm, "end": v(140, 207.85) * mm, "construction": true});
            skLineSegment(sketch, "E34.7.0.0", {"start": v(150, -17.32) * mm, "end": v(170, -17.32) * mm, "construction": true});
            skLineSegment(sketch, "E34.7.0.1", {"start": v(160, 0) * mm, "end": v(150, -17.32) * mm, "construction": true});
            skLineSegment(sketch, "E34.7.0.2", {"start": v(170, -17.32) * mm, "end": v(160, 0) * mm, "construction": true});
            skLineSegment(sketch, "E34.7.0.3", {"start": v(140, 0) * mm, "end": v(160, 0) * mm, "construction": true});
            skLineSegment(sketch, "E34.7.0.4", {"start": v(150, -17.32) * mm, "end": v(140, 0) * mm, "construction": true});
            skLineSegment(sketch, "E34.7.0.5", {"start": v(150, 17.32) * mm, "end": v(140, 0) * mm, "construction": true});
            skLineSegment(sketch, "E34.7.0.6", {"start": v(160, 0) * mm, "end": v(150, 17.32) * mm, "construction": true});
            skLineSegment(sketch, "E34.7.0.7", {"start": v(150, 17.32) * mm, "end": v(170, 17.32) * mm, "construction": true});
            skLineSegment(sketch, "E34.7.0.8", {"start": v(170, 17.32) * mm, "end": v(160, 0) * mm, "construction": true});
            skLineSegment(sketch, "E34.7.1.0", {"start": v(150, 17.32) * mm, "end": v(170, 17.32) * mm, "construction": true});
            skLineSegment(sketch, "E34.7.1.1", {"start": v(160, 34.64) * mm, "end": v(150, 17.32) * mm, "construction": true});
            skLineSegment(sketch, "E34.7.1.2", {"start": v(170, 17.32) * mm, "end": v(160, 34.64) * mm, "construction": true});
            skLineSegment(sketch, "E34.7.1.3", {"start": v(140, 34.64) * mm, "end": v(160, 34.64) * mm, "construction": true});
            skLineSegment(sketch, "E34.7.1.4", {"start": v(150, 17.32) * mm, "end": v(140, 34.64) * mm, "construction": true});
            skLineSegment(sketch, "E34.7.1.5", {"start": v(150, 51.96) * mm, "end": v(140, 34.64) * mm, "construction": true});
            skLineSegment(sketch, "E34.7.1.6", {"start": v(160, 34.64) * mm, "end": v(150, 51.96) * mm, "construction": true});
            skLineSegment(sketch, "E34.7.1.7", {"start": v(150, 51.96) * mm, "end": v(170, 51.96) * mm, "construction": true});
            skLineSegment(sketch, "E34.7.1.8", {"start": v(170, 51.96) * mm, "end": v(160, 34.64) * mm, "construction": true});
            skLineSegment(sketch, "E34.7.2.0", {"start": v(150, 51.96) * mm, "end": v(170, 51.96) * mm, "construction": true});
            skLineSegment(sketch, "E34.7.2.1", {"start": v(160, 69.28) * mm, "end": v(150, 51.96) * mm, "construction": true});
            skLineSegment(sketch, "E34.7.2.2", {"start": v(170, 51.96) * mm, "end": v(160, 69.28) * mm, "construction": true});
            skLineSegment(sketch, "E34.7.2.3", {"start": v(140, 69.28) * mm, "end": v(160, 69.28) * mm, "construction": true});
            skLineSegment(sketch, "E34.7.2.4", {"start": v(150, 51.96) * mm, "end": v(140, 69.28) * mm, "construction": true});
            skLineSegment(sketch, "E34.7.2.5", {"start": v(150, 86.6) * mm, "end": v(140, 69.28) * mm, "construction": true});
            skLineSegment(sketch, "E34.7.2.6", {"start": v(160, 69.28) * mm, "end": v(150, 86.6) * mm, "construction": true});
            skLineSegment(sketch, "E34.7.2.7", {"start": v(150, 86.6) * mm, "end": v(170, 86.6) * mm, "construction": true});
            skLineSegment(sketch, "E34.7.2.8", {"start": v(170, 86.6) * mm, "end": v(160, 69.28) * mm, "construction": true});
            skLineSegment(sketch, "E34.7.3.0", {"start": v(150, 86.6) * mm, "end": v(170, 86.6) * mm, "construction": true});
            skLineSegment(sketch, "E34.7.3.1", {"start": v(160, 103.92) * mm, "end": v(150, 86.6) * mm, "construction": true});
            skLineSegment(sketch, "E34.7.3.2", {"start": v(170, 86.6) * mm, "end": v(160, 103.92) * mm, "construction": true});
            skLineSegment(sketch, "E34.7.3.3", {"start": v(140, 103.92) * mm, "end": v(160, 103.92) * mm, "construction": true});
            skLineSegment(sketch, "E34.7.3.4", {"start": v(150, 86.6) * mm, "end": v(140, 103.92) * mm, "construction": true});
            skLineSegment(sketch, "E34.7.3.5", {"start": v(150, 121.24) * mm, "end": v(140, 103.92) * mm, "construction": true});
            skLineSegment(sketch, "E34.7.3.6", {"start": v(160, 103.92) * mm, "end": v(150, 121.24) * mm, "construction": true});
            skLineSegment(sketch, "E34.7.3.7", {"start": v(150, 121.24) * mm, "end": v(170, 121.24) * mm, "construction": true});
            skLineSegment(sketch, "E34.7.3.8", {"start": v(170, 121.24) * mm, "end": v(160, 103.92) * mm, "construction": true});
            skLineSegment(sketch, "E34.7.4.0", {"start": v(150, 121.24) * mm, "end": v(170, 121.24) * mm, "construction": true});
            skLineSegment(sketch, "E34.7.4.1", {"start": v(160, 138.56) * mm, "end": v(150, 121.24) * mm, "construction": true});
            skLineSegment(sketch, "E34.7.4.2", {"start": v(170, 121.24) * mm, "end": v(160, 138.56) * mm, "construction": true});
            skLineSegment(sketch, "E34.7.4.3", {"start": v(140, 138.56) * mm, "end": v(160, 138.56) * mm, "construction": true});
            skLineSegment(sketch, "E34.7.4.4", {"start": v(150, 121.24) * mm, "end": v(140, 138.56) * mm, "construction": true});
            skLineSegment(sketch, "E34.7.4.5", {"start": v(150, 155.88) * mm, "end": v(140, 138.56) * mm, "construction": true});
            skLineSegment(sketch, "E34.7.4.6", {"start": v(160, 138.56) * mm, "end": v(150, 155.88) * mm, "construction": true});
            skLineSegment(sketch, "E34.7.4.7", {"start": v(150, 155.88) * mm, "end": v(170, 155.88) * mm, "construction": true});
            skLineSegment(sketch, "E34.7.4.8", {"start": v(170, 155.88) * mm, "end": v(160, 138.56) * mm, "construction": true});
            skLineSegment(sketch, "E34.7.5.0", {"start": v(150, 155.88) * mm, "end": v(170, 155.88) * mm, "construction": true});
            skLineSegment(sketch, "E34.7.5.1", {"start": v(160, 173.2) * mm, "end": v(150, 155.88) * mm, "construction": true});
            skLineSegment(sketch, "E34.7.5.2", {"start": v(170, 155.88) * mm, "end": v(160, 173.2) * mm, "construction": true});
            skLineSegment(sketch, "E34.7.5.3", {"start": v(140, 173.2) * mm, "end": v(160, 173.2) * mm, "construction": true});
            skLineSegment(sketch, "E34.7.5.4", {"start": v(150, 155.88) * mm, "end": v(140, 173.2) * mm, "construction": true});
            skLineSegment(sketch, "E34.7.5.5", {"start": v(150, 190.53) * mm, "end": v(140, 173.2) * mm, "construction": true});
            skLineSegment(sketch, "E34.7.5.6", {"start": v(160, 173.2) * mm, "end": v(150, 190.53) * mm, "construction": true});
            skLineSegment(sketch, "E34.7.5.7", {"start": v(150, 190.53) * mm, "end": v(170, 190.53) * mm, "construction": true});
            skLineSegment(sketch, "E34.7.5.8", {"start": v(170, 190.53) * mm, "end": v(160, 173.2) * mm, "construction": true});
            skLineSegment(sketch, "E34.7.6.0", {"start": v(150, 190.53) * mm, "end": v(170, 190.53) * mm, "construction": true});
            skLineSegment(sketch, "E34.7.6.1", {"start": v(160, 207.85) * mm, "end": v(150, 190.53) * mm, "construction": true});
            skLineSegment(sketch, "E34.7.6.2", {"start": v(170, 190.53) * mm, "end": v(160, 207.85) * mm, "construction": true});
            skLineSegment(sketch, "E34.7.6.3", {"start": v(140, 207.85) * mm, "end": v(160, 207.85) * mm, "construction": true});
            skLineSegment(sketch, "E34.7.6.4", {"start": v(150, 190.53) * mm, "end": v(140, 207.85) * mm, "construction": true});
            skLineSegment(sketch, "E34.7.6.5", {"start": v(150, 225.17) * mm, "end": v(140, 207.85) * mm, "construction": true});
            skLineSegment(sketch, "E34.7.6.6", {"start": v(160, 207.85) * mm, "end": v(150, 225.17) * mm, "construction": true});
            skLineSegment(sketch, "E34.7.6.7", {"start": v(150, 225.17) * mm, "end": v(170, 225.17) * mm, "construction": true});
            skLineSegment(sketch, "E34.7.6.8", {"start": v(170, 225.17) * mm, "end": v(160, 207.85) * mm, "construction": true});
            skLineSegment(sketch, "E34.8.0.0", {"start": v(170, -17.32) * mm, "end": v(190, -17.32) * mm, "construction": true});
            skLineSegment(sketch, "E34.8.0.1", {"start": v(180, 0) * mm, "end": v(170, -17.32) * mm, "construction": true});
            skLineSegment(sketch, "E34.8.0.2", {"start": v(190, -17.32) * mm, "end": v(180, 0) * mm, "construction": true});
            skLineSegment(sketch, "E34.8.0.3", {"start": v(160, 0) * mm, "end": v(180, 0) * mm, "construction": true});
            skLineSegment(sketch, "E34.8.0.4", {"start": v(170, -17.32) * mm, "end": v(160, 0) * mm, "construction": true});
            skLineSegment(sketch, "E34.8.0.5", {"start": v(170, 17.32) * mm, "end": v(160, 0) * mm, "construction": true});
            skLineSegment(sketch, "E34.8.0.6", {"start": v(180, 0) * mm, "end": v(170, 17.32) * mm, "construction": true});
            skLineSegment(sketch, "E34.8.0.7", {"start": v(170, 17.32) * mm, "end": v(190, 17.32) * mm, "construction": true});
            skLineSegment(sketch, "E34.8.0.8", {"start": v(190, 17.32) * mm, "end": v(180, 0) * mm, "construction": true});
            skLineSegment(sketch, "E34.8.1.0", {"start": v(170, 17.32) * mm, "end": v(190, 17.32) * mm, "construction": true});
            skLineSegment(sketch, "E34.8.1.1", {"start": v(180, 34.64) * mm, "end": v(170, 17.32) * mm, "construction": true});
            skLineSegment(sketch, "E34.8.1.2", {"start": v(190, 17.32) * mm, "end": v(180, 34.64) * mm, "construction": true});
            skLineSegment(sketch, "E34.8.1.3", {"start": v(160, 34.64) * mm, "end": v(180, 34.64) * mm, "construction": true});
            skLineSegment(sketch, "E34.8.1.4", {"start": v(170, 17.32) * mm, "end": v(160, 34.64) * mm, "construction": true});
            skLineSegment(sketch, "E34.8.1.5", {"start": v(170, 51.96) * mm, "end": v(160, 34.64) * mm, "construction": true});
            skLineSegment(sketch, "E34.8.1.6", {"start": v(180, 34.64) * mm, "end": v(170, 51.96) * mm, "construction": true});
            skLineSegment(sketch, "E34.8.1.7", {"start": v(170, 51.96) * mm, "end": v(190, 51.96) * mm, "construction": true});
            skLineSegment(sketch, "E34.8.1.8", {"start": v(190, 51.96) * mm, "end": v(180, 34.64) * mm, "construction": true});
            skLineSegment(sketch, "E34.8.2.0", {"start": v(170, 51.96) * mm, "end": v(190, 51.96) * mm, "construction": true});
            skLineSegment(sketch, "E34.8.2.1", {"start": v(180, 69.28) * mm, "end": v(170, 51.96) * mm, "construction": true});
            skLineSegment(sketch, "E34.8.2.2", {"start": v(190, 51.96) * mm, "end": v(180, 69.28) * mm, "construction": true});
            skLineSegment(sketch, "E34.8.2.3", {"start": v(160, 69.28) * mm, "end": v(180, 69.28) * mm, "construction": true});
            skLineSegment(sketch, "E34.8.2.4", {"start": v(170, 51.96) * mm, "end": v(160, 69.28) * mm, "construction": true});
            skLineSegment(sketch, "E34.8.2.5", {"start": v(170, 86.6) * mm, "end": v(160, 69.28) * mm, "construction": true});
            skLineSegment(sketch, "E34.8.2.6", {"start": v(180, 69.28) * mm, "end": v(170, 86.6) * mm, "construction": true});
            skLineSegment(sketch, "E34.8.2.7", {"start": v(170, 86.6) * mm, "end": v(190, 86.6) * mm, "construction": true});
            skLineSegment(sketch, "E34.8.2.8", {"start": v(190, 86.6) * mm, "end": v(180, 69.28) * mm, "construction": true});
            skLineSegment(sketch, "E34.8.3.0", {"start": v(170, 86.6) * mm, "end": v(190, 86.6) * mm, "construction": true});
            skLineSegment(sketch, "E34.8.3.1", {"start": v(180, 103.92) * mm, "end": v(170, 86.6) * mm, "construction": true});
            skLineSegment(sketch, "E34.8.3.2", {"start": v(190, 86.6) * mm, "end": v(180, 103.92) * mm, "construction": true});
            skLineSegment(sketch, "E34.8.3.3", {"start": v(160, 103.92) * mm, "end": v(180, 103.92) * mm, "construction": true});
            skLineSegment(sketch, "E34.8.3.4", {"start": v(170, 86.6) * mm, "end": v(160, 103.92) * mm, "construction": true});
            skLineSegment(sketch, "E34.8.3.5", {"start": v(170, 121.24) * mm, "end": v(160, 103.92) * mm, "construction": true});
            skLineSegment(sketch, "E34.8.3.6", {"start": v(180, 103.92) * mm, "end": v(170, 121.24) * mm, "construction": true});
            skLineSegment(sketch, "E34.8.3.7", {"start": v(170, 121.24) * mm, "end": v(190, 121.24) * mm, "construction": true});
            skLineSegment(sketch, "E34.8.3.8", {"start": v(190, 121.24) * mm, "end": v(180, 103.92) * mm, "construction": true});
            skLineSegment(sketch, "E34.8.4.0", {"start": v(170, 121.24) * mm, "end": v(190, 121.24) * mm, "construction": true});
            skLineSegment(sketch, "E34.8.4.1", {"start": v(180, 138.56) * mm, "end": v(170, 121.24) * mm, "construction": true});
            skLineSegment(sketch, "E34.8.4.2", {"start": v(190, 121.24) * mm, "end": v(180, 138.56) * mm, "construction": true});
            skLineSegment(sketch, "E34.8.4.3", {"start": v(160, 138.56) * mm, "end": v(180, 138.56) * mm, "construction": true});
            skLineSegment(sketch, "E34.8.4.4", {"start": v(170, 121.24) * mm, "end": v(160, 138.56) * mm, "construction": true});
            skLineSegment(sketch, "E34.8.4.5", {"start": v(170, 155.88) * mm, "end": v(160, 138.56) * mm, "construction": true});
            skLineSegment(sketch, "E34.8.4.6", {"start": v(180, 138.56) * mm, "end": v(170, 155.88) * mm, "construction": true});
            skLineSegment(sketch, "E34.8.4.7", {"start": v(170, 155.88) * mm, "end": v(190, 155.88) * mm, "construction": true});
            skLineSegment(sketch, "E34.8.4.8", {"start": v(190, 155.88) * mm, "end": v(180, 138.56) * mm, "construction": true});
            skLineSegment(sketch, "E34.8.5.0", {"start": v(170, 155.88) * mm, "end": v(190, 155.88) * mm, "construction": true});
            skLineSegment(sketch, "E34.8.5.1", {"start": v(180, 173.2) * mm, "end": v(170, 155.88) * mm, "construction": true});
            skLineSegment(sketch, "E34.8.5.2", {"start": v(190, 155.88) * mm, "end": v(180, 173.2) * mm, "construction": true});
            skLineSegment(sketch, "E34.8.5.3", {"start": v(160, 173.2) * mm, "end": v(180, 173.2) * mm, "construction": true});
            skLineSegment(sketch, "E34.8.5.4", {"start": v(170, 155.88) * mm, "end": v(160, 173.2) * mm, "construction": true});
            skLineSegment(sketch, "E34.8.5.5", {"start": v(170, 190.53) * mm, "end": v(160, 173.2) * mm, "construction": true});
            skLineSegment(sketch, "E34.8.5.6", {"start": v(180, 173.2) * mm, "end": v(170, 190.53) * mm, "construction": true});
            skLineSegment(sketch, "E34.8.5.7", {"start": v(170, 190.53) * mm, "end": v(190, 190.53) * mm, "construction": true});
            skLineSegment(sketch, "E34.8.5.8", {"start": v(190, 190.53) * mm, "end": v(180, 173.2) * mm, "construction": true});
            skLineSegment(sketch, "E34.8.6.0", {"start": v(170, 190.53) * mm, "end": v(190, 190.53) * mm, "construction": true});
            skLineSegment(sketch, "E34.8.6.1", {"start": v(180, 207.85) * mm, "end": v(170, 190.53) * mm, "construction": true});
            skLineSegment(sketch, "E34.8.6.2", {"start": v(190, 190.53) * mm, "end": v(180, 207.85) * mm, "construction": true});
            skLineSegment(sketch, "E34.8.6.3", {"start": v(160, 207.85) * mm, "end": v(180, 207.85) * mm, "construction": true});
            skLineSegment(sketch, "E34.8.6.4", {"start": v(170, 190.53) * mm, "end": v(160, 207.85) * mm, "construction": true});
            skLineSegment(sketch, "E34.8.6.5", {"start": v(170, 225.17) * mm, "end": v(160, 207.85) * mm, "construction": true});
            skLineSegment(sketch, "E34.8.6.6", {"start": v(180, 207.85) * mm, "end": v(170, 225.17) * mm, "construction": true});
            skLineSegment(sketch, "E34.8.6.7", {"start": v(170, 225.17) * mm, "end": v(190, 225.17) * mm, "construction": true});
            skLineSegment(sketch, "E34.8.6.8", {"start": v(190, 225.17) * mm, "end": v(180, 207.85) * mm, "construction": true});
            skLineSegment(sketch, "E34.9.0.0", {"start": v(190, -17.32) * mm, "end": v(210, -17.32) * mm, "construction": true});
            skLineSegment(sketch, "E34.9.0.1", {"start": v(200, 0) * mm, "end": v(190, -17.32) * mm, "construction": true});
            skLineSegment(sketch, "E34.9.0.2", {"start": v(210, -17.32) * mm, "end": v(200, 0) * mm, "construction": true});
            skLineSegment(sketch, "E34.9.0.3", {"start": v(180, 0) * mm, "end": v(200, 0) * mm, "construction": true});
            skLineSegment(sketch, "E34.9.0.4", {"start": v(190, -17.32) * mm, "end": v(180, 0) * mm, "construction": true});
            skLineSegment(sketch, "E34.9.0.5", {"start": v(190, 17.32) * mm, "end": v(180, 0) * mm, "construction": true});
            skLineSegment(sketch, "E34.9.0.6", {"start": v(200, 0) * mm, "end": v(190, 17.32) * mm, "construction": true});
            skLineSegment(sketch, "E34.9.0.7", {"start": v(190, 17.32) * mm, "end": v(210, 17.32) * mm, "construction": true});
            skLineSegment(sketch, "E34.9.0.8", {"start": v(210, 17.32) * mm, "end": v(200, 0) * mm, "construction": true});
            skLineSegment(sketch, "E34.9.1.0", {"start": v(190, 17.32) * mm, "end": v(210, 17.32) * mm, "construction": true});
            skLineSegment(sketch, "E34.9.1.1", {"start": v(200, 34.64) * mm, "end": v(190, 17.32) * mm, "construction": true});
            skLineSegment(sketch, "E34.9.1.2", {"start": v(210, 17.32) * mm, "end": v(200, 34.64) * mm, "construction": true});
            skLineSegment(sketch, "E34.9.1.3", {"start": v(180, 34.64) * mm, "end": v(200, 34.64) * mm, "construction": true});
            skLineSegment(sketch, "E34.9.1.4", {"start": v(190, 17.32) * mm, "end": v(180, 34.64) * mm, "construction": true});
            skLineSegment(sketch, "E34.9.1.5", {"start": v(190, 51.96) * mm, "end": v(180, 34.64) * mm, "construction": true});
            skLineSegment(sketch, "E34.9.1.6", {"start": v(200, 34.64) * mm, "end": v(190, 51.96) * mm, "construction": true});
            skLineSegment(sketch, "E34.9.1.7", {"start": v(190, 51.96) * mm, "end": v(210, 51.96) * mm, "construction": true});
            skLineSegment(sketch, "E34.9.1.8", {"start": v(210, 51.96) * mm, "end": v(200, 34.64) * mm, "construction": true});
            skLineSegment(sketch, "E34.9.2.0", {"start": v(190, 51.96) * mm, "end": v(210, 51.96) * mm, "construction": true});
            skLineSegment(sketch, "E34.9.2.1", {"start": v(200, 69.28) * mm, "end": v(190, 51.96) * mm, "construction": true});
            skLineSegment(sketch, "E34.9.2.2", {"start": v(210, 51.96) * mm, "end": v(200, 69.28) * mm, "construction": true});
            skLineSegment(sketch, "E34.9.2.3", {"start": v(180, 69.28) * mm, "end": v(200, 69.28) * mm, "construction": true});
            skLineSegment(sketch, "E34.9.2.4", {"start": v(190, 51.96) * mm, "end": v(180, 69.28) * mm, "construction": true});
            skLineSegment(sketch, "E34.9.2.5", {"start": v(190, 86.6) * mm, "end": v(180, 69.28) * mm, "construction": true});
            skLineSegment(sketch, "E34.9.2.6", {"start": v(200, 69.28) * mm, "end": v(190, 86.6) * mm, "construction": true});
            skLineSegment(sketch, "E34.9.2.7", {"start": v(190, 86.6) * mm, "end": v(210, 86.6) * mm, "construction": true});
            skLineSegment(sketch, "E34.9.2.8", {"start": v(210, 86.6) * mm, "end": v(200, 69.28) * mm, "construction": true});
            skLineSegment(sketch, "E34.9.3.0", {"start": v(190, 86.6) * mm, "end": v(210, 86.6) * mm, "construction": true});
            skLineSegment(sketch, "E34.9.3.1", {"start": v(200, 103.92) * mm, "end": v(190, 86.6) * mm, "construction": true});
            skLineSegment(sketch, "E34.9.3.2", {"start": v(210, 86.6) * mm, "end": v(200, 103.92) * mm, "construction": true});
            skLineSegment(sketch, "E34.9.3.3", {"start": v(180, 103.92) * mm, "end": v(200, 103.92) * mm, "construction": true});
            skLineSegment(sketch, "E34.9.3.4", {"start": v(190, 86.6) * mm, "end": v(180, 103.92) * mm, "construction": true});
            skLineSegment(sketch, "E34.9.3.5", {"start": v(190, 121.24) * mm, "end": v(180, 103.92) * mm, "construction": true});
            skLineSegment(sketch, "E34.9.3.6", {"start": v(200, 103.92) * mm, "end": v(190, 121.24) * mm, "construction": true});
            skLineSegment(sketch, "E34.9.3.7", {"start": v(190, 121.24) * mm, "end": v(210, 121.24) * mm, "construction": true});
            skLineSegment(sketch, "E34.9.3.8", {"start": v(210, 121.24) * mm, "end": v(200, 103.92) * mm, "construction": true});
            skLineSegment(sketch, "E34.9.4.0", {"start": v(190, 121.24) * mm, "end": v(210, 121.24) * mm, "construction": true});
            skLineSegment(sketch, "E34.9.4.1", {"start": v(200, 138.56) * mm, "end": v(190, 121.24) * mm, "construction": true});
            skLineSegment(sketch, "E34.9.4.2", {"start": v(210, 121.24) * mm, "end": v(200, 138.56) * mm, "construction": true});
            skLineSegment(sketch, "E34.9.4.3", {"start": v(180, 138.56) * mm, "end": v(200, 138.56) * mm, "construction": true});
            skLineSegment(sketch, "E34.9.4.4", {"start": v(190, 121.24) * mm, "end": v(180, 138.56) * mm, "construction": true});
            skLineSegment(sketch, "E34.9.4.5", {"start": v(190, 155.88) * mm, "end": v(180, 138.56) * mm, "construction": true});
            skLineSegment(sketch, "E34.9.4.6", {"start": v(200, 138.56) * mm, "end": v(190, 155.88) * mm, "construction": true});
            skLineSegment(sketch, "E34.9.4.7", {"start": v(190, 155.88) * mm, "end": v(210, 155.88) * mm, "construction": true});
            skLineSegment(sketch, "E34.9.4.8", {"start": v(210, 155.88) * mm, "end": v(200, 138.56) * mm, "construction": true});
            skLineSegment(sketch, "E34.9.5.0", {"start": v(190, 155.88) * mm, "end": v(210, 155.88) * mm, "construction": true});
            skLineSegment(sketch, "E34.9.5.1", {"start": v(200, 173.2) * mm, "end": v(190, 155.88) * mm, "construction": true});
            skLineSegment(sketch, "E34.9.5.2", {"start": v(210, 155.88) * mm, "end": v(200, 173.2) * mm, "construction": true});
            skLineSegment(sketch, "E34.9.5.3", {"start": v(180, 173.2) * mm, "end": v(200, 173.2) * mm, "construction": true});
            skLineSegment(sketch, "E34.9.5.4", {"start": v(190, 155.88) * mm, "end": v(180, 173.2) * mm, "construction": true});
            skLineSegment(sketch, "E34.9.5.5", {"start": v(190, 190.53) * mm, "end": v(180, 173.2) * mm, "construction": true});
            skLineSegment(sketch, "E34.9.5.6", {"start": v(200, 173.2) * mm, "end": v(190, 190.53) * mm, "construction": true});
            skLineSegment(sketch, "E34.9.5.7", {"start": v(190, 190.53) * mm, "end": v(210, 190.53) * mm, "construction": true});
            skLineSegment(sketch, "E34.9.5.8", {"start": v(210, 190.53) * mm, "end": v(200, 173.2) * mm, "construction": true});
            skLineSegment(sketch, "E34.9.6.0", {"start": v(190, 190.53) * mm, "end": v(210, 190.53) * mm, "construction": true});
            skLineSegment(sketch, "E34.9.6.1", {"start": v(200, 207.85) * mm, "end": v(190, 190.53) * mm, "construction": true});
            skLineSegment(sketch, "E34.9.6.2", {"start": v(210, 190.53) * mm, "end": v(200, 207.85) * mm, "construction": true});
            skLineSegment(sketch, "E34.9.6.3", {"start": v(180, 207.85) * mm, "end": v(200, 207.85) * mm, "construction": true});
            skLineSegment(sketch, "E34.9.6.4", {"start": v(190, 190.53) * mm, "end": v(180, 207.85) * mm, "construction": true});
            skLineSegment(sketch, "E34.9.6.5", {"start": v(190, 225.17) * mm, "end": v(180, 207.85) * mm, "construction": true});
            skLineSegment(sketch, "E34.9.6.6", {"start": v(200, 207.85) * mm, "end": v(190, 225.17) * mm, "construction": true});
            skLineSegment(sketch, "E34.9.6.7", {"start": v(190, 225.17) * mm, "end": v(210, 225.17) * mm, "construction": true});
            skLineSegment(sketch, "E34.9.6.8", {"start": v(210, 225.17) * mm, "end": v(200, 207.85) * mm, "construction": true});
            skLineSegment(sketch, "E34.10.0.0", {"start": v(210, -17.32) * mm, "end": v(230, -17.32) * mm, "construction": true});
            skLineSegment(sketch, "E34.10.0.1", {"start": v(220, 0) * mm, "end": v(210, -17.32) * mm, "construction": true});
            skLineSegment(sketch, "E34.10.0.2", {"start": v(230, -17.32) * mm, "end": v(220, 0) * mm, "construction": true});
            skLineSegment(sketch, "E34.10.0.3", {"start": v(200, 0) * mm, "end": v(220, 0) * mm, "construction": true});
            skLineSegment(sketch, "E34.10.0.4", {"start": v(210, -17.32) * mm, "end": v(200, 0) * mm, "construction": true});
            skLineSegment(sketch, "E34.10.0.5", {"start": v(210, 17.32) * mm, "end": v(200, 0) * mm, "construction": true});
            skLineSegment(sketch, "E34.10.0.6", {"start": v(220, 0) * mm, "end": v(210, 17.32) * mm, "construction": true});
            skLineSegment(sketch, "E34.10.0.7", {"start": v(210, 17.32) * mm, "end": v(230, 17.32) * mm, "construction": true});
            skLineSegment(sketch, "E34.10.0.8", {"start": v(230, 17.32) * mm, "end": v(220, 0) * mm, "construction": true});
            skLineSegment(sketch, "E34.10.1.0", {"start": v(210, 17.32) * mm, "end": v(230, 17.32) * mm, "construction": true});
            skLineSegment(sketch, "E34.10.1.1", {"start": v(220, 34.64) * mm, "end": v(210, 17.32) * mm, "construction": true});
            skLineSegment(sketch, "E34.10.1.2", {"start": v(230, 17.32) * mm, "end": v(220, 34.64) * mm, "construction": true});
            skLineSegment(sketch, "E34.10.1.3", {"start": v(200, 34.64) * mm, "end": v(220, 34.64) * mm, "construction": true});
            skLineSegment(sketch, "E34.10.1.4", {"start": v(210, 17.32) * mm, "end": v(200, 34.64) * mm, "construction": true});
            skLineSegment(sketch, "E34.10.1.5", {"start": v(210, 51.96) * mm, "end": v(200, 34.64) * mm, "construction": true});
            skLineSegment(sketch, "E34.10.1.6", {"start": v(220, 34.64) * mm, "end": v(210, 51.96) * mm, "construction": true});
            skLineSegment(sketch, "E34.10.1.7", {"start": v(210, 51.96) * mm, "end": v(230, 51.96) * mm, "construction": true});
            skLineSegment(sketch, "E34.10.1.8", {"start": v(230, 51.96) * mm, "end": v(220, 34.64) * mm, "construction": true});
            skLineSegment(sketch, "E34.10.2.0", {"start": v(210, 51.96) * mm, "end": v(230, 51.96) * mm, "construction": true});
            skLineSegment(sketch, "E34.10.2.1", {"start": v(220, 69.28) * mm, "end": v(210, 51.96) * mm, "construction": true});
            skLineSegment(sketch, "E34.10.2.2", {"start": v(230, 51.96) * mm, "end": v(220, 69.28) * mm, "construction": true});
            skLineSegment(sketch, "E34.10.2.3", {"start": v(200, 69.28) * mm, "end": v(220, 69.28) * mm, "construction": true});
            skLineSegment(sketch, "E34.10.2.4", {"start": v(210, 51.96) * mm, "end": v(200, 69.28) * mm, "construction": true});
            skLineSegment(sketch, "E34.10.2.5", {"start": v(210, 86.6) * mm, "end": v(200, 69.28) * mm, "construction": true});
            skLineSegment(sketch, "E34.10.2.6", {"start": v(220, 69.28) * mm, "end": v(210, 86.6) * mm, "construction": true});
            skLineSegment(sketch, "E34.10.2.7", {"start": v(210, 86.6) * mm, "end": v(230, 86.6) * mm, "construction": true});
            skLineSegment(sketch, "E34.10.2.8", {"start": v(230, 86.6) * mm, "end": v(220, 69.28) * mm, "construction": true});
            skLineSegment(sketch, "E34.10.3.0", {"start": v(210, 86.6) * mm, "end": v(230, 86.6) * mm, "construction": true});
            skLineSegment(sketch, "E34.10.3.1", {"start": v(220, 103.92) * mm, "end": v(210, 86.6) * mm, "construction": true});
            skLineSegment(sketch, "E34.10.3.2", {"start": v(230, 86.6) * mm, "end": v(220, 103.92) * mm, "construction": true});
            skLineSegment(sketch, "E34.10.3.3", {"start": v(200, 103.92) * mm, "end": v(220, 103.92) * mm, "construction": true});
            skLineSegment(sketch, "E34.10.3.4", {"start": v(210, 86.6) * mm, "end": v(200, 103.92) * mm, "construction": true});
            skLineSegment(sketch, "E34.10.3.5", {"start": v(210, 121.24) * mm, "end": v(200, 103.92) * mm, "construction": true});
            skLineSegment(sketch, "E34.10.3.6", {"start": v(220, 103.92) * mm, "end": v(210, 121.24) * mm, "construction": true});
            skLineSegment(sketch, "E34.10.3.7", {"start": v(210, 121.24) * mm, "end": v(230, 121.24) * mm, "construction": true});
            skLineSegment(sketch, "E34.10.3.8", {"start": v(230, 121.24) * mm, "end": v(220, 103.92) * mm, "construction": true});
            skLineSegment(sketch, "E34.10.4.0", {"start": v(210, 121.24) * mm, "end": v(230, 121.24) * mm, "construction": true});
            skLineSegment(sketch, "E34.10.4.1", {"start": v(220, 138.56) * mm, "end": v(210, 121.24) * mm, "construction": true});
            skLineSegment(sketch, "E34.10.4.2", {"start": v(230, 121.24) * mm, "end": v(220, 138.56) * mm, "construction": true});
            skLineSegment(sketch, "E34.10.4.3", {"start": v(200, 138.56) * mm, "end": v(220, 138.56) * mm, "construction": true});
            skLineSegment(sketch, "E34.10.4.4", {"start": v(210, 121.24) * mm, "end": v(200, 138.56) * mm, "construction": true});
            skLineSegment(sketch, "E34.10.4.5", {"start": v(210, 155.88) * mm, "end": v(200, 138.56) * mm, "construction": true});
            skLineSegment(sketch, "E34.10.4.6", {"start": v(220, 138.56) * mm, "end": v(210, 155.88) * mm, "construction": true});
            skLineSegment(sketch, "E34.10.4.7", {"start": v(210, 155.88) * mm, "end": v(230, 155.88) * mm, "construction": true});
            skLineSegment(sketch, "E34.10.4.8", {"start": v(230, 155.88) * mm, "end": v(220, 138.56) * mm, "construction": true});
            skLineSegment(sketch, "E34.10.5.0", {"start": v(210, 155.88) * mm, "end": v(230, 155.88) * mm, "construction": true});
            skLineSegment(sketch, "E34.10.5.1", {"start": v(220, 173.2) * mm, "end": v(210, 155.88) * mm, "construction": true});
            skLineSegment(sketch, "E34.10.5.2", {"start": v(230, 155.88) * mm, "end": v(220, 173.2) * mm, "construction": true});
            skLineSegment(sketch, "E34.10.5.3", {"start": v(200, 173.2) * mm, "end": v(220, 173.2) * mm, "construction": true});
            skLineSegment(sketch, "E34.10.5.4", {"start": v(210, 155.88) * mm, "end": v(200, 173.2) * mm, "construction": true});
            skLineSegment(sketch, "E34.10.5.5", {"start": v(210, 190.53) * mm, "end": v(200, 173.2) * mm, "construction": true});
            skLineSegment(sketch, "E34.10.5.6", {"start": v(220, 173.2) * mm, "end": v(210, 190.53) * mm, "construction": true});
            skLineSegment(sketch, "E34.10.5.7", {"start": v(210, 190.53) * mm, "end": v(230, 190.53) * mm, "construction": true});
            skLineSegment(sketch, "E34.10.5.8", {"start": v(230, 190.53) * mm, "end": v(220, 173.2) * mm, "construction": true});
            skLineSegment(sketch, "E34.10.6.0", {"start": v(210, 190.53) * mm, "end": v(230, 190.53) * mm, "construction": true});
            skLineSegment(sketch, "E34.10.6.1", {"start": v(220, 207.85) * mm, "end": v(210, 190.53) * mm, "construction": true});
            skLineSegment(sketch, "E34.10.6.2", {"start": v(230, 190.53) * mm, "end": v(220, 207.85) * mm, "construction": true});
            skLineSegment(sketch, "E34.10.6.3", {"start": v(200, 207.85) * mm, "end": v(220, 207.85) * mm, "construction": true});
            skLineSegment(sketch, "E34.10.6.4", {"start": v(210, 190.53) * mm, "end": v(200, 207.85) * mm, "construction": true});
            skLineSegment(sketch, "E34.10.6.5", {"start": v(210, 225.17) * mm, "end": v(200, 207.85) * mm, "construction": true});
            skLineSegment(sketch, "E34.10.6.6", {"start": v(220, 207.85) * mm, "end": v(210, 225.17) * mm, "construction": true});
            skLineSegment(sketch, "E34.10.6.7", {"start": v(210, 225.17) * mm, "end": v(230, 225.17) * mm, "construction": true});
            skLineSegment(sketch, "E34.10.6.8", {"start": v(230, 225.17) * mm, "end": v(220, 207.85) * mm, "construction": true});
            skLineSegment(sketch, "E34.11.0.0", {"start": v(230, -17.32) * mm, "end": v(250, -17.32) * mm, "construction": true});
            skLineSegment(sketch, "E34.11.0.1", {"start": v(240, 0) * mm, "end": v(230, -17.32) * mm, "construction": true});
            skLineSegment(sketch, "E34.11.0.2", {"start": v(250, -17.32) * mm, "end": v(240, 0) * mm, "construction": true});
            skLineSegment(sketch, "E34.11.0.3", {"start": v(220, 0) * mm, "end": v(240, 0) * mm, "construction": true});
            skLineSegment(sketch, "E34.11.0.4", {"start": v(230, -17.32) * mm, "end": v(220, 0) * mm, "construction": true});
            skLineSegment(sketch, "E34.11.0.5", {"start": v(230, 17.32) * mm, "end": v(220, 0) * mm, "construction": true});
            skLineSegment(sketch, "E34.11.0.6", {"start": v(240, 0) * mm, "end": v(230, 17.32) * mm, "construction": true});
            skLineSegment(sketch, "E34.11.0.7", {"start": v(230, 17.32) * mm, "end": v(250, 17.32) * mm, "construction": true});
            skLineSegment(sketch, "E34.11.0.8", {"start": v(250, 17.32) * mm, "end": v(240, 0) * mm, "construction": true});
            skLineSegment(sketch, "E34.11.1.0", {"start": v(230, 17.32) * mm, "end": v(250, 17.32) * mm, "construction": true});
            skLineSegment(sketch, "E34.11.1.1", {"start": v(240, 34.64) * mm, "end": v(230, 17.32) * mm, "construction": true});
            skLineSegment(sketch, "E34.11.1.2", {"start": v(250, 17.32) * mm, "end": v(240, 34.64) * mm, "construction": true});
            skLineSegment(sketch, "E34.11.1.3", {"start": v(220, 34.64) * mm, "end": v(240, 34.64) * mm, "construction": true});
            skLineSegment(sketch, "E34.11.1.4", {"start": v(230, 17.32) * mm, "end": v(220, 34.64) * mm, "construction": true});
            skLineSegment(sketch, "E34.11.1.5", {"start": v(230, 51.96) * mm, "end": v(220, 34.64) * mm, "construction": true});
            skLineSegment(sketch, "E34.11.1.6", {"start": v(240, 34.64) * mm, "end": v(230, 51.96) * mm, "construction": true});
            skLineSegment(sketch, "E34.11.1.7", {"start": v(230, 51.96) * mm, "end": v(250, 51.96) * mm, "construction": true});
            skLineSegment(sketch, "E34.11.1.8", {"start": v(250, 51.96) * mm, "end": v(240, 34.64) * mm, "construction": true});
            skLineSegment(sketch, "E34.11.2.0", {"start": v(230, 51.96) * mm, "end": v(250, 51.96) * mm, "construction": true});
            skLineSegment(sketch, "E34.11.2.1", {"start": v(240, 69.28) * mm, "end": v(230, 51.96) * mm, "construction": true});
            skLineSegment(sketch, "E34.11.2.2", {"start": v(250, 51.96) * mm, "end": v(240, 69.28) * mm, "construction": true});
            skLineSegment(sketch, "E34.11.2.3", {"start": v(220, 69.28) * mm, "end": v(240, 69.28) * mm, "construction": true});
            skLineSegment(sketch, "E34.11.2.4", {"start": v(230, 51.96) * mm, "end": v(220, 69.28) * mm, "construction": true});
            skLineSegment(sketch, "E34.11.2.5", {"start": v(230, 86.6) * mm, "end": v(220, 69.28) * mm, "construction": true});
            skLineSegment(sketch, "E34.11.2.6", {"start": v(240, 69.28) * mm, "end": v(230, 86.6) * mm, "construction": true});
            skLineSegment(sketch, "E34.11.2.7", {"start": v(230, 86.6) * mm, "end": v(250, 86.6) * mm, "construction": true});
            skLineSegment(sketch, "E34.11.2.8", {"start": v(250, 86.6) * mm, "end": v(240, 69.28) * mm, "construction": true});
            skLineSegment(sketch, "E34.11.3.0", {"start": v(230, 86.6) * mm, "end": v(250, 86.6) * mm, "construction": true});
            skLineSegment(sketch, "E34.11.3.1", {"start": v(240, 103.92) * mm, "end": v(230, 86.6) * mm, "construction": true});
            skLineSegment(sketch, "E34.11.3.2", {"start": v(250, 86.6) * mm, "end": v(240, 103.92) * mm, "construction": true});
            skLineSegment(sketch, "E34.11.3.3", {"start": v(220, 103.92) * mm, "end": v(240, 103.92) * mm, "construction": true});
            skLineSegment(sketch, "E34.11.3.4", {"start": v(230, 86.6) * mm, "end": v(220, 103.92) * mm, "construction": true});
            skLineSegment(sketch, "E34.11.3.5", {"start": v(230, 121.24) * mm, "end": v(220, 103.92) * mm, "construction": true});
            skLineSegment(sketch, "E34.11.3.6", {"start": v(240, 103.92) * mm, "end": v(230, 121.24) * mm, "construction": true});
            skLineSegment(sketch, "E34.11.3.7", {"start": v(230, 121.24) * mm, "end": v(250, 121.24) * mm, "construction": true});
            skLineSegment(sketch, "E34.11.3.8", {"start": v(250, 121.24) * mm, "end": v(240, 103.92) * mm, "construction": true});
            skLineSegment(sketch, "E34.11.4.0", {"start": v(230, 121.24) * mm, "end": v(250, 121.24) * mm, "construction": true});
            skLineSegment(sketch, "E34.11.4.1", {"start": v(240, 138.56) * mm, "end": v(230, 121.24) * mm, "construction": true});
            skLineSegment(sketch, "E34.11.4.2", {"start": v(250, 121.24) * mm, "end": v(240, 138.56) * mm, "construction": true});
            skLineSegment(sketch, "E34.11.4.3", {"start": v(220, 138.56) * mm, "end": v(240, 138.56) * mm, "construction": true});
            skLineSegment(sketch, "E34.11.4.4", {"start": v(230, 121.24) * mm, "end": v(220, 138.56) * mm, "construction": true});
            skLineSegment(sketch, "E34.11.4.5", {"start": v(230, 155.88) * mm, "end": v(220, 138.56) * mm, "construction": true});
            skLineSegment(sketch, "E34.11.4.6", {"start": v(240, 138.56) * mm, "end": v(230, 155.88) * mm, "construction": true});
            skLineSegment(sketch, "E34.11.4.7", {"start": v(230, 155.88) * mm, "end": v(250, 155.88) * mm, "construction": true});
            skLineSegment(sketch, "E34.11.4.8", {"start": v(250, 155.88) * mm, "end": v(240, 138.56) * mm, "construction": true});
            skLineSegment(sketch, "E34.11.5.0", {"start": v(230, 155.88) * mm, "end": v(250, 155.88) * mm, "construction": true});
            skLineSegment(sketch, "E34.11.5.1", {"start": v(240, 173.2) * mm, "end": v(230, 155.88) * mm, "construction": true});
            skLineSegment(sketch, "E34.11.5.2", {"start": v(250, 155.88) * mm, "end": v(240, 173.2) * mm, "construction": true});
            skLineSegment(sketch, "E34.11.5.3", {"start": v(220, 173.2) * mm, "end": v(240, 173.2) * mm, "construction": true});
            skLineSegment(sketch, "E34.11.5.4", {"start": v(230, 155.88) * mm, "end": v(220, 173.2) * mm, "construction": true});
            skLineSegment(sketch, "E34.11.5.5", {"start": v(230, 190.53) * mm, "end": v(220, 173.2) * mm, "construction": true});
            skLineSegment(sketch, "E34.11.5.6", {"start": v(240, 173.2) * mm, "end": v(230, 190.53) * mm, "construction": true});
            skLineSegment(sketch, "E34.11.5.7", {"start": v(230, 190.53) * mm, "end": v(250, 190.53) * mm, "construction": true});
            skLineSegment(sketch, "E34.11.5.8", {"start": v(250, 190.53) * mm, "end": v(240, 173.2) * mm, "construction": true});
            skLineSegment(sketch, "E34.11.6.0", {"start": v(230, 190.53) * mm, "end": v(250, 190.53) * mm, "construction": true});
            skLineSegment(sketch, "E34.11.6.1", {"start": v(240, 207.85) * mm, "end": v(230, 190.53) * mm, "construction": true});
            skLineSegment(sketch, "E34.11.6.2", {"start": v(250, 190.53) * mm, "end": v(240, 207.85) * mm, "construction": true});
            skLineSegment(sketch, "E34.11.6.3", {"start": v(220, 207.85) * mm, "end": v(240, 207.85) * mm, "construction": true});
            skLineSegment(sketch, "E34.11.6.4", {"start": v(230, 190.53) * mm, "end": v(220, 207.85) * mm, "construction": true});
            skLineSegment(sketch, "E34.11.6.5", {"start": v(230, 225.17) * mm, "end": v(220, 207.85) * mm, "construction": true});
            skLineSegment(sketch, "E34.11.6.6", {"start": v(240, 207.85) * mm, "end": v(230, 225.17) * mm, "construction": true});
            skLineSegment(sketch, "E34.11.6.7", {"start": v(230, 225.17) * mm, "end": v(250, 225.17) * mm, "construction": true});
            skLineSegment(sketch, "E34.11.6.8", {"start": v(250, 225.17) * mm, "end": v(240, 207.85) * mm, "construction": true});
            skLineSegment(sketch, "E34.12.0.0", {"start": v(250, -17.32) * mm, "end": v(270, -17.32) * mm, "construction": true});
            skLineSegment(sketch, "E34.12.0.1", {"start": v(260, 0) * mm, "end": v(250, -17.32) * mm, "construction": true});
            skLineSegment(sketch, "E34.12.0.2", {"start": v(270, -17.32) * mm, "end": v(260, 0) * mm, "construction": true});
            skLineSegment(sketch, "E34.12.0.3", {"start": v(240, 0) * mm, "end": v(260, 0) * mm, "construction": true});
            skLineSegment(sketch, "E34.12.0.4", {"start": v(250, -17.32) * mm, "end": v(240, 0) * mm, "construction": true});
            skLineSegment(sketch, "E34.12.0.5", {"start": v(250, 17.32) * mm, "end": v(240, 0) * mm, "construction": true});
            skLineSegment(sketch, "E34.12.0.6", {"start": v(260, 0) * mm, "end": v(250, 17.32) * mm, "construction": true});
            skLineSegment(sketch, "E34.12.0.7", {"start": v(250, 17.32) * mm, "end": v(270, 17.32) * mm, "construction": true});
            skLineSegment(sketch, "E34.12.0.8", {"start": v(270, 17.32) * mm, "end": v(260, 0) * mm, "construction": true});
            skLineSegment(sketch, "E34.12.1.0", {"start": v(250, 17.32) * mm, "end": v(270, 17.32) * mm, "construction": true});
            skLineSegment(sketch, "E34.12.1.1", {"start": v(260, 34.64) * mm, "end": v(250, 17.32) * mm, "construction": true});
            skLineSegment(sketch, "E34.12.1.2", {"start": v(270, 17.32) * mm, "end": v(260, 34.64) * mm, "construction": true});
            skLineSegment(sketch, "E34.12.1.3", {"start": v(240, 34.64) * mm, "end": v(260, 34.64) * mm, "construction": true});
            skLineSegment(sketch, "E34.12.1.4", {"start": v(250, 17.32) * mm, "end": v(240, 34.64) * mm, "construction": true});
            skLineSegment(sketch, "E34.12.1.5", {"start": v(250, 51.96) * mm, "end": v(240, 34.64) * mm, "construction": true});
            skLineSegment(sketch, "E34.12.1.6", {"start": v(260, 34.64) * mm, "end": v(250, 51.96) * mm, "construction": true});
            skLineSegment(sketch, "E34.12.1.7", {"start": v(250, 51.96) * mm, "end": v(270, 51.96) * mm, "construction": true});
            skLineSegment(sketch, "E34.12.1.8", {"start": v(270, 51.96) * mm, "end": v(260, 34.64) * mm, "construction": true});
            skLineSegment(sketch, "E34.12.2.0", {"start": v(250, 51.96) * mm, "end": v(270, 51.96) * mm, "construction": true});
            skLineSegment(sketch, "E34.12.2.1", {"start": v(260, 69.28) * mm, "end": v(250, 51.96) * mm, "construction": true});
            skLineSegment(sketch, "E34.12.2.2", {"start": v(270, 51.96) * mm, "end": v(260, 69.28) * mm, "construction": true});
            skLineSegment(sketch, "E34.12.2.3", {"start": v(240, 69.28) * mm, "end": v(260, 69.28) * mm, "construction": true});
            skLineSegment(sketch, "E34.12.2.4", {"start": v(250, 51.96) * mm, "end": v(240, 69.28) * mm, "construction": true});
            skLineSegment(sketch, "E34.12.2.5", {"start": v(250, 86.6) * mm, "end": v(240, 69.28) * mm, "construction": true});
            skLineSegment(sketch, "E34.12.2.6", {"start": v(260, 69.28) * mm, "end": v(250, 86.6) * mm, "construction": true});
            skLineSegment(sketch, "E34.12.2.7", {"start": v(250, 86.6) * mm, "end": v(270, 86.6) * mm, "construction": true});
            skLineSegment(sketch, "E34.12.2.8", {"start": v(270, 86.6) * mm, "end": v(260, 69.28) * mm, "construction": true});
            skLineSegment(sketch, "E34.12.3.0", {"start": v(250, 86.6) * mm, "end": v(270, 86.6) * mm, "construction": true});
            skLineSegment(sketch, "E34.12.3.1", {"start": v(260, 103.92) * mm, "end": v(250, 86.6) * mm, "construction": true});
            skLineSegment(sketch, "E34.12.3.2", {"start": v(270, 86.6) * mm, "end": v(260, 103.92) * mm, "construction": true});
            skLineSegment(sketch, "E34.12.3.3", {"start": v(240, 103.92) * mm, "end": v(260, 103.92) * mm, "construction": true});
            skLineSegment(sketch, "E34.12.3.4", {"start": v(250, 86.6) * mm, "end": v(240, 103.92) * mm, "construction": true});
            skLineSegment(sketch, "E34.12.3.5", {"start": v(250, 121.24) * mm, "end": v(240, 103.92) * mm, "construction": true});
            skLineSegment(sketch, "E34.12.3.6", {"start": v(260, 103.92) * mm, "end": v(250, 121.24) * mm, "construction": true});
            skLineSegment(sketch, "E34.12.3.7", {"start": v(250, 121.24) * mm, "end": v(270, 121.24) * mm, "construction": true});
            skLineSegment(sketch, "E34.12.3.8", {"start": v(270, 121.24) * mm, "end": v(260, 103.92) * mm, "construction": true});
            skLineSegment(sketch, "E34.12.4.0", {"start": v(250, 121.24) * mm, "end": v(270, 121.24) * mm, "construction": true});
            skLineSegment(sketch, "E34.12.4.1", {"start": v(260, 138.56) * mm, "end": v(250, 121.24) * mm, "construction": true});
            skLineSegment(sketch, "E34.12.4.2", {"start": v(270, 121.24) * mm, "end": v(260, 138.56) * mm, "construction": true});
            skLineSegment(sketch, "E34.12.4.3", {"start": v(240, 138.56) * mm, "end": v(260, 138.56) * mm, "construction": true});
            skLineSegment(sketch, "E34.12.4.4", {"start": v(250, 121.24) * mm, "end": v(240, 138.56) * mm, "construction": true});
            skLineSegment(sketch, "E34.12.4.5", {"start": v(250, 155.88) * mm, "end": v(240, 138.56) * mm, "construction": true});
            skLineSegment(sketch, "E34.12.4.6", {"start": v(260, 138.56) * mm, "end": v(250, 155.88) * mm, "construction": true});
            skLineSegment(sketch, "E34.12.4.7", {"start": v(250, 155.88) * mm, "end": v(270, 155.88) * mm, "construction": true});
            skLineSegment(sketch, "E34.12.4.8", {"start": v(270, 155.88) * mm, "end": v(260, 138.56) * mm, "construction": true});
            skLineSegment(sketch, "E34.12.5.0", {"start": v(250, 155.88) * mm, "end": v(270, 155.88) * mm, "construction": true});
            skLineSegment(sketch, "E34.12.5.1", {"start": v(260, 173.2) * mm, "end": v(250, 155.88) * mm, "construction": true});
            skLineSegment(sketch, "E34.12.5.2", {"start": v(270, 155.88) * mm, "end": v(260, 173.2) * mm, "construction": true});
            skLineSegment(sketch, "E34.12.5.3", {"start": v(240, 173.2) * mm, "end": v(260, 173.2) * mm, "construction": true});
            skLineSegment(sketch, "E34.12.5.4", {"start": v(250, 155.88) * mm, "end": v(240, 173.2) * mm, "construction": true});
            skLineSegment(sketch, "E34.12.5.5", {"start": v(250, 190.53) * mm, "end": v(240, 173.2) * mm, "construction": true});
            skLineSegment(sketch, "E34.12.5.6", {"start": v(260, 173.2) * mm, "end": v(250, 190.53) * mm, "construction": true});
            skLineSegment(sketch, "E34.12.5.7", {"start": v(250, 190.53) * mm, "end": v(270, 190.53) * mm, "construction": true});
            skLineSegment(sketch, "E34.12.5.8", {"start": v(270, 190.53) * mm, "end": v(260, 173.2) * mm, "construction": true});
            skLineSegment(sketch, "E34.12.6.0", {"start": v(250, 190.53) * mm, "end": v(270, 190.53) * mm, "construction": true});
            skLineSegment(sketch, "E34.12.6.1", {"start": v(260, 207.85) * mm, "end": v(250, 190.53) * mm, "construction": true});
            skLineSegment(sketch, "E34.12.6.2", {"start": v(270, 190.53) * mm, "end": v(260, 207.85) * mm, "construction": true});
            skLineSegment(sketch, "E34.12.6.3", {"start": v(240, 207.85) * mm, "end": v(260, 207.85) * mm, "construction": true});
            skLineSegment(sketch, "E34.12.6.4", {"start": v(250, 190.53) * mm, "end": v(240, 207.85) * mm, "construction": true});
            skLineSegment(sketch, "E34.12.6.5", {"start": v(250, 225.17) * mm, "end": v(240, 207.85) * mm, "construction": true});
            skLineSegment(sketch, "E34.12.6.6", {"start": v(260, 207.85) * mm, "end": v(250, 225.17) * mm, "construction": true});
            skLineSegment(sketch, "E34.12.6.7", {"start": v(250, 225.17) * mm, "end": v(270, 225.17) * mm, "construction": true});
            skLineSegment(sketch, "E34.12.6.8", {"start": v(270, 225.17) * mm, "end": v(260, 207.85) * mm, "construction": true});
            skLineSegment(sketch, "E34.13.0.0", {"start": v(270, -17.32) * mm, "end": v(290, -17.32) * mm, "construction": true});
            skLineSegment(sketch, "E34.13.0.1", {"start": v(280, 0) * mm, "end": v(270, -17.32) * mm, "construction": true});
            skLineSegment(sketch, "E34.13.0.2", {"start": v(290, -17.32) * mm, "end": v(280, 0) * mm, "construction": true});
            skLineSegment(sketch, "E34.13.0.3", {"start": v(260, 0) * mm, "end": v(280, 0) * mm, "construction": true});
            skLineSegment(sketch, "E34.13.0.4", {"start": v(270, -17.32) * mm, "end": v(260, 0) * mm, "construction": true});
            skLineSegment(sketch, "E34.13.0.5", {"start": v(270, 17.32) * mm, "end": v(260, 0) * mm, "construction": true});
            skLineSegment(sketch, "E34.13.0.6", {"start": v(280, 0) * mm, "end": v(270, 17.32) * mm, "construction": true});
            skLineSegment(sketch, "E34.13.0.7", {"start": v(270, 17.32) * mm, "end": v(290, 17.32) * mm, "construction": true});
            skLineSegment(sketch, "E34.13.0.8", {"start": v(290, 17.32) * mm, "end": v(280, 0) * mm, "construction": true});
            skLineSegment(sketch, "E34.13.1.0", {"start": v(270, 17.32) * mm, "end": v(290, 17.32) * mm, "construction": true});
            skLineSegment(sketch, "E34.13.1.1", {"start": v(280, 34.64) * mm, "end": v(270, 17.32) * mm, "construction": true});
            skLineSegment(sketch, "E34.13.1.2", {"start": v(290, 17.32) * mm, "end": v(280, 34.64) * mm, "construction": true});
            skLineSegment(sketch, "E34.13.1.3", {"start": v(260, 34.64) * mm, "end": v(280, 34.64) * mm, "construction": true});
            skLineSegment(sketch, "E34.13.1.4", {"start": v(270, 17.32) * mm, "end": v(260, 34.64) * mm, "construction": true});
            skLineSegment(sketch, "E34.13.1.5", {"start": v(270, 51.96) * mm, "end": v(260, 34.64) * mm, "construction": true});
            skLineSegment(sketch, "E34.13.1.6", {"start": v(280, 34.64) * mm, "end": v(270, 51.96) * mm, "construction": true});
            skLineSegment(sketch, "E34.13.1.7", {"start": v(270, 51.96) * mm, "end": v(290, 51.96) * mm, "construction": true});
            skLineSegment(sketch, "E34.13.1.8", {"start": v(290, 51.96) * mm, "end": v(280, 34.64) * mm, "construction": true});
            skLineSegment(sketch, "E34.13.2.0", {"start": v(270, 51.96) * mm, "end": v(290, 51.96) * mm, "construction": true});
            skLineSegment(sketch, "E34.13.2.1", {"start": v(280, 69.28) * mm, "end": v(270, 51.96) * mm, "construction": true});
            skLineSegment(sketch, "E34.13.2.2", {"start": v(290, 51.96) * mm, "end": v(280, 69.28) * mm, "construction": true});
            skLineSegment(sketch, "E34.13.2.3", {"start": v(260, 69.28) * mm, "end": v(280, 69.28) * mm, "construction": true});
            skLineSegment(sketch, "E34.13.2.4", {"start": v(270, 51.96) * mm, "end": v(260, 69.28) * mm, "construction": true});
            skLineSegment(sketch, "E34.13.2.5", {"start": v(270, 86.6) * mm, "end": v(260, 69.28) * mm, "construction": true});
            skLineSegment(sketch, "E34.13.2.6", {"start": v(280, 69.28) * mm, "end": v(270, 86.6) * mm, "construction": true});
            skLineSegment(sketch, "E34.13.2.7", {"start": v(270, 86.6) * mm, "end": v(290, 86.6) * mm, "construction": true});
            skLineSegment(sketch, "E34.13.2.8", {"start": v(290, 86.6) * mm, "end": v(280, 69.28) * mm, "construction": true});
            skLineSegment(sketch, "E34.13.3.0", {"start": v(270, 86.6) * mm, "end": v(290, 86.6) * mm, "construction": true});
            skLineSegment(sketch, "E34.13.3.1", {"start": v(280, 103.92) * mm, "end": v(270, 86.6) * mm, "construction": true});
            skLineSegment(sketch, "E34.13.3.2", {"start": v(290, 86.6) * mm, "end": v(280, 103.92) * mm, "construction": true});
            skLineSegment(sketch, "E34.13.3.3", {"start": v(260, 103.92) * mm, "end": v(280, 103.92) * mm, "construction": true});
            skLineSegment(sketch, "E34.13.3.4", {"start": v(270, 86.6) * mm, "end": v(260, 103.92) * mm, "construction": true});
            skLineSegment(sketch, "E34.13.3.5", {"start": v(270, 121.24) * mm, "end": v(260, 103.92) * mm, "construction": true});
            skLineSegment(sketch, "E34.13.3.6", {"start": v(280, 103.92) * mm, "end": v(270, 121.24) * mm, "construction": true});
            skLineSegment(sketch, "E34.13.3.7", {"start": v(270, 121.24) * mm, "end": v(290, 121.24) * mm, "construction": true});
            skLineSegment(sketch, "E34.13.3.8", {"start": v(290, 121.24) * mm, "end": v(280, 103.92) * mm, "construction": true});
            skLineSegment(sketch, "E34.13.4.0", {"start": v(270, 121.24) * mm, "end": v(290, 121.24) * mm, "construction": true});
            skLineSegment(sketch, "E34.13.4.1", {"start": v(280, 138.56) * mm, "end": v(270, 121.24) * mm, "construction": true});
            skLineSegment(sketch, "E34.13.4.2", {"start": v(290, 121.24) * mm, "end": v(280, 138.56) * mm, "construction": true});
            skLineSegment(sketch, "E34.13.4.3", {"start": v(260, 138.56) * mm, "end": v(280, 138.56) * mm, "construction": true});
            skLineSegment(sketch, "E34.13.4.4", {"start": v(270, 121.24) * mm, "end": v(260, 138.56) * mm, "construction": true});
            skLineSegment(sketch, "E34.13.4.5", {"start": v(270, 155.88) * mm, "end": v(260, 138.56) * mm, "construction": true});
            skLineSegment(sketch, "E34.13.4.6", {"start": v(280, 138.56) * mm, "end": v(270, 155.88) * mm, "construction": true});
            skLineSegment(sketch, "E34.13.4.7", {"start": v(270, 155.88) * mm, "end": v(290, 155.88) * mm, "construction": true});
            skLineSegment(sketch, "E34.13.4.8", {"start": v(290, 155.88) * mm, "end": v(280, 138.56) * mm, "construction": true});
            skLineSegment(sketch, "E34.13.5.0", {"start": v(270, 155.88) * mm, "end": v(290, 155.88) * mm, "construction": true});
            skLineSegment(sketch, "E34.13.5.1", {"start": v(280, 173.2) * mm, "end": v(270, 155.88) * mm, "construction": true});
            skLineSegment(sketch, "E34.13.5.2", {"start": v(290, 155.88) * mm, "end": v(280, 173.2) * mm, "construction": true});
            skLineSegment(sketch, "E34.13.5.3", {"start": v(260, 173.2) * mm, "end": v(280, 173.2) * mm, "construction": true});
            skLineSegment(sketch, "E34.13.5.4", {"start": v(270, 155.88) * mm, "end": v(260, 173.2) * mm, "construction": true});
            skLineSegment(sketch, "E34.13.5.5", {"start": v(270, 190.53) * mm, "end": v(260, 173.2) * mm, "construction": true});
            skLineSegment(sketch, "E34.13.5.6", {"start": v(280, 173.2) * mm, "end": v(270, 190.53) * mm, "construction": true});
            skLineSegment(sketch, "E34.13.5.7", {"start": v(270, 190.53) * mm, "end": v(290, 190.53) * mm, "construction": true});
            skLineSegment(sketch, "E34.13.5.8", {"start": v(290, 190.53) * mm, "end": v(280, 173.2) * mm, "construction": true});
            skLineSegment(sketch, "E34.13.6.0", {"start": v(270, 190.53) * mm, "end": v(290, 190.53) * mm, "construction": true});
            skLineSegment(sketch, "E34.13.6.1", {"start": v(280, 207.85) * mm, "end": v(270, 190.53) * mm, "construction": true});
            skLineSegment(sketch, "E34.13.6.2", {"start": v(290, 190.53) * mm, "end": v(280, 207.85) * mm, "construction": true});
            skLineSegment(sketch, "E34.13.6.3", {"start": v(260, 207.85) * mm, "end": v(280, 207.85) * mm, "construction": true});
            skLineSegment(sketch, "E34.13.6.4", {"start": v(270, 190.53) * mm, "end": v(260, 207.85) * mm, "construction": true});
            skLineSegment(sketch, "E34.13.6.5", {"start": v(270, 225.17) * mm, "end": v(260, 207.85) * mm, "construction": true});
            skLineSegment(sketch, "E34.13.6.6", {"start": v(280, 207.85) * mm, "end": v(270, 225.17) * mm, "construction": true});
            skLineSegment(sketch, "E34.13.6.7", {"start": v(270, 225.17) * mm, "end": v(290, 225.17) * mm, "construction": true});
            skLineSegment(sketch, "E34.13.6.8", {"start": v(290, 225.17) * mm, "end": v(280, 207.85) * mm, "construction": true});
            skLineSegment(sketch, "E34.direction2", {"start": v(10, -17.32) * mm, "end": v(10, 17.32) * mm, "construction": true});
            skLineSegment(sketch, "E35.bottom", {"start": v(-70, -44.58) * mm, "end": v(350, -44.58) * mm});
            skLineSegment(sketch, "E35.top", {"start": v(-70, 252.42) * mm, "end": v(350, 252.42) * mm});
            skLineSegment(sketch, "E35.left", {"start": v(-70, -44.58) * mm, "end": v(-70, 252.42) * mm});
            skLineSegment(sketch, "E35.right", {"start": v(350, -44.58) * mm, "end": v(350, 252.42) * mm});
            skPoint(sketch, "E35.middle", {"position": v(140, 103.92) * mm});
            skPoint(sketch, "E36.middle", {"position": v(-149.88, -103.44) * mm});
            skCircle(sketch, "E37", {"center": v(270, 86.6) * mm, "radius": 1.5 * mm});
            skCircle(sketch, "E38", {"center": v(250, 51.96) * mm, "radius": 1.5 * mm});
            skCircle(sketch, "E39", {"center": v(230, 17.32) * mm, "radius": 1.5 * mm});
            skCircle(sketch, "E40", {"center": v(180, 0) * mm, "radius": 1.5 * mm});
            skCircle(sketch, "E41", {"center": v(100, 0) * mm, "radius": 1.5 * mm});
            skCircle(sketch, "E42", {"center": v(50, 17.32) * mm, "radius": 1.5 * mm});
            skCircle(sketch, "E43", {"center": v(80, 34.64) * mm, "radius": 1.5 * mm});
            skCircle(sketch, "E44", {"center": v(40, 69.28) * mm, "radius": 1.5 * mm});
            skCircle(sketch, "E45", {"center": v(20, 103.92) * mm, "radius": 1.5 * mm});
            skCircle(sketch, "E46", {"center": v(20, 138.56) * mm, "radius": 1.5 * mm});
            skCircle(sketch, "E47", {"center": v(20, 173.2) * mm, "radius": 1.5 * mm});
            skCircle(sketch, "E48", {"center": v(30, 190.53) * mm, "radius": 1.5 * mm});
            skCircle(sketch, "E49", {"center": v(70, 190.53) * mm, "radius": 1.5 * mm});
            skCircle(sketch, "E50", {"center": v(90, 155.88) * mm, "radius": 1.5 * mm});
            skCircle(sketch, "E51", {"center": v(60, 138.56) * mm, "radius": 1.5 * mm});
            skCircle(sketch, "E52", {"center": v(60, 103.92) * mm, "radius": 1.5 * mm});
            skCircle(sketch, "E53", {"center": v(80, 69.28) * mm, "radius": 1.5 * mm});
            skCircle(sketch, "E54", {"center": v(130, 17.32) * mm, "radius": 1.5 * mm});
            skCircle(sketch, "E55", {"center": v(160, 34.64) * mm, "radius": 1.5 * mm});
            skCircle(sketch, "E56", {"center": v(130, 51.96) * mm, "radius": 1.5 * mm});
            skCircle(sketch, "E57", {"center": v(130, 86.6) * mm, "radius": 1.5 * mm});
            skCircle(sketch, "E58", {"center": v(130, 121.24) * mm, "radius": 1.5 * mm});
            skCircle(sketch, "E59", {"center": v(130, 155.88) * mm, "radius": 1.5 * mm});
            skCircle(sketch, "E60", {"center": v(110, 190.53) * mm, "radius": 1.5 * mm});
            skCircle(sketch, "E61", {"center": v(90, 121.24) * mm, "radius": 1.5 * mm});
            skCircle(sketch, "E62", {"center": v(200, 34.64) * mm, "radius": 1.5 * mm});
            skCircle(sketch, "E63", {"center": v(200, 69.28) * mm, "radius": 1.5 * mm});
            skCircle(sketch, "E64", {"center": v(220, 103.92) * mm, "radius": 1.5 * mm});
            skCircle(sketch, "E65", {"center": v(170, 86.6) * mm, "radius": 1.5 * mm});
            skCircle(sketch, "E66", {"center": v(170, 121.24) * mm, "radius": 1.5 * mm});
            skCircle(sketch, "E67", {"center": v(200, 138.56) * mm, "radius": 1.5 * mm});
            skCircle(sketch, "E68", {"center": v(250, 121.24) * mm, "radius": 1.5 * mm});
            skCircle(sketch, "E69", {"center": v(230, 155.88) * mm, "radius": 1.5 * mm});
            skCircle(sketch, "E70", {"center": v(200, 173.2) * mm, "radius": 1.5 * mm});
            skCircle(sketch, "E71", {"center": v(160, 173.2) * mm, "radius": 1.5 * mm});
            skSolve(sketch);
        }
        {
            var Q0;
            Q0=makeQuery(id+"F2.imprint","IMPRINT",FACE,{"disambiguationData":[TD([[makeQuery(id+"F2.imprint","IMPRINT",EDGE,{"derivedFrom":sQuery(id+"F2.wireOp",EDGE,"E42")}),1.0]])]});
            var Q1;
            Q1=makeQuery(id+"F2.imprint","IMPRINT",FACE,{"disambiguationData":[TD([[makeQuery(id+"F2.imprint","IMPRINT",EDGE,{"derivedFrom":sQuery(id+"F2.wireOp",EDGE,"E41")}),1.0]])]});
            var Q2;
            Q2=makeQuery(id+"F2.imprint","IMPRINT",FACE,{"disambiguationData":[TD([[makeQuery(id+"F2.imprint","IMPRINT",EDGE,{"derivedFrom":sQuery(id+"F2.wireOp",EDGE,"E54")}),1.0]])]});
            var Q3;
            Q3=makeQuery(id+"F2.imprint","IMPRINT",FACE,{"disambiguationData":[TD([[makeQuery(id+"F2.imprint","IMPRINT",EDGE,{"derivedFrom":sQuery(id+"F2.wireOp",EDGE,"E43")}),1.0]])]});
            var Q4;
            Q4=makeQuery(id+"F2.imprint","IMPRINT",FACE,{"disambiguationData":[TD([[makeQuery(id+"F2.imprint","IMPRINT",EDGE,{"derivedFrom":sQuery(id+"F2.wireOp",EDGE,"E53")}),1.0]])]});
            var Q5;
            Q5=makeQuery(id+"F2.imprint","IMPRINT",FACE,{"disambiguationData":[TD([[makeQuery(id+"F2.imprint","IMPRINT",EDGE,{"derivedFrom":sQuery(id+"F2.wireOp",EDGE,"E44")}),1.0]])]});
            var Q6;
            Q6=makeQuery(id+"F2.imprint","IMPRINT",FACE,{"disambiguationData":[TD([[makeQuery(id+"F2.imprint","IMPRINT",EDGE,{"derivedFrom":sQuery(id+"F2.wireOp",EDGE,"E56")}),1.0]])]});
            var Q7;
            Q7=makeQuery(id+"F2.imprint","IMPRINT",FACE,{"disambiguationData":[TD([[makeQuery(id+"F2.imprint","IMPRINT",EDGE,{"derivedFrom":sQuery(id+"F2.wireOp",EDGE,"E40")}),1.0]])]});
            var Q8;
            Q8=makeQuery(id+"F2.imprint","IMPRINT",FACE,{"disambiguationData":[TD([[makeQuery(id+"F2.imprint","IMPRINT",EDGE,{"derivedFrom":sQuery(id+"F2.wireOp",EDGE,"E62")}),1.0]])]});
            var Q9;
            Q9=makeQuery(id+"F2.imprint","IMPRINT",FACE,{"disambiguationData":[TD([[makeQuery(id+"F2.imprint","IMPRINT",EDGE,{"derivedFrom":sQuery(id+"F2.wireOp",EDGE,"E55")}),1.0]])]});
            var Q10;
            Q10=makeQuery(id+"F2.imprint","IMPRINT",FACE,{"disambiguationData":[TD([[makeQuery(id+"F2.imprint","IMPRINT",EDGE,{"derivedFrom":sQuery(id+"F2.wireOp",EDGE,"E39")}),1.0]])]});
            var Q11;
            Q11=makeQuery(id+"F2.imprint","IMPRINT",FACE,{"disambiguationData":[TD([[makeQuery(id+"F2.imprint","IMPRINT",EDGE,{"derivedFrom":sQuery(id+"F2.wireOp",EDGE,"E38")}),1.0]])]});
            var Q12;
            Q12=makeQuery(id+"F2.imprint","IMPRINT",FACE,{"disambiguationData":[TD([[makeQuery(id+"F2.imprint","IMPRINT",EDGE,{"derivedFrom":sQuery(id+"F2.wireOp",EDGE,"E37")}),1.0]])]});
            var Q13;
            Q13=makeQuery(id+"F2.imprint","IMPRINT",FACE,{"disambiguationData":[TD([[makeQuery(id+"F2.imprint","IMPRINT",EDGE,{"derivedFrom":sQuery(id+"F2.wireOp",EDGE,"E63")}),1.0]])]});
            var Q14;
            Q14=makeQuery(id+"F2.imprint","IMPRINT",FACE,{"disambiguationData":[TD([[makeQuery(id+"F2.imprint","IMPRINT",EDGE,{"derivedFrom":sQuery(id+"F2.wireOp",EDGE,"E65")}),1.0]])]});
            var Q15;
            Q15=makeQuery(id+"F2.imprint","IMPRINT",FACE,{"disambiguationData":[TD([[makeQuery(id+"F2.imprint","IMPRINT",EDGE,{"derivedFrom":sQuery(id+"F2.wireOp",EDGE,"E57")}),1.0]])]});
            var Q16;
            Q16=makeQuery(id+"F2.imprint","IMPRINT",FACE,{"disambiguationData":[TD([[makeQuery(id+"F2.imprint","IMPRINT",EDGE,{"derivedFrom":sQuery(id+"F2.wireOp",EDGE,"E52")}),1.0]])]});
            var Q17;
            Q17=makeQuery(id+"F2.imprint","IMPRINT",FACE,{"disambiguationData":[TD([[makeQuery(id+"F2.imprint","IMPRINT",EDGE,{"derivedFrom":sQuery(id+"F2.wireOp",EDGE,"E45")}),1.0]])]});
            var Q18;
            Q18=makeQuery(id+"F2.imprint","IMPRINT",FACE,{"disambiguationData":[TD([[makeQuery(id+"F2.imprint","IMPRINT",EDGE,{"derivedFrom":sQuery(id+"F2.wireOp",EDGE,"E61")}),1.0]])]});
            var Q19;
            Q19=makeQuery(id+"F2.imprint","IMPRINT",FACE,{"disambiguationData":[TD([[makeQuery(id+"F2.imprint","IMPRINT",EDGE,{"derivedFrom":sQuery(id+"F2.wireOp",EDGE,"E58")}),1.0]])]});
            var Q20;
            Q20=makeQuery(id+"F2.imprint","IMPRINT",FACE,{"disambiguationData":[TD([[makeQuery(id+"F2.imprint","IMPRINT",EDGE,{"derivedFrom":sQuery(id+"F2.wireOp",EDGE,"E66")}),1.0]])]});
            var Q21;
            Q21=makeQuery(id+"F2.imprint","IMPRINT",FACE,{"disambiguationData":[TD([[makeQuery(id+"F2.imprint","IMPRINT",EDGE,{"derivedFrom":sQuery(id+"F2.wireOp",EDGE,"E64")}),1.0]])]});
            var Q22;
            Q22=makeQuery(id+"F2.imprint","IMPRINT",FACE,{"disambiguationData":[TD([[makeQuery(id+"F2.imprint","IMPRINT",EDGE,{"derivedFrom":sQuery(id+"F2.wireOp",EDGE,"E68")}),1.0]])]});
            var Q23;
            Q23=makeQuery(id+"F2.imprint","IMPRINT",FACE,{"disambiguationData":[TD([[makeQuery(id+"F2.imprint","IMPRINT",EDGE,{"derivedFrom":sQuery(id+"F2.wireOp",EDGE,"E69")}),1.0]])]});
            var Q24;
            Q24=makeQuery(id+"F2.imprint","IMPRINT",FACE,{"disambiguationData":[TD([[makeQuery(id+"F2.imprint","IMPRINT",EDGE,{"derivedFrom":sQuery(id+"F2.wireOp",EDGE,"E67")}),1.0]])]});
            var Q25;
            Q25=makeQuery(id+"F2.imprint","IMPRINT",FACE,{"disambiguationData":[TD([[makeQuery(id+"F2.imprint","IMPRINT",EDGE,{"derivedFrom":sQuery(id+"F2.wireOp",EDGE,"E59")}),1.0]])]});
            var Q26;
            Q26=makeQuery(id+"F2.imprint","IMPRINT",FACE,{"disambiguationData":[TD([[makeQuery(id+"F2.imprint","IMPRINT",EDGE,{"derivedFrom":sQuery(id+"F2.wireOp",EDGE,"E50")}),1.0]])]});
            var Q27;
            Q27=makeQuery(id+"F2.imprint","IMPRINT",FACE,{"disambiguationData":[TD([[makeQuery(id+"F2.imprint","IMPRINT",EDGE,{"derivedFrom":sQuery(id+"F2.wireOp",EDGE,"E51")}),1.0]])]});
            var Q28;
            Q28=makeQuery(id+"F2.imprint","IMPRINT",FACE,{"disambiguationData":[TD([[makeQuery(id+"F2.imprint","IMPRINT",EDGE,{"derivedFrom":sQuery(id+"F2.wireOp",EDGE,"E46")}),1.0]])]});
            var Q29;
            Q29=makeQuery(id+"F2.imprint","IMPRINT",FACE,{"disambiguationData":[TD([[makeQuery(id+"F2.imprint","IMPRINT",EDGE,{"derivedFrom":sQuery(id+"F2.wireOp",EDGE,"E48")}),1.0]])]});
            var Q30;
            Q30=makeQuery(id+"F2.imprint","IMPRINT",FACE,{"disambiguationData":[TD([[makeQuery(id+"F2.imprint","IMPRINT",EDGE,{"derivedFrom":sQuery(id+"F2.wireOp",EDGE,"E47")}),1.0]])]});
            var Q31;
            Q31=makeQuery(id+"F2.imprint","IMPRINT",FACE,{"disambiguationData":[TD([[makeQuery(id+"F2.imprint","IMPRINT",EDGE,{"derivedFrom":sQuery(id+"F2.wireOp",EDGE,"E49")}),1.0]])]});
            var Q32;
            Q32=makeQuery(id+"F2.imprint","IMPRINT",FACE,{"disambiguationData":[TD([[makeQuery(id+"F2.imprint","IMPRINT",EDGE,{"derivedFrom":sQuery(id+"F2.wireOp",EDGE,"E60")}),1.0]])]});
            var Q33;
            Q33=makeQuery(id+"F2.imprint","IMPRINT",FACE,{"disambiguationData":[TD([[makeQuery(id+"F2.imprint","IMPRINT",EDGE,{"derivedFrom":sQuery(id+"F2.wireOp",EDGE,"E71")}),1.0]])]});
            var Q34;
            Q34=makeQuery(id+"F2.imprint","IMPRINT",FACE,{"disambiguationData":[TD([[makeQuery(id+"F2.imprint","IMPRINT",EDGE,{"derivedFrom":sQuery(id+"F2.wireOp",EDGE,"E70")}),1.0]])]});
            extrude(context, id + "F3", {"entities" : qUnion([Q0, Q1, Q2, Q3, Q4, Q5, Q6, Q7, Q8, Q9, Q10, Q11, Q12, Q13, Q14, Q15, Q16, Q17, Q18, Q19, Q20, Q21, Q22, Q23, Q24, Q25, Q26, Q27, Q28, Q29, Q30, Q31, Q32, Q33, Q34]), "depth" : 6 * mm, "offsetDistance" : 25 * mm});
        }
    });
